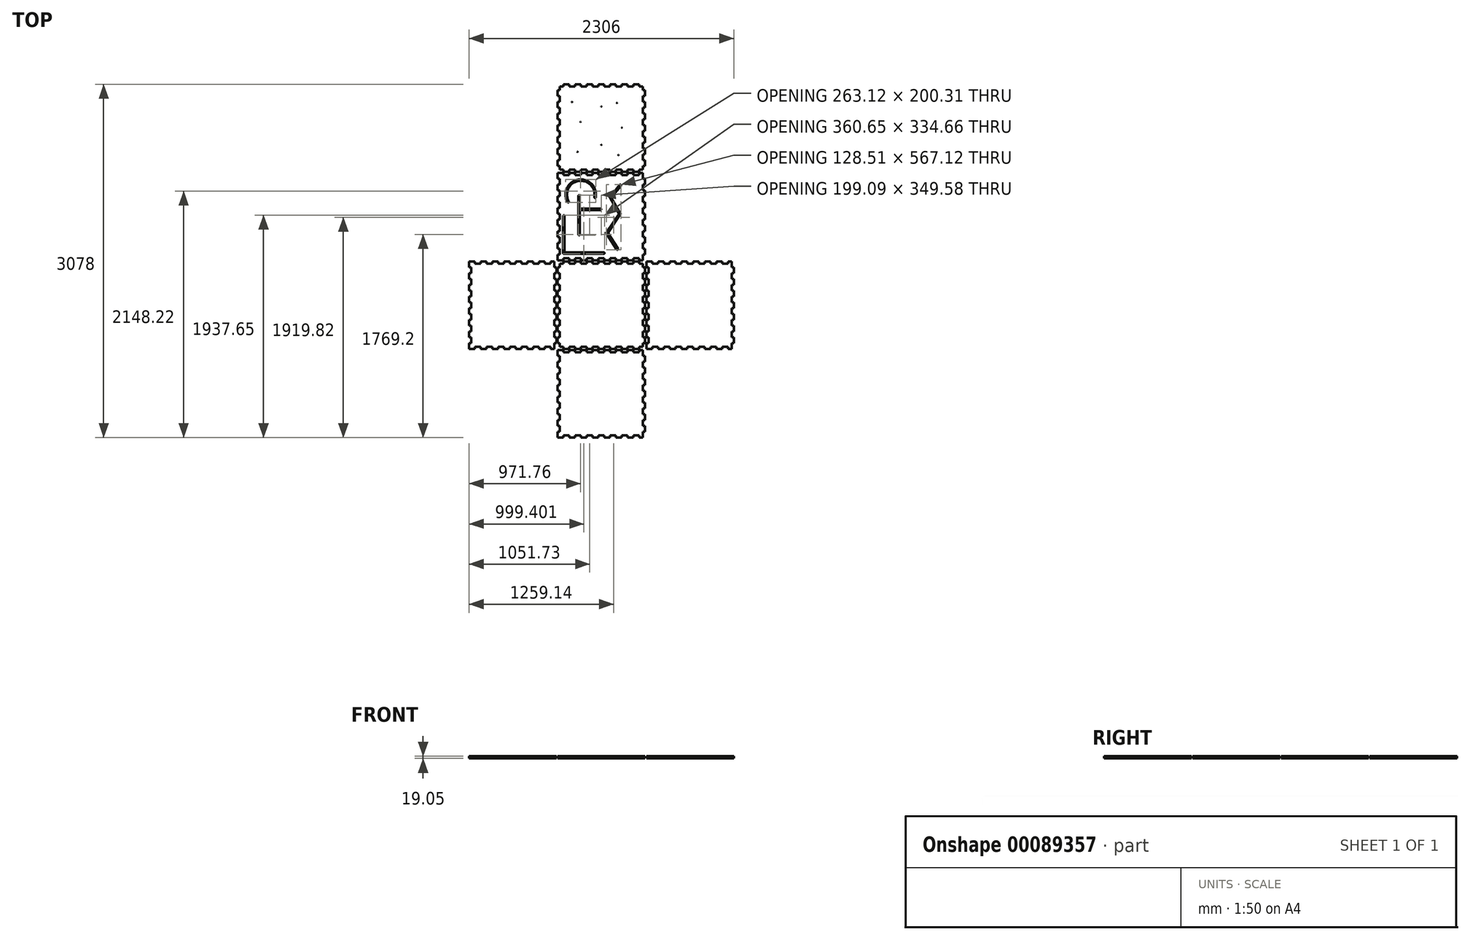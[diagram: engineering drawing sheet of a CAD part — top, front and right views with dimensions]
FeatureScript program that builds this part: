
annotation { "Feature Type Name" : "Feature", "Feature Type Description" : "" }
export const myFeature = defineFeature(function(context is Context, id is Id, definition is map)
    precondition{}
    {
        {
            var Q0;
            Q0=qCreatedBy(makeId("Top.planeOp"),FACE);
            var sketch = newSketch(context, id + "F0", { "sketchPlane" : qUnion([Q0])});
            skLineSegment(sketch, "E0", {"start": v(-381, -1539) * mm, "end": v(-330.2, -1539) * mm});
            skLineSegment(sketch, "E1", {"start": v(-330.2, -1519.95) * mm, "end": v(-330.2, -1539) * mm});
            skLineSegment(sketch, "E2", {"start": v(-330.2, -1519.95) * mm, "end": v(-279.4, -1519.95) * mm});
            skLineSegment(sketch, "E3", {"start": v(-279.4, -1519.95) * mm, "end": v(-279.4, -1539) * mm});
            skLineSegment(sketch, "E4", {"start": v(-279.4, -1539) * mm, "end": v(-228.6, -1539) * mm});
            skLineSegment(sketch, "E5", {"start": v(-228.6, -1519.95) * mm, "end": v(-228.6, -1539) * mm});
            skLineSegment(sketch, "E6", {"start": v(-228.6, -1519.95) * mm, "end": v(-177.8, -1519.95) * mm});
            skLineSegment(sketch, "E7", {"start": v(-177.8, -1519.95) * mm, "end": v(-177.8, -1539) * mm});
            skLineSegment(sketch, "E8", {"start": v(-177.8, -1539) * mm, "end": v(-127, -1539) * mm});
            skLineSegment(sketch, "E9", {"start": v(-127, -1519.95) * mm, "end": v(-127, -1539) * mm});
            skLineSegment(sketch, "E10", {"start": v(-127, -1519.95) * mm, "end": v(-76.2, -1519.95) * mm});
            skLineSegment(sketch, "E11", {"start": v(-76.2, -1519.95) * mm, "end": v(-76.2, -1539) * mm});
            skLineSegment(sketch, "E12", {"start": v(-76.2, -1539) * mm, "end": v(-25.4, -1539) * mm});
            skLineSegment(sketch, "E13", {"start": v(-25.4, -1519.95) * mm, "end": v(-25.4, -1539) * mm});
            skLineSegment(sketch, "E14", {"start": v(-25.4, -1519.95) * mm, "end": v(25.4, -1519.95) * mm});
            skLineSegment(sketch, "E15", {"start": v(25.4, -1519.95) * mm, "end": v(25.4, -1539) * mm});
            skLineSegment(sketch, "E16", {"start": v(25.4, -1539) * mm, "end": v(76.2, -1539) * mm});
            skLineSegment(sketch, "E17", {"start": v(76.2, -1519.95) * mm, "end": v(76.2, -1539) * mm});
            skLineSegment(sketch, "E18", {"start": v(76.2, -1519.95) * mm, "end": v(127, -1519.95) * mm});
            skLineSegment(sketch, "E19", {"start": v(127, -1519.95) * mm, "end": v(127, -1539) * mm});
            skLineSegment(sketch, "E20", {"start": v(127, -1539) * mm, "end": v(177.8, -1539) * mm});
            skLineSegment(sketch, "E21", {"start": v(177.8, -1519.95) * mm, "end": v(177.8, -1539) * mm});
            skLineSegment(sketch, "E22", {"start": v(177.8, -1519.95) * mm, "end": v(228.6, -1519.95) * mm});
            skLineSegment(sketch, "E23", {"start": v(228.6, -1519.95) * mm, "end": v(228.6, -1539) * mm});
            skLineSegment(sketch, "E24", {"start": v(228.6, -1539) * mm, "end": v(279.4, -1539) * mm});
            skLineSegment(sketch, "E25", {"start": v(279.4, -1519.95) * mm, "end": v(279.4, -1539) * mm});
            skLineSegment(sketch, "E26", {"start": v(279.4, -1519.95) * mm, "end": v(330.2, -1519.95) * mm});
            skLineSegment(sketch, "E27", {"start": v(330.2, -1519.95) * mm, "end": v(330.2, -1539) * mm});
            skLineSegment(sketch, "E28", {"start": v(330.2, -1539) * mm, "end": v(361.95, -1539) * mm});
            skLineSegment(sketch, "E29", {"start": v(-381, -777) * mm, "end": v(-330.2, -777) * mm});
            skLineSegment(sketch, "E30", {"start": v(-330.2, -777) * mm, "end": v(-330.2, -796.05) * mm});
            skLineSegment(sketch, "E31", {"start": v(-330.2, -796.05) * mm, "end": v(-279.4, -796.05) * mm});
            skLineSegment(sketch, "E32", {"start": v(-279.4, -777) * mm, "end": v(-279.4, -796.05) * mm});
            skLineSegment(sketch, "E33", {"start": v(-279.4, -777) * mm, "end": v(-228.6, -777) * mm});
            skLineSegment(sketch, "E34", {"start": v(-228.6, -777) * mm, "end": v(-228.6, -796.05) * mm});
            skLineSegment(sketch, "E35", {"start": v(-228.6, -796.05) * mm, "end": v(-177.8, -796.05) * mm});
            skLineSegment(sketch, "E36", {"start": v(-177.8, -777) * mm, "end": v(-177.8, -796.05) * mm});
            skLineSegment(sketch, "E37", {"start": v(-177.8, -777) * mm, "end": v(-127, -777) * mm});
            skLineSegment(sketch, "E38", {"start": v(-127, -777) * mm, "end": v(-127, -796.05) * mm});
            skLineSegment(sketch, "E39", {"start": v(-127, -796.05) * mm, "end": v(-76.2, -796.05) * mm});
            skLineSegment(sketch, "E40", {"start": v(-76.2, -777) * mm, "end": v(-76.2, -796.05) * mm});
            skLineSegment(sketch, "E41", {"start": v(-76.2, -777) * mm, "end": v(-25.4, -777) * mm});
            skLineSegment(sketch, "E42", {"start": v(-25.4, -777) * mm, "end": v(-25.4, -796.05) * mm});
            skLineSegment(sketch, "E43", {"start": v(-25.4, -796.05) * mm, "end": v(25.4, -796.05) * mm});
            skLineSegment(sketch, "E44", {"start": v(25.4, -777) * mm, "end": v(25.4, -796.05) * mm});
            skLineSegment(sketch, "E45", {"start": v(25.4, -777) * mm, "end": v(76.2, -777) * mm});
            skLineSegment(sketch, "E46", {"start": v(76.2, -777) * mm, "end": v(76.2, -796.05) * mm});
            skLineSegment(sketch, "E47", {"start": v(76.2, -796.05) * mm, "end": v(127, -796.05) * mm});
            skLineSegment(sketch, "E48", {"start": v(127, -777) * mm, "end": v(127, -796.05) * mm});
            skLineSegment(sketch, "E49", {"start": v(127, -777) * mm, "end": v(177.8, -777) * mm});
            skLineSegment(sketch, "E50", {"start": v(177.8, -777) * mm, "end": v(177.8, -796.05) * mm});
            skLineSegment(sketch, "E51", {"start": v(177.8, -796.05) * mm, "end": v(228.6, -796.05) * mm});
            skLineSegment(sketch, "E52", {"start": v(228.6, -777) * mm, "end": v(228.6, -796.05) * mm});
            skLineSegment(sketch, "E53", {"start": v(228.6, -777) * mm, "end": v(279.4, -777) * mm});
            skLineSegment(sketch, "E54", {"start": v(279.4, -777) * mm, "end": v(279.4, -796.05) * mm});
            skLineSegment(sketch, "E55", {"start": v(279.4, -796.05) * mm, "end": v(330.2, -796.05) * mm});
            skLineSegment(sketch, "E56", {"start": v(330.2, -777) * mm, "end": v(330.2, -796.05) * mm});
            skLineSegment(sketch, "E57", {"start": v(330.2, -777) * mm, "end": v(361.95, -777) * mm});
            skLineSegment(sketch, "E58", {"start": v(-381, -1539) * mm, "end": v(-381, -1488.2) * mm});
            skLineSegment(sketch, "E59", {"start": v(-361.95, -1488.2) * mm, "end": v(-381, -1488.2) * mm});
            skLineSegment(sketch, "E60", {"start": v(-361.95, -1488.2) * mm, "end": v(-361.95, -1437.4) * mm});
            skLineSegment(sketch, "E61", {"start": v(-361.95, -1437.4) * mm, "end": v(-381, -1437.4) * mm});
            skLineSegment(sketch, "E62", {"start": v(-381, -1437.4) * mm, "end": v(-381, -1386.6) * mm});
            skLineSegment(sketch, "E63", {"start": v(-361.95, -1386.6) * mm, "end": v(-381, -1386.6) * mm});
            skLineSegment(sketch, "E64", {"start": v(-361.95, -1386.6) * mm, "end": v(-361.95, -1335.8) * mm});
            skLineSegment(sketch, "E65", {"start": v(-361.95, -1335.8) * mm, "end": v(-381, -1335.8) * mm});
            skLineSegment(sketch, "E66", {"start": v(-381, -1335.8) * mm, "end": v(-381, -1285) * mm});
            skLineSegment(sketch, "E67", {"start": v(-361.95, -1285) * mm, "end": v(-381, -1285) * mm});
            skLineSegment(sketch, "E68", {"start": v(-361.95, -1285) * mm, "end": v(-361.95, -1234.2) * mm});
            skLineSegment(sketch, "E69", {"start": v(-361.95, -1234.2) * mm, "end": v(-381, -1234.2) * mm});
            skLineSegment(sketch, "E70", {"start": v(-381, -1234.2) * mm, "end": v(-381, -1183.4) * mm});
            skLineSegment(sketch, "E71", {"start": v(-361.95, -1183.4) * mm, "end": v(-381, -1183.4) * mm});
            skLineSegment(sketch, "E72", {"start": v(-361.95, -1183.4) * mm, "end": v(-361.95, -1132.6) * mm});
            skLineSegment(sketch, "E73", {"start": v(-361.95, -1132.6) * mm, "end": v(-381, -1132.6) * mm});
            skLineSegment(sketch, "E74", {"start": v(-381, -1132.6) * mm, "end": v(-381, -1081.8) * mm});
            skLineSegment(sketch, "E75", {"start": v(-361.95, -1081.8) * mm, "end": v(-381, -1081.8) * mm});
            skLineSegment(sketch, "E76", {"start": v(-361.95, -1081.8) * mm, "end": v(-361.95, -1031) * mm});
            skLineSegment(sketch, "E77", {"start": v(-361.95, -1031) * mm, "end": v(-381, -1031) * mm});
            skLineSegment(sketch, "E78", {"start": v(-381, -1031) * mm, "end": v(-381, -980.2) * mm});
            skLineSegment(sketch, "E79", {"start": v(-361.95, -980.2) * mm, "end": v(-381, -980.2) * mm});
            skLineSegment(sketch, "E80", {"start": v(-361.95, -980.2) * mm, "end": v(-361.95, -929.4) * mm});
            skLineSegment(sketch, "E81", {"start": v(-361.95, -929.4) * mm, "end": v(-381, -929.4) * mm});
            skLineSegment(sketch, "E82", {"start": v(-381, -929.4) * mm, "end": v(-381, -878.6) * mm});
            skLineSegment(sketch, "E83", {"start": v(-361.95, -878.6) * mm, "end": v(-381, -878.6) * mm});
            skLineSegment(sketch, "E84", {"start": v(-361.95, -878.6) * mm, "end": v(-361.95, -827.8) * mm});
            skLineSegment(sketch, "E85", {"start": v(-361.95, -827.8) * mm, "end": v(-381, -827.8) * mm});
            skLineSegment(sketch, "E86", {"start": v(-381, -827.8) * mm, "end": v(-381, -777) * mm});
            skLineSegment(sketch, "E87", {"start": v(361.95, -1539) * mm, "end": v(361.95, -1488.2) * mm});
            skLineSegment(sketch, "E88", {"start": v(381, -1488.2) * mm, "end": v(361.95, -1488.2) * mm});
            skLineSegment(sketch, "E89", {"start": v(381, -1488.2) * mm, "end": v(381, -1437.4) * mm});
            skLineSegment(sketch, "E90", {"start": v(381, -1437.4) * mm, "end": v(361.95, -1437.4) * mm});
            skLineSegment(sketch, "E91", {"start": v(361.95, -1437.4) * mm, "end": v(361.95, -1386.6) * mm});
            skLineSegment(sketch, "E92", {"start": v(381, -1386.6) * mm, "end": v(361.95, -1386.6) * mm});
            skLineSegment(sketch, "E93", {"start": v(381, -1386.6) * mm, "end": v(381, -1335.8) * mm});
            skLineSegment(sketch, "E94", {"start": v(381, -1335.8) * mm, "end": v(361.95, -1335.8) * mm});
            skLineSegment(sketch, "E95", {"start": v(361.95, -1335.8) * mm, "end": v(361.95, -1285) * mm});
            skLineSegment(sketch, "E96", {"start": v(381, -1285) * mm, "end": v(361.95, -1285) * mm});
            skLineSegment(sketch, "E97", {"start": v(381, -1285) * mm, "end": v(381, -1234.2) * mm});
            skLineSegment(sketch, "E98", {"start": v(381, -1234.2) * mm, "end": v(361.95, -1234.2) * mm});
            skLineSegment(sketch, "E99", {"start": v(361.95, -1234.2) * mm, "end": v(361.95, -1183.4) * mm});
            skLineSegment(sketch, "E100", {"start": v(381, -1183.4) * mm, "end": v(361.95, -1183.4) * mm});
            skLineSegment(sketch, "E101", {"start": v(381, -1183.4) * mm, "end": v(381, -1132.6) * mm});
            skLineSegment(sketch, "E102", {"start": v(381, -1132.6) * mm, "end": v(361.95, -1132.6) * mm});
            skLineSegment(sketch, "E103", {"start": v(361.95, -1132.6) * mm, "end": v(361.95, -1081.8) * mm});
            skLineSegment(sketch, "E104", {"start": v(381, -1081.8) * mm, "end": v(361.95, -1081.8) * mm});
            skLineSegment(sketch, "E105", {"start": v(381, -1081.8) * mm, "end": v(381, -1031) * mm});
            skLineSegment(sketch, "E106", {"start": v(381, -1031) * mm, "end": v(361.95, -1031) * mm});
            skLineSegment(sketch, "E107", {"start": v(361.95, -1031) * mm, "end": v(361.95, -980.2) * mm});
            skLineSegment(sketch, "E108", {"start": v(381, -980.2) * mm, "end": v(361.95, -980.2) * mm});
            skLineSegment(sketch, "E109", {"start": v(381, -980.2) * mm, "end": v(381, -929.4) * mm});
            skLineSegment(sketch, "E110", {"start": v(381, -929.4) * mm, "end": v(361.95, -929.4) * mm});
            skLineSegment(sketch, "E111", {"start": v(361.95, -929.4) * mm, "end": v(361.95, -878.6) * mm});
            skLineSegment(sketch, "E112", {"start": v(381, -878.6) * mm, "end": v(361.95, -878.6) * mm});
            skLineSegment(sketch, "E113", {"start": v(381, -878.6) * mm, "end": v(381, -827.8) * mm});
            skLineSegment(sketch, "E114", {"start": v(381, -827.8) * mm, "end": v(361.95, -827.8) * mm});
            skLineSegment(sketch, "E115", {"start": v(361.95, -827.8) * mm, "end": v(361.95, -777) * mm});
            skLineSegment(sketch, "E116", {"start": v(-1153, -767) * mm, "end": v(-1102.2, -767) * mm});
            skLineSegment(sketch, "E117", {"start": v(-1102.2, -747.95) * mm, "end": v(-1102.2, -767) * mm});
            skLineSegment(sketch, "E118", {"start": v(-1102.2, -747.95) * mm, "end": v(-1051.4, -747.95) * mm});
            skLineSegment(sketch, "E119", {"start": v(-1051.4, -747.95) * mm, "end": v(-1051.4, -767) * mm});
            skLineSegment(sketch, "E120", {"start": v(-1051.4, -767) * mm, "end": v(-1000.6, -767) * mm});
            skLineSegment(sketch, "E121", {"start": v(-1000.6, -747.95) * mm, "end": v(-1000.6, -767) * mm});
            skLineSegment(sketch, "E122", {"start": v(-1000.6, -747.95) * mm, "end": v(-949.8, -747.95) * mm});
            skLineSegment(sketch, "E123", {"start": v(-949.8, -747.95) * mm, "end": v(-949.8, -767) * mm});
            skLineSegment(sketch, "E124", {"start": v(-949.8, -767) * mm, "end": v(-899, -767) * mm});
            skLineSegment(sketch, "E125", {"start": v(-899, -747.95) * mm, "end": v(-899, -767) * mm});
            skLineSegment(sketch, "E126", {"start": v(-899, -747.95) * mm, "end": v(-848.2, -747.95) * mm});
            skLineSegment(sketch, "E127", {"start": v(-848.2, -747.95) * mm, "end": v(-848.2, -767) * mm});
            skLineSegment(sketch, "E128", {"start": v(-848.2, -767) * mm, "end": v(-797.4, -767) * mm});
            skLineSegment(sketch, "E129", {"start": v(-797.4, -747.95) * mm, "end": v(-797.4, -767) * mm});
            skLineSegment(sketch, "E130", {"start": v(-797.4, -747.95) * mm, "end": v(-746.6, -747.95) * mm});
            skLineSegment(sketch, "E131", {"start": v(-746.6, -747.95) * mm, "end": v(-746.6, -767) * mm});
            skLineSegment(sketch, "E132", {"start": v(-746.6, -767) * mm, "end": v(-695.8, -767) * mm});
            skLineSegment(sketch, "E133", {"start": v(-695.8, -747.95) * mm, "end": v(-695.8, -767) * mm});
            skLineSegment(sketch, "E134", {"start": v(-695.8, -747.95) * mm, "end": v(-645, -747.95) * mm});
            skLineSegment(sketch, "E135", {"start": v(-645, -747.95) * mm, "end": v(-645, -767) * mm});
            skLineSegment(sketch, "E136", {"start": v(-645, -767) * mm, "end": v(-594.2, -767) * mm});
            skLineSegment(sketch, "E137", {"start": v(-594.2, -747.95) * mm, "end": v(-594.2, -767) * mm});
            skLineSegment(sketch, "E138", {"start": v(-594.2, -747.95) * mm, "end": v(-543.4, -747.95) * mm});
            skLineSegment(sketch, "E139", {"start": v(-543.4, -747.95) * mm, "end": v(-543.4, -767) * mm});
            skLineSegment(sketch, "E140", {"start": v(-543.4, -767) * mm, "end": v(-492.6, -767) * mm});
            skLineSegment(sketch, "E141", {"start": v(-492.6, -747.95) * mm, "end": v(-492.6, -767) * mm});
            skLineSegment(sketch, "E142", {"start": v(-492.6, -747.95) * mm, "end": v(-441.8, -747.95) * mm});
            skLineSegment(sketch, "E143", {"start": v(-441.8, -747.95) * mm, "end": v(-441.8, -767) * mm});
            skLineSegment(sketch, "E144", {"start": v(-441.8, -767) * mm, "end": v(-410.05, -767) * mm});
            skLineSegment(sketch, "E145", {"start": v(-1153, -5) * mm, "end": v(-1102.2, -5) * mm});
            skLineSegment(sketch, "E146", {"start": v(-1102.2, -5) * mm, "end": v(-1102.2, -24.05) * mm});
            skLineSegment(sketch, "E147", {"start": v(-1102.2, -24.05) * mm, "end": v(-1051.4, -24.05) * mm});
            skLineSegment(sketch, "E148", {"start": v(-1051.4, -5) * mm, "end": v(-1051.4, -24.05) * mm});
            skLineSegment(sketch, "E149", {"start": v(-1051.4, -5) * mm, "end": v(-1000.6, -5) * mm});
            skLineSegment(sketch, "E150", {"start": v(-1000.6, -5) * mm, "end": v(-1000.6, -24.05) * mm});
            skLineSegment(sketch, "E151", {"start": v(-1000.6, -24.05) * mm, "end": v(-949.8, -24.05) * mm});
            skLineSegment(sketch, "E152", {"start": v(-949.8, -5) * mm, "end": v(-949.8, -24.05) * mm});
            skLineSegment(sketch, "E153", {"start": v(-949.8, -5) * mm, "end": v(-899, -5) * mm});
            skLineSegment(sketch, "E154", {"start": v(-899, -5) * mm, "end": v(-899, -24.05) * mm});
            skLineSegment(sketch, "E155", {"start": v(-899, -24.05) * mm, "end": v(-848.2, -24.05) * mm});
            skLineSegment(sketch, "E156", {"start": v(-848.2, -5) * mm, "end": v(-848.2, -24.05) * mm});
            skLineSegment(sketch, "E157", {"start": v(-848.2, -5) * mm, "end": v(-797.4, -5) * mm});
            skLineSegment(sketch, "E158", {"start": v(-797.4, -5) * mm, "end": v(-797.4, -24.05) * mm});
            skLineSegment(sketch, "E159", {"start": v(-797.4, -24.05) * mm, "end": v(-746.6, -24.05) * mm});
            skLineSegment(sketch, "E160", {"start": v(-746.6, -5) * mm, "end": v(-746.6, -24.05) * mm});
            skLineSegment(sketch, "E161", {"start": v(-746.6, -5) * mm, "end": v(-695.8, -5) * mm});
            skLineSegment(sketch, "E162", {"start": v(-695.8, -5) * mm, "end": v(-695.8, -24.05) * mm});
            skLineSegment(sketch, "E163", {"start": v(-695.8, -24.05) * mm, "end": v(-645, -24.05) * mm});
            skLineSegment(sketch, "E164", {"start": v(-645, -5) * mm, "end": v(-645, -24.05) * mm});
            skLineSegment(sketch, "E165", {"start": v(-645, -5) * mm, "end": v(-594.2, -5) * mm});
            skLineSegment(sketch, "E166", {"start": v(-594.2, -5) * mm, "end": v(-594.2, -24.05) * mm});
            skLineSegment(sketch, "E167", {"start": v(-594.2, -24.05) * mm, "end": v(-543.4, -24.05) * mm});
            skLineSegment(sketch, "E168", {"start": v(-543.4, -5) * mm, "end": v(-543.4, -24.05) * mm});
            skLineSegment(sketch, "E169", {"start": v(-543.4, -5) * mm, "end": v(-492.6, -5) * mm});
            skLineSegment(sketch, "E170", {"start": v(-492.6, -5) * mm, "end": v(-492.6, -24.05) * mm});
            skLineSegment(sketch, "E171", {"start": v(-492.6, -24.05) * mm, "end": v(-441.8, -24.05) * mm});
            skLineSegment(sketch, "E172", {"start": v(-441.8, -5) * mm, "end": v(-441.8, -24.05) * mm});
            skLineSegment(sketch, "E173", {"start": v(-441.8, -5) * mm, "end": v(-410.05, -5) * mm});
            skLineSegment(sketch, "E174", {"start": v(-1153, -767) * mm, "end": v(-1153, -716.2) * mm});
            skLineSegment(sketch, "E175", {"start": v(-1133.95, -716.2) * mm, "end": v(-1153, -716.2) * mm});
            skLineSegment(sketch, "E176", {"start": v(-1133.95, -716.2) * mm, "end": v(-1133.95, -665.4) * mm});
            skLineSegment(sketch, "E177", {"start": v(-1133.95, -665.4) * mm, "end": v(-1153, -665.4) * mm});
            skLineSegment(sketch, "E178", {"start": v(-1153, -665.4) * mm, "end": v(-1153, -614.6) * mm});
            skLineSegment(sketch, "E179", {"start": v(-1133.95, -614.6) * mm, "end": v(-1153, -614.6) * mm});
            skLineSegment(sketch, "E180", {"start": v(-1133.95, -614.6) * mm, "end": v(-1133.95, -563.8) * mm});
            skLineSegment(sketch, "E181", {"start": v(-1133.95, -563.8) * mm, "end": v(-1153, -563.8) * mm});
            skLineSegment(sketch, "E182", {"start": v(-1153, -563.8) * mm, "end": v(-1153, -513) * mm});
            skLineSegment(sketch, "E183", {"start": v(-1133.95, -513) * mm, "end": v(-1153, -513) * mm});
            skLineSegment(sketch, "E184", {"start": v(-1133.95, -513) * mm, "end": v(-1133.95, -462.2) * mm});
            skLineSegment(sketch, "E185", {"start": v(-1133.95, -462.2) * mm, "end": v(-1153, -462.2) * mm});
            skLineSegment(sketch, "E186", {"start": v(-1153, -462.2) * mm, "end": v(-1153, -411.4) * mm});
            skLineSegment(sketch, "E187", {"start": v(-1133.95, -411.4) * mm, "end": v(-1153, -411.4) * mm});
            skLineSegment(sketch, "E188", {"start": v(-1133.95, -411.4) * mm, "end": v(-1133.95, -360.6) * mm});
            skLineSegment(sketch, "E189", {"start": v(-1133.95, -360.6) * mm, "end": v(-1153, -360.6) * mm});
            skLineSegment(sketch, "E190", {"start": v(-1153, -360.6) * mm, "end": v(-1153, -309.8) * mm});
            skLineSegment(sketch, "E191", {"start": v(-1133.95, -309.8) * mm, "end": v(-1153, -309.8) * mm});
            skLineSegment(sketch, "E192", {"start": v(-1133.95, -309.8) * mm, "end": v(-1133.95, -259) * mm});
            skLineSegment(sketch, "E193", {"start": v(-1133.95, -259) * mm, "end": v(-1153, -259) * mm});
            skLineSegment(sketch, "E194", {"start": v(-1153, -259) * mm, "end": v(-1153, -208.2) * mm});
            skLineSegment(sketch, "E195", {"start": v(-1133.95, -208.2) * mm, "end": v(-1153, -208.2) * mm});
            skLineSegment(sketch, "E196", {"start": v(-1133.95, -208.2) * mm, "end": v(-1133.95, -157.4) * mm});
            skLineSegment(sketch, "E197", {"start": v(-1133.95, -157.4) * mm, "end": v(-1153, -157.4) * mm});
            skLineSegment(sketch, "E198", {"start": v(-1153, -157.4) * mm, "end": v(-1153, -106.6) * mm});
            skLineSegment(sketch, "E199", {"start": v(-1133.95, -106.6) * mm, "end": v(-1153, -106.6) * mm});
            skLineSegment(sketch, "E200", {"start": v(-1133.95, -106.6) * mm, "end": v(-1133.95, -55.8) * mm});
            skLineSegment(sketch, "E201", {"start": v(-1133.95, -55.8) * mm, "end": v(-1153, -55.8) * mm});
            skLineSegment(sketch, "E202", {"start": v(-1153, -55.8) * mm, "end": v(-1153, -5) * mm});
            skLineSegment(sketch, "E203", {"start": v(-410.05, -767) * mm, "end": v(-410.05, -716.2) * mm});
            skLineSegment(sketch, "E204", {"start": v(-391, -716.2) * mm, "end": v(-410.05, -716.2) * mm});
            skLineSegment(sketch, "E205", {"start": v(-391, -716.2) * mm, "end": v(-391, -665.4) * mm});
            skLineSegment(sketch, "E206", {"start": v(-391, -665.4) * mm, "end": v(-410.05, -665.4) * mm});
            skLineSegment(sketch, "E207", {"start": v(-410.05, -665.4) * mm, "end": v(-410.05, -614.6) * mm});
            skLineSegment(sketch, "E208", {"start": v(-391, -614.6) * mm, "end": v(-410.05, -614.6) * mm});
            skLineSegment(sketch, "E209", {"start": v(-391, -614.6) * mm, "end": v(-391, -563.8) * mm});
            skLineSegment(sketch, "E210", {"start": v(-391, -563.8) * mm, "end": v(-410.05, -563.8) * mm});
            skLineSegment(sketch, "E211", {"start": v(-410.05, -563.8) * mm, "end": v(-410.05, -513) * mm});
            skLineSegment(sketch, "E212", {"start": v(-391, -513) * mm, "end": v(-410.05, -513) * mm});
            skLineSegment(sketch, "E213", {"start": v(-391, -513) * mm, "end": v(-391, -462.2) * mm});
            skLineSegment(sketch, "E214", {"start": v(-391, -462.2) * mm, "end": v(-410.05, -462.2) * mm});
            skLineSegment(sketch, "E215", {"start": v(-410.05, -462.2) * mm, "end": v(-410.05, -411.4) * mm});
            skLineSegment(sketch, "E216", {"start": v(-391, -411.4) * mm, "end": v(-410.05, -411.4) * mm});
            skLineSegment(sketch, "E217", {"start": v(-391, -411.4) * mm, "end": v(-391, -360.6) * mm});
            skLineSegment(sketch, "E218", {"start": v(-391, -360.6) * mm, "end": v(-410.05, -360.6) * mm});
            skLineSegment(sketch, "E219", {"start": v(-410.05, -360.6) * mm, "end": v(-410.05, -309.8) * mm});
            skLineSegment(sketch, "E220", {"start": v(-391, -309.8) * mm, "end": v(-410.05, -309.8) * mm});
            skLineSegment(sketch, "E221", {"start": v(-391, -309.8) * mm, "end": v(-391, -259) * mm});
            skLineSegment(sketch, "E222", {"start": v(-391, -259) * mm, "end": v(-410.05, -259) * mm});
            skLineSegment(sketch, "E223", {"start": v(-410.05, -259) * mm, "end": v(-410.05, -208.2) * mm});
            skLineSegment(sketch, "E224", {"start": v(-391, -208.2) * mm, "end": v(-410.05, -208.2) * mm});
            skLineSegment(sketch, "E225", {"start": v(-391, -208.2) * mm, "end": v(-391, -157.4) * mm});
            skLineSegment(sketch, "E226", {"start": v(-391, -157.4) * mm, "end": v(-410.05, -157.4) * mm});
            skLineSegment(sketch, "E227", {"start": v(-410.05, -157.4) * mm, "end": v(-410.05, -106.6) * mm});
            skLineSegment(sketch, "E228", {"start": v(-391, -106.6) * mm, "end": v(-410.05, -106.6) * mm});
            skLineSegment(sketch, "E229", {"start": v(-391, -106.6) * mm, "end": v(-391, -55.8) * mm});
            skLineSegment(sketch, "E230", {"start": v(-391, -55.8) * mm, "end": v(-410.05, -55.8) * mm});
            skLineSegment(sketch, "E231", {"start": v(-410.05, -55.8) * mm, "end": v(-410.05, -5) * mm});
            skLineSegment(sketch, "E232", {"start": v(-361.95, -747.95) * mm, "end": v(-330.2, -747.95) * mm});
            skLineSegment(sketch, "E233", {"start": v(-330.2, -747.95) * mm, "end": v(-330.2, -767) * mm});
            skLineSegment(sketch, "E234", {"start": v(-330.2, -767) * mm, "end": v(-279.4, -767) * mm});
            skLineSegment(sketch, "E235", {"start": v(-279.4, -747.95) * mm, "end": v(-279.4, -767) * mm});
            skLineSegment(sketch, "E236", {"start": v(-279.4, -747.95) * mm, "end": v(-228.6, -747.95) * mm});
            skLineSegment(sketch, "E237", {"start": v(-228.6, -747.95) * mm, "end": v(-228.6, -767) * mm});
            skLineSegment(sketch, "E238", {"start": v(-228.6, -767) * mm, "end": v(-177.8, -767) * mm});
            skLineSegment(sketch, "E239", {"start": v(-177.8, -747.95) * mm, "end": v(-177.8, -767) * mm});
            skLineSegment(sketch, "E240", {"start": v(-177.8, -747.95) * mm, "end": v(-127, -747.95) * mm});
            skLineSegment(sketch, "E241", {"start": v(-127, -747.95) * mm, "end": v(-127, -767) * mm});
            skLineSegment(sketch, "E242", {"start": v(-127, -767) * mm, "end": v(-76.2, -767) * mm});
            skLineSegment(sketch, "E243", {"start": v(-76.2, -747.95) * mm, "end": v(-76.2, -767) * mm});
            skLineSegment(sketch, "E244", {"start": v(-76.2, -747.95) * mm, "end": v(-25.4, -747.95) * mm});
            skLineSegment(sketch, "E245", {"start": v(-25.4, -747.95) * mm, "end": v(-25.4, -767) * mm});
            skLineSegment(sketch, "E246", {"start": v(-25.4, -767) * mm, "end": v(25.4, -767) * mm});
            skLineSegment(sketch, "E247", {"start": v(25.4, -747.95) * mm, "end": v(25.4, -767) * mm});
            skLineSegment(sketch, "E248", {"start": v(25.4, -747.95) * mm, "end": v(76.2, -747.95) * mm});
            skLineSegment(sketch, "E249", {"start": v(76.2, -747.95) * mm, "end": v(76.2, -767) * mm});
            skLineSegment(sketch, "E250", {"start": v(76.2, -767) * mm, "end": v(127, -767) * mm});
            skLineSegment(sketch, "E251", {"start": v(127, -747.95) * mm, "end": v(127, -767) * mm});
            skLineSegment(sketch, "E252", {"start": v(127, -747.95) * mm, "end": v(177.8, -747.95) * mm});
            skLineSegment(sketch, "E253", {"start": v(177.8, -747.95) * mm, "end": v(177.8, -767) * mm});
            skLineSegment(sketch, "E254", {"start": v(177.8, -767) * mm, "end": v(228.6, -767) * mm});
            skLineSegment(sketch, "E255", {"start": v(228.6, -747.95) * mm, "end": v(228.6, -767) * mm});
            skLineSegment(sketch, "E256", {"start": v(228.6, -747.95) * mm, "end": v(279.4, -747.95) * mm});
            skLineSegment(sketch, "E257", {"start": v(279.4, -747.95) * mm, "end": v(279.4, -767) * mm});
            skLineSegment(sketch, "E258", {"start": v(279.4, -767) * mm, "end": v(330.2, -767) * mm});
            skLineSegment(sketch, "E259", {"start": v(330.2, -747.95) * mm, "end": v(330.2, -767) * mm});
            skLineSegment(sketch, "E260", {"start": v(330.2, -747.95) * mm, "end": v(361.95, -747.95) * mm});
            skLineSegment(sketch, "E261", {"start": v(-361.95, -24.05) * mm, "end": v(-330.2, -24.05) * mm});
            skLineSegment(sketch, "E262", {"start": v(-330.2, -5) * mm, "end": v(-330.2, -24.05) * mm});
            skLineSegment(sketch, "E263", {"start": v(-330.2, -5) * mm, "end": v(-279.4, -5) * mm});
            skLineSegment(sketch, "E264", {"start": v(-279.4, -5) * mm, "end": v(-279.4, -24.05) * mm});
            skLineSegment(sketch, "E265", {"start": v(-279.4, -24.05) * mm, "end": v(-228.6, -24.05) * mm});
            skLineSegment(sketch, "E266", {"start": v(-228.6, -5) * mm, "end": v(-228.6, -24.05) * mm});
            skLineSegment(sketch, "E267", {"start": v(-228.6, -5) * mm, "end": v(-177.8, -5) * mm});
            skLineSegment(sketch, "E268", {"start": v(-177.8, -5) * mm, "end": v(-177.8, -24.05) * mm});
            skLineSegment(sketch, "E269", {"start": v(-177.8, -24.05) * mm, "end": v(-127, -24.05) * mm});
            skLineSegment(sketch, "E270", {"start": v(-127, -5) * mm, "end": v(-127, -24.05) * mm});
            skLineSegment(sketch, "E271", {"start": v(-127, -5) * mm, "end": v(-76.2, -5) * mm});
            skLineSegment(sketch, "E272", {"start": v(-76.2, -5) * mm, "end": v(-76.2, -24.05) * mm});
            skLineSegment(sketch, "E273", {"start": v(-76.2, -24.05) * mm, "end": v(-25.4, -24.05) * mm});
            skLineSegment(sketch, "E274", {"start": v(-25.4, -5) * mm, "end": v(-25.4, -24.05) * mm});
            skLineSegment(sketch, "E275", {"start": v(-25.4, -5) * mm, "end": v(25.4, -5) * mm});
            skLineSegment(sketch, "E276", {"start": v(25.4, -5) * mm, "end": v(25.4, -24.05) * mm});
            skLineSegment(sketch, "E277", {"start": v(25.4, -24.05) * mm, "end": v(76.2, -24.05) * mm});
            skLineSegment(sketch, "E278", {"start": v(76.2, -5) * mm, "end": v(76.2, -24.05) * mm});
            skLineSegment(sketch, "E279", {"start": v(76.2, -5) * mm, "end": v(127, -5) * mm});
            skLineSegment(sketch, "E280", {"start": v(127, -5) * mm, "end": v(127, -24.05) * mm});
            skLineSegment(sketch, "E281", {"start": v(127, -24.05) * mm, "end": v(177.8, -24.05) * mm});
            skLineSegment(sketch, "E282", {"start": v(177.8, -5) * mm, "end": v(177.8, -24.05) * mm});
            skLineSegment(sketch, "E283", {"start": v(177.8, -5) * mm, "end": v(228.6, -5) * mm});
            skLineSegment(sketch, "E284", {"start": v(228.6, -5) * mm, "end": v(228.6, -24.05) * mm});
            skLineSegment(sketch, "E285", {"start": v(228.6, -24.05) * mm, "end": v(279.4, -24.05) * mm});
            skLineSegment(sketch, "E286", {"start": v(279.4, -5) * mm, "end": v(279.4, -24.05) * mm});
            skLineSegment(sketch, "E287", {"start": v(279.4, -5) * mm, "end": v(330.2, -5) * mm});
            skLineSegment(sketch, "E288", {"start": v(330.2, -5) * mm, "end": v(330.2, -24.05) * mm});
            skLineSegment(sketch, "E289", {"start": v(330.2, -24.05) * mm, "end": v(361.95, -24.05) * mm});
            skLineSegment(sketch, "E290", {"start": v(-361.95, -747.95) * mm, "end": v(-361.95, -716.2) * mm});
            skLineSegment(sketch, "E291", {"start": v(-361.95, -716.2) * mm, "end": v(-381, -716.2) * mm});
            skLineSegment(sketch, "E292", {"start": v(-381, -716.2) * mm, "end": v(-381, -665.4) * mm});
            skLineSegment(sketch, "E293", {"start": v(-361.95, -665.4) * mm, "end": v(-381, -665.4) * mm});
            skLineSegment(sketch, "E294", {"start": v(-361.95, -665.4) * mm, "end": v(-361.95, -614.6) * mm});
            skLineSegment(sketch, "E295", {"start": v(-361.95, -614.6) * mm, "end": v(-381, -614.6) * mm});
            skLineSegment(sketch, "E296", {"start": v(-381, -614.6) * mm, "end": v(-381, -563.8) * mm});
            skLineSegment(sketch, "E297", {"start": v(-361.95, -563.8) * mm, "end": v(-381, -563.8) * mm});
            skLineSegment(sketch, "E298", {"start": v(-361.95, -563.8) * mm, "end": v(-361.95, -513) * mm});
            skLineSegment(sketch, "E299", {"start": v(-361.95, -513) * mm, "end": v(-381, -513) * mm});
            skLineSegment(sketch, "E300", {"start": v(-381, -513) * mm, "end": v(-381, -462.2) * mm});
            skLineSegment(sketch, "E301", {"start": v(-361.95, -462.2) * mm, "end": v(-381, -462.2) * mm});
            skLineSegment(sketch, "E302", {"start": v(-361.95, -462.2) * mm, "end": v(-361.95, -411.4) * mm});
            skLineSegment(sketch, "E303", {"start": v(-361.95, -411.4) * mm, "end": v(-381, -411.4) * mm});
            skLineSegment(sketch, "E304", {"start": v(-381, -411.4) * mm, "end": v(-381, -360.6) * mm});
            skLineSegment(sketch, "E305", {"start": v(-361.95, -360.6) * mm, "end": v(-381, -360.6) * mm});
            skLineSegment(sketch, "E306", {"start": v(-361.95, -360.6) * mm, "end": v(-361.95, -309.8) * mm});
            skLineSegment(sketch, "E307", {"start": v(-361.95, -309.8) * mm, "end": v(-381, -309.8) * mm});
            skLineSegment(sketch, "E308", {"start": v(-381, -309.8) * mm, "end": v(-381, -259) * mm});
            skLineSegment(sketch, "E309", {"start": v(-361.95, -259) * mm, "end": v(-381, -259) * mm});
            skLineSegment(sketch, "E310", {"start": v(-361.95, -259) * mm, "end": v(-361.95, -208.2) * mm});
            skLineSegment(sketch, "E311", {"start": v(-361.95, -208.2) * mm, "end": v(-381, -208.2) * mm});
            skLineSegment(sketch, "E312", {"start": v(-381, -208.2) * mm, "end": v(-381, -157.4) * mm});
            skLineSegment(sketch, "E313", {"start": v(-361.95, -157.4) * mm, "end": v(-381, -157.4) * mm});
            skLineSegment(sketch, "E314", {"start": v(-361.95, -157.4) * mm, "end": v(-361.95, -106.6) * mm});
            skLineSegment(sketch, "E315", {"start": v(-361.95, -106.6) * mm, "end": v(-381, -106.6) * mm});
            skLineSegment(sketch, "E316", {"start": v(-381, -106.6) * mm, "end": v(-381, -55.8) * mm});
            skLineSegment(sketch, "E317", {"start": v(-361.95, -55.8) * mm, "end": v(-381, -55.8) * mm});
            skLineSegment(sketch, "E318", {"start": v(-361.95, -55.8) * mm, "end": v(-361.95, -24.05) * mm});
            skLineSegment(sketch, "E319", {"start": v(361.95, -747.95) * mm, "end": v(361.95, -716.2) * mm});
            skLineSegment(sketch, "E320", {"start": v(381, -716.2) * mm, "end": v(361.95, -716.2) * mm});
            skLineSegment(sketch, "E321", {"start": v(381, -716.2) * mm, "end": v(381, -665.4) * mm});
            skLineSegment(sketch, "E322", {"start": v(381, -665.4) * mm, "end": v(361.95, -665.4) * mm});
            skLineSegment(sketch, "E323", {"start": v(361.95, -665.4) * mm, "end": v(361.95, -614.6) * mm});
            skLineSegment(sketch, "E324", {"start": v(381, -614.6) * mm, "end": v(361.95, -614.6) * mm});
            skLineSegment(sketch, "E325", {"start": v(381, -614.6) * mm, "end": v(381, -563.8) * mm});
            skLineSegment(sketch, "E326", {"start": v(381, -563.8) * mm, "end": v(361.95, -563.8) * mm});
            skLineSegment(sketch, "E327", {"start": v(361.95, -563.8) * mm, "end": v(361.95, -513) * mm});
            skLineSegment(sketch, "E328", {"start": v(381, -513) * mm, "end": v(361.95, -513) * mm});
            skLineSegment(sketch, "E329", {"start": v(381, -513) * mm, "end": v(381, -462.2) * mm});
            skLineSegment(sketch, "E330", {"start": v(381, -462.2) * mm, "end": v(361.95, -462.2) * mm});
            skLineSegment(sketch, "E331", {"start": v(361.95, -462.2) * mm, "end": v(361.95, -411.4) * mm});
            skLineSegment(sketch, "E332", {"start": v(381, -411.4) * mm, "end": v(361.95, -411.4) * mm});
            skLineSegment(sketch, "E333", {"start": v(381, -411.4) * mm, "end": v(381, -360.6) * mm});
            skLineSegment(sketch, "E334", {"start": v(381, -360.6) * mm, "end": v(361.95, -360.6) * mm});
            skLineSegment(sketch, "E335", {"start": v(361.95, -360.6) * mm, "end": v(361.95, -309.8) * mm});
            skLineSegment(sketch, "E336", {"start": v(381, -309.8) * mm, "end": v(361.95, -309.8) * mm});
            skLineSegment(sketch, "E337", {"start": v(381, -309.8) * mm, "end": v(381, -259) * mm});
            skLineSegment(sketch, "E338", {"start": v(381, -259) * mm, "end": v(361.95, -259) * mm});
            skLineSegment(sketch, "E339", {"start": v(361.95, -259) * mm, "end": v(361.95, -208.2) * mm});
            skLineSegment(sketch, "E340", {"start": v(381, -208.2) * mm, "end": v(361.95, -208.2) * mm});
            skLineSegment(sketch, "E341", {"start": v(381, -208.2) * mm, "end": v(381, -157.4) * mm});
            skLineSegment(sketch, "E342", {"start": v(381, -157.4) * mm, "end": v(361.95, -157.4) * mm});
            skLineSegment(sketch, "E343", {"start": v(361.95, -157.4) * mm, "end": v(361.95, -106.6) * mm});
            skLineSegment(sketch, "E344", {"start": v(381, -106.6) * mm, "end": v(361.95, -106.6) * mm});
            skLineSegment(sketch, "E345", {"start": v(381, -106.6) * mm, "end": v(381, -55.8) * mm});
            skLineSegment(sketch, "E346", {"start": v(381, -55.8) * mm, "end": v(361.95, -55.8) * mm});
            skLineSegment(sketch, "E347", {"start": v(361.95, -55.8) * mm, "end": v(361.95, -24.05) * mm});
            skLineSegment(sketch, "E348", {"start": v(391, -767) * mm, "end": v(441.8, -767) * mm});
            skLineSegment(sketch, "E349", {"start": v(441.8, -747.95) * mm, "end": v(441.8, -767) * mm});
            skLineSegment(sketch, "E350", {"start": v(441.8, -747.95) * mm, "end": v(492.6, -747.95) * mm});
            skLineSegment(sketch, "E351", {"start": v(492.6, -747.95) * mm, "end": v(492.6, -767) * mm});
            skLineSegment(sketch, "E352", {"start": v(492.6, -767) * mm, "end": v(543.4, -767) * mm});
            skLineSegment(sketch, "E353", {"start": v(543.4, -747.95) * mm, "end": v(543.4, -767) * mm});
            skLineSegment(sketch, "E354", {"start": v(543.4, -747.95) * mm, "end": v(594.2, -747.95) * mm});
            skLineSegment(sketch, "E355", {"start": v(594.2, -747.95) * mm, "end": v(594.2, -767) * mm});
            skLineSegment(sketch, "E356", {"start": v(594.2, -767) * mm, "end": v(645, -767) * mm});
            skLineSegment(sketch, "E357", {"start": v(645, -747.95) * mm, "end": v(645, -767) * mm});
            skLineSegment(sketch, "E358", {"start": v(645, -747.95) * mm, "end": v(695.8, -747.95) * mm});
            skLineSegment(sketch, "E359", {"start": v(695.8, -747.95) * mm, "end": v(695.8, -767) * mm});
            skLineSegment(sketch, "E360", {"start": v(695.8, -767) * mm, "end": v(746.6, -767) * mm});
            skLineSegment(sketch, "E361", {"start": v(746.6, -747.95) * mm, "end": v(746.6, -767) * mm});
            skLineSegment(sketch, "E362", {"start": v(746.6, -747.95) * mm, "end": v(797.4, -747.95) * mm});
            skLineSegment(sketch, "E363", {"start": v(797.4, -747.95) * mm, "end": v(797.4, -767) * mm});
            skLineSegment(sketch, "E364", {"start": v(797.4, -767) * mm, "end": v(848.2, -767) * mm});
            skLineSegment(sketch, "E365", {"start": v(848.2, -747.95) * mm, "end": v(848.2, -767) * mm});
            skLineSegment(sketch, "E366", {"start": v(848.2, -747.95) * mm, "end": v(899, -747.95) * mm});
            skLineSegment(sketch, "E367", {"start": v(899, -747.95) * mm, "end": v(899, -767) * mm});
            skLineSegment(sketch, "E368", {"start": v(899, -767) * mm, "end": v(949.8, -767) * mm});
            skLineSegment(sketch, "E369", {"start": v(949.8, -747.95) * mm, "end": v(949.8, -767) * mm});
            skLineSegment(sketch, "E370", {"start": v(949.8, -747.95) * mm, "end": v(1000.6, -747.95) * mm});
            skLineSegment(sketch, "E371", {"start": v(1000.6, -747.95) * mm, "end": v(1000.6, -767) * mm});
            skLineSegment(sketch, "E372", {"start": v(1000.6, -767) * mm, "end": v(1051.4, -767) * mm});
            skLineSegment(sketch, "E373", {"start": v(1051.4, -747.95) * mm, "end": v(1051.4, -767) * mm});
            skLineSegment(sketch, "E374", {"start": v(1051.4, -747.95) * mm, "end": v(1102.2, -747.95) * mm});
            skLineSegment(sketch, "E375", {"start": v(1102.2, -747.95) * mm, "end": v(1102.2, -767) * mm});
            skLineSegment(sketch, "E376", {"start": v(1102.2, -767) * mm, "end": v(1133.95, -767) * mm});
            skLineSegment(sketch, "E377", {"start": v(391, -5) * mm, "end": v(441.8, -5) * mm});
            skLineSegment(sketch, "E378", {"start": v(441.8, -5) * mm, "end": v(441.8, -24.05) * mm});
            skLineSegment(sketch, "E379", {"start": v(441.8, -24.05) * mm, "end": v(492.6, -24.05) * mm});
            skLineSegment(sketch, "E380", {"start": v(492.6, -5) * mm, "end": v(492.6, -24.05) * mm});
            skLineSegment(sketch, "E381", {"start": v(492.6, -5) * mm, "end": v(543.4, -5) * mm});
            skLineSegment(sketch, "E382", {"start": v(543.4, -5) * mm, "end": v(543.4, -24.05) * mm});
            skLineSegment(sketch, "E383", {"start": v(543.4, -24.05) * mm, "end": v(594.2, -24.05) * mm});
            skLineSegment(sketch, "E384", {"start": v(594.2, -5) * mm, "end": v(594.2, -24.05) * mm});
            skLineSegment(sketch, "E385", {"start": v(594.2, -5) * mm, "end": v(645, -5) * mm});
            skLineSegment(sketch, "E386", {"start": v(645, -5) * mm, "end": v(645, -24.05) * mm});
            skLineSegment(sketch, "E387", {"start": v(645, -24.05) * mm, "end": v(695.8, -24.05) * mm});
            skLineSegment(sketch, "E388", {"start": v(695.8, -5) * mm, "end": v(695.8, -24.05) * mm});
            skLineSegment(sketch, "E389", {"start": v(695.8, -5) * mm, "end": v(746.6, -5) * mm});
            skLineSegment(sketch, "E390", {"start": v(746.6, -5) * mm, "end": v(746.6, -24.05) * mm});
            skLineSegment(sketch, "E391", {"start": v(746.6, -24.05) * mm, "end": v(797.4, -24.05) * mm});
            skLineSegment(sketch, "E392", {"start": v(797.4, -5) * mm, "end": v(797.4, -24.05) * mm});
            skLineSegment(sketch, "E393", {"start": v(797.4, -5) * mm, "end": v(848.2, -5) * mm});
            skLineSegment(sketch, "E394", {"start": v(848.2, -5) * mm, "end": v(848.2, -24.05) * mm});
            skLineSegment(sketch, "E395", {"start": v(848.2, -24.05) * mm, "end": v(899, -24.05) * mm});
            skLineSegment(sketch, "E396", {"start": v(899, -5) * mm, "end": v(899, -24.05) * mm});
            skLineSegment(sketch, "E397", {"start": v(899, -5) * mm, "end": v(949.8, -5) * mm});
            skLineSegment(sketch, "E398", {"start": v(949.8, -5) * mm, "end": v(949.8, -24.05) * mm});
            skLineSegment(sketch, "E399", {"start": v(949.8, -24.05) * mm, "end": v(1000.6, -24.05) * mm});
            skLineSegment(sketch, "E400", {"start": v(1000.6, -5) * mm, "end": v(1000.6, -24.05) * mm});
            skLineSegment(sketch, "E401", {"start": v(1000.6, -5) * mm, "end": v(1051.4, -5) * mm});
            skLineSegment(sketch, "E402", {"start": v(1051.4, -5) * mm, "end": v(1051.4, -24.05) * mm});
            skLineSegment(sketch, "E403", {"start": v(1051.4, -24.05) * mm, "end": v(1102.2, -24.05) * mm});
            skLineSegment(sketch, "E404", {"start": v(1102.2, -5) * mm, "end": v(1102.2, -24.05) * mm});
            skLineSegment(sketch, "E405", {"start": v(1102.2, -5) * mm, "end": v(1133.95, -5) * mm});
            skLineSegment(sketch, "E406", {"start": v(391, -767) * mm, "end": v(391, -716.2) * mm});
            skLineSegment(sketch, "E407", {"start": v(410.05, -716.2) * mm, "end": v(391, -716.2) * mm});
            skLineSegment(sketch, "E408", {"start": v(410.05, -716.2) * mm, "end": v(410.05, -665.4) * mm});
            skLineSegment(sketch, "E409", {"start": v(410.05, -665.4) * mm, "end": v(391, -665.4) * mm});
            skLineSegment(sketch, "E410", {"start": v(391, -665.4) * mm, "end": v(391, -614.6) * mm});
            skLineSegment(sketch, "E411", {"start": v(410.05, -614.6) * mm, "end": v(391, -614.6) * mm});
            skLineSegment(sketch, "E412", {"start": v(410.05, -614.6) * mm, "end": v(410.05, -563.8) * mm});
            skLineSegment(sketch, "E413", {"start": v(410.05, -563.8) * mm, "end": v(391, -563.8) * mm});
            skLineSegment(sketch, "E414", {"start": v(391, -563.8) * mm, "end": v(391, -513) * mm});
            skLineSegment(sketch, "E415", {"start": v(410.05, -513) * mm, "end": v(391, -513) * mm});
            skLineSegment(sketch, "E416", {"start": v(410.05, -513) * mm, "end": v(410.05, -462.2) * mm});
            skLineSegment(sketch, "E417", {"start": v(410.05, -462.2) * mm, "end": v(391, -462.2) * mm});
            skLineSegment(sketch, "E418", {"start": v(391, -462.2) * mm, "end": v(391, -411.4) * mm});
            skLineSegment(sketch, "E419", {"start": v(410.05, -411.4) * mm, "end": v(391, -411.4) * mm});
            skLineSegment(sketch, "E420", {"start": v(410.05, -411.4) * mm, "end": v(410.05, -360.6) * mm});
            skLineSegment(sketch, "E421", {"start": v(410.05, -360.6) * mm, "end": v(391, -360.6) * mm});
            skLineSegment(sketch, "E422", {"start": v(391, -360.6) * mm, "end": v(391, -309.8) * mm});
            skLineSegment(sketch, "E423", {"start": v(410.05, -309.8) * mm, "end": v(391, -309.8) * mm});
            skLineSegment(sketch, "E424", {"start": v(410.05, -309.8) * mm, "end": v(410.05, -259) * mm});
            skLineSegment(sketch, "E425", {"start": v(410.05, -259) * mm, "end": v(391, -259) * mm});
            skLineSegment(sketch, "E426", {"start": v(391, -259) * mm, "end": v(391, -208.2) * mm});
            skLineSegment(sketch, "E427", {"start": v(410.05, -208.2) * mm, "end": v(391, -208.2) * mm});
            skLineSegment(sketch, "E428", {"start": v(410.05, -208.2) * mm, "end": v(410.05, -157.4) * mm});
            skLineSegment(sketch, "E429", {"start": v(410.05, -157.4) * mm, "end": v(391, -157.4) * mm});
            skLineSegment(sketch, "E430", {"start": v(391, -157.4) * mm, "end": v(391, -106.6) * mm});
            skLineSegment(sketch, "E431", {"start": v(410.05, -106.6) * mm, "end": v(391, -106.6) * mm});
            skLineSegment(sketch, "E432", {"start": v(410.05, -106.6) * mm, "end": v(410.05, -55.8) * mm});
            skLineSegment(sketch, "E433", {"start": v(410.05, -55.8) * mm, "end": v(391, -55.8) * mm});
            skLineSegment(sketch, "E434", {"start": v(391, -55.8) * mm, "end": v(391, -5) * mm});
            skLineSegment(sketch, "E435", {"start": v(1133.95, -767) * mm, "end": v(1133.95, -716.2) * mm});
            skLineSegment(sketch, "E436", {"start": v(1153, -716.2) * mm, "end": v(1133.95, -716.2) * mm});
            skLineSegment(sketch, "E437", {"start": v(1153, -716.2) * mm, "end": v(1153, -665.4) * mm});
            skLineSegment(sketch, "E438", {"start": v(1153, -665.4) * mm, "end": v(1133.95, -665.4) * mm});
            skLineSegment(sketch, "E439", {"start": v(1133.95, -665.4) * mm, "end": v(1133.95, -614.6) * mm});
            skLineSegment(sketch, "E440", {"start": v(1153, -614.6) * mm, "end": v(1133.95, -614.6) * mm});
            skLineSegment(sketch, "E441", {"start": v(1153, -614.6) * mm, "end": v(1153, -563.8) * mm});
            skLineSegment(sketch, "E442", {"start": v(1153, -563.8) * mm, "end": v(1133.95, -563.8) * mm});
            skLineSegment(sketch, "E443", {"start": v(1133.95, -563.8) * mm, "end": v(1133.95, -513) * mm});
            skLineSegment(sketch, "E444", {"start": v(1153, -513) * mm, "end": v(1133.95, -513) * mm});
            skLineSegment(sketch, "E445", {"start": v(1153, -513) * mm, "end": v(1153, -462.2) * mm});
            skLineSegment(sketch, "E446", {"start": v(1153, -462.2) * mm, "end": v(1133.95, -462.2) * mm});
            skLineSegment(sketch, "E447", {"start": v(1133.95, -462.2) * mm, "end": v(1133.95, -411.4) * mm});
            skLineSegment(sketch, "E448", {"start": v(1153, -411.4) * mm, "end": v(1133.95, -411.4) * mm});
            skLineSegment(sketch, "E449", {"start": v(1153, -411.4) * mm, "end": v(1153, -360.6) * mm});
            skLineSegment(sketch, "E450", {"start": v(1153, -360.6) * mm, "end": v(1133.95, -360.6) * mm});
            skLineSegment(sketch, "E451", {"start": v(1133.95, -360.6) * mm, "end": v(1133.95, -309.8) * mm});
            skLineSegment(sketch, "E452", {"start": v(1153, -309.8) * mm, "end": v(1133.95, -309.8) * mm});
            skLineSegment(sketch, "E453", {"start": v(1153, -309.8) * mm, "end": v(1153, -259) * mm});
            skLineSegment(sketch, "E454", {"start": v(1153, -259) * mm, "end": v(1133.95, -259) * mm});
            skLineSegment(sketch, "E455", {"start": v(1133.95, -259) * mm, "end": v(1133.95, -208.2) * mm});
            skLineSegment(sketch, "E456", {"start": v(1153, -208.2) * mm, "end": v(1133.95, -208.2) * mm});
            skLineSegment(sketch, "E457", {"start": v(1153, -208.2) * mm, "end": v(1153, -157.4) * mm});
            skLineSegment(sketch, "E458", {"start": v(1153, -157.4) * mm, "end": v(1133.95, -157.4) * mm});
            skLineSegment(sketch, "E459", {"start": v(1133.95, -157.4) * mm, "end": v(1133.95, -106.6) * mm});
            skLineSegment(sketch, "E460", {"start": v(1153, -106.6) * mm, "end": v(1133.95, -106.6) * mm});
            skLineSegment(sketch, "E461", {"start": v(1153, -106.6) * mm, "end": v(1153, -55.8) * mm});
            skLineSegment(sketch, "E462", {"start": v(1153, -55.8) * mm, "end": v(1133.95, -55.8) * mm});
            skLineSegment(sketch, "E463", {"start": v(1133.95, -55.8) * mm, "end": v(1133.95, -5) * mm});
            skLineSegment(sketch, "E464", {"start": v(-381, 5) * mm, "end": v(-330.2, 5) * mm});
            skLineSegment(sketch, "E465", {"start": v(-330.2, 24.05) * mm, "end": v(-330.2, 5) * mm});
            skLineSegment(sketch, "E466", {"start": v(-330.2, 24.05) * mm, "end": v(-279.4, 24.05) * mm});
            skLineSegment(sketch, "E467", {"start": v(-279.4, 24.05) * mm, "end": v(-279.4, 5) * mm});
            skLineSegment(sketch, "E468", {"start": v(-279.4, 5) * mm, "end": v(-228.6, 5) * mm});
            skLineSegment(sketch, "E469", {"start": v(-228.6, 24.05) * mm, "end": v(-228.6, 5) * mm});
            skLineSegment(sketch, "E470", {"start": v(-228.6, 24.05) * mm, "end": v(-177.8, 24.05) * mm});
            skLineSegment(sketch, "E471", {"start": v(-177.8, 24.05) * mm, "end": v(-177.8, 5) * mm});
            skLineSegment(sketch, "E472", {"start": v(-177.8, 5) * mm, "end": v(-127, 5) * mm});
            skLineSegment(sketch, "E473", {"start": v(-127, 24.05) * mm, "end": v(-127, 5) * mm});
            skLineSegment(sketch, "E474", {"start": v(-127, 24.05) * mm, "end": v(-76.2, 24.05) * mm});
            skLineSegment(sketch, "E475", {"start": v(-76.2, 24.05) * mm, "end": v(-76.2, 5) * mm});
            skLineSegment(sketch, "E476", {"start": v(-76.2, 5) * mm, "end": v(-25.4, 5) * mm});
            skLineSegment(sketch, "E477", {"start": v(-25.4, 24.05) * mm, "end": v(-25.4, 5) * mm});
            skLineSegment(sketch, "E478", {"start": v(-25.4, 24.05) * mm, "end": v(25.4, 24.05) * mm});
            skLineSegment(sketch, "E479", {"start": v(25.4, 24.05) * mm, "end": v(25.4, 5) * mm});
            skLineSegment(sketch, "E480", {"start": v(25.4, 5) * mm, "end": v(76.2, 5) * mm});
            skLineSegment(sketch, "E481", {"start": v(76.2, 24.05) * mm, "end": v(76.2, 5) * mm});
            skLineSegment(sketch, "E482", {"start": v(76.2, 24.05) * mm, "end": v(127, 24.05) * mm});
            skLineSegment(sketch, "E483", {"start": v(127, 24.05) * mm, "end": v(127, 5) * mm});
            skLineSegment(sketch, "E484", {"start": v(127, 5) * mm, "end": v(177.8, 5) * mm});
            skLineSegment(sketch, "E485", {"start": v(177.8, 24.05) * mm, "end": v(177.8, 5) * mm});
            skLineSegment(sketch, "E486", {"start": v(177.8, 24.05) * mm, "end": v(228.6, 24.05) * mm});
            skLineSegment(sketch, "E487", {"start": v(228.6, 24.05) * mm, "end": v(228.6, 5) * mm});
            skLineSegment(sketch, "E488", {"start": v(228.6, 5) * mm, "end": v(279.4, 5) * mm});
            skLineSegment(sketch, "E489", {"start": v(279.4, 24.05) * mm, "end": v(279.4, 5) * mm});
            skLineSegment(sketch, "E490", {"start": v(279.4, 24.05) * mm, "end": v(330.2, 24.05) * mm});
            skLineSegment(sketch, "E491", {"start": v(330.2, 24.05) * mm, "end": v(330.2, 5) * mm});
            skLineSegment(sketch, "E492", {"start": v(330.2, 5) * mm, "end": v(361.95, 5) * mm});
            skLineSegment(sketch, "E493", {"start": v(-381, 767) * mm, "end": v(-330.2, 767) * mm});
            skLineSegment(sketch, "E494", {"start": v(-330.2, 767) * mm, "end": v(-330.2, 747.95) * mm});
            skLineSegment(sketch, "E495", {"start": v(-330.2, 747.95) * mm, "end": v(-279.4, 747.95) * mm});
            skLineSegment(sketch, "E496", {"start": v(-279.4, 767) * mm, "end": v(-279.4, 747.95) * mm});
            skLineSegment(sketch, "E497", {"start": v(-279.4, 767) * mm, "end": v(-228.6, 767) * mm});
            skLineSegment(sketch, "E498", {"start": v(-228.6, 767) * mm, "end": v(-228.6, 747.95) * mm});
            skLineSegment(sketch, "E499", {"start": v(-228.6, 747.95) * mm, "end": v(-177.8, 747.95) * mm});
            skLineSegment(sketch, "E500", {"start": v(-177.8, 767) * mm, "end": v(-177.8, 747.95) * mm});
            skLineSegment(sketch, "E501", {"start": v(-177.8, 767) * mm, "end": v(-127, 767) * mm});
            skLineSegment(sketch, "E502", {"start": v(-127, 767) * mm, "end": v(-127, 747.95) * mm});
            skLineSegment(sketch, "E503", {"start": v(-127, 747.95) * mm, "end": v(-76.2, 747.95) * mm});
            skLineSegment(sketch, "E504", {"start": v(-76.2, 767) * mm, "end": v(-76.2, 747.95) * mm});
            skLineSegment(sketch, "E505", {"start": v(-76.2, 767) * mm, "end": v(-25.4, 767) * mm});
            skLineSegment(sketch, "E506", {"start": v(-25.4, 767) * mm, "end": v(-25.4, 747.95) * mm});
            skLineSegment(sketch, "E507", {"start": v(-25.4, 747.95) * mm, "end": v(25.4, 747.95) * mm});
            skLineSegment(sketch, "E508", {"start": v(25.4, 767) * mm, "end": v(25.4, 747.95) * mm});
            skLineSegment(sketch, "E509", {"start": v(25.4, 767) * mm, "end": v(76.2, 767) * mm});
            skLineSegment(sketch, "E510", {"start": v(76.2, 767) * mm, "end": v(76.2, 747.95) * mm});
            skLineSegment(sketch, "E511", {"start": v(76.2, 747.95) * mm, "end": v(127, 747.95) * mm});
            skLineSegment(sketch, "E512", {"start": v(127, 767) * mm, "end": v(127, 747.95) * mm});
            skLineSegment(sketch, "E513", {"start": v(127, 767) * mm, "end": v(177.8, 767) * mm});
            skLineSegment(sketch, "E514", {"start": v(177.8, 767) * mm, "end": v(177.8, 747.95) * mm});
            skLineSegment(sketch, "E515", {"start": v(177.8, 747.95) * mm, "end": v(228.6, 747.95) * mm});
            skLineSegment(sketch, "E516", {"start": v(228.6, 767) * mm, "end": v(228.6, 747.95) * mm});
            skLineSegment(sketch, "E517", {"start": v(228.6, 767) * mm, "end": v(279.4, 767) * mm});
            skLineSegment(sketch, "E518", {"start": v(279.4, 767) * mm, "end": v(279.4, 747.95) * mm});
            skLineSegment(sketch, "E519", {"start": v(279.4, 747.95) * mm, "end": v(330.2, 747.95) * mm});
            skLineSegment(sketch, "E520", {"start": v(330.2, 767) * mm, "end": v(330.2, 747.95) * mm});
            skLineSegment(sketch, "E521", {"start": v(330.2, 767) * mm, "end": v(361.95, 767) * mm});
            skLineSegment(sketch, "E522", {"start": v(-381, 5) * mm, "end": v(-381, 55.8) * mm});
            skLineSegment(sketch, "E523", {"start": v(-361.95, 55.8) * mm, "end": v(-381, 55.8) * mm});
            skLineSegment(sketch, "E524", {"start": v(-361.95, 55.8) * mm, "end": v(-361.95, 106.6) * mm});
            skLineSegment(sketch, "E525", {"start": v(-361.95, 106.6) * mm, "end": v(-381, 106.6) * mm});
            skLineSegment(sketch, "E526", {"start": v(-381, 106.6) * mm, "end": v(-381, 157.4) * mm});
            skLineSegment(sketch, "E527", {"start": v(-361.95, 157.4) * mm, "end": v(-381, 157.4) * mm});
            skLineSegment(sketch, "E528", {"start": v(-361.95, 157.4) * mm, "end": v(-361.95, 208.2) * mm});
            skLineSegment(sketch, "E529", {"start": v(-361.95, 208.2) * mm, "end": v(-381, 208.2) * mm});
            skLineSegment(sketch, "E530", {"start": v(-381, 208.2) * mm, "end": v(-381, 259) * mm});
            skLineSegment(sketch, "E531", {"start": v(-361.95, 259) * mm, "end": v(-381, 259) * mm});
            skLineSegment(sketch, "E532", {"start": v(-361.95, 259) * mm, "end": v(-361.95, 309.8) * mm});
            skLineSegment(sketch, "E533", {"start": v(-361.95, 309.8) * mm, "end": v(-381, 309.8) * mm});
            skLineSegment(sketch, "E534", {"start": v(-381, 309.8) * mm, "end": v(-381, 360.6) * mm});
            skLineSegment(sketch, "E535", {"start": v(-361.95, 360.6) * mm, "end": v(-381, 360.6) * mm});
            skLineSegment(sketch, "E536", {"start": v(-361.95, 360.6) * mm, "end": v(-361.95, 411.4) * mm});
            skLineSegment(sketch, "E537", {"start": v(-361.95, 411.4) * mm, "end": v(-381, 411.4) * mm});
            skLineSegment(sketch, "E538", {"start": v(-381, 411.4) * mm, "end": v(-381, 462.2) * mm});
            skLineSegment(sketch, "E539", {"start": v(-361.95, 462.2) * mm, "end": v(-381, 462.2) * mm});
            skLineSegment(sketch, "E540", {"start": v(-361.95, 462.2) * mm, "end": v(-361.95, 513) * mm});
            skLineSegment(sketch, "E541", {"start": v(-361.95, 513) * mm, "end": v(-381, 513) * mm});
            skLineSegment(sketch, "E542", {"start": v(-381, 513) * mm, "end": v(-381, 563.8) * mm});
            skLineSegment(sketch, "E543", {"start": v(-361.95, 563.8) * mm, "end": v(-381, 563.8) * mm});
            skLineSegment(sketch, "E544", {"start": v(-361.95, 563.8) * mm, "end": v(-361.95, 614.6) * mm});
            skLineSegment(sketch, "E545", {"start": v(-361.95, 614.6) * mm, "end": v(-381, 614.6) * mm});
            skLineSegment(sketch, "E546", {"start": v(-381, 614.6) * mm, "end": v(-381, 665.4) * mm});
            skLineSegment(sketch, "E547", {"start": v(-361.95, 665.4) * mm, "end": v(-381, 665.4) * mm});
            skLineSegment(sketch, "E548", {"start": v(-361.95, 665.4) * mm, "end": v(-361.95, 716.2) * mm});
            skLineSegment(sketch, "E549", {"start": v(-361.95, 716.2) * mm, "end": v(-381, 716.2) * mm});
            skLineSegment(sketch, "E550", {"start": v(-381, 716.2) * mm, "end": v(-381, 767) * mm});
            skLineSegment(sketch, "E551", {"start": v(361.95, 5) * mm, "end": v(361.95, 55.8) * mm});
            skLineSegment(sketch, "E552", {"start": v(381, 55.8) * mm, "end": v(361.95, 55.8) * mm});
            skLineSegment(sketch, "E553", {"start": v(381, 55.8) * mm, "end": v(381, 106.6) * mm});
            skLineSegment(sketch, "E554", {"start": v(381, 106.6) * mm, "end": v(361.95, 106.6) * mm});
            skLineSegment(sketch, "E555", {"start": v(361.95, 106.6) * mm, "end": v(361.95, 157.4) * mm});
            skLineSegment(sketch, "E556", {"start": v(381, 157.4) * mm, "end": v(361.95, 157.4) * mm});
            skLineSegment(sketch, "E557", {"start": v(381, 157.4) * mm, "end": v(381, 208.2) * mm});
            skLineSegment(sketch, "E558", {"start": v(381, 208.2) * mm, "end": v(361.95, 208.2) * mm});
            skLineSegment(sketch, "E559", {"start": v(361.95, 208.2) * mm, "end": v(361.95, 259) * mm});
            skLineSegment(sketch, "E560", {"start": v(381, 259) * mm, "end": v(361.95, 259) * mm});
            skLineSegment(sketch, "E561", {"start": v(381, 259) * mm, "end": v(381, 309.8) * mm});
            skLineSegment(sketch, "E562", {"start": v(381, 309.8) * mm, "end": v(361.95, 309.8) * mm});
            skLineSegment(sketch, "E563", {"start": v(361.95, 309.8) * mm, "end": v(361.95, 360.6) * mm});
            skLineSegment(sketch, "E564", {"start": v(381, 360.6) * mm, "end": v(361.95, 360.6) * mm});
            skLineSegment(sketch, "E565", {"start": v(381, 360.6) * mm, "end": v(381, 411.4) * mm});
            skLineSegment(sketch, "E566", {"start": v(381, 411.4) * mm, "end": v(361.95, 411.4) * mm});
            skLineSegment(sketch, "E567", {"start": v(361.95, 411.4) * mm, "end": v(361.95, 462.2) * mm});
            skLineSegment(sketch, "E568", {"start": v(381, 462.2) * mm, "end": v(361.95, 462.2) * mm});
            skLineSegment(sketch, "E569", {"start": v(381, 462.2) * mm, "end": v(381, 513) * mm});
            skLineSegment(sketch, "E570", {"start": v(381, 513) * mm, "end": v(361.95, 513) * mm});
            skLineSegment(sketch, "E571", {"start": v(361.95, 513) * mm, "end": v(361.95, 563.8) * mm});
            skLineSegment(sketch, "E572", {"start": v(381, 563.8) * mm, "end": v(361.95, 563.8) * mm});
            skLineSegment(sketch, "E573", {"start": v(381, 563.8) * mm, "end": v(381, 614.6) * mm});
            skLineSegment(sketch, "E574", {"start": v(381, 614.6) * mm, "end": v(361.95, 614.6) * mm});
            skLineSegment(sketch, "E575", {"start": v(361.95, 614.6) * mm, "end": v(361.95, 665.4) * mm});
            skLineSegment(sketch, "E576", {"start": v(381, 665.4) * mm, "end": v(361.95, 665.4) * mm});
            skLineSegment(sketch, "E577", {"start": v(381, 665.4) * mm, "end": v(381, 716.2) * mm});
            skLineSegment(sketch, "E578", {"start": v(381, 716.2) * mm, "end": v(361.95, 716.2) * mm});
            skLineSegment(sketch, "E579", {"start": v(361.95, 716.2) * mm, "end": v(361.95, 767) * mm});
            skLineSegment(sketch, "E580", {"start": v(-361.95, 796.05) * mm, "end": v(-330.2, 796.05) * mm});
            skLineSegment(sketch, "E581", {"start": v(-330.2, 796.05) * mm, "end": v(-330.2, 777) * mm});
            skLineSegment(sketch, "E582", {"start": v(-330.2, 777) * mm, "end": v(-279.4, 777) * mm});
            skLineSegment(sketch, "E583", {"start": v(-279.4, 796.05) * mm, "end": v(-279.4, 777) * mm});
            skLineSegment(sketch, "E584", {"start": v(-279.4, 796.05) * mm, "end": v(-228.6, 796.05) * mm});
            skLineSegment(sketch, "E585", {"start": v(-228.6, 796.05) * mm, "end": v(-228.6, 777) * mm});
            skLineSegment(sketch, "E586", {"start": v(-228.6, 777) * mm, "end": v(-177.8, 777) * mm});
            skLineSegment(sketch, "E587", {"start": v(-177.8, 796.05) * mm, "end": v(-177.8, 777) * mm});
            skLineSegment(sketch, "E588", {"start": v(-177.8, 796.05) * mm, "end": v(-127, 796.05) * mm});
            skLineSegment(sketch, "E589", {"start": v(-127, 796.05) * mm, "end": v(-127, 777) * mm});
            skLineSegment(sketch, "E590", {"start": v(-127, 777) * mm, "end": v(-76.2, 777) * mm});
            skLineSegment(sketch, "E591", {"start": v(-76.2, 796.05) * mm, "end": v(-76.2, 777) * mm});
            skLineSegment(sketch, "E592", {"start": v(-76.2, 796.05) * mm, "end": v(-25.4, 796.05) * mm});
            skLineSegment(sketch, "E593", {"start": v(-25.4, 796.05) * mm, "end": v(-25.4, 777) * mm});
            skLineSegment(sketch, "E594", {"start": v(-25.4, 777) * mm, "end": v(25.4, 777) * mm});
            skLineSegment(sketch, "E595", {"start": v(25.4, 796.05) * mm, "end": v(25.4, 777) * mm});
            skLineSegment(sketch, "E596", {"start": v(25.4, 796.05) * mm, "end": v(76.2, 796.05) * mm});
            skLineSegment(sketch, "E597", {"start": v(76.2, 796.05) * mm, "end": v(76.2, 777) * mm});
            skLineSegment(sketch, "E598", {"start": v(76.2, 777) * mm, "end": v(127, 777) * mm});
            skLineSegment(sketch, "E599", {"start": v(127, 796.05) * mm, "end": v(127, 777) * mm});
            skLineSegment(sketch, "E600", {"start": v(127, 796.05) * mm, "end": v(177.8, 796.05) * mm});
            skLineSegment(sketch, "E601", {"start": v(177.8, 796.05) * mm, "end": v(177.8, 777) * mm});
            skLineSegment(sketch, "E602", {"start": v(177.8, 777) * mm, "end": v(228.6, 777) * mm});
            skLineSegment(sketch, "E603", {"start": v(228.6, 796.05) * mm, "end": v(228.6, 777) * mm});
            skLineSegment(sketch, "E604", {"start": v(228.6, 796.05) * mm, "end": v(279.4, 796.05) * mm});
            skLineSegment(sketch, "E605", {"start": v(279.4, 796.05) * mm, "end": v(279.4, 777) * mm});
            skLineSegment(sketch, "E606", {"start": v(279.4, 777) * mm, "end": v(330.2, 777) * mm});
            skLineSegment(sketch, "E607", {"start": v(330.2, 796.05) * mm, "end": v(330.2, 777) * mm});
            skLineSegment(sketch, "E608", {"start": v(330.2, 796.05) * mm, "end": v(361.95, 796.05) * mm});
            skLineSegment(sketch, "E609", {"start": v(-361.95, 1519.95) * mm, "end": v(-330.2, 1519.95) * mm});
            skLineSegment(sketch, "E610", {"start": v(-330.2, 1539) * mm, "end": v(-330.2, 1519.95) * mm});
            skLineSegment(sketch, "E611", {"start": v(-330.2, 1539) * mm, "end": v(-279.4, 1539) * mm});
            skLineSegment(sketch, "E612", {"start": v(-279.4, 1539) * mm, "end": v(-279.4, 1519.95) * mm});
            skLineSegment(sketch, "E613", {"start": v(-279.4, 1519.95) * mm, "end": v(-228.6, 1519.95) * mm});
            skLineSegment(sketch, "E614", {"start": v(-228.6, 1539) * mm, "end": v(-228.6, 1519.95) * mm});
            skLineSegment(sketch, "E615", {"start": v(-228.6, 1539) * mm, "end": v(-177.8, 1539) * mm});
            skLineSegment(sketch, "E616", {"start": v(-177.8, 1539) * mm, "end": v(-177.8, 1519.95) * mm});
            skLineSegment(sketch, "E617", {"start": v(-177.8, 1519.95) * mm, "end": v(-127, 1519.95) * mm});
            skLineSegment(sketch, "E618", {"start": v(-127, 1539) * mm, "end": v(-127, 1519.95) * mm});
            skLineSegment(sketch, "E619", {"start": v(-127, 1539) * mm, "end": v(-76.2, 1539) * mm});
            skLineSegment(sketch, "E620", {"start": v(-76.2, 1539) * mm, "end": v(-76.2, 1519.95) * mm});
            skLineSegment(sketch, "E621", {"start": v(-76.2, 1519.95) * mm, "end": v(-25.4, 1519.95) * mm});
            skLineSegment(sketch, "E622", {"start": v(-25.4, 1539) * mm, "end": v(-25.4, 1519.95) * mm});
            skLineSegment(sketch, "E623", {"start": v(-25.4, 1539) * mm, "end": v(25.4, 1539) * mm});
            skLineSegment(sketch, "E624", {"start": v(25.4, 1539) * mm, "end": v(25.4, 1519.95) * mm});
            skLineSegment(sketch, "E625", {"start": v(25.4, 1519.95) * mm, "end": v(76.2, 1519.95) * mm});
            skLineSegment(sketch, "E626", {"start": v(76.2, 1539) * mm, "end": v(76.2, 1519.95) * mm});
            skLineSegment(sketch, "E627", {"start": v(76.2, 1539) * mm, "end": v(127, 1539) * mm});
            skLineSegment(sketch, "E628", {"start": v(127, 1539) * mm, "end": v(127, 1519.95) * mm});
            skLineSegment(sketch, "E629", {"start": v(127, 1519.95) * mm, "end": v(177.8, 1519.95) * mm});
            skLineSegment(sketch, "E630", {"start": v(177.8, 1539) * mm, "end": v(177.8, 1519.95) * mm});
            skLineSegment(sketch, "E631", {"start": v(177.8, 1539) * mm, "end": v(228.6, 1539) * mm});
            skLineSegment(sketch, "E632", {"start": v(228.6, 1539) * mm, "end": v(228.6, 1519.95) * mm});
            skLineSegment(sketch, "E633", {"start": v(228.6, 1519.95) * mm, "end": v(279.4, 1519.95) * mm});
            skLineSegment(sketch, "E634", {"start": v(279.4, 1539) * mm, "end": v(279.4, 1519.95) * mm});
            skLineSegment(sketch, "E635", {"start": v(279.4, 1539) * mm, "end": v(330.2, 1539) * mm});
            skLineSegment(sketch, "E636", {"start": v(330.2, 1539) * mm, "end": v(330.2, 1519.95) * mm});
            skLineSegment(sketch, "E637", {"start": v(330.2, 1519.95) * mm, "end": v(361.95, 1519.95) * mm});
            skLineSegment(sketch, "E638", {"start": v(-361.95, 796.05) * mm, "end": v(-361.95, 827.8) * mm});
            skLineSegment(sketch, "E639", {"start": v(-361.95, 827.8) * mm, "end": v(-381, 827.8) * mm});
            skLineSegment(sketch, "E640", {"start": v(-381, 827.8) * mm, "end": v(-381, 878.6) * mm});
            skLineSegment(sketch, "E641", {"start": v(-361.95, 878.6) * mm, "end": v(-381, 878.6) * mm});
            skLineSegment(sketch, "E642", {"start": v(-361.95, 878.6) * mm, "end": v(-361.95, 929.4) * mm});
            skLineSegment(sketch, "E643", {"start": v(-361.95, 929.4) * mm, "end": v(-381, 929.4) * mm});
            skLineSegment(sketch, "E644", {"start": v(-381, 929.4) * mm, "end": v(-381, 980.2) * mm});
            skLineSegment(sketch, "E645", {"start": v(-361.95, 980.2) * mm, "end": v(-381, 980.2) * mm});
            skLineSegment(sketch, "E646", {"start": v(-361.95, 980.2) * mm, "end": v(-361.95, 1031) * mm});
            skLineSegment(sketch, "E647", {"start": v(-361.95, 1031) * mm, "end": v(-381, 1031) * mm});
            skLineSegment(sketch, "E648", {"start": v(-381, 1031) * mm, "end": v(-381, 1081.8) * mm});
            skLineSegment(sketch, "E649", {"start": v(-361.95, 1081.8) * mm, "end": v(-381, 1081.8) * mm});
            skLineSegment(sketch, "E650", {"start": v(-361.95, 1081.8) * mm, "end": v(-361.95, 1132.6) * mm});
            skLineSegment(sketch, "E651", {"start": v(-361.95, 1132.6) * mm, "end": v(-381, 1132.6) * mm});
            skLineSegment(sketch, "E652", {"start": v(-381, 1132.6) * mm, "end": v(-381, 1183.4) * mm});
            skLineSegment(sketch, "E653", {"start": v(-361.95, 1183.4) * mm, "end": v(-381, 1183.4) * mm});
            skLineSegment(sketch, "E654", {"start": v(-361.95, 1183.4) * mm, "end": v(-361.95, 1234.2) * mm});
            skLineSegment(sketch, "E655", {"start": v(-361.95, 1234.2) * mm, "end": v(-381, 1234.2) * mm});
            skLineSegment(sketch, "E656", {"start": v(-381, 1234.2) * mm, "end": v(-381, 1285) * mm});
            skLineSegment(sketch, "E657", {"start": v(-361.95, 1285) * mm, "end": v(-381, 1285) * mm});
            skLineSegment(sketch, "E658", {"start": v(-361.95, 1285) * mm, "end": v(-361.95, 1335.8) * mm});
            skLineSegment(sketch, "E659", {"start": v(-361.95, 1335.8) * mm, "end": v(-381, 1335.8) * mm});
            skLineSegment(sketch, "E660", {"start": v(-381, 1335.8) * mm, "end": v(-381, 1386.6) * mm});
            skLineSegment(sketch, "E661", {"start": v(-361.95, 1386.6) * mm, "end": v(-381, 1386.6) * mm});
            skLineSegment(sketch, "E662", {"start": v(-361.95, 1386.6) * mm, "end": v(-361.95, 1437.4) * mm});
            skLineSegment(sketch, "E663", {"start": v(-361.95, 1437.4) * mm, "end": v(-381, 1437.4) * mm});
            skLineSegment(sketch, "E664", {"start": v(-381, 1437.4) * mm, "end": v(-381, 1488.2) * mm});
            skLineSegment(sketch, "E665", {"start": v(-361.95, 1488.2) * mm, "end": v(-381, 1488.2) * mm});
            skLineSegment(sketch, "E666", {"start": v(-361.95, 1488.2) * mm, "end": v(-361.95, 1519.95) * mm});
            skLineSegment(sketch, "E667", {"start": v(361.95, 796.05) * mm, "end": v(361.95, 827.8) * mm});
            skLineSegment(sketch, "E668", {"start": v(381, 827.8) * mm, "end": v(361.95, 827.8) * mm});
            skLineSegment(sketch, "E669", {"start": v(381, 827.8) * mm, "end": v(381, 878.6) * mm});
            skLineSegment(sketch, "E670", {"start": v(381, 878.6) * mm, "end": v(361.95, 878.6) * mm});
            skLineSegment(sketch, "E671", {"start": v(361.95, 878.6) * mm, "end": v(361.95, 929.4) * mm});
            skLineSegment(sketch, "E672", {"start": v(381, 929.4) * mm, "end": v(361.95, 929.4) * mm});
            skLineSegment(sketch, "E673", {"start": v(381, 929.4) * mm, "end": v(381, 980.2) * mm});
            skLineSegment(sketch, "E674", {"start": v(381, 980.2) * mm, "end": v(361.95, 980.2) * mm});
            skLineSegment(sketch, "E675", {"start": v(361.95, 980.2) * mm, "end": v(361.95, 1031) * mm});
            skLineSegment(sketch, "E676", {"start": v(381, 1031) * mm, "end": v(361.95, 1031) * mm});
            skLineSegment(sketch, "E677", {"start": v(381, 1031) * mm, "end": v(381, 1081.8) * mm});
            skLineSegment(sketch, "E678", {"start": v(381, 1081.8) * mm, "end": v(361.95, 1081.8) * mm});
            skLineSegment(sketch, "E679", {"start": v(361.95, 1081.8) * mm, "end": v(361.95, 1132.6) * mm});
            skLineSegment(sketch, "E680", {"start": v(381, 1132.6) * mm, "end": v(361.95, 1132.6) * mm});
            skLineSegment(sketch, "E681", {"start": v(381, 1132.6) * mm, "end": v(381, 1183.4) * mm});
            skLineSegment(sketch, "E682", {"start": v(381, 1183.4) * mm, "end": v(361.95, 1183.4) * mm});
            skLineSegment(sketch, "E683", {"start": v(361.95, 1183.4) * mm, "end": v(361.95, 1234.2) * mm});
            skLineSegment(sketch, "E684", {"start": v(381, 1234.2) * mm, "end": v(361.95, 1234.2) * mm});
            skLineSegment(sketch, "E685", {"start": v(381, 1234.2) * mm, "end": v(381, 1285) * mm});
            skLineSegment(sketch, "E686", {"start": v(381, 1285) * mm, "end": v(361.95, 1285) * mm});
            skLineSegment(sketch, "E687", {"start": v(361.95, 1285) * mm, "end": v(361.95, 1335.8) * mm});
            skLineSegment(sketch, "E688", {"start": v(381, 1335.8) * mm, "end": v(361.95, 1335.8) * mm});
            skLineSegment(sketch, "E689", {"start": v(381, 1335.8) * mm, "end": v(381, 1386.6) * mm});
            skLineSegment(sketch, "E690", {"start": v(381, 1386.6) * mm, "end": v(361.95, 1386.6) * mm});
            skLineSegment(sketch, "E691", {"start": v(361.95, 1386.6) * mm, "end": v(361.95, 1437.4) * mm});
            skLineSegment(sketch, "E692", {"start": v(381, 1437.4) * mm, "end": v(361.95, 1437.4) * mm});
            skLineSegment(sketch, "E693", {"start": v(381, 1437.4) * mm, "end": v(381, 1488.2) * mm});
            skLineSegment(sketch, "E694", {"start": v(381, 1488.2) * mm, "end": v(361.95, 1488.2) * mm});
            skLineSegment(sketch, "E695", {"start": v(361.95, 1488.2) * mm, "end": v(361.95, 1519.95) * mm});
            skSolve(sketch);
        }
        {
            var Q0;
            Q0=makeQuery(id+"F0.imprint","IMPRINT",FACE,{"disambiguationData":[TD([[makeQuery(id+"F0.imprint","IMPRINT",EDGE,{"derivedFrom":sQuery(id+"F0.wireOp",EDGE,"E580")}),1.0]])]});
            var Q1;
            Q1=makeQuery(id+"F0.imprint","IMPRINT",FACE,{"disambiguationData":[TD([[makeQuery(id+"F0.imprint","IMPRINT",EDGE,{"derivedFrom":sQuery(id+"F0.wireOp",EDGE,"E464")}),1.0]])]});
            var Q2;
            Q2=makeQuery(id+"F0.imprint","IMPRINT",FACE,{"disambiguationData":[TD([[makeQuery(id+"F0.imprint","IMPRINT",EDGE,{"derivedFrom":sQuery(id+"F0.wireOp",EDGE,"E232")}),1.0]])]});
            var Q3;
            Q3=makeQuery(id+"F0.imprint","IMPRINT",FACE,{"disambiguationData":[TD([[makeQuery(id+"F0.imprint","IMPRINT",EDGE,{"derivedFrom":sQuery(id+"F0.wireOp",EDGE,"E348")}),1.0]])]});
            var Q4;
            Q4=makeQuery(id+"F0.imprint","IMPRINT",FACE,{"disambiguationData":[TD([[makeQuery(id+"F0.imprint","IMPRINT",EDGE,{"derivedFrom":sQuery(id+"F0.wireOp",EDGE,"E116")}),1.0]])]});
            var Q5;
            Q5=makeQuery(id+"F0.imprint","IMPRINT",FACE,{"disambiguationData":[TD([[makeQuery(id+"F0.imprint","IMPRINT",EDGE,{"derivedFrom":sQuery(id+"F0.wireOp",EDGE,"E0")}),1.0]])]});
            extrude(context, id + "F1", {"entities" : qUnion([Q0, Q1, Q2, Q3, Q4, Q5]), "depth" : 19.05 * mm});
        }
        {
            var Q0;
            Q0=makeQuery(id+"F1.opExtrude","CAP_FACE",FACE,{"disambiguationData":[OSD([sQuery(id+"F0.wireOp",EDGE,"E464"),sQuery(id+"F0.wireOp",EDGE,"E465"),sQuery(id+"F0.wireOp",EDGE,"E466"),sQuery(id+"F0.wireOp",EDGE,"E467"),sQuery(id+"F0.wireOp",EDGE,"E468"),sQuery(id+"F0.wireOp",EDGE,"E469"),sQuery(id+"F0.wireOp",EDGE,"E470"),sQuery(id+"F0.wireOp",EDGE,"E471"),sQuery(id+"F0.wireOp",EDGE,"E472"),sQuery(id+"F0.wireOp",EDGE,"E473"),sQuery(id+"F0.wireOp",EDGE,"E474"),sQuery(id+"F0.wireOp",EDGE,"E475"),sQuery(id+"F0.wireOp",EDGE,"E476"),sQuery(id+"F0.wireOp",EDGE,"E477"),sQuery(id+"F0.wireOp",EDGE,"E478"),sQuery(id+"F0.wireOp",EDGE,"E479"),sQuery(id+"F0.wireOp",EDGE,"E480"),sQuery(id+"F0.wireOp",EDGE,"E481"),sQuery(id+"F0.wireOp",EDGE,"E482"),sQuery(id+"F0.wireOp",EDGE,"E483"),sQuery(id+"F0.wireOp",EDGE,"E484"),sQuery(id+"F0.wireOp",EDGE,"E485"),sQuery(id+"F0.wireOp",EDGE,"E486"),sQuery(id+"F0.wireOp",EDGE,"E487"),sQuery(id+"F0.wireOp",EDGE,"E488"),sQuery(id+"F0.wireOp",EDGE,"E489"),sQuery(id+"F0.wireOp",EDGE,"E490"),sQuery(id+"F0.wireOp",EDGE,"E491"),sQuery(id+"F0.wireOp",EDGE,"E492"),sQuery(id+"F0.wireOp",EDGE,"E493"),sQuery(id+"F0.wireOp",EDGE,"E494"),sQuery(id+"F0.wireOp",EDGE,"E495"),sQuery(id+"F0.wireOp",EDGE,"E496"),sQuery(id+"F0.wireOp",EDGE,"E497"),sQuery(id+"F0.wireOp",EDGE,"E498"),sQuery(id+"F0.wireOp",EDGE,"E499"),sQuery(id+"F0.wireOp",EDGE,"E500"),sQuery(id+"F0.wireOp",EDGE,"E501"),sQuery(id+"F0.wireOp",EDGE,"E502"),sQuery(id+"F0.wireOp",EDGE,"E503"),sQuery(id+"F0.wireOp",EDGE,"E504"),sQuery(id+"F0.wireOp",EDGE,"E505"),sQuery(id+"F0.wireOp",EDGE,"E506"),sQuery(id+"F0.wireOp",EDGE,"E507"),sQuery(id+"F0.wireOp",EDGE,"E508"),sQuery(id+"F0.wireOp",EDGE,"E509"),sQuery(id+"F0.wireOp",EDGE,"E510"),sQuery(id+"F0.wireOp",EDGE,"E511"),sQuery(id+"F0.wireOp",EDGE,"E512"),sQuery(id+"F0.wireOp",EDGE,"E513"),sQuery(id+"F0.wireOp",EDGE,"E514"),sQuery(id+"F0.wireOp",EDGE,"E515"),sQuery(id+"F0.wireOp",EDGE,"E516"),sQuery(id+"F0.wireOp",EDGE,"E517"),sQuery(id+"F0.wireOp",EDGE,"E518"),sQuery(id+"F0.wireOp",EDGE,"E519"),sQuery(id+"F0.wireOp",EDGE,"E520"),sQuery(id+"F0.wireOp",EDGE,"E521"),sQuery(id+"F0.wireOp",EDGE,"E522"),sQuery(id+"F0.wireOp",EDGE,"E523"),sQuery(id+"F0.wireOp",EDGE,"E524"),sQuery(id+"F0.wireOp",EDGE,"E525"),sQuery(id+"F0.wireOp",EDGE,"E526"),sQuery(id+"F0.wireOp",EDGE,"E527"),sQuery(id+"F0.wireOp",EDGE,"E528"),sQuery(id+"F0.wireOp",EDGE,"E529"),sQuery(id+"F0.wireOp",EDGE,"E530"),sQuery(id+"F0.wireOp",EDGE,"E531"),sQuery(id+"F0.wireOp",EDGE,"E532"),sQuery(id+"F0.wireOp",EDGE,"E533"),sQuery(id+"F0.wireOp",EDGE,"E534"),sQuery(id+"F0.wireOp",EDGE,"E535"),sQuery(id+"F0.wireOp",EDGE,"E536"),sQuery(id+"F0.wireOp",EDGE,"E537"),sQuery(id+"F0.wireOp",EDGE,"E538"),sQuery(id+"F0.wireOp",EDGE,"E539"),sQuery(id+"F0.wireOp",EDGE,"E540"),sQuery(id+"F0.wireOp",EDGE,"E541"),sQuery(id+"F0.wireOp",EDGE,"E542"),sQuery(id+"F0.wireOp",EDGE,"E543"),sQuery(id+"F0.wireOp",EDGE,"E544"),sQuery(id+"F0.wireOp",EDGE,"E545"),sQuery(id+"F0.wireOp",EDGE,"E546"),sQuery(id+"F0.wireOp",EDGE,"E547"),sQuery(id+"F0.wireOp",EDGE,"E548"),sQuery(id+"F0.wireOp",EDGE,"E549"),sQuery(id+"F0.wireOp",EDGE,"E550"),sQuery(id+"F0.wireOp",EDGE,"E551"),sQuery(id+"F0.wireOp",EDGE,"E552"),sQuery(id+"F0.wireOp",EDGE,"E553"),sQuery(id+"F0.wireOp",EDGE,"E554"),sQuery(id+"F0.wireOp",EDGE,"E555"),sQuery(id+"F0.wireOp",EDGE,"E556"),sQuery(id+"F0.wireOp",EDGE,"E557"),sQuery(id+"F0.wireOp",EDGE,"E558"),sQuery(id+"F0.wireOp",EDGE,"E559"),sQuery(id+"F0.wireOp",EDGE,"E560"),sQuery(id+"F0.wireOp",EDGE,"E561"),sQuery(id+"F0.wireOp",EDGE,"E562"),sQuery(id+"F0.wireOp",EDGE,"E563"),sQuery(id+"F0.wireOp",EDGE,"E564"),sQuery(id+"F0.wireOp",EDGE,"E565"),sQuery(id+"F0.wireOp",EDGE,"E566"),sQuery(id+"F0.wireOp",EDGE,"E567"),sQuery(id+"F0.wireOp",EDGE,"E568"),sQuery(id+"F0.wireOp",EDGE,"E569"),sQuery(id+"F0.wireOp",EDGE,"E570"),sQuery(id+"F0.wireOp",EDGE,"E571"),sQuery(id+"F0.wireOp",EDGE,"E572"),sQuery(id+"F0.wireOp",EDGE,"E573"),sQuery(id+"F0.wireOp",EDGE,"E574"),sQuery(id+"F0.wireOp",EDGE,"E575"),sQuery(id+"F0.wireOp",EDGE,"E576"),sQuery(id+"F0.wireOp",EDGE,"E577"),sQuery(id+"F0.wireOp",EDGE,"E578"),sQuery(id+"F0.wireOp",EDGE,"E579")])],"isStart":false});
            var sketch = newSketch(context, id + "F2", { "sketchPlane" : qUnion([Q0])});
            skPoint(sketch, "E696", {"position": v(-142.68, 651.63) * mm});
            skArc(sketch, "E697", {"start": v(-49.68, 554.24) * mm, "mid": v(-202.6, 709.38) * mm, "end": v(-295.15, 512.2) * mm});
            skArc(sketch, "E698.0", {"start": v(-62.17, 556.57) * mm, "mid": v(-200.45, 696.86) * mm, "end": v(-284.15, 518.54) * mm});
            skPoint(sketch, "E699", {"position": v(-279.13, 510.58) * mm});
            skPoint(sketch, "E700", {"position": v(-289.61, 503.42) * mm});
            skPoint(sketch, "E701", {"position": v(-295.15, 512.2) * mm});
            skPoint(sketch, "E702", {"position": v(-284.15, 518.54) * mm});
            skPoint(sketch, "E703", {"position": v(-49.68, 554.24) * mm});
            skPoint(sketch, "E704", {"position": v(-62.17, 556.57) * mm});
            skArc(sketch, "E705", {"start": v(-295.15, 512.2) * mm, "mid": v(-286.47, 509.87) * mm, "end": v(-284.15, 518.54) * mm});
            skArc(sketch, "E706", {"start": v(-62.17, 556.57) * mm, "mid": v(-57.09, 549.16) * mm, "end": v(-49.68, 554.24) * mm});
            skPoint(sketch, "E707", {"position": v(-189.93, 576.44) * mm});
            skPoint(sketch, "E708", {"position": v(-200.81, 583.02) * mm});
            skPoint(sketch, "E709", {"position": v(-275.57, 90.15) * mm});
            skPoint(sketch, "E710.4.internal.orphan", {"position": v(-180.18, 246.44) * mm});
            skLineSegment(sketch, "E711.left", {"start": v(-200.81, 567.1) * mm, "end": v(-200.81, 230.2) * mm});
            skLineSegment(sketch, "E711.right", {"start": v(-188.11, 567.1) * mm, "end": v(-188.11, 463.76) * mm});
            skLineSegment(sketch, "E712.bottom", {"start": v(-181.76, 457.41) * mm, "end": v(-8.07, 457.41) * mm});
            skLineSegment(sketch, "E712.top", {"start": v(-181.76, 444.71) * mm, "end": v(-8.07, 444.71) * mm});
            skLineSegment(sketch, "E713.trimOffspring", {"start": v(-188.11, 438.36) * mm, "end": v(-188.11, 230.2) * mm});
            skArc(sketch, "E714", {"start": v(-200.81, 230.2) * mm, "mid": v(-194.46, 223.86) * mm, "end": v(-188.11, 230.2) * mm});
            skArc(sketch, "E715", {"start": v(-8.07, 444.71) * mm, "mid": v(-1.72, 451.06) * mm, "end": v(-8.07, 457.41) * mm});
            skArc(sketch, "E716", {"start": v(-188.11, 567.1) * mm, "mid": v(-194.46, 573.44) * mm, "end": v(-200.81, 567.1) * mm});
            skPoint(sketch, "E717.15.internal.snap0", {"position": v(-361.95, 386) * mm});
            skPoint(sketch, "E718.8.internal.snap0", {"position": v(-98.1, 457.41) * mm});
            skPoint(sketch, "E718.20.internal.snap0", {"position": v(-361.95, 182.8) * mm});
            skPoint(sketch, "E717.0.internal.orphan", {"position": v(-310.1, 687.94) * mm});
            skPoint(sketch, "E717.18.internal.orphan", {"position": v(158.77, 716.2) * mm});
            skPoint(sketch, "E717.20.internal.orphan", {"position": v(-80.55, 716.2) * mm});
            skPoint(sketch, "E718.0.internal.orphan", {"position": v(-289.65, 165.35) * mm});
            skPoint(sketch, "E718.10.internal.orphan", {"position": v(64.34, 665.4) * mm});
            skPoint(sketch, "E718.12.internal.orphan", {"position": v(152.26, 411.4) * mm});
            skPoint(sketch, "E718.2.internal.orphan", {"position": v(-289.65, 329.78) * mm});
            skPoint(sketch, "E718.20.internal.orphan", {"position": v(-127, 182.8) * mm});
            skPoint(sketch, "E718.6.internal.orphan", {"position": v(-310.1, 457.41) * mm});
            skPoint(sketch, "E718.7.internal.orphan", {"position": v(-289.65, 665.4) * mm});
            skPoint(sketch, "E718.8.internal.orphan", {"position": v(-98.1, 704.22) * mm});
            skLineSegment(sketch, "E719", {"start": v(73.78, 550.48) * mm, "end": v(150.34, 414.8) * mm});
            skLineSegment(sketch, "E720", {"start": v(150.08, 408.15) * mm, "end": v(42.96, 248.31) * mm});
            skLineSegment(sketch, "E721", {"start": v(42.89, 241.35) * mm, "end": v(133.7, 100.08) * mm});
            skLineSegment(sketch, "E722", {"start": v(-333.93, 391.19) * mm, "end": v(-333.93, 69.22) * mm});
            skLineSegment(sketch, "E723", {"start": v(-327.58, 62.87) * mm, "end": v(20.38, 62.87) * mm});
            skLineSegment(sketch, "E724.0", {"start": v(-321.23, 391.19) * mm, "end": v(-321.23, 75.57) * mm});
            skLineSegment(sketch, "E725.0", {"start": v(-355.6, 49.45) * mm, "end": v(-374.65, 49.45) * mm});
            skLineSegment(sketch, "E725.1", {"start": v(-355.6, 112.95) * mm, "end": v(-355.6, 49.45) * mm});
            skLineSegment(sketch, "E725.2", {"start": v(-374.65, 112.95) * mm, "end": v(-355.6, 112.95) * mm});
            skLineSegment(sketch, "E725.3", {"start": v(-374.65, 151.05) * mm, "end": v(-374.65, 112.95) * mm});
            skLineSegment(sketch, "E725.4", {"start": v(-355.6, 151.05) * mm, "end": v(-374.65, 151.05) * mm});
            skLineSegment(sketch, "E725.5", {"start": v(-355.6, 214.55) * mm, "end": v(-355.6, 151.05) * mm});
            skLineSegment(sketch, "E725.6", {"start": v(-374.65, 214.55) * mm, "end": v(-355.6, 214.55) * mm});
            skLineSegment(sketch, "E725.7", {"start": v(-374.65, 252.65) * mm, "end": v(-374.65, 214.55) * mm});
            skLineSegment(sketch, "E725.8", {"start": v(-355.6, 252.65) * mm, "end": v(-374.65, 252.65) * mm});
            skLineSegment(sketch, "E725.9", {"start": v(-355.6, 316.15) * mm, "end": v(-355.6, 252.65) * mm});
            skLineSegment(sketch, "E725.10", {"start": v(-374.65, 316.15) * mm, "end": v(-355.6, 316.15) * mm});
            skLineSegment(sketch, "E725.11", {"start": v(-374.65, 354.25) * mm, "end": v(-374.65, 316.15) * mm});
            skLineSegment(sketch, "E725.12", {"start": v(-355.6, 354.25) * mm, "end": v(-374.65, 354.25) * mm});
            skLineSegment(sketch, "E725.13", {"start": v(-355.6, 417.75) * mm, "end": v(-355.6, 354.25) * mm});
            skLineSegment(sketch, "E725.14", {"start": v(-374.65, 417.75) * mm, "end": v(-355.6, 417.75) * mm});
            skLineSegment(sketch, "E725.15", {"start": v(-374.65, 455.85) * mm, "end": v(-374.65, 417.75) * mm});
            skLineSegment(sketch, "E725.16", {"start": v(-355.6, 455.85) * mm, "end": v(-374.65, 455.85) * mm});
            skLineSegment(sketch, "E725.17", {"start": v(-355.6, 519.35) * mm, "end": v(-355.6, 455.85) * mm});
            skLineSegment(sketch, "E725.18", {"start": v(-374.65, 519.35) * mm, "end": v(-355.6, 519.35) * mm});
            skLineSegment(sketch, "E725.19", {"start": v(355.6, 405.05) * mm, "end": v(355.6, 468.55) * mm});
            skLineSegment(sketch, "E725.20", {"start": v(374.65, 405.05) * mm, "end": v(355.6, 405.05) * mm});
            skLineSegment(sketch, "E725.21", {"start": v(374.65, 366.95) * mm, "end": v(374.65, 405.05) * mm});
            skLineSegment(sketch, "E725.22", {"start": v(355.6, 366.95) * mm, "end": v(374.65, 366.95) * mm});
            skLineSegment(sketch, "E725.23", {"start": v(355.6, 303.45) * mm, "end": v(355.6, 366.95) * mm});
            skLineSegment(sketch, "E725.24", {"start": v(374.65, 303.45) * mm, "end": v(355.6, 303.45) * mm});
            skLineSegment(sketch, "E725.25", {"start": v(374.65, 265.35) * mm, "end": v(374.65, 303.45) * mm});
            skLineSegment(sketch, "E725.26", {"start": v(355.6, 265.35) * mm, "end": v(374.65, 265.35) * mm});
            skLineSegment(sketch, "E725.27", {"start": v(355.6, 201.85) * mm, "end": v(355.6, 265.35) * mm});
            skLineSegment(sketch, "E725.28", {"start": v(374.65, 201.85) * mm, "end": v(355.6, 201.85) * mm});
            skLineSegment(sketch, "E725.29", {"start": v(374.65, 163.75) * mm, "end": v(374.65, 201.85) * mm});
            skLineSegment(sketch, "E725.30", {"start": v(355.6, 163.75) * mm, "end": v(374.65, 163.75) * mm});
            skLineSegment(sketch, "E725.31", {"start": v(355.6, 100.25) * mm, "end": v(355.6, 163.75) * mm});
            skLineSegment(sketch, "E725.32", {"start": v(374.65, 100.25) * mm, "end": v(355.6, 100.25) * mm});
            skLineSegment(sketch, "E725.33", {"start": v(374.65, 62.15) * mm, "end": v(374.65, 100.25) * mm});
            skLineSegment(sketch, "E725.34", {"start": v(355.6, 62.15) * mm, "end": v(374.65, 62.15) * mm});
            skLineSegment(sketch, "E725.35", {"start": v(355.6, 11.35) * mm, "end": v(355.6, 62.15) * mm});
            skLineSegment(sketch, "E725.36", {"start": v(336.55, 11.35) * mm, "end": v(355.6, 11.35) * mm});
            skLineSegment(sketch, "E725.37", {"start": v(336.55, 30.4) * mm, "end": v(336.55, 11.35) * mm});
            skLineSegment(sketch, "E725.38", {"start": v(273.05, 30.4) * mm, "end": v(336.55, 30.4) * mm});
            skLineSegment(sketch, "E725.39", {"start": v(273.05, 11.35) * mm, "end": v(273.05, 30.4) * mm});
            skLineSegment(sketch, "E725.40", {"start": v(234.95, 11.35) * mm, "end": v(273.05, 11.35) * mm});
            skLineSegment(sketch, "E725.41", {"start": v(234.95, 30.4) * mm, "end": v(234.95, 11.35) * mm});
            skLineSegment(sketch, "E725.42", {"start": v(171.45, 30.4) * mm, "end": v(234.95, 30.4) * mm});
            skLineSegment(sketch, "E725.43", {"start": v(-133.35, 11.35) * mm, "end": v(-133.35, 30.4) * mm});
            skLineSegment(sketch, "E725.44", {"start": v(-171.45, 11.35) * mm, "end": v(-133.35, 11.35) * mm});
            skLineSegment(sketch, "E725.45", {"start": v(-171.45, 30.4) * mm, "end": v(-171.45, 11.35) * mm});
            skLineSegment(sketch, "E725.46", {"start": v(-234.95, 30.4) * mm, "end": v(-171.45, 30.4) * mm});
            skLineSegment(sketch, "E725.47", {"start": v(-234.95, 11.35) * mm, "end": v(-234.95, 30.4) * mm});
            skLineSegment(sketch, "E725.48", {"start": v(-273.05, 11.35) * mm, "end": v(-234.95, 11.35) * mm});
            skLineSegment(sketch, "E725.49", {"start": v(-374.65, 11.35) * mm, "end": v(-336.55, 11.35) * mm});
            skLineSegment(sketch, "E725.50", {"start": v(-336.55, 11.35) * mm, "end": v(-336.55, 30.4) * mm});
            skLineSegment(sketch, "E725.51", {"start": v(-336.55, 30.4) * mm, "end": v(-273.05, 30.4) * mm});
            skLineSegment(sketch, "E725.52", {"start": v(-273.05, 30.4) * mm, "end": v(-273.05, 11.35) * mm});
            skLineSegment(sketch, "E725.53", {"start": v(-133.35, 30.4) * mm, "end": v(-69.85, 30.4) * mm});
            skLineSegment(sketch, "E725.54", {"start": v(-69.85, 30.4) * mm, "end": v(-69.85, 11.35) * mm});
            skLineSegment(sketch, "E725.55", {"start": v(-69.85, 11.35) * mm, "end": v(-31.75, 11.35) * mm});
            skLineSegment(sketch, "E725.56", {"start": v(-31.75, 11.35) * mm, "end": v(-31.75, 30.4) * mm});
            skLineSegment(sketch, "E725.57", {"start": v(-31.75, 30.4) * mm, "end": v(31.75, 30.4) * mm});
            skLineSegment(sketch, "E725.58", {"start": v(31.75, 30.4) * mm, "end": v(31.75, 11.35) * mm});
            skLineSegment(sketch, "E725.59", {"start": v(31.75, 11.35) * mm, "end": v(69.85, 11.35) * mm});
            skLineSegment(sketch, "E725.60", {"start": v(69.85, 11.35) * mm, "end": v(69.85, 30.4) * mm});
            skLineSegment(sketch, "E725.61", {"start": v(69.85, 30.4) * mm, "end": v(133.35, 30.4) * mm});
            skLineSegment(sketch, "E725.62", {"start": v(133.35, 30.4) * mm, "end": v(133.35, 11.35) * mm});
            skLineSegment(sketch, "E725.63", {"start": v(133.35, 11.35) * mm, "end": v(171.45, 11.35) * mm});
            skLineSegment(sketch, "E725.64", {"start": v(171.45, 11.35) * mm, "end": v(171.45, 30.4) * mm});
            skLineSegment(sketch, "E725.65", {"start": v(355.6, 468.55) * mm, "end": v(374.65, 468.55) * mm});
            skLineSegment(sketch, "E725.66", {"start": v(374.65, 468.55) * mm, "end": v(374.65, 506.65) * mm});
            skLineSegment(sketch, "E725.67", {"start": v(374.65, 506.65) * mm, "end": v(355.6, 506.65) * mm});
            skLineSegment(sketch, "E725.68", {"start": v(355.6, 506.65) * mm, "end": v(355.6, 570.15) * mm});
            skLineSegment(sketch, "E725.69", {"start": v(355.6, 570.15) * mm, "end": v(374.65, 570.15) * mm});
            skLineSegment(sketch, "E725.70", {"start": v(374.65, 570.15) * mm, "end": v(374.65, 608.25) * mm});
            skLineSegment(sketch, "E725.71", {"start": v(374.65, 608.25) * mm, "end": v(355.6, 608.25) * mm});
            skLineSegment(sketch, "E725.72", {"start": v(355.6, 608.25) * mm, "end": v(355.6, 671.75) * mm});
            skLineSegment(sketch, "E725.73", {"start": v(355.6, 671.75) * mm, "end": v(374.65, 671.75) * mm});
            skLineSegment(sketch, "E725.74", {"start": v(374.65, 671.75) * mm, "end": v(374.65, 709.85) * mm});
            skLineSegment(sketch, "E725.75", {"start": v(374.65, 709.85) * mm, "end": v(355.6, 709.85) * mm});
            skLineSegment(sketch, "E725.76", {"start": v(355.6, 709.85) * mm, "end": v(355.6, 760.65) * mm});
            skLineSegment(sketch, "E725.77", {"start": v(355.6, 760.65) * mm, "end": v(336.55, 760.65) * mm});
            skLineSegment(sketch, "E725.78", {"start": v(336.55, 760.65) * mm, "end": v(336.55, 741.6) * mm});
            skLineSegment(sketch, "E725.79", {"start": v(336.55, 741.6) * mm, "end": v(273.05, 741.6) * mm});
            skLineSegment(sketch, "E725.80", {"start": v(273.05, 741.6) * mm, "end": v(273.05, 760.65) * mm});
            skLineSegment(sketch, "E725.81", {"start": v(273.05, 760.65) * mm, "end": v(234.95, 760.65) * mm});
            skLineSegment(sketch, "E725.82", {"start": v(234.95, 760.65) * mm, "end": v(234.95, 741.6) * mm});
            skLineSegment(sketch, "E725.83", {"start": v(234.95, 741.6) * mm, "end": v(171.45, 741.6) * mm});
            skLineSegment(sketch, "E725.84", {"start": v(-374.65, 49.45) * mm, "end": v(-374.65, 11.35) * mm});
            skLineSegment(sketch, "E725.85", {"start": v(171.45, 741.6) * mm, "end": v(171.45, 760.65) * mm});
            skLineSegment(sketch, "E725.86", {"start": v(171.45, 760.65) * mm, "end": v(133.35, 760.65) * mm});
            skLineSegment(sketch, "E725.87", {"start": v(133.35, 760.65) * mm, "end": v(133.35, 741.6) * mm});
            skLineSegment(sketch, "E725.88", {"start": v(133.35, 741.6) * mm, "end": v(69.85, 741.6) * mm});
            skLineSegment(sketch, "E725.89", {"start": v(69.85, 741.6) * mm, "end": v(69.85, 760.65) * mm});
            skLineSegment(sketch, "E725.90", {"start": v(69.85, 760.65) * mm, "end": v(31.75, 760.65) * mm});
            skLineSegment(sketch, "E725.91", {"start": v(31.75, 760.65) * mm, "end": v(31.75, 741.6) * mm});
            skLineSegment(sketch, "E725.92", {"start": v(31.75, 741.6) * mm, "end": v(-31.75, 741.6) * mm});
            skLineSegment(sketch, "E725.93", {"start": v(-31.75, 741.6) * mm, "end": v(-31.75, 760.65) * mm});
            skLineSegment(sketch, "E725.94", {"start": v(-31.75, 760.65) * mm, "end": v(-69.85, 760.65) * mm});
            skLineSegment(sketch, "E725.95", {"start": v(-69.85, 760.65) * mm, "end": v(-69.85, 741.6) * mm});
            skLineSegment(sketch, "E725.96", {"start": v(-69.85, 741.6) * mm, "end": v(-133.35, 741.6) * mm});
            skLineSegment(sketch, "E725.97", {"start": v(-133.35, 741.6) * mm, "end": v(-133.35, 760.65) * mm});
            skLineSegment(sketch, "E725.98", {"start": v(-133.35, 760.65) * mm, "end": v(-171.45, 760.65) * mm});
            skLineSegment(sketch, "E725.99", {"start": v(-171.45, 760.65) * mm, "end": v(-171.45, 741.6) * mm});
            skLineSegment(sketch, "E725.100", {"start": v(-171.45, 741.6) * mm, "end": v(-234.95, 741.6) * mm});
            skLineSegment(sketch, "E725.101", {"start": v(-234.95, 741.6) * mm, "end": v(-234.95, 760.65) * mm});
            skLineSegment(sketch, "E725.102", {"start": v(-234.95, 760.65) * mm, "end": v(-273.05, 760.65) * mm});
            skLineSegment(sketch, "E725.103", {"start": v(-273.05, 760.65) * mm, "end": v(-273.05, 741.6) * mm});
            skLineSegment(sketch, "E725.104", {"start": v(-273.05, 741.6) * mm, "end": v(-336.55, 741.6) * mm});
            skLineSegment(sketch, "E725.105", {"start": v(-336.55, 741.6) * mm, "end": v(-336.55, 760.65) * mm});
            skLineSegment(sketch, "E725.106", {"start": v(-336.55, 760.65) * mm, "end": v(-374.65, 760.65) * mm});
            skLineSegment(sketch, "E725.107", {"start": v(-374.65, 760.65) * mm, "end": v(-374.65, 722.55) * mm});
            skLineSegment(sketch, "E725.108", {"start": v(-374.65, 722.55) * mm, "end": v(-355.6, 722.55) * mm});
            skLineSegment(sketch, "E725.109", {"start": v(-355.6, 722.55) * mm, "end": v(-355.6, 659.05) * mm});
            skLineSegment(sketch, "E725.110", {"start": v(-355.6, 659.05) * mm, "end": v(-374.65, 659.05) * mm});
            skLineSegment(sketch, "E725.111", {"start": v(-374.65, 659.05) * mm, "end": v(-374.65, 620.95) * mm});
            skLineSegment(sketch, "E725.112", {"start": v(-374.65, 620.95) * mm, "end": v(-355.6, 620.95) * mm});
            skLineSegment(sketch, "E725.113", {"start": v(-355.6, 620.95) * mm, "end": v(-355.6, 557.45) * mm});
            skLineSegment(sketch, "E725.114", {"start": v(-355.6, 557.45) * mm, "end": v(-374.65, 557.45) * mm});
            skLineSegment(sketch, "E725.115", {"start": v(-374.65, 557.45) * mm, "end": v(-374.65, 519.35) * mm});
            skLineSegment(sketch, "E726", {"start": v(20.38, 75.57) * mm, "end": v(-321.23, 75.57) * mm});
            skLineSegment(sketch, "E727", {"start": v(-321.23, 75.57) * mm, "end": v(-321.23, 391.19) * mm});
            skPoint(sketch, "E728.startSnap0", {"position": v(-98.1, 444.71) * mm});
            skLineSegment(sketch, "E729", {"start": v(-204.1, 116.27) * mm, "end": v(60.34, 435.04) * mm});
            skPoint(sketch, "E730.endSnap0", {"position": v(355.6, 436.8) * mm});
            skPoint(sketch, "E731.end.orphan", {"position": v(266.93, 651.63) * mm});
            skPoint(sketch, "E731.start.orphan", {"position": v(266.93, 638.93) * mm});
            skLineSegment(sketch, "E732", {"start": v(74.38, 557.6) * mm, "end": v(159.15, 662.06) * mm});
            skLineSegment(sketch, "E733.0", {"start": v(89.7, 556.31) * mm, "end": v(169.01, 654.06) * mm});
            skLineSegment(sketch, "E733.1", {"start": v(89.1, 549.19) * mm, "end": v(165.24, 414.23) * mm});
            skLineSegment(sketch, "E733.2", {"start": v(164.99, 407.58) * mm, "end": v(58.15, 248.17) * mm});
            skLineSegment(sketch, "E733.3", {"start": v(58.08, 241.2) * mm, "end": v(144.39, 106.94) * mm});
            skArc(sketch, "E734", {"start": v(-321.23, 391.19) * mm, "mid": v(-327.58, 397.54) * mm, "end": v(-333.93, 391.19) * mm});
            skArc(sketch, "E735", {"start": v(20.38, 62.87) * mm, "mid": v(26.73, 69.22) * mm, "end": v(20.38, 75.57) * mm});
            skPoint(sketch, "E736.visualSharp", {"position": v(-333.93, 62.87) * mm});
            skArc(sketch, "E736.filletArc", {"start": v(-333.93, 69.22) * mm, "mid": v(-332.07, 64.73) * mm, "end": v(-327.58, 62.87) * mm});
            skArc(sketch, "E737", {"start": v(133.7, 100.08) * mm, "mid": v(142.48, 98.17) * mm, "end": v(144.39, 106.94) * mm});
            skArc(sketch, "E738", {"start": v(169.01, 654.06) * mm, "mid": v(168.08, 663) * mm, "end": v(159.15, 662.06) * mm});
            skPoint(sketch, "E739.visualSharp", {"position": v(71.66, 554.24) * mm});
            skArc(sketch, "E739.filletArc", {"start": v(74.38, 557.6) * mm, "mid": v(72.99, 554.13) * mm, "end": v(73.78, 550.48) * mm});
            skPoint(sketch, "E740.visualSharp", {"position": v(86.97, 552.95) * mm});
            skArc(sketch, "E740.filletArc", {"start": v(89.7, 556.31) * mm, "mid": v(88.3, 552.84) * mm, "end": v(89.1, 549.19) * mm});
            skArc(sketch, "E741.filletArc", {"start": v(150.08, 408.15) * mm, "mid": v(151.15, 411.44) * mm, "end": v(150.34, 414.8) * mm});
            skPoint(sketch, "E742.visualSharp", {"position": v(167.16, 410.83) * mm});
            skArc(sketch, "E742.filletArc", {"start": v(164.99, 407.58) * mm, "mid": v(166.06, 410.87) * mm, "end": v(165.24, 414.23) * mm});
            skPoint(sketch, "E743.visualSharp", {"position": v(40.64, 244.85) * mm});
            skArc(sketch, "E743.filletArc", {"start": v(42.96, 248.31) * mm, "mid": v(41.88, 244.84) * mm, "end": v(42.89, 241.35) * mm});
            skPoint(sketch, "E744.visualSharp", {"position": v(55.83, 244.7) * mm});
            skArc(sketch, "E744.filletArc", {"start": v(58.15, 248.17) * mm, "mid": v(57.07, 244.7) * mm, "end": v(58.08, 241.2) * mm});
            skPoint(sketch, "E745.visualSharp", {"position": v(-188.11, 457.41) * mm});
            skArc(sketch, "E745.filletArc", {"start": v(-188.11, 463.76) * mm, "mid": v(-186.25, 459.27) * mm, "end": v(-181.76, 457.41) * mm});
            skPoint(sketch, "E746.visualSharp", {"position": v(-188.11, 444.71) * mm});
            skArc(sketch, "E746.filletArc", {"start": v(-181.76, 444.71) * mm, "mid": v(-186.25, 442.85) * mm, "end": v(-188.11, 438.36) * mm});
            skPoint(sketch, "E728.start.orphan", {"position": v(52.1, 444.71) * mm});
            skLineSegment(sketch, "E747.0", {"start": v(-194.32, 108.16) * mm, "end": v(70.1, 426.93) * mm});
            skArc(sketch, "E748", {"start": v(-204.1, 116.27) * mm, "mid": v(-203.26, 107.33) * mm, "end": v(-194.32, 108.16) * mm});
            skArc(sketch, "E749", {"start": v(70.1, 426.93) * mm, "mid": v(69.28, 435.87) * mm, "end": v(60.34, 435.04) * mm});
            skSolve(sketch);
        }
        {
            var Q0;
            Q0=makeQuery(id+"F2.imprint","IMPRINT",FACE,{"disambiguationData":[TD([[makeQuery(id+"F2.imprint","IMPRINT",EDGE,{"derivedFrom":sQuery(id+"F2.wireOp",EDGE,"E697")}),1.0]])]});
            var Q1;
            Q1=makeQuery(id+"F2.imprint","IMPRINT",FACE,{"disambiguationData":[TD([[makeQuery(id+"F2.imprint","IMPRINT",EDGE,{"derivedFrom":sQuery(id+"F2.wireOp",EDGE,"E711.left")}),1.0]])]});
            var Q2;
            Q2=makeQuery(id+"F2.imprint","IMPRINT",FACE,{"disambiguationData":[TD([[makeQuery(id+"F2.imprint","IMPRINT",EDGE,{"derivedFrom":sQuery(id+"F2.wireOp",EDGE,"E717")}),1.0]])]});
            var Q3;
            Q3=makeQuery(id+"F2.imprint","IMPRINT",FACE,{"disambiguationData":[TD([[makeQuery(id+"F2.imprint","IMPRINT",EDGE,{"derivedFrom":sQuery(id+"F2.wireOp",EDGE,"vTTiJHrq-l3M7-g1bd-ojdK-S6GDLuhRd5LN")}),1.0]])]});
            var Q4;
            Q4=makeQuery(id+"F2.imprint","IMPRINT",FACE,{"disambiguationData":[TD([[makeQuery(id+"F2.imprint","IMPRINT",EDGE,{"derivedFrom":sQuery(id+"F2.wireOp",EDGE,"E728")}),1.0]])]});
            var Q5;
            Q5=makeQuery(id+"F2.imprint","IMPRINT",FACE,{"disambiguationData":[TD([[makeQuery(id+"F2.imprint","IMPRINT",EDGE,{"derivedFrom":sQuery(id+"F2.wireOp",EDGE,"E719")}),1.0]])]});
            var Q6;
            Q6=makeQuery(id+"F2.imprint","IMPRINT",FACE,{"disambiguationData":[TD([[makeQuery(id+"F2.imprint","IMPRINT",EDGE,{"derivedFrom":sQuery(id+"F2.wireOp",EDGE,"E722")}),1.0]])]});
            extrude(context, id + "F3", {"entities" : qUnion([Q0, Q1, Q2, Q3, Q4, Q5, Q6]), "operationType" : NewBodyOperationType.REMOVE, "endBound" : BoundingType.THROUGH_ALL, "oppositeDirection" : true, "depth" : 25.4 * mm});
        }
        {
            var Q0;
            Q0=makeQuery(id+"F1.opExtrude","CAP_FACE",FACE,{"disambiguationData":[OSD([sQuery(id+"F0.wireOp",EDGE,"E0"),sQuery(id+"F0.wireOp",EDGE,"E1"),sQuery(id+"F0.wireOp",EDGE,"E2"),sQuery(id+"F0.wireOp",EDGE,"E3"),sQuery(id+"F0.wireOp",EDGE,"E4"),sQuery(id+"F0.wireOp",EDGE,"E5"),sQuery(id+"F0.wireOp",EDGE,"E6"),sQuery(id+"F0.wireOp",EDGE,"E7"),sQuery(id+"F0.wireOp",EDGE,"E8"),sQuery(id+"F0.wireOp",EDGE,"E9"),sQuery(id+"F0.wireOp",EDGE,"E10"),sQuery(id+"F0.wireOp",EDGE,"E11"),sQuery(id+"F0.wireOp",EDGE,"E12"),sQuery(id+"F0.wireOp",EDGE,"E13"),sQuery(id+"F0.wireOp",EDGE,"E14"),sQuery(id+"F0.wireOp",EDGE,"E15"),sQuery(id+"F0.wireOp",EDGE,"E16"),sQuery(id+"F0.wireOp",EDGE,"E17"),sQuery(id+"F0.wireOp",EDGE,"E18"),sQuery(id+"F0.wireOp",EDGE,"E19"),sQuery(id+"F0.wireOp",EDGE,"E20"),sQuery(id+"F0.wireOp",EDGE,"E21"),sQuery(id+"F0.wireOp",EDGE,"E22"),sQuery(id+"F0.wireOp",EDGE,"E23"),sQuery(id+"F0.wireOp",EDGE,"E24"),sQuery(id+"F0.wireOp",EDGE,"E25"),sQuery(id+"F0.wireOp",EDGE,"E26"),sQuery(id+"F0.wireOp",EDGE,"E27"),sQuery(id+"F0.wireOp",EDGE,"E28"),sQuery(id+"F0.wireOp",EDGE,"E29"),sQuery(id+"F0.wireOp",EDGE,"E30"),sQuery(id+"F0.wireOp",EDGE,"E31"),sQuery(id+"F0.wireOp",EDGE,"E32"),sQuery(id+"F0.wireOp",EDGE,"E33"),sQuery(id+"F0.wireOp",EDGE,"E34"),sQuery(id+"F0.wireOp",EDGE,"E35"),sQuery(id+"F0.wireOp",EDGE,"E36"),sQuery(id+"F0.wireOp",EDGE,"E37"),sQuery(id+"F0.wireOp",EDGE,"E38"),sQuery(id+"F0.wireOp",EDGE,"E39"),sQuery(id+"F0.wireOp",EDGE,"E40"),sQuery(id+"F0.wireOp",EDGE,"E41"),sQuery(id+"F0.wireOp",EDGE,"E42"),sQuery(id+"F0.wireOp",EDGE,"E43"),sQuery(id+"F0.wireOp",EDGE,"E44"),sQuery(id+"F0.wireOp",EDGE,"E45"),sQuery(id+"F0.wireOp",EDGE,"E46"),sQuery(id+"F0.wireOp",EDGE,"E47"),sQuery(id+"F0.wireOp",EDGE,"E48"),sQuery(id+"F0.wireOp",EDGE,"E49"),sQuery(id+"F0.wireOp",EDGE,"E50"),sQuery(id+"F0.wireOp",EDGE,"E51"),sQuery(id+"F0.wireOp",EDGE,"E52"),sQuery(id+"F0.wireOp",EDGE,"E53"),sQuery(id+"F0.wireOp",EDGE,"E54"),sQuery(id+"F0.wireOp",EDGE,"E55"),sQuery(id+"F0.wireOp",EDGE,"E56"),sQuery(id+"F0.wireOp",EDGE,"E57"),sQuery(id+"F0.wireOp",EDGE,"E58"),sQuery(id+"F0.wireOp",EDGE,"E59"),sQuery(id+"F0.wireOp",EDGE,"E60"),sQuery(id+"F0.wireOp",EDGE,"E61"),sQuery(id+"F0.wireOp",EDGE,"E62"),sQuery(id+"F0.wireOp",EDGE,"E63"),sQuery(id+"F0.wireOp",EDGE,"E64"),sQuery(id+"F0.wireOp",EDGE,"E65"),sQuery(id+"F0.wireOp",EDGE,"E66"),sQuery(id+"F0.wireOp",EDGE,"E67"),sQuery(id+"F0.wireOp",EDGE,"E68"),sQuery(id+"F0.wireOp",EDGE,"E69"),sQuery(id+"F0.wireOp",EDGE,"E70"),sQuery(id+"F0.wireOp",EDGE,"E71"),sQuery(id+"F0.wireOp",EDGE,"E72"),sQuery(id+"F0.wireOp",EDGE,"E73"),sQuery(id+"F0.wireOp",EDGE,"E74"),sQuery(id+"F0.wireOp",EDGE,"E75"),sQuery(id+"F0.wireOp",EDGE,"E76"),sQuery(id+"F0.wireOp",EDGE,"E77"),sQuery(id+"F0.wireOp",EDGE,"E78"),sQuery(id+"F0.wireOp",EDGE,"E79"),sQuery(id+"F0.wireOp",EDGE,"E80"),sQuery(id+"F0.wireOp",EDGE,"E81"),sQuery(id+"F0.wireOp",EDGE,"E82"),sQuery(id+"F0.wireOp",EDGE,"E83"),sQuery(id+"F0.wireOp",EDGE,"E84"),sQuery(id+"F0.wireOp",EDGE,"E85"),sQuery(id+"F0.wireOp",EDGE,"E86"),sQuery(id+"F0.wireOp",EDGE,"E87"),sQuery(id+"F0.wireOp",EDGE,"E88"),sQuery(id+"F0.wireOp",EDGE,"E89"),sQuery(id+"F0.wireOp",EDGE,"E90"),sQuery(id+"F0.wireOp",EDGE,"E91"),sQuery(id+"F0.wireOp",EDGE,"E92"),sQuery(id+"F0.wireOp",EDGE,"E93"),sQuery(id+"F0.wireOp",EDGE,"E94"),sQuery(id+"F0.wireOp",EDGE,"E95"),sQuery(id+"F0.wireOp",EDGE,"E96"),sQuery(id+"F0.wireOp",EDGE,"E97"),sQuery(id+"F0.wireOp",EDGE,"E98"),sQuery(id+"F0.wireOp",EDGE,"E99"),sQuery(id+"F0.wireOp",EDGE,"E100"),sQuery(id+"F0.wireOp",EDGE,"E101"),sQuery(id+"F0.wireOp",EDGE,"E102"),sQuery(id+"F0.wireOp",EDGE,"E103"),sQuery(id+"F0.wireOp",EDGE,"E104"),sQuery(id+"F0.wireOp",EDGE,"E105"),sQuery(id+"F0.wireOp",EDGE,"E106"),sQuery(id+"F0.wireOp",EDGE,"E107"),sQuery(id+"F0.wireOp",EDGE,"E108"),sQuery(id+"F0.wireOp",EDGE,"E109"),sQuery(id+"F0.wireOp",EDGE,"E110"),sQuery(id+"F0.wireOp",EDGE,"E111"),sQuery(id+"F0.wireOp",EDGE,"E112"),sQuery(id+"F0.wireOp",EDGE,"E113"),sQuery(id+"F0.wireOp",EDGE,"E114"),sQuery(id+"F0.wireOp",EDGE,"E115")])],"isStart":false});
            var sketch = newSketch(context, id + "F4", { "sketchPlane" : qUnion([Q0])});
            skPoint(sketch, "E750.center.orphan", {"position": v(-145.79, -1033.13) * mm});
            skPoint(sketch, "E751.center.orphan", {"position": v(-71.5, -1033.13) * mm});
            skPoint(sketch, "E752.center.orphan", {"position": v(0, -1088.98) * mm});
            skPoint(sketch, "E753.center.orphan", {"position": v(0, -1295.23) * mm});
            skPoint(sketch, "E754.center.orphan", {"position": v(110.8, -1312.2) * mm});
            skPoint(sketch, "E755.center.orphan", {"position": v(110.8, -1376.62) * mm});
            skCircle(sketch, "E756", {"center": v(-263.93, -887.76) * mm, "radius": 44.17 * mm});
            skPoint(sketch, "E756.first.point", {"position": v(-299.33, -861.34) * mm});
            skPoint(sketch, "E756.second.point", {"position": v(-249.31, -929.45) * mm});
            skPoint(sketch, "E756.third.point", {"position": v(-248.1, -846.53) * mm});
            skCircle(sketch, "E757.0.1.0", {"center": v(-261.05, -989.32) * mm, "radius": 44.17 * mm});
            skCircle(sketch, "E757.0.2.0", {"center": v(-258.17, -1090.88) * mm, "radius": 44.17 * mm});
            skCircle(sketch, "E757.0.3.0", {"center": v(-255.29, -1192.44) * mm, "radius": 44.17 * mm});
            skCircle(sketch, "E757.1.0.0", {"center": v(-162.33, -888.64) * mm, "radius": 44.17 * mm});
            skCircle(sketch, "E757.1.1.0", {"center": v(-159.45, -990.2) * mm, "radius": 44.17 * mm});
            skCircle(sketch, "E757.1.2.0", {"center": v(-156.57, -1091.76) * mm, "radius": 44.17 * mm});
            skCircle(sketch, "E757.1.3.0", {"center": v(-153.7, -1193.32) * mm, "radius": 44.17 * mm});
            skCircle(sketch, "E757.2.0.0", {"center": v(-60.74, -889.52) * mm, "radius": 44.17 * mm});
            skCircle(sketch, "E757.2.1.0", {"center": v(-57.86, -991.08) * mm, "radius": 44.17 * mm});
            skCircle(sketch, "E757.2.2.0", {"center": v(-54.98, -1092.64) * mm, "radius": 44.17 * mm});
            skCircle(sketch, "E757.2.3.0", {"center": v(-52.1, -1194.2) * mm, "radius": 44.17 * mm});
            skCircle(sketch, "E757.3.0.0", {"center": v(40.86, -890.4) * mm, "radius": 44.17 * mm});
            skCircle(sketch, "E757.3.1.0", {"center": v(43.74, -991.96) * mm, "radius": 44.17 * mm});
            skCircle(sketch, "E757.3.2.0", {"center": v(46.62, -1093.52) * mm, "radius": 44.17 * mm});
            skCircle(sketch, "E757.3.3.0", {"center": v(49.5, -1195.08) * mm, "radius": 44.17 * mm});
            skLineSegment(sketch, "E757.direction1", {"start": v(-263.93, -887.76) * mm, "end": v(-162.33, -888.64) * mm, "construction": true});
            skLineSegment(sketch, "E757.direction2", {"start": v(-263.93, -887.76) * mm, "end": v(-261.05, -989.32) * mm, "construction": true});
            skCircle(sketch, "E758.0.4.0", {"center": v(142.46, -891.28) * mm, "radius": 44.17 * mm});
            skCircle(sketch, "E758.0.4.1", {"center": v(145.34, -992.84) * mm, "radius": 44.17 * mm});
            skCircle(sketch, "E758.0.4.2", {"center": v(148.22, -1094.4) * mm, "radius": 44.17 * mm});
            skCircle(sketch, "E758.0.4.3", {"center": v(151.1, -1195.96) * mm, "radius": 44.17 * mm});
            skCircle(sketch, "E758.0.5.0", {"center": v(244.05, -892.16) * mm, "radius": 44.17 * mm});
            skCircle(sketch, "E758.0.5.1", {"center": v(246.93, -993.72) * mm, "radius": 44.17 * mm});
            skCircle(sketch, "E758.0.5.2", {"center": v(249.81, -1095.28) * mm, "radius": 44.17 * mm});
            skCircle(sketch, "E758.0.5.3", {"center": v(252.7, -1196.84) * mm, "radius": 44.17 * mm});
            skCircle(sketch, "E759.0.0.4", {"center": v(-252.4, -1294) * mm, "radius": 44.17 * mm});
            skCircle(sketch, "E759.0.0.5", {"center": v(-249.53, -1395.56) * mm, "radius": 44.17 * mm});
            skCircle(sketch, "E759.0.1.4", {"center": v(-150.81, -1294.88) * mm, "radius": 44.17 * mm});
            skCircle(sketch, "E759.0.1.5", {"center": v(-147.93, -1396.44) * mm, "radius": 44.17 * mm});
            skCircle(sketch, "E759.0.2.4", {"center": v(-49.22, -1295.76) * mm, "radius": 44.17 * mm});
            skCircle(sketch, "E759.0.2.5", {"center": v(-46.34, -1397.32) * mm, "radius": 44.17 * mm});
            skCircle(sketch, "E759.0.3.4", {"center": v(52.38, -1296.64) * mm, "radius": 44.17 * mm});
            skCircle(sketch, "E759.0.3.5", {"center": v(55.26, -1398.2) * mm, "radius": 44.17 * mm});
            skCircle(sketch, "E759.0.4.4", {"center": v(153.98, -1297.52) * mm, "radius": 44.17 * mm});
            skCircle(sketch, "E759.0.4.5", {"center": v(156.86, -1399.08) * mm, "radius": 44.17 * mm});
            skCircle(sketch, "E759.0.5.4", {"center": v(255.57, -1298.4) * mm, "radius": 44.17 * mm});
            skCircle(sketch, "E759.0.5.5", {"center": v(258.45, -1399.96) * mm, "radius": 44.17 * mm});
            skSolve(sketch);
        }
        {
            var Q0;
            Q0=makeQuery(id+"F4.imprint","IMPRINT",FACE,{"disambiguationData":[TD([[makeQuery(id+"F4.imprint","IMPRINT",EDGE,{"derivedFrom":sQuery(id+"F4.wireOp",EDGE,"E757.2.2.0")}),1.0]])]});
            var Q1;
            Q1=makeQuery(id+"F4.imprint","IMPRINT",FACE,{"disambiguationData":[TD([[makeQuery(id+"F4.imprint","IMPRINT",EDGE,{"derivedFrom":sQuery(id+"F4.wireOp",EDGE,"E757.1.2.0")}),1.0]])]});
            var Q2;
            Q2=makeQuery(id+"F4.imprint","IMPRINT",FACE,{"disambiguationData":[TD([[makeQuery(id+"F4.imprint","IMPRINT",EDGE,{"derivedFrom":sQuery(id+"F4.wireOp",EDGE,"E757.0.2.0")}),1.0]])]});
            var Q3;
            Q3=makeQuery(id+"F4.imprint","IMPRINT",FACE,{"disambiguationData":[TD([[makeQuery(id+"F4.imprint","IMPRINT",EDGE,{"derivedFrom":sQuery(id+"F4.wireOp",EDGE,"E757.0.1.0")}),1.0]])]});
            var Q4;
            Q4=makeQuery(id+"F4.imprint","IMPRINT",FACE,{"disambiguationData":[TD([[makeQuery(id+"F4.imprint","IMPRINT",EDGE,{"derivedFrom":sQuery(id+"F4.wireOp",EDGE,"E757.1.1.0")}),1.0]])]});
            var Q5;
            Q5=makeQuery(id+"F4.imprint","IMPRINT",FACE,{"disambiguationData":[TD([[makeQuery(id+"F4.imprint","IMPRINT",EDGE,{"derivedFrom":sQuery(id+"F4.wireOp",EDGE,"E757.2.1.0")}),1.0]])]});
            var Q6;
            Q6=makeQuery(id+"F4.imprint","IMPRINT",FACE,{"disambiguationData":[TD([[makeQuery(id+"F4.imprint","IMPRINT",EDGE,{"derivedFrom":sQuery(id+"F4.wireOp",EDGE,"E756")}),1.0]])]});
            var Q7;
            Q7=makeQuery(id+"F4.imprint","IMPRINT",FACE,{"disambiguationData":[TD([[makeQuery(id+"F4.imprint","IMPRINT",EDGE,{"derivedFrom":sQuery(id+"F4.wireOp",EDGE,"E757.1.0.0")}),1.0]])]});
            var Q8;
            Q8=makeQuery(id+"F4.imprint","IMPRINT",FACE,{"disambiguationData":[TD([[makeQuery(id+"F4.imprint","IMPRINT",EDGE,{"derivedFrom":sQuery(id+"F4.wireOp",EDGE,"E757.2.0.0")}),1.0]])]});
            var Q9;
            Q9=makeQuery(id+"F4.imprint","IMPRINT",FACE,{"disambiguationData":[TD([[makeQuery(id+"F4.imprint","IMPRINT",EDGE,{"derivedFrom":sQuery(id+"F4.wireOp",EDGE,"E757.3.0.0")}),1.0]])]});
            var Q10;
            Q10=makeQuery(id+"F4.imprint","IMPRINT",FACE,{"disambiguationData":[TD([[makeQuery(id+"F4.imprint","IMPRINT",EDGE,{"derivedFrom":sQuery(id+"F4.wireOp",EDGE,"E757.3.1.0")}),1.0]])]});
            var Q11;
            Q11=makeQuery(id+"F4.imprint","IMPRINT",FACE,{"disambiguationData":[TD([[makeQuery(id+"F4.imprint","IMPRINT",EDGE,{"derivedFrom":sQuery(id+"F4.wireOp",EDGE,"E757.3.2.0")}),1.0]])]});
            var Q12;
            Q12=makeQuery(id+"F4.imprint","IMPRINT",FACE,{"disambiguationData":[TD([[makeQuery(id+"F4.imprint","IMPRINT",EDGE,{"derivedFrom":sQuery(id+"F4.wireOp",EDGE,"E758.0.4.2")}),1.0]])]});
            var Q13;
            Q13=makeQuery(id+"F4.imprint","IMPRINT",FACE,{"disambiguationData":[TD([[makeQuery(id+"F4.imprint","IMPRINT",EDGE,{"derivedFrom":sQuery(id+"F4.wireOp",EDGE,"E758.0.4.1")}),1.0]])]});
            var Q14;
            Q14=makeQuery(id+"F4.imprint","IMPRINT",FACE,{"disambiguationData":[TD([[makeQuery(id+"F4.imprint","IMPRINT",EDGE,{"derivedFrom":sQuery(id+"F4.wireOp",EDGE,"E758.0.4.0")}),1.0]])]});
            var Q15;
            Q15=makeQuery(id+"F4.imprint","IMPRINT",FACE,{"disambiguationData":[TD([[makeQuery(id+"F4.imprint","IMPRINT",EDGE,{"derivedFrom":sQuery(id+"F4.wireOp",EDGE,"E758.0.5.0")}),1.0]])]});
            var Q16;
            Q16=makeQuery(id+"F4.imprint","IMPRINT",FACE,{"disambiguationData":[TD([[makeQuery(id+"F4.imprint","IMPRINT",EDGE,{"derivedFrom":sQuery(id+"F4.wireOp",EDGE,"E758.0.5.1")}),1.0]])]});
            var Q17;
            Q17=makeQuery(id+"F4.imprint","IMPRINT",FACE,{"disambiguationData":[TD([[makeQuery(id+"F4.imprint","IMPRINT",EDGE,{"derivedFrom":sQuery(id+"F4.wireOp",EDGE,"E758.0.5.2")}),1.0]])]});
            var Q18;
            Q18=makeQuery(id+"F4.imprint","IMPRINT",FACE,{"disambiguationData":[TD([[makeQuery(id+"F4.imprint","IMPRINT",EDGE,{"derivedFrom":sQuery(id+"F4.wireOp",EDGE,"E757.2.3.0")}),1.0]])]});
            var Q19;
            Q19=makeQuery(id+"F4.imprint","IMPRINT",FACE,{"disambiguationData":[TD([[makeQuery(id+"F4.imprint","IMPRINT",EDGE,{"derivedFrom":sQuery(id+"F4.wireOp",EDGE,"E757.1.3.0")}),1.0]])]});
            var Q20;
            Q20=makeQuery(id+"F4.imprint","IMPRINT",FACE,{"disambiguationData":[TD([[makeQuery(id+"F4.imprint","IMPRINT",EDGE,{"derivedFrom":sQuery(id+"F4.wireOp",EDGE,"E757.0.3.0")}),1.0]])]});
            var Q21;
            Q21=makeQuery(id+"F4.imprint","IMPRINT",FACE,{"disambiguationData":[TD([[makeQuery(id+"F4.imprint","IMPRINT",EDGE,{"derivedFrom":sQuery(id+"F4.wireOp",EDGE,"E759.0.0.4")}),1.0]])]});
            var Q22;
            Q22=makeQuery(id+"F4.imprint","IMPRINT",FACE,{"disambiguationData":[TD([[makeQuery(id+"F4.imprint","IMPRINT",EDGE,{"derivedFrom":sQuery(id+"F4.wireOp",EDGE,"E759.0.1.4")}),1.0]])]});
            var Q23;
            Q23=makeQuery(id+"F4.imprint","IMPRINT",FACE,{"disambiguationData":[TD([[makeQuery(id+"F4.imprint","IMPRINT",EDGE,{"derivedFrom":sQuery(id+"F4.wireOp",EDGE,"E759.0.2.4")}),1.0]])]});
            var Q24;
            Q24=makeQuery(id+"F4.imprint","IMPRINT",FACE,{"disambiguationData":[TD([[makeQuery(id+"F4.imprint","IMPRINT",EDGE,{"derivedFrom":sQuery(id+"F4.wireOp",EDGE,"E757.3.3.0")}),1.0]])]});
            var Q25;
            Q25=makeQuery(id+"F4.imprint","IMPRINT",FACE,{"disambiguationData":[TD([[makeQuery(id+"F4.imprint","IMPRINT",EDGE,{"derivedFrom":sQuery(id+"F4.wireOp",EDGE,"E758.0.4.3")}),1.0]])]});
            var Q26;
            Q26=makeQuery(id+"F4.imprint","IMPRINT",FACE,{"disambiguationData":[TD([[makeQuery(id+"F4.imprint","IMPRINT",EDGE,{"derivedFrom":sQuery(id+"F4.wireOp",EDGE,"E758.0.5.3")}),1.0]])]});
            var Q27;
            Q27=makeQuery(id+"F4.imprint","IMPRINT",FACE,{"disambiguationData":[TD([[makeQuery(id+"F4.imprint","IMPRINT",EDGE,{"derivedFrom":sQuery(id+"F4.wireOp",EDGE,"E759.0.5.4")}),1.0]])]});
            var Q28;
            Q28=makeQuery(id+"F4.imprint","IMPRINT",FACE,{"disambiguationData":[TD([[makeQuery(id+"F4.imprint","IMPRINT",EDGE,{"derivedFrom":sQuery(id+"F4.wireOp",EDGE,"E759.0.4.4")}),1.0]])]});
            var Q29;
            Q29=makeQuery(id+"F4.imprint","IMPRINT",FACE,{"disambiguationData":[TD([[makeQuery(id+"F4.imprint","IMPRINT",EDGE,{"derivedFrom":sQuery(id+"F4.wireOp",EDGE,"E759.0.3.4")}),1.0]])]});
            var Q30;
            Q30=makeQuery(id+"F4.imprint","IMPRINT",FACE,{"disambiguationData":[TD([[makeQuery(id+"F4.imprint","IMPRINT",EDGE,{"derivedFrom":sQuery(id+"F4.wireOp",EDGE,"E759.0.3.5")}),1.0]])]});
            var Q31;
            Q31=makeQuery(id+"F4.imprint","IMPRINT",FACE,{"disambiguationData":[TD([[makeQuery(id+"F4.imprint","IMPRINT",EDGE,{"derivedFrom":sQuery(id+"F4.wireOp",EDGE,"E759.0.4.5")}),1.0]])]});
            var Q32;
            Q32=makeQuery(id+"F4.imprint","IMPRINT",FACE,{"disambiguationData":[TD([[makeQuery(id+"F4.imprint","IMPRINT",EDGE,{"derivedFrom":sQuery(id+"F4.wireOp",EDGE,"E759.0.5.5")}),1.0]])]});
            var Q33;
            Q33=makeQuery(id+"F4.imprint","IMPRINT",FACE,{"disambiguationData":[TD([[makeQuery(id+"F4.imprint","IMPRINT",EDGE,{"derivedFrom":sQuery(id+"F4.wireOp",EDGE,"E759.0.2.5")}),1.0]])]});
            var Q34;
            Q34=makeQuery(id+"F4.imprint","IMPRINT",FACE,{"disambiguationData":[TD([[makeQuery(id+"F4.imprint","IMPRINT",EDGE,{"derivedFrom":sQuery(id+"F4.wireOp",EDGE,"E759.0.1.5")}),1.0]])]});
            var Q35;
            Q35=makeQuery(id+"F4.imprint","IMPRINT",FACE,{"disambiguationData":[TD([[makeQuery(id+"F4.imprint","IMPRINT",EDGE,{"derivedFrom":sQuery(id+"F4.wireOp",EDGE,"E759.0.0.5")}),1.0]])]});
            extrude(context, id + "F5", {"entities" : qUnion([Q0, Q1, Q2, Q3, Q4, Q5, Q6, Q7, Q8, Q9, Q10, Q11, Q12, Q13, Q14, Q15, Q16, Q17, Q18, Q19, Q20, Q21, Q22, Q23, Q24, Q25, Q26, Q27, Q28, Q29, Q30, Q31, Q32, Q33, Q34, Q35]), "operationType" : NewBodyOperationType.REMOVE, "oppositeDirection" : true, "depth" : 6.35 * mm});
        }
        {
            var Q0;
            Q0=makeQuery(id+"F5.boolean.opBoolean","COPY",EDGE,{"derivedFrom":makeQuery(id+"F5.opExtrude","CAP_EDGE",EDGE,{"disambiguationData":[OSD([sQuery(id+"F4.wireOp",EDGE,"E756")])],"isStart":false})});
            var Q1;
            Q1=makeQuery(id+"F5.boolean.opBoolean","COPY",EDGE,{"derivedFrom":makeQuery(id+"F5.opExtrude","CAP_EDGE",EDGE,{"disambiguationData":[OSD([sQuery(id+"F4.wireOp",EDGE,"E757.0.1.0")])],"isStart":false})});
            var Q2;
            Q2=makeQuery(id+"F5.boolean.opBoolean","COPY",FACE,{"derivedFrom":makeQuery(id+"F5.opExtrude","CAP_FACE",FACE,{"disambiguationData":[OSD([sQuery(id+"F4.wireOp",EDGE,"E757.1.0.0")])],"isStart":false})});
            var Q3;
            Q3=makeQuery(id+"F5.boolean.opBoolean","COPY",EDGE,{"derivedFrom":makeQuery(id+"F5.opExtrude","CAP_EDGE",EDGE,{"disambiguationData":[OSD([sQuery(id+"F4.wireOp",EDGE,"E757.1.1.0")])],"isStart":false})});
            var Q4;
            Q4=makeQuery(id+"F5.boolean.opBoolean","COPY",EDGE,{"derivedFrom":makeQuery(id+"F5.opExtrude","CAP_EDGE",EDGE,{"disambiguationData":[OSD([sQuery(id+"F4.wireOp",EDGE,"E757.2.1.0")])],"isStart":false})});
            var Q5;
            Q5=makeQuery(id+"F5.boolean.opBoolean","COPY",EDGE,{"derivedFrom":makeQuery(id+"F5.opExtrude","CAP_EDGE",EDGE,{"disambiguationData":[OSD([sQuery(id+"F4.wireOp",EDGE,"E757.2.0.0")])],"isStart":false})});
            var Q6;
            Q6=makeQuery(id+"F5.boolean.opBoolean","COPY",FACE,{"derivedFrom":makeQuery(id+"F5.opExtrude","CAP_FACE",FACE,{"disambiguationData":[OSD([sQuery(id+"F4.wireOp",EDGE,"E757.3.0.0")])],"isStart":false})});
            var Q7;
            Q7=makeQuery(id+"F5.boolean.opBoolean","COPY",EDGE,{"derivedFrom":makeQuery(id+"F5.opExtrude","CAP_EDGE",EDGE,{"disambiguationData":[OSD([sQuery(id+"F4.wireOp",EDGE,"E757.3.1.0")])],"isStart":false})});
            var Q8;
            Q8=makeQuery(id+"F5.boolean.opBoolean","COPY",FACE,{"derivedFrom":makeQuery(id+"F5.opExtrude","CAP_FACE",FACE,{"disambiguationData":[OSD([sQuery(id+"F4.wireOp",EDGE,"E758.0.4.0")])],"isStart":false})});
            var Q9;
            Q9=makeQuery(id+"F5.boolean.opBoolean","COPY",EDGE,{"derivedFrom":makeQuery(id+"F5.opExtrude","CAP_EDGE",EDGE,{"disambiguationData":[OSD([sQuery(id+"F4.wireOp",EDGE,"E758.0.4.1")])],"isStart":false})});
            var Q10;
            Q10=makeQuery(id+"F5.boolean.opBoolean","COPY",EDGE,{"derivedFrom":makeQuery(id+"F5.opExtrude","CAP_EDGE",EDGE,{"disambiguationData":[OSD([sQuery(id+"F4.wireOp",EDGE,"E758.0.4.2")])],"isStart":false})});
            var Q11;
            Q11=makeQuery(id+"F5.boolean.opBoolean","COPY",FACE,{"derivedFrom":makeQuery(id+"F5.opExtrude","CAP_FACE",FACE,{"disambiguationData":[OSD([sQuery(id+"F4.wireOp",EDGE,"E757.3.2.0")])],"isStart":false})});
            var Q12;
            Q12=makeQuery(id+"F5.boolean.opBoolean","COPY",FACE,{"derivedFrom":makeQuery(id+"F5.opExtrude","CAP_FACE",FACE,{"disambiguationData":[OSD([sQuery(id+"F4.wireOp",EDGE,"E757.2.2.0")])],"isStart":false})});
            var Q13;
            Q13=makeQuery(id+"F5.boolean.opBoolean","COPY",FACE,{"derivedFrom":makeQuery(id+"F5.opExtrude","CAP_FACE",FACE,{"disambiguationData":[OSD([sQuery(id+"F4.wireOp",EDGE,"E757.1.2.0")])],"isStart":false})});
            var Q14;
            Q14=makeQuery(id+"F5.boolean.opBoolean","COPY",FACE,{"derivedFrom":makeQuery(id+"F5.opExtrude","CAP_FACE",FACE,{"disambiguationData":[OSD([sQuery(id+"F4.wireOp",EDGE,"E757.0.2.0")])],"isStart":false})});
            var Q15;
            Q15=makeQuery(id+"F5.boolean.opBoolean","COPY",FACE,{"derivedFrom":makeQuery(id+"F5.opExtrude","CAP_FACE",FACE,{"disambiguationData":[OSD([sQuery(id+"F4.wireOp",EDGE,"E757.0.3.0")])],"isStart":false})});
            var Q16;
            Q16=makeQuery(id+"F5.boolean.opBoolean","COPY",FACE,{"derivedFrom":makeQuery(id+"F5.opExtrude","CAP_FACE",FACE,{"disambiguationData":[OSD([sQuery(id+"F4.wireOp",EDGE,"E757.1.3.0")])],"isStart":false})});
            var Q17;
            Q17=makeQuery(id+"F5.boolean.opBoolean","COPY",FACE,{"derivedFrom":makeQuery(id+"F5.opExtrude","CAP_FACE",FACE,{"disambiguationData":[OSD([sQuery(id+"F4.wireOp",EDGE,"E757.2.3.0")])],"isStart":false})});
            var Q18;
            Q18=makeQuery(id+"F5.boolean.opBoolean","COPY",FACE,{"derivedFrom":makeQuery(id+"F5.opExtrude","CAP_FACE",FACE,{"disambiguationData":[OSD([sQuery(id+"F4.wireOp",EDGE,"E757.3.3.0")])],"isStart":false})});
            var Q19;
            Q19=makeQuery(id+"F5.boolean.opBoolean","COPY",FACE,{"derivedFrom":makeQuery(id+"F5.opExtrude","CAP_FACE",FACE,{"disambiguationData":[OSD([sQuery(id+"F4.wireOp",EDGE,"E758.0.4.3")])],"isStart":false})});
            var Q20;
            Q20=makeQuery(id+"F5.boolean.opBoolean","COPY",FACE,{"derivedFrom":makeQuery(id+"F5.opExtrude","CAP_FACE",FACE,{"disambiguationData":[OSD([sQuery(id+"F4.wireOp",EDGE,"E759.0.3.4")])],"isStart":false})});
            var Q21;
            Q21=makeQuery(id+"F5.boolean.opBoolean","COPY",FACE,{"derivedFrom":makeQuery(id+"F5.opExtrude","CAP_FACE",FACE,{"disambiguationData":[OSD([sQuery(id+"F4.wireOp",EDGE,"E759.0.2.4")])],"isStart":false})});
            var Q22;
            Q22=makeQuery(id+"F5.boolean.opBoolean","COPY",FACE,{"derivedFrom":makeQuery(id+"F5.opExtrude","CAP_FACE",FACE,{"disambiguationData":[OSD([sQuery(id+"F4.wireOp",EDGE,"E759.0.1.4")])],"isStart":false})});
            var Q23;
            Q23=makeQuery(id+"F5.boolean.opBoolean","COPY",FACE,{"derivedFrom":makeQuery(id+"F5.opExtrude","CAP_FACE",FACE,{"disambiguationData":[OSD([sQuery(id+"F4.wireOp",EDGE,"E759.0.0.4")])],"isStart":false})});
            var Q24;
            Q24=makeQuery(id+"F5.boolean.opBoolean","COPY",FACE,{"derivedFrom":makeQuery(id+"F5.opExtrude","CAP_FACE",FACE,{"disambiguationData":[OSD([sQuery(id+"F4.wireOp",EDGE,"E759.0.0.5")])],"isStart":false})});
            var Q25;
            Q25=makeQuery(id+"F5.boolean.opBoolean","COPY",FACE,{"derivedFrom":makeQuery(id+"F5.opExtrude","CAP_FACE",FACE,{"disambiguationData":[OSD([sQuery(id+"F4.wireOp",EDGE,"E759.0.1.5")])],"isStart":false})});
            var Q26;
            Q26=makeQuery(id+"F5.boolean.opBoolean","COPY",FACE,{"derivedFrom":makeQuery(id+"F5.opExtrude","CAP_FACE",FACE,{"disambiguationData":[OSD([sQuery(id+"F4.wireOp",EDGE,"E759.0.2.5")])],"isStart":false})});
            var Q27;
            Q27=makeQuery(id+"F5.boolean.opBoolean","COPY",FACE,{"derivedFrom":makeQuery(id+"F5.opExtrude","CAP_FACE",FACE,{"disambiguationData":[OSD([sQuery(id+"F4.wireOp",EDGE,"E759.0.3.5")])],"isStart":false})});
            var Q28;
            Q28=makeQuery(id+"F5.boolean.opBoolean","COPY",FACE,{"derivedFrom":makeQuery(id+"F5.opExtrude","CAP_FACE",FACE,{"disambiguationData":[OSD([sQuery(id+"F4.wireOp",EDGE,"E759.0.4.5")])],"isStart":false})});
            var Q29;
            Q29=makeQuery(id+"F5.boolean.opBoolean","COPY",FACE,{"derivedFrom":makeQuery(id+"F5.opExtrude","CAP_FACE",FACE,{"disambiguationData":[OSD([sQuery(id+"F4.wireOp",EDGE,"E759.0.4.4")])],"isStart":false})});
            var Q30;
            Q30=makeQuery(id+"F5.boolean.opBoolean","COPY",FACE,{"derivedFrom":makeQuery(id+"F5.opExtrude","CAP_FACE",FACE,{"disambiguationData":[OSD([sQuery(id+"F4.wireOp",EDGE,"E758.0.5.0")])],"isStart":false})});
            var Q31;
            Q31=makeQuery(id+"F5.boolean.opBoolean","COPY",FACE,{"derivedFrom":makeQuery(id+"F5.opExtrude","CAP_FACE",FACE,{"disambiguationData":[OSD([sQuery(id+"F4.wireOp",EDGE,"E758.0.5.1")])],"isStart":false})});
            var Q32;
            Q32=makeQuery(id+"F5.boolean.opBoolean","COPY",EDGE,{"derivedFrom":makeQuery(id+"F5.opExtrude","CAP_EDGE",EDGE,{"disambiguationData":[OSD([sQuery(id+"F4.wireOp",EDGE,"E758.0.5.2")])],"isStart":false})});
            var Q33;
            Q33=makeQuery(id+"F5.boolean.opBoolean","COPY",FACE,{"derivedFrom":makeQuery(id+"F5.opExtrude","CAP_FACE",FACE,{"disambiguationData":[OSD([sQuery(id+"F4.wireOp",EDGE,"E758.0.5.3")])],"isStart":false})});
            var Q34;
            Q34=makeQuery(id+"F5.boolean.opBoolean","COPY",FACE,{"derivedFrom":makeQuery(id+"F5.opExtrude","CAP_FACE",FACE,{"disambiguationData":[OSD([sQuery(id+"F4.wireOp",EDGE,"E759.0.5.4")])],"isStart":false})});
            var Q35;
            Q35=makeQuery(id+"F5.boolean.opBoolean","COPY",FACE,{"derivedFrom":makeQuery(id+"F5.opExtrude","CAP_FACE",FACE,{"disambiguationData":[OSD([sQuery(id+"F4.wireOp",EDGE,"E759.0.5.5")])],"isStart":false})});
            fillet(context, id + "F6", {"entities" : qUnion([Q0, Q1, Q2, Q3, Q4, Q5, Q6, Q7, Q8, Q9, Q10, Q11, Q12, Q13, Q14, Q15, Q16, Q17, Q18, Q19, Q20, Q21, Q22, Q23, Q24, Q25, Q26, Q27, Q28, Q29, Q30, Q31, Q32, Q33, Q34, Q35]), "radius" : 154.94 * mm, "tangentPropagation" : true, "allowEdgeOverflow" : false});
        }
        {
            var Q0;
            Q0=makeQuery(id+"F6.opFillet","BLEND_EDGE",EDGE,{"blendedFrom":[makeQuery(id+"F5.boolean.opBoolean","COPY",EDGE,{"derivedFrom":makeQuery(id+"F5.opExtrude","CAP_EDGE",EDGE,{"disambiguationData":[OSD([sQuery(id+"F4.wireOp",EDGE,"E757.3.3.0")])],"isStart":false})}),makeQuery(id+"F1.opExtrude","CAP_FACE",FACE,{"disambiguationData":[OSD([sQuery(id+"F0.wireOp",EDGE,"E0"),sQuery(id+"F0.wireOp",EDGE,"E1"),sQuery(id+"F0.wireOp",EDGE,"E2"),sQuery(id+"F0.wireOp",EDGE,"E3"),sQuery(id+"F0.wireOp",EDGE,"E4"),sQuery(id+"F0.wireOp",EDGE,"E5"),sQuery(id+"F0.wireOp",EDGE,"E6"),sQuery(id+"F0.wireOp",EDGE,"E7"),sQuery(id+"F0.wireOp",EDGE,"E8"),sQuery(id+"F0.wireOp",EDGE,"E9"),sQuery(id+"F0.wireOp",EDGE,"E10"),sQuery(id+"F0.wireOp",EDGE,"E11"),sQuery(id+"F0.wireOp",EDGE,"E12"),sQuery(id+"F0.wireOp",EDGE,"E13"),sQuery(id+"F0.wireOp",EDGE,"E14"),sQuery(id+"F0.wireOp",EDGE,"E15"),sQuery(id+"F0.wireOp",EDGE,"E16"),sQuery(id+"F0.wireOp",EDGE,"E17"),sQuery(id+"F0.wireOp",EDGE,"E18"),sQuery(id+"F0.wireOp",EDGE,"E19"),sQuery(id+"F0.wireOp",EDGE,"E20"),sQuery(id+"F0.wireOp",EDGE,"E21"),sQuery(id+"F0.wireOp",EDGE,"E22"),sQuery(id+"F0.wireOp",EDGE,"E23"),sQuery(id+"F0.wireOp",EDGE,"E24"),sQuery(id+"F0.wireOp",EDGE,"E25"),sQuery(id+"F0.wireOp",EDGE,"E26"),sQuery(id+"F0.wireOp",EDGE,"E27"),sQuery(id+"F0.wireOp",EDGE,"E28"),sQuery(id+"F0.wireOp",EDGE,"E29"),sQuery(id+"F0.wireOp",EDGE,"E30"),sQuery(id+"F0.wireOp",EDGE,"E31"),sQuery(id+"F0.wireOp",EDGE,"E32"),sQuery(id+"F0.wireOp",EDGE,"E33"),sQuery(id+"F0.wireOp",EDGE,"E34"),sQuery(id+"F0.wireOp",EDGE,"E35"),sQuery(id+"F0.wireOp",EDGE,"E36"),sQuery(id+"F0.wireOp",EDGE,"E37"),sQuery(id+"F0.wireOp",EDGE,"E38"),sQuery(id+"F0.wireOp",EDGE,"E39"),sQuery(id+"F0.wireOp",EDGE,"E40"),sQuery(id+"F0.wireOp",EDGE,"E41"),sQuery(id+"F0.wireOp",EDGE,"E42"),sQuery(id+"F0.wireOp",EDGE,"E43"),sQuery(id+"F0.wireOp",EDGE,"E44"),sQuery(id+"F0.wireOp",EDGE,"E45"),sQuery(id+"F0.wireOp",EDGE,"E46"),sQuery(id+"F0.wireOp",EDGE,"E47"),sQuery(id+"F0.wireOp",EDGE,"E48"),sQuery(id+"F0.wireOp",EDGE,"E49"),sQuery(id+"F0.wireOp",EDGE,"E50"),sQuery(id+"F0.wireOp",EDGE,"E51"),sQuery(id+"F0.wireOp",EDGE,"E52"),sQuery(id+"F0.wireOp",EDGE,"E53"),sQuery(id+"F0.wireOp",EDGE,"E54"),sQuery(id+"F0.wireOp",EDGE,"E55"),sQuery(id+"F0.wireOp",EDGE,"E56"),sQuery(id+"F0.wireOp",EDGE,"E57"),sQuery(id+"F0.wireOp",EDGE,"E58"),sQuery(id+"F0.wireOp",EDGE,"E59"),sQuery(id+"F0.wireOp",EDGE,"E60"),sQuery(id+"F0.wireOp",EDGE,"E61"),sQuery(id+"F0.wireOp",EDGE,"E62"),sQuery(id+"F0.wireOp",EDGE,"E63"),sQuery(id+"F0.wireOp",EDGE,"E64"),sQuery(id+"F0.wireOp",EDGE,"E65"),sQuery(id+"F0.wireOp",EDGE,"E66"),sQuery(id+"F0.wireOp",EDGE,"E67"),sQuery(id+"F0.wireOp",EDGE,"E68"),sQuery(id+"F0.wireOp",EDGE,"E69"),sQuery(id+"F0.wireOp",EDGE,"E70"),sQuery(id+"F0.wireOp",EDGE,"E71"),sQuery(id+"F0.wireOp",EDGE,"E72"),sQuery(id+"F0.wireOp",EDGE,"E73"),sQuery(id+"F0.wireOp",EDGE,"E74"),sQuery(id+"F0.wireOp",EDGE,"E75"),sQuery(id+"F0.wireOp",EDGE,"E76"),sQuery(id+"F0.wireOp",EDGE,"E77"),sQuery(id+"F0.wireOp",EDGE,"E78"),sQuery(id+"F0.wireOp",EDGE,"E79"),sQuery(id+"F0.wireOp",EDGE,"E80"),sQuery(id+"F0.wireOp",EDGE,"E81"),sQuery(id+"F0.wireOp",EDGE,"E82"),sQuery(id+"F0.wireOp",EDGE,"E83"),sQuery(id+"F0.wireOp",EDGE,"E84"),sQuery(id+"F0.wireOp",EDGE,"E85"),sQuery(id+"F0.wireOp",EDGE,"E86"),sQuery(id+"F0.wireOp",EDGE,"E87"),sQuery(id+"F0.wireOp",EDGE,"E88"),sQuery(id+"F0.wireOp",EDGE,"E89"),sQuery(id+"F0.wireOp",EDGE,"E90"),sQuery(id+"F0.wireOp",EDGE,"E91"),sQuery(id+"F0.wireOp",EDGE,"E92"),sQuery(id+"F0.wireOp",EDGE,"E93"),sQuery(id+"F0.wireOp",EDGE,"E94"),sQuery(id+"F0.wireOp",EDGE,"E95"),sQuery(id+"F0.wireOp",EDGE,"E96"),sQuery(id+"F0.wireOp",EDGE,"E97"),sQuery(id+"F0.wireOp",EDGE,"E98"),sQuery(id+"F0.wireOp",EDGE,"E99"),sQuery(id+"F0.wireOp",EDGE,"E100"),sQuery(id+"F0.wireOp",EDGE,"E101"),sQuery(id+"F0.wireOp",EDGE,"E102"),sQuery(id+"F0.wireOp",EDGE,"E103"),sQuery(id+"F0.wireOp",EDGE,"E104"),sQuery(id+"F0.wireOp",EDGE,"E105"),sQuery(id+"F0.wireOp",EDGE,"E106"),sQuery(id+"F0.wireOp",EDGE,"E107"),sQuery(id+"F0.wireOp",EDGE,"E108"),sQuery(id+"F0.wireOp",EDGE,"E109"),sQuery(id+"F0.wireOp",EDGE,"E110"),sQuery(id+"F0.wireOp",EDGE,"E111"),sQuery(id+"F0.wireOp",EDGE,"E112"),sQuery(id+"F0.wireOp",EDGE,"E113"),sQuery(id+"F0.wireOp",EDGE,"E114"),sQuery(id+"F0.wireOp",EDGE,"E115")])],"isStart":false})],"blendedInto":[makeQuery(id+"F1.opExtrude","CAP_FACE",FACE,{"disambiguationData":[OSD([sQuery(id+"F0.wireOp",EDGE,"E0"),sQuery(id+"F0.wireOp",EDGE,"E1"),sQuery(id+"F0.wireOp",EDGE,"E2"),sQuery(id+"F0.wireOp",EDGE,"E3"),sQuery(id+"F0.wireOp",EDGE,"E4"),sQuery(id+"F0.wireOp",EDGE,"E5"),sQuery(id+"F0.wireOp",EDGE,"E6"),sQuery(id+"F0.wireOp",EDGE,"E7"),sQuery(id+"F0.wireOp",EDGE,"E8"),sQuery(id+"F0.wireOp",EDGE,"E9"),sQuery(id+"F0.wireOp",EDGE,"E10"),sQuery(id+"F0.wireOp",EDGE,"E11"),sQuery(id+"F0.wireOp",EDGE,"E12"),sQuery(id+"F0.wireOp",EDGE,"E13"),sQuery(id+"F0.wireOp",EDGE,"E14"),sQuery(id+"F0.wireOp",EDGE,"E15"),sQuery(id+"F0.wireOp",EDGE,"E16"),sQuery(id+"F0.wireOp",EDGE,"E17"),sQuery(id+"F0.wireOp",EDGE,"E18"),sQuery(id+"F0.wireOp",EDGE,"E19"),sQuery(id+"F0.wireOp",EDGE,"E20"),sQuery(id+"F0.wireOp",EDGE,"E21"),sQuery(id+"F0.wireOp",EDGE,"E22"),sQuery(id+"F0.wireOp",EDGE,"E23"),sQuery(id+"F0.wireOp",EDGE,"E24"),sQuery(id+"F0.wireOp",EDGE,"E25"),sQuery(id+"F0.wireOp",EDGE,"E26"),sQuery(id+"F0.wireOp",EDGE,"E27"),sQuery(id+"F0.wireOp",EDGE,"E28"),sQuery(id+"F0.wireOp",EDGE,"E29"),sQuery(id+"F0.wireOp",EDGE,"E30"),sQuery(id+"F0.wireOp",EDGE,"E31"),sQuery(id+"F0.wireOp",EDGE,"E32"),sQuery(id+"F0.wireOp",EDGE,"E33"),sQuery(id+"F0.wireOp",EDGE,"E34"),sQuery(id+"F0.wireOp",EDGE,"E35"),sQuery(id+"F0.wireOp",EDGE,"E36"),sQuery(id+"F0.wireOp",EDGE,"E37"),sQuery(id+"F0.wireOp",EDGE,"E38"),sQuery(id+"F0.wireOp",EDGE,"E39"),sQuery(id+"F0.wireOp",EDGE,"E40"),sQuery(id+"F0.wireOp",EDGE,"E41"),sQuery(id+"F0.wireOp",EDGE,"E42"),sQuery(id+"F0.wireOp",EDGE,"E43"),sQuery(id+"F0.wireOp",EDGE,"E44"),sQuery(id+"F0.wireOp",EDGE,"E45"),sQuery(id+"F0.wireOp",EDGE,"E46"),sQuery(id+"F0.wireOp",EDGE,"E47"),sQuery(id+"F0.wireOp",EDGE,"E48"),sQuery(id+"F0.wireOp",EDGE,"E49"),sQuery(id+"F0.wireOp",EDGE,"E50"),sQuery(id+"F0.wireOp",EDGE,"E51"),sQuery(id+"F0.wireOp",EDGE,"E52"),sQuery(id+"F0.wireOp",EDGE,"E53"),sQuery(id+"F0.wireOp",EDGE,"E54"),sQuery(id+"F0.wireOp",EDGE,"E55"),sQuery(id+"F0.wireOp",EDGE,"E56"),sQuery(id+"F0.wireOp",EDGE,"E57"),sQuery(id+"F0.wireOp",EDGE,"E58"),sQuery(id+"F0.wireOp",EDGE,"E59"),sQuery(id+"F0.wireOp",EDGE,"E60"),sQuery(id+"F0.wireOp",EDGE,"E61"),sQuery(id+"F0.wireOp",EDGE,"E62"),sQuery(id+"F0.wireOp",EDGE,"E63"),sQuery(id+"F0.wireOp",EDGE,"E64"),sQuery(id+"F0.wireOp",EDGE,"E65"),sQuery(id+"F0.wireOp",EDGE,"E66"),sQuery(id+"F0.wireOp",EDGE,"E67"),sQuery(id+"F0.wireOp",EDGE,"E68"),sQuery(id+"F0.wireOp",EDGE,"E69"),sQuery(id+"F0.wireOp",EDGE,"E70"),sQuery(id+"F0.wireOp",EDGE,"E71"),sQuery(id+"F0.wireOp",EDGE,"E72"),sQuery(id+"F0.wireOp",EDGE,"E73"),sQuery(id+"F0.wireOp",EDGE,"E74"),sQuery(id+"F0.wireOp",EDGE,"E75"),sQuery(id+"F0.wireOp",EDGE,"E76"),sQuery(id+"F0.wireOp",EDGE,"E77"),sQuery(id+"F0.wireOp",EDGE,"E78"),sQuery(id+"F0.wireOp",EDGE,"E79"),sQuery(id+"F0.wireOp",EDGE,"E80"),sQuery(id+"F0.wireOp",EDGE,"E81"),sQuery(id+"F0.wireOp",EDGE,"E82"),sQuery(id+"F0.wireOp",EDGE,"E83"),sQuery(id+"F0.wireOp",EDGE,"E84"),sQuery(id+"F0.wireOp",EDGE,"E85"),sQuery(id+"F0.wireOp",EDGE,"E86"),sQuery(id+"F0.wireOp",EDGE,"E87"),sQuery(id+"F0.wireOp",EDGE,"E88"),sQuery(id+"F0.wireOp",EDGE,"E89"),sQuery(id+"F0.wireOp",EDGE,"E90"),sQuery(id+"F0.wireOp",EDGE,"E91"),sQuery(id+"F0.wireOp",EDGE,"E92"),sQuery(id+"F0.wireOp",EDGE,"E93"),sQuery(id+"F0.wireOp",EDGE,"E94"),sQuery(id+"F0.wireOp",EDGE,"E95"),sQuery(id+"F0.wireOp",EDGE,"E96"),sQuery(id+"F0.wireOp",EDGE,"E97"),sQuery(id+"F0.wireOp",EDGE,"E98"),sQuery(id+"F0.wireOp",EDGE,"E99"),sQuery(id+"F0.wireOp",EDGE,"E100"),sQuery(id+"F0.wireOp",EDGE,"E101"),sQuery(id+"F0.wireOp",EDGE,"E102"),sQuery(id+"F0.wireOp",EDGE,"E103"),sQuery(id+"F0.wireOp",EDGE,"E104"),sQuery(id+"F0.wireOp",EDGE,"E105"),sQuery(id+"F0.wireOp",EDGE,"E106"),sQuery(id+"F0.wireOp",EDGE,"E107"),sQuery(id+"F0.wireOp",EDGE,"E108"),sQuery(id+"F0.wireOp",EDGE,"E109"),sQuery(id+"F0.wireOp",EDGE,"E110"),sQuery(id+"F0.wireOp",EDGE,"E111"),sQuery(id+"F0.wireOp",EDGE,"E112"),sQuery(id+"F0.wireOp",EDGE,"E113"),sQuery(id+"F0.wireOp",EDGE,"E114"),sQuery(id+"F0.wireOp",EDGE,"E115")])],"isStart":false})]});
            var Q1;
            Q1=makeQuery(id+"F6.opFillet","BLEND_EDGE",EDGE,{"blendedFrom":[makeQuery(id+"F5.boolean.opBoolean","COPY",EDGE,{"derivedFrom":makeQuery(id+"F5.opExtrude","CAP_EDGE",EDGE,{"disambiguationData":[OSD([sQuery(id+"F4.wireOp",EDGE,"E758.0.4.3")])],"isStart":false})}),makeQuery(id+"F1.opExtrude","CAP_FACE",FACE,{"disambiguationData":[OSD([sQuery(id+"F0.wireOp",EDGE,"E0"),sQuery(id+"F0.wireOp",EDGE,"E1"),sQuery(id+"F0.wireOp",EDGE,"E2"),sQuery(id+"F0.wireOp",EDGE,"E3"),sQuery(id+"F0.wireOp",EDGE,"E4"),sQuery(id+"F0.wireOp",EDGE,"E5"),sQuery(id+"F0.wireOp",EDGE,"E6"),sQuery(id+"F0.wireOp",EDGE,"E7"),sQuery(id+"F0.wireOp",EDGE,"E8"),sQuery(id+"F0.wireOp",EDGE,"E9"),sQuery(id+"F0.wireOp",EDGE,"E10"),sQuery(id+"F0.wireOp",EDGE,"E11"),sQuery(id+"F0.wireOp",EDGE,"E12"),sQuery(id+"F0.wireOp",EDGE,"E13"),sQuery(id+"F0.wireOp",EDGE,"E14"),sQuery(id+"F0.wireOp",EDGE,"E15"),sQuery(id+"F0.wireOp",EDGE,"E16"),sQuery(id+"F0.wireOp",EDGE,"E17"),sQuery(id+"F0.wireOp",EDGE,"E18"),sQuery(id+"F0.wireOp",EDGE,"E19"),sQuery(id+"F0.wireOp",EDGE,"E20"),sQuery(id+"F0.wireOp",EDGE,"E21"),sQuery(id+"F0.wireOp",EDGE,"E22"),sQuery(id+"F0.wireOp",EDGE,"E23"),sQuery(id+"F0.wireOp",EDGE,"E24"),sQuery(id+"F0.wireOp",EDGE,"E25"),sQuery(id+"F0.wireOp",EDGE,"E26"),sQuery(id+"F0.wireOp",EDGE,"E27"),sQuery(id+"F0.wireOp",EDGE,"E28"),sQuery(id+"F0.wireOp",EDGE,"E29"),sQuery(id+"F0.wireOp",EDGE,"E30"),sQuery(id+"F0.wireOp",EDGE,"E31"),sQuery(id+"F0.wireOp",EDGE,"E32"),sQuery(id+"F0.wireOp",EDGE,"E33"),sQuery(id+"F0.wireOp",EDGE,"E34"),sQuery(id+"F0.wireOp",EDGE,"E35"),sQuery(id+"F0.wireOp",EDGE,"E36"),sQuery(id+"F0.wireOp",EDGE,"E37"),sQuery(id+"F0.wireOp",EDGE,"E38"),sQuery(id+"F0.wireOp",EDGE,"E39"),sQuery(id+"F0.wireOp",EDGE,"E40"),sQuery(id+"F0.wireOp",EDGE,"E41"),sQuery(id+"F0.wireOp",EDGE,"E42"),sQuery(id+"F0.wireOp",EDGE,"E43"),sQuery(id+"F0.wireOp",EDGE,"E44"),sQuery(id+"F0.wireOp",EDGE,"E45"),sQuery(id+"F0.wireOp",EDGE,"E46"),sQuery(id+"F0.wireOp",EDGE,"E47"),sQuery(id+"F0.wireOp",EDGE,"E48"),sQuery(id+"F0.wireOp",EDGE,"E49"),sQuery(id+"F0.wireOp",EDGE,"E50"),sQuery(id+"F0.wireOp",EDGE,"E51"),sQuery(id+"F0.wireOp",EDGE,"E52"),sQuery(id+"F0.wireOp",EDGE,"E53"),sQuery(id+"F0.wireOp",EDGE,"E54"),sQuery(id+"F0.wireOp",EDGE,"E55"),sQuery(id+"F0.wireOp",EDGE,"E56"),sQuery(id+"F0.wireOp",EDGE,"E57"),sQuery(id+"F0.wireOp",EDGE,"E58"),sQuery(id+"F0.wireOp",EDGE,"E59"),sQuery(id+"F0.wireOp",EDGE,"E60"),sQuery(id+"F0.wireOp",EDGE,"E61"),sQuery(id+"F0.wireOp",EDGE,"E62"),sQuery(id+"F0.wireOp",EDGE,"E63"),sQuery(id+"F0.wireOp",EDGE,"E64"),sQuery(id+"F0.wireOp",EDGE,"E65"),sQuery(id+"F0.wireOp",EDGE,"E66"),sQuery(id+"F0.wireOp",EDGE,"E67"),sQuery(id+"F0.wireOp",EDGE,"E68"),sQuery(id+"F0.wireOp",EDGE,"E69"),sQuery(id+"F0.wireOp",EDGE,"E70"),sQuery(id+"F0.wireOp",EDGE,"E71"),sQuery(id+"F0.wireOp",EDGE,"E72"),sQuery(id+"F0.wireOp",EDGE,"E73"),sQuery(id+"F0.wireOp",EDGE,"E74"),sQuery(id+"F0.wireOp",EDGE,"E75"),sQuery(id+"F0.wireOp",EDGE,"E76"),sQuery(id+"F0.wireOp",EDGE,"E77"),sQuery(id+"F0.wireOp",EDGE,"E78"),sQuery(id+"F0.wireOp",EDGE,"E79"),sQuery(id+"F0.wireOp",EDGE,"E80"),sQuery(id+"F0.wireOp",EDGE,"E81"),sQuery(id+"F0.wireOp",EDGE,"E82"),sQuery(id+"F0.wireOp",EDGE,"E83"),sQuery(id+"F0.wireOp",EDGE,"E84"),sQuery(id+"F0.wireOp",EDGE,"E85"),sQuery(id+"F0.wireOp",EDGE,"E86"),sQuery(id+"F0.wireOp",EDGE,"E87"),sQuery(id+"F0.wireOp",EDGE,"E88"),sQuery(id+"F0.wireOp",EDGE,"E89"),sQuery(id+"F0.wireOp",EDGE,"E90"),sQuery(id+"F0.wireOp",EDGE,"E91"),sQuery(id+"F0.wireOp",EDGE,"E92"),sQuery(id+"F0.wireOp",EDGE,"E93"),sQuery(id+"F0.wireOp",EDGE,"E94"),sQuery(id+"F0.wireOp",EDGE,"E95"),sQuery(id+"F0.wireOp",EDGE,"E96"),sQuery(id+"F0.wireOp",EDGE,"E97"),sQuery(id+"F0.wireOp",EDGE,"E98"),sQuery(id+"F0.wireOp",EDGE,"E99"),sQuery(id+"F0.wireOp",EDGE,"E100"),sQuery(id+"F0.wireOp",EDGE,"E101"),sQuery(id+"F0.wireOp",EDGE,"E102"),sQuery(id+"F0.wireOp",EDGE,"E103"),sQuery(id+"F0.wireOp",EDGE,"E104"),sQuery(id+"F0.wireOp",EDGE,"E105"),sQuery(id+"F0.wireOp",EDGE,"E106"),sQuery(id+"F0.wireOp",EDGE,"E107"),sQuery(id+"F0.wireOp",EDGE,"E108"),sQuery(id+"F0.wireOp",EDGE,"E109"),sQuery(id+"F0.wireOp",EDGE,"E110"),sQuery(id+"F0.wireOp",EDGE,"E111"),sQuery(id+"F0.wireOp",EDGE,"E112"),sQuery(id+"F0.wireOp",EDGE,"E113"),sQuery(id+"F0.wireOp",EDGE,"E114"),sQuery(id+"F0.wireOp",EDGE,"E115")])],"isStart":false})],"blendedInto":[makeQuery(id+"F1.opExtrude","CAP_FACE",FACE,{"disambiguationData":[OSD([sQuery(id+"F0.wireOp",EDGE,"E0"),sQuery(id+"F0.wireOp",EDGE,"E1"),sQuery(id+"F0.wireOp",EDGE,"E2"),sQuery(id+"F0.wireOp",EDGE,"E3"),sQuery(id+"F0.wireOp",EDGE,"E4"),sQuery(id+"F0.wireOp",EDGE,"E5"),sQuery(id+"F0.wireOp",EDGE,"E6"),sQuery(id+"F0.wireOp",EDGE,"E7"),sQuery(id+"F0.wireOp",EDGE,"E8"),sQuery(id+"F0.wireOp",EDGE,"E9"),sQuery(id+"F0.wireOp",EDGE,"E10"),sQuery(id+"F0.wireOp",EDGE,"E11"),sQuery(id+"F0.wireOp",EDGE,"E12"),sQuery(id+"F0.wireOp",EDGE,"E13"),sQuery(id+"F0.wireOp",EDGE,"E14"),sQuery(id+"F0.wireOp",EDGE,"E15"),sQuery(id+"F0.wireOp",EDGE,"E16"),sQuery(id+"F0.wireOp",EDGE,"E17"),sQuery(id+"F0.wireOp",EDGE,"E18"),sQuery(id+"F0.wireOp",EDGE,"E19"),sQuery(id+"F0.wireOp",EDGE,"E20"),sQuery(id+"F0.wireOp",EDGE,"E21"),sQuery(id+"F0.wireOp",EDGE,"E22"),sQuery(id+"F0.wireOp",EDGE,"E23"),sQuery(id+"F0.wireOp",EDGE,"E24"),sQuery(id+"F0.wireOp",EDGE,"E25"),sQuery(id+"F0.wireOp",EDGE,"E26"),sQuery(id+"F0.wireOp",EDGE,"E27"),sQuery(id+"F0.wireOp",EDGE,"E28"),sQuery(id+"F0.wireOp",EDGE,"E29"),sQuery(id+"F0.wireOp",EDGE,"E30"),sQuery(id+"F0.wireOp",EDGE,"E31"),sQuery(id+"F0.wireOp",EDGE,"E32"),sQuery(id+"F0.wireOp",EDGE,"E33"),sQuery(id+"F0.wireOp",EDGE,"E34"),sQuery(id+"F0.wireOp",EDGE,"E35"),sQuery(id+"F0.wireOp",EDGE,"E36"),sQuery(id+"F0.wireOp",EDGE,"E37"),sQuery(id+"F0.wireOp",EDGE,"E38"),sQuery(id+"F0.wireOp",EDGE,"E39"),sQuery(id+"F0.wireOp",EDGE,"E40"),sQuery(id+"F0.wireOp",EDGE,"E41"),sQuery(id+"F0.wireOp",EDGE,"E42"),sQuery(id+"F0.wireOp",EDGE,"E43"),sQuery(id+"F0.wireOp",EDGE,"E44"),sQuery(id+"F0.wireOp",EDGE,"E45"),sQuery(id+"F0.wireOp",EDGE,"E46"),sQuery(id+"F0.wireOp",EDGE,"E47"),sQuery(id+"F0.wireOp",EDGE,"E48"),sQuery(id+"F0.wireOp",EDGE,"E49"),sQuery(id+"F0.wireOp",EDGE,"E50"),sQuery(id+"F0.wireOp",EDGE,"E51"),sQuery(id+"F0.wireOp",EDGE,"E52"),sQuery(id+"F0.wireOp",EDGE,"E53"),sQuery(id+"F0.wireOp",EDGE,"E54"),sQuery(id+"F0.wireOp",EDGE,"E55"),sQuery(id+"F0.wireOp",EDGE,"E56"),sQuery(id+"F0.wireOp",EDGE,"E57"),sQuery(id+"F0.wireOp",EDGE,"E58"),sQuery(id+"F0.wireOp",EDGE,"E59"),sQuery(id+"F0.wireOp",EDGE,"E60"),sQuery(id+"F0.wireOp",EDGE,"E61"),sQuery(id+"F0.wireOp",EDGE,"E62"),sQuery(id+"F0.wireOp",EDGE,"E63"),sQuery(id+"F0.wireOp",EDGE,"E64"),sQuery(id+"F0.wireOp",EDGE,"E65"),sQuery(id+"F0.wireOp",EDGE,"E66"),sQuery(id+"F0.wireOp",EDGE,"E67"),sQuery(id+"F0.wireOp",EDGE,"E68"),sQuery(id+"F0.wireOp",EDGE,"E69"),sQuery(id+"F0.wireOp",EDGE,"E70"),sQuery(id+"F0.wireOp",EDGE,"E71"),sQuery(id+"F0.wireOp",EDGE,"E72"),sQuery(id+"F0.wireOp",EDGE,"E73"),sQuery(id+"F0.wireOp",EDGE,"E74"),sQuery(id+"F0.wireOp",EDGE,"E75"),sQuery(id+"F0.wireOp",EDGE,"E76"),sQuery(id+"F0.wireOp",EDGE,"E77"),sQuery(id+"F0.wireOp",EDGE,"E78"),sQuery(id+"F0.wireOp",EDGE,"E79"),sQuery(id+"F0.wireOp",EDGE,"E80"),sQuery(id+"F0.wireOp",EDGE,"E81"),sQuery(id+"F0.wireOp",EDGE,"E82"),sQuery(id+"F0.wireOp",EDGE,"E83"),sQuery(id+"F0.wireOp",EDGE,"E84"),sQuery(id+"F0.wireOp",EDGE,"E85"),sQuery(id+"F0.wireOp",EDGE,"E86"),sQuery(id+"F0.wireOp",EDGE,"E87"),sQuery(id+"F0.wireOp",EDGE,"E88"),sQuery(id+"F0.wireOp",EDGE,"E89"),sQuery(id+"F0.wireOp",EDGE,"E90"),sQuery(id+"F0.wireOp",EDGE,"E91"),sQuery(id+"F0.wireOp",EDGE,"E92"),sQuery(id+"F0.wireOp",EDGE,"E93"),sQuery(id+"F0.wireOp",EDGE,"E94"),sQuery(id+"F0.wireOp",EDGE,"E95"),sQuery(id+"F0.wireOp",EDGE,"E96"),sQuery(id+"F0.wireOp",EDGE,"E97"),sQuery(id+"F0.wireOp",EDGE,"E98"),sQuery(id+"F0.wireOp",EDGE,"E99"),sQuery(id+"F0.wireOp",EDGE,"E100"),sQuery(id+"F0.wireOp",EDGE,"E101"),sQuery(id+"F0.wireOp",EDGE,"E102"),sQuery(id+"F0.wireOp",EDGE,"E103"),sQuery(id+"F0.wireOp",EDGE,"E104"),sQuery(id+"F0.wireOp",EDGE,"E105"),sQuery(id+"F0.wireOp",EDGE,"E106"),sQuery(id+"F0.wireOp",EDGE,"E107"),sQuery(id+"F0.wireOp",EDGE,"E108"),sQuery(id+"F0.wireOp",EDGE,"E109"),sQuery(id+"F0.wireOp",EDGE,"E110"),sQuery(id+"F0.wireOp",EDGE,"E111"),sQuery(id+"F0.wireOp",EDGE,"E112"),sQuery(id+"F0.wireOp",EDGE,"E113"),sQuery(id+"F0.wireOp",EDGE,"E114"),sQuery(id+"F0.wireOp",EDGE,"E115")])],"isStart":false})]});
            var Q2;
            Q2=makeQuery(id+"F6.opFillet","BLEND_FACE",FACE,{"disambiguationData":[OSD([sQuery(id+"F4.wireOp",EDGE,"E758.0.4.2")])]});
            var Q3;
            Q3=makeQuery(id+"F6.opFillet","BLEND_EDGE",EDGE,{"blendedFrom":[makeQuery(id+"F5.boolean.opBoolean","COPY",EDGE,{"derivedFrom":makeQuery(id+"F5.opExtrude","CAP_EDGE",EDGE,{"disambiguationData":[OSD([sQuery(id+"F4.wireOp",EDGE,"E758.0.4.2")])],"isStart":false})}),makeQuery(id+"F1.opExtrude","CAP_FACE",FACE,{"disambiguationData":[OSD([sQuery(id+"F0.wireOp",EDGE,"E0"),sQuery(id+"F0.wireOp",EDGE,"E1"),sQuery(id+"F0.wireOp",EDGE,"E2"),sQuery(id+"F0.wireOp",EDGE,"E3"),sQuery(id+"F0.wireOp",EDGE,"E4"),sQuery(id+"F0.wireOp",EDGE,"E5"),sQuery(id+"F0.wireOp",EDGE,"E6"),sQuery(id+"F0.wireOp",EDGE,"E7"),sQuery(id+"F0.wireOp",EDGE,"E8"),sQuery(id+"F0.wireOp",EDGE,"E9"),sQuery(id+"F0.wireOp",EDGE,"E10"),sQuery(id+"F0.wireOp",EDGE,"E11"),sQuery(id+"F0.wireOp",EDGE,"E12"),sQuery(id+"F0.wireOp",EDGE,"E13"),sQuery(id+"F0.wireOp",EDGE,"E14"),sQuery(id+"F0.wireOp",EDGE,"E15"),sQuery(id+"F0.wireOp",EDGE,"E16"),sQuery(id+"F0.wireOp",EDGE,"E17"),sQuery(id+"F0.wireOp",EDGE,"E18"),sQuery(id+"F0.wireOp",EDGE,"E19"),sQuery(id+"F0.wireOp",EDGE,"E20"),sQuery(id+"F0.wireOp",EDGE,"E21"),sQuery(id+"F0.wireOp",EDGE,"E22"),sQuery(id+"F0.wireOp",EDGE,"E23"),sQuery(id+"F0.wireOp",EDGE,"E24"),sQuery(id+"F0.wireOp",EDGE,"E25"),sQuery(id+"F0.wireOp",EDGE,"E26"),sQuery(id+"F0.wireOp",EDGE,"E27"),sQuery(id+"F0.wireOp",EDGE,"E28"),sQuery(id+"F0.wireOp",EDGE,"E29"),sQuery(id+"F0.wireOp",EDGE,"E30"),sQuery(id+"F0.wireOp",EDGE,"E31"),sQuery(id+"F0.wireOp",EDGE,"E32"),sQuery(id+"F0.wireOp",EDGE,"E33"),sQuery(id+"F0.wireOp",EDGE,"E34"),sQuery(id+"F0.wireOp",EDGE,"E35"),sQuery(id+"F0.wireOp",EDGE,"E36"),sQuery(id+"F0.wireOp",EDGE,"E37"),sQuery(id+"F0.wireOp",EDGE,"E38"),sQuery(id+"F0.wireOp",EDGE,"E39"),sQuery(id+"F0.wireOp",EDGE,"E40"),sQuery(id+"F0.wireOp",EDGE,"E41"),sQuery(id+"F0.wireOp",EDGE,"E42"),sQuery(id+"F0.wireOp",EDGE,"E43"),sQuery(id+"F0.wireOp",EDGE,"E44"),sQuery(id+"F0.wireOp",EDGE,"E45"),sQuery(id+"F0.wireOp",EDGE,"E46"),sQuery(id+"F0.wireOp",EDGE,"E47"),sQuery(id+"F0.wireOp",EDGE,"E48"),sQuery(id+"F0.wireOp",EDGE,"E49"),sQuery(id+"F0.wireOp",EDGE,"E50"),sQuery(id+"F0.wireOp",EDGE,"E51"),sQuery(id+"F0.wireOp",EDGE,"E52"),sQuery(id+"F0.wireOp",EDGE,"E53"),sQuery(id+"F0.wireOp",EDGE,"E54"),sQuery(id+"F0.wireOp",EDGE,"E55"),sQuery(id+"F0.wireOp",EDGE,"E56"),sQuery(id+"F0.wireOp",EDGE,"E57"),sQuery(id+"F0.wireOp",EDGE,"E58"),sQuery(id+"F0.wireOp",EDGE,"E59"),sQuery(id+"F0.wireOp",EDGE,"E60"),sQuery(id+"F0.wireOp",EDGE,"E61"),sQuery(id+"F0.wireOp",EDGE,"E62"),sQuery(id+"F0.wireOp",EDGE,"E63"),sQuery(id+"F0.wireOp",EDGE,"E64"),sQuery(id+"F0.wireOp",EDGE,"E65"),sQuery(id+"F0.wireOp",EDGE,"E66"),sQuery(id+"F0.wireOp",EDGE,"E67"),sQuery(id+"F0.wireOp",EDGE,"E68"),sQuery(id+"F0.wireOp",EDGE,"E69"),sQuery(id+"F0.wireOp",EDGE,"E70"),sQuery(id+"F0.wireOp",EDGE,"E71"),sQuery(id+"F0.wireOp",EDGE,"E72"),sQuery(id+"F0.wireOp",EDGE,"E73"),sQuery(id+"F0.wireOp",EDGE,"E74"),sQuery(id+"F0.wireOp",EDGE,"E75"),sQuery(id+"F0.wireOp",EDGE,"E76"),sQuery(id+"F0.wireOp",EDGE,"E77"),sQuery(id+"F0.wireOp",EDGE,"E78"),sQuery(id+"F0.wireOp",EDGE,"E79"),sQuery(id+"F0.wireOp",EDGE,"E80"),sQuery(id+"F0.wireOp",EDGE,"E81"),sQuery(id+"F0.wireOp",EDGE,"E82"),sQuery(id+"F0.wireOp",EDGE,"E83"),sQuery(id+"F0.wireOp",EDGE,"E84"),sQuery(id+"F0.wireOp",EDGE,"E85"),sQuery(id+"F0.wireOp",EDGE,"E86"),sQuery(id+"F0.wireOp",EDGE,"E87"),sQuery(id+"F0.wireOp",EDGE,"E88"),sQuery(id+"F0.wireOp",EDGE,"E89"),sQuery(id+"F0.wireOp",EDGE,"E90"),sQuery(id+"F0.wireOp",EDGE,"E91"),sQuery(id+"F0.wireOp",EDGE,"E92"),sQuery(id+"F0.wireOp",EDGE,"E93"),sQuery(id+"F0.wireOp",EDGE,"E94"),sQuery(id+"F0.wireOp",EDGE,"E95"),sQuery(id+"F0.wireOp",EDGE,"E96"),sQuery(id+"F0.wireOp",EDGE,"E97"),sQuery(id+"F0.wireOp",EDGE,"E98"),sQuery(id+"F0.wireOp",EDGE,"E99"),sQuery(id+"F0.wireOp",EDGE,"E100"),sQuery(id+"F0.wireOp",EDGE,"E101"),sQuery(id+"F0.wireOp",EDGE,"E102"),sQuery(id+"F0.wireOp",EDGE,"E103"),sQuery(id+"F0.wireOp",EDGE,"E104"),sQuery(id+"F0.wireOp",EDGE,"E105"),sQuery(id+"F0.wireOp",EDGE,"E106"),sQuery(id+"F0.wireOp",EDGE,"E107"),sQuery(id+"F0.wireOp",EDGE,"E108"),sQuery(id+"F0.wireOp",EDGE,"E109"),sQuery(id+"F0.wireOp",EDGE,"E110"),sQuery(id+"F0.wireOp",EDGE,"E111"),sQuery(id+"F0.wireOp",EDGE,"E112"),sQuery(id+"F0.wireOp",EDGE,"E113"),sQuery(id+"F0.wireOp",EDGE,"E114"),sQuery(id+"F0.wireOp",EDGE,"E115")])],"isStart":false})],"blendedInto":[makeQuery(id+"F1.opExtrude","CAP_FACE",FACE,{"disambiguationData":[OSD([sQuery(id+"F0.wireOp",EDGE,"E0"),sQuery(id+"F0.wireOp",EDGE,"E1"),sQuery(id+"F0.wireOp",EDGE,"E2"),sQuery(id+"F0.wireOp",EDGE,"E3"),sQuery(id+"F0.wireOp",EDGE,"E4"),sQuery(id+"F0.wireOp",EDGE,"E5"),sQuery(id+"F0.wireOp",EDGE,"E6"),sQuery(id+"F0.wireOp",EDGE,"E7"),sQuery(id+"F0.wireOp",EDGE,"E8"),sQuery(id+"F0.wireOp",EDGE,"E9"),sQuery(id+"F0.wireOp",EDGE,"E10"),sQuery(id+"F0.wireOp",EDGE,"E11"),sQuery(id+"F0.wireOp",EDGE,"E12"),sQuery(id+"F0.wireOp",EDGE,"E13"),sQuery(id+"F0.wireOp",EDGE,"E14"),sQuery(id+"F0.wireOp",EDGE,"E15"),sQuery(id+"F0.wireOp",EDGE,"E16"),sQuery(id+"F0.wireOp",EDGE,"E17"),sQuery(id+"F0.wireOp",EDGE,"E18"),sQuery(id+"F0.wireOp",EDGE,"E19"),sQuery(id+"F0.wireOp",EDGE,"E20"),sQuery(id+"F0.wireOp",EDGE,"E21"),sQuery(id+"F0.wireOp",EDGE,"E22"),sQuery(id+"F0.wireOp",EDGE,"E23"),sQuery(id+"F0.wireOp",EDGE,"E24"),sQuery(id+"F0.wireOp",EDGE,"E25"),sQuery(id+"F0.wireOp",EDGE,"E26"),sQuery(id+"F0.wireOp",EDGE,"E27"),sQuery(id+"F0.wireOp",EDGE,"E28"),sQuery(id+"F0.wireOp",EDGE,"E29"),sQuery(id+"F0.wireOp",EDGE,"E30"),sQuery(id+"F0.wireOp",EDGE,"E31"),sQuery(id+"F0.wireOp",EDGE,"E32"),sQuery(id+"F0.wireOp",EDGE,"E33"),sQuery(id+"F0.wireOp",EDGE,"E34"),sQuery(id+"F0.wireOp",EDGE,"E35"),sQuery(id+"F0.wireOp",EDGE,"E36"),sQuery(id+"F0.wireOp",EDGE,"E37"),sQuery(id+"F0.wireOp",EDGE,"E38"),sQuery(id+"F0.wireOp",EDGE,"E39"),sQuery(id+"F0.wireOp",EDGE,"E40"),sQuery(id+"F0.wireOp",EDGE,"E41"),sQuery(id+"F0.wireOp",EDGE,"E42"),sQuery(id+"F0.wireOp",EDGE,"E43"),sQuery(id+"F0.wireOp",EDGE,"E44"),sQuery(id+"F0.wireOp",EDGE,"E45"),sQuery(id+"F0.wireOp",EDGE,"E46"),sQuery(id+"F0.wireOp",EDGE,"E47"),sQuery(id+"F0.wireOp",EDGE,"E48"),sQuery(id+"F0.wireOp",EDGE,"E49"),sQuery(id+"F0.wireOp",EDGE,"E50"),sQuery(id+"F0.wireOp",EDGE,"E51"),sQuery(id+"F0.wireOp",EDGE,"E52"),sQuery(id+"F0.wireOp",EDGE,"E53"),sQuery(id+"F0.wireOp",EDGE,"E54"),sQuery(id+"F0.wireOp",EDGE,"E55"),sQuery(id+"F0.wireOp",EDGE,"E56"),sQuery(id+"F0.wireOp",EDGE,"E57"),sQuery(id+"F0.wireOp",EDGE,"E58"),sQuery(id+"F0.wireOp",EDGE,"E59"),sQuery(id+"F0.wireOp",EDGE,"E60"),sQuery(id+"F0.wireOp",EDGE,"E61"),sQuery(id+"F0.wireOp",EDGE,"E62"),sQuery(id+"F0.wireOp",EDGE,"E63"),sQuery(id+"F0.wireOp",EDGE,"E64"),sQuery(id+"F0.wireOp",EDGE,"E65"),sQuery(id+"F0.wireOp",EDGE,"E66"),sQuery(id+"F0.wireOp",EDGE,"E67"),sQuery(id+"F0.wireOp",EDGE,"E68"),sQuery(id+"F0.wireOp",EDGE,"E69"),sQuery(id+"F0.wireOp",EDGE,"E70"),sQuery(id+"F0.wireOp",EDGE,"E71"),sQuery(id+"F0.wireOp",EDGE,"E72"),sQuery(id+"F0.wireOp",EDGE,"E73"),sQuery(id+"F0.wireOp",EDGE,"E74"),sQuery(id+"F0.wireOp",EDGE,"E75"),sQuery(id+"F0.wireOp",EDGE,"E76"),sQuery(id+"F0.wireOp",EDGE,"E77"),sQuery(id+"F0.wireOp",EDGE,"E78"),sQuery(id+"F0.wireOp",EDGE,"E79"),sQuery(id+"F0.wireOp",EDGE,"E80"),sQuery(id+"F0.wireOp",EDGE,"E81"),sQuery(id+"F0.wireOp",EDGE,"E82"),sQuery(id+"F0.wireOp",EDGE,"E83"),sQuery(id+"F0.wireOp",EDGE,"E84"),sQuery(id+"F0.wireOp",EDGE,"E85"),sQuery(id+"F0.wireOp",EDGE,"E86"),sQuery(id+"F0.wireOp",EDGE,"E87"),sQuery(id+"F0.wireOp",EDGE,"E88"),sQuery(id+"F0.wireOp",EDGE,"E89"),sQuery(id+"F0.wireOp",EDGE,"E90"),sQuery(id+"F0.wireOp",EDGE,"E91"),sQuery(id+"F0.wireOp",EDGE,"E92"),sQuery(id+"F0.wireOp",EDGE,"E93"),sQuery(id+"F0.wireOp",EDGE,"E94"),sQuery(id+"F0.wireOp",EDGE,"E95"),sQuery(id+"F0.wireOp",EDGE,"E96"),sQuery(id+"F0.wireOp",EDGE,"E97"),sQuery(id+"F0.wireOp",EDGE,"E98"),sQuery(id+"F0.wireOp",EDGE,"E99"),sQuery(id+"F0.wireOp",EDGE,"E100"),sQuery(id+"F0.wireOp",EDGE,"E101"),sQuery(id+"F0.wireOp",EDGE,"E102"),sQuery(id+"F0.wireOp",EDGE,"E103"),sQuery(id+"F0.wireOp",EDGE,"E104"),sQuery(id+"F0.wireOp",EDGE,"E105"),sQuery(id+"F0.wireOp",EDGE,"E106"),sQuery(id+"F0.wireOp",EDGE,"E107"),sQuery(id+"F0.wireOp",EDGE,"E108"),sQuery(id+"F0.wireOp",EDGE,"E109"),sQuery(id+"F0.wireOp",EDGE,"E110"),sQuery(id+"F0.wireOp",EDGE,"E111"),sQuery(id+"F0.wireOp",EDGE,"E112"),sQuery(id+"F0.wireOp",EDGE,"E113"),sQuery(id+"F0.wireOp",EDGE,"E114"),sQuery(id+"F0.wireOp",EDGE,"E115")])],"isStart":false})]});
            var Q4;
            Q4=makeQuery(id+"F6.opFillet","BLEND_FACE",FACE,{"disambiguationData":[OSD([sQuery(id+"F4.wireOp",EDGE,"E757.3.2.0")])]});
            var Q5;
            Q5=makeQuery(id+"F6.opFillet","BLEND_EDGE",EDGE,{"blendedFrom":[makeQuery(id+"F5.boolean.opBoolean","COPY",EDGE,{"derivedFrom":makeQuery(id+"F5.opExtrude","CAP_EDGE",EDGE,{"disambiguationData":[OSD([sQuery(id+"F4.wireOp",EDGE,"E757.2.2.0")])],"isStart":false})}),makeQuery(id+"F1.opExtrude","CAP_FACE",FACE,{"disambiguationData":[OSD([sQuery(id+"F0.wireOp",EDGE,"E0"),sQuery(id+"F0.wireOp",EDGE,"E1"),sQuery(id+"F0.wireOp",EDGE,"E2"),sQuery(id+"F0.wireOp",EDGE,"E3"),sQuery(id+"F0.wireOp",EDGE,"E4"),sQuery(id+"F0.wireOp",EDGE,"E5"),sQuery(id+"F0.wireOp",EDGE,"E6"),sQuery(id+"F0.wireOp",EDGE,"E7"),sQuery(id+"F0.wireOp",EDGE,"E8"),sQuery(id+"F0.wireOp",EDGE,"E9"),sQuery(id+"F0.wireOp",EDGE,"E10"),sQuery(id+"F0.wireOp",EDGE,"E11"),sQuery(id+"F0.wireOp",EDGE,"E12"),sQuery(id+"F0.wireOp",EDGE,"E13"),sQuery(id+"F0.wireOp",EDGE,"E14"),sQuery(id+"F0.wireOp",EDGE,"E15"),sQuery(id+"F0.wireOp",EDGE,"E16"),sQuery(id+"F0.wireOp",EDGE,"E17"),sQuery(id+"F0.wireOp",EDGE,"E18"),sQuery(id+"F0.wireOp",EDGE,"E19"),sQuery(id+"F0.wireOp",EDGE,"E20"),sQuery(id+"F0.wireOp",EDGE,"E21"),sQuery(id+"F0.wireOp",EDGE,"E22"),sQuery(id+"F0.wireOp",EDGE,"E23"),sQuery(id+"F0.wireOp",EDGE,"E24"),sQuery(id+"F0.wireOp",EDGE,"E25"),sQuery(id+"F0.wireOp",EDGE,"E26"),sQuery(id+"F0.wireOp",EDGE,"E27"),sQuery(id+"F0.wireOp",EDGE,"E28"),sQuery(id+"F0.wireOp",EDGE,"E29"),sQuery(id+"F0.wireOp",EDGE,"E30"),sQuery(id+"F0.wireOp",EDGE,"E31"),sQuery(id+"F0.wireOp",EDGE,"E32"),sQuery(id+"F0.wireOp",EDGE,"E33"),sQuery(id+"F0.wireOp",EDGE,"E34"),sQuery(id+"F0.wireOp",EDGE,"E35"),sQuery(id+"F0.wireOp",EDGE,"E36"),sQuery(id+"F0.wireOp",EDGE,"E37"),sQuery(id+"F0.wireOp",EDGE,"E38"),sQuery(id+"F0.wireOp",EDGE,"E39"),sQuery(id+"F0.wireOp",EDGE,"E40"),sQuery(id+"F0.wireOp",EDGE,"E41"),sQuery(id+"F0.wireOp",EDGE,"E42"),sQuery(id+"F0.wireOp",EDGE,"E43"),sQuery(id+"F0.wireOp",EDGE,"E44"),sQuery(id+"F0.wireOp",EDGE,"E45"),sQuery(id+"F0.wireOp",EDGE,"E46"),sQuery(id+"F0.wireOp",EDGE,"E47"),sQuery(id+"F0.wireOp",EDGE,"E48"),sQuery(id+"F0.wireOp",EDGE,"E49"),sQuery(id+"F0.wireOp",EDGE,"E50"),sQuery(id+"F0.wireOp",EDGE,"E51"),sQuery(id+"F0.wireOp",EDGE,"E52"),sQuery(id+"F0.wireOp",EDGE,"E53"),sQuery(id+"F0.wireOp",EDGE,"E54"),sQuery(id+"F0.wireOp",EDGE,"E55"),sQuery(id+"F0.wireOp",EDGE,"E56"),sQuery(id+"F0.wireOp",EDGE,"E57"),sQuery(id+"F0.wireOp",EDGE,"E58"),sQuery(id+"F0.wireOp",EDGE,"E59"),sQuery(id+"F0.wireOp",EDGE,"E60"),sQuery(id+"F0.wireOp",EDGE,"E61"),sQuery(id+"F0.wireOp",EDGE,"E62"),sQuery(id+"F0.wireOp",EDGE,"E63"),sQuery(id+"F0.wireOp",EDGE,"E64"),sQuery(id+"F0.wireOp",EDGE,"E65"),sQuery(id+"F0.wireOp",EDGE,"E66"),sQuery(id+"F0.wireOp",EDGE,"E67"),sQuery(id+"F0.wireOp",EDGE,"E68"),sQuery(id+"F0.wireOp",EDGE,"E69"),sQuery(id+"F0.wireOp",EDGE,"E70"),sQuery(id+"F0.wireOp",EDGE,"E71"),sQuery(id+"F0.wireOp",EDGE,"E72"),sQuery(id+"F0.wireOp",EDGE,"E73"),sQuery(id+"F0.wireOp",EDGE,"E74"),sQuery(id+"F0.wireOp",EDGE,"E75"),sQuery(id+"F0.wireOp",EDGE,"E76"),sQuery(id+"F0.wireOp",EDGE,"E77"),sQuery(id+"F0.wireOp",EDGE,"E78"),sQuery(id+"F0.wireOp",EDGE,"E79"),sQuery(id+"F0.wireOp",EDGE,"E80"),sQuery(id+"F0.wireOp",EDGE,"E81"),sQuery(id+"F0.wireOp",EDGE,"E82"),sQuery(id+"F0.wireOp",EDGE,"E83"),sQuery(id+"F0.wireOp",EDGE,"E84"),sQuery(id+"F0.wireOp",EDGE,"E85"),sQuery(id+"F0.wireOp",EDGE,"E86"),sQuery(id+"F0.wireOp",EDGE,"E87"),sQuery(id+"F0.wireOp",EDGE,"E88"),sQuery(id+"F0.wireOp",EDGE,"E89"),sQuery(id+"F0.wireOp",EDGE,"E90"),sQuery(id+"F0.wireOp",EDGE,"E91"),sQuery(id+"F0.wireOp",EDGE,"E92"),sQuery(id+"F0.wireOp",EDGE,"E93"),sQuery(id+"F0.wireOp",EDGE,"E94"),sQuery(id+"F0.wireOp",EDGE,"E95"),sQuery(id+"F0.wireOp",EDGE,"E96"),sQuery(id+"F0.wireOp",EDGE,"E97"),sQuery(id+"F0.wireOp",EDGE,"E98"),sQuery(id+"F0.wireOp",EDGE,"E99"),sQuery(id+"F0.wireOp",EDGE,"E100"),sQuery(id+"F0.wireOp",EDGE,"E101"),sQuery(id+"F0.wireOp",EDGE,"E102"),sQuery(id+"F0.wireOp",EDGE,"E103"),sQuery(id+"F0.wireOp",EDGE,"E104"),sQuery(id+"F0.wireOp",EDGE,"E105"),sQuery(id+"F0.wireOp",EDGE,"E106"),sQuery(id+"F0.wireOp",EDGE,"E107"),sQuery(id+"F0.wireOp",EDGE,"E108"),sQuery(id+"F0.wireOp",EDGE,"E109"),sQuery(id+"F0.wireOp",EDGE,"E110"),sQuery(id+"F0.wireOp",EDGE,"E111"),sQuery(id+"F0.wireOp",EDGE,"E112"),sQuery(id+"F0.wireOp",EDGE,"E113"),sQuery(id+"F0.wireOp",EDGE,"E114"),sQuery(id+"F0.wireOp",EDGE,"E115")])],"isStart":false})],"blendedInto":[makeQuery(id+"F1.opExtrude","CAP_FACE",FACE,{"disambiguationData":[OSD([sQuery(id+"F0.wireOp",EDGE,"E0"),sQuery(id+"F0.wireOp",EDGE,"E1"),sQuery(id+"F0.wireOp",EDGE,"E2"),sQuery(id+"F0.wireOp",EDGE,"E3"),sQuery(id+"F0.wireOp",EDGE,"E4"),sQuery(id+"F0.wireOp",EDGE,"E5"),sQuery(id+"F0.wireOp",EDGE,"E6"),sQuery(id+"F0.wireOp",EDGE,"E7"),sQuery(id+"F0.wireOp",EDGE,"E8"),sQuery(id+"F0.wireOp",EDGE,"E9"),sQuery(id+"F0.wireOp",EDGE,"E10"),sQuery(id+"F0.wireOp",EDGE,"E11"),sQuery(id+"F0.wireOp",EDGE,"E12"),sQuery(id+"F0.wireOp",EDGE,"E13"),sQuery(id+"F0.wireOp",EDGE,"E14"),sQuery(id+"F0.wireOp",EDGE,"E15"),sQuery(id+"F0.wireOp",EDGE,"E16"),sQuery(id+"F0.wireOp",EDGE,"E17"),sQuery(id+"F0.wireOp",EDGE,"E18"),sQuery(id+"F0.wireOp",EDGE,"E19"),sQuery(id+"F0.wireOp",EDGE,"E20"),sQuery(id+"F0.wireOp",EDGE,"E21"),sQuery(id+"F0.wireOp",EDGE,"E22"),sQuery(id+"F0.wireOp",EDGE,"E23"),sQuery(id+"F0.wireOp",EDGE,"E24"),sQuery(id+"F0.wireOp",EDGE,"E25"),sQuery(id+"F0.wireOp",EDGE,"E26"),sQuery(id+"F0.wireOp",EDGE,"E27"),sQuery(id+"F0.wireOp",EDGE,"E28"),sQuery(id+"F0.wireOp",EDGE,"E29"),sQuery(id+"F0.wireOp",EDGE,"E30"),sQuery(id+"F0.wireOp",EDGE,"E31"),sQuery(id+"F0.wireOp",EDGE,"E32"),sQuery(id+"F0.wireOp",EDGE,"E33"),sQuery(id+"F0.wireOp",EDGE,"E34"),sQuery(id+"F0.wireOp",EDGE,"E35"),sQuery(id+"F0.wireOp",EDGE,"E36"),sQuery(id+"F0.wireOp",EDGE,"E37"),sQuery(id+"F0.wireOp",EDGE,"E38"),sQuery(id+"F0.wireOp",EDGE,"E39"),sQuery(id+"F0.wireOp",EDGE,"E40"),sQuery(id+"F0.wireOp",EDGE,"E41"),sQuery(id+"F0.wireOp",EDGE,"E42"),sQuery(id+"F0.wireOp",EDGE,"E43"),sQuery(id+"F0.wireOp",EDGE,"E44"),sQuery(id+"F0.wireOp",EDGE,"E45"),sQuery(id+"F0.wireOp",EDGE,"E46"),sQuery(id+"F0.wireOp",EDGE,"E47"),sQuery(id+"F0.wireOp",EDGE,"E48"),sQuery(id+"F0.wireOp",EDGE,"E49"),sQuery(id+"F0.wireOp",EDGE,"E50"),sQuery(id+"F0.wireOp",EDGE,"E51"),sQuery(id+"F0.wireOp",EDGE,"E52"),sQuery(id+"F0.wireOp",EDGE,"E53"),sQuery(id+"F0.wireOp",EDGE,"E54"),sQuery(id+"F0.wireOp",EDGE,"E55"),sQuery(id+"F0.wireOp",EDGE,"E56"),sQuery(id+"F0.wireOp",EDGE,"E57"),sQuery(id+"F0.wireOp",EDGE,"E58"),sQuery(id+"F0.wireOp",EDGE,"E59"),sQuery(id+"F0.wireOp",EDGE,"E60"),sQuery(id+"F0.wireOp",EDGE,"E61"),sQuery(id+"F0.wireOp",EDGE,"E62"),sQuery(id+"F0.wireOp",EDGE,"E63"),sQuery(id+"F0.wireOp",EDGE,"E64"),sQuery(id+"F0.wireOp",EDGE,"E65"),sQuery(id+"F0.wireOp",EDGE,"E66"),sQuery(id+"F0.wireOp",EDGE,"E67"),sQuery(id+"F0.wireOp",EDGE,"E68"),sQuery(id+"F0.wireOp",EDGE,"E69"),sQuery(id+"F0.wireOp",EDGE,"E70"),sQuery(id+"F0.wireOp",EDGE,"E71"),sQuery(id+"F0.wireOp",EDGE,"E72"),sQuery(id+"F0.wireOp",EDGE,"E73"),sQuery(id+"F0.wireOp",EDGE,"E74"),sQuery(id+"F0.wireOp",EDGE,"E75"),sQuery(id+"F0.wireOp",EDGE,"E76"),sQuery(id+"F0.wireOp",EDGE,"E77"),sQuery(id+"F0.wireOp",EDGE,"E78"),sQuery(id+"F0.wireOp",EDGE,"E79"),sQuery(id+"F0.wireOp",EDGE,"E80"),sQuery(id+"F0.wireOp",EDGE,"E81"),sQuery(id+"F0.wireOp",EDGE,"E82"),sQuery(id+"F0.wireOp",EDGE,"E83"),sQuery(id+"F0.wireOp",EDGE,"E84"),sQuery(id+"F0.wireOp",EDGE,"E85"),sQuery(id+"F0.wireOp",EDGE,"E86"),sQuery(id+"F0.wireOp",EDGE,"E87"),sQuery(id+"F0.wireOp",EDGE,"E88"),sQuery(id+"F0.wireOp",EDGE,"E89"),sQuery(id+"F0.wireOp",EDGE,"E90"),sQuery(id+"F0.wireOp",EDGE,"E91"),sQuery(id+"F0.wireOp",EDGE,"E92"),sQuery(id+"F0.wireOp",EDGE,"E93"),sQuery(id+"F0.wireOp",EDGE,"E94"),sQuery(id+"F0.wireOp",EDGE,"E95"),sQuery(id+"F0.wireOp",EDGE,"E96"),sQuery(id+"F0.wireOp",EDGE,"E97"),sQuery(id+"F0.wireOp",EDGE,"E98"),sQuery(id+"F0.wireOp",EDGE,"E99"),sQuery(id+"F0.wireOp",EDGE,"E100"),sQuery(id+"F0.wireOp",EDGE,"E101"),sQuery(id+"F0.wireOp",EDGE,"E102"),sQuery(id+"F0.wireOp",EDGE,"E103"),sQuery(id+"F0.wireOp",EDGE,"E104"),sQuery(id+"F0.wireOp",EDGE,"E105"),sQuery(id+"F0.wireOp",EDGE,"E106"),sQuery(id+"F0.wireOp",EDGE,"E107"),sQuery(id+"F0.wireOp",EDGE,"E108"),sQuery(id+"F0.wireOp",EDGE,"E109"),sQuery(id+"F0.wireOp",EDGE,"E110"),sQuery(id+"F0.wireOp",EDGE,"E111"),sQuery(id+"F0.wireOp",EDGE,"E112"),sQuery(id+"F0.wireOp",EDGE,"E113"),sQuery(id+"F0.wireOp",EDGE,"E114"),sQuery(id+"F0.wireOp",EDGE,"E115")])],"isStart":false})]});
            var Q6;
            Q6=makeQuery(id+"F6.opFillet","BLEND_FACE",FACE,{"disambiguationData":[OSD([sQuery(id+"F4.wireOp",EDGE,"E757.1.2.0")])]});
            var Q7;
            Q7=makeQuery(id+"F6.opFillet","BLEND_EDGE",EDGE,{"blendedFrom":[makeQuery(id+"F5.boolean.opBoolean","COPY",EDGE,{"derivedFrom":makeQuery(id+"F5.opExtrude","CAP_EDGE",EDGE,{"disambiguationData":[OSD([sQuery(id+"F4.wireOp",EDGE,"E757.0.2.0")])],"isStart":false})}),makeQuery(id+"F1.opExtrude","CAP_FACE",FACE,{"disambiguationData":[OSD([sQuery(id+"F0.wireOp",EDGE,"E0"),sQuery(id+"F0.wireOp",EDGE,"E1"),sQuery(id+"F0.wireOp",EDGE,"E2"),sQuery(id+"F0.wireOp",EDGE,"E3"),sQuery(id+"F0.wireOp",EDGE,"E4"),sQuery(id+"F0.wireOp",EDGE,"E5"),sQuery(id+"F0.wireOp",EDGE,"E6"),sQuery(id+"F0.wireOp",EDGE,"E7"),sQuery(id+"F0.wireOp",EDGE,"E8"),sQuery(id+"F0.wireOp",EDGE,"E9"),sQuery(id+"F0.wireOp",EDGE,"E10"),sQuery(id+"F0.wireOp",EDGE,"E11"),sQuery(id+"F0.wireOp",EDGE,"E12"),sQuery(id+"F0.wireOp",EDGE,"E13"),sQuery(id+"F0.wireOp",EDGE,"E14"),sQuery(id+"F0.wireOp",EDGE,"E15"),sQuery(id+"F0.wireOp",EDGE,"E16"),sQuery(id+"F0.wireOp",EDGE,"E17"),sQuery(id+"F0.wireOp",EDGE,"E18"),sQuery(id+"F0.wireOp",EDGE,"E19"),sQuery(id+"F0.wireOp",EDGE,"E20"),sQuery(id+"F0.wireOp",EDGE,"E21"),sQuery(id+"F0.wireOp",EDGE,"E22"),sQuery(id+"F0.wireOp",EDGE,"E23"),sQuery(id+"F0.wireOp",EDGE,"E24"),sQuery(id+"F0.wireOp",EDGE,"E25"),sQuery(id+"F0.wireOp",EDGE,"E26"),sQuery(id+"F0.wireOp",EDGE,"E27"),sQuery(id+"F0.wireOp",EDGE,"E28"),sQuery(id+"F0.wireOp",EDGE,"E29"),sQuery(id+"F0.wireOp",EDGE,"E30"),sQuery(id+"F0.wireOp",EDGE,"E31"),sQuery(id+"F0.wireOp",EDGE,"E32"),sQuery(id+"F0.wireOp",EDGE,"E33"),sQuery(id+"F0.wireOp",EDGE,"E34"),sQuery(id+"F0.wireOp",EDGE,"E35"),sQuery(id+"F0.wireOp",EDGE,"E36"),sQuery(id+"F0.wireOp",EDGE,"E37"),sQuery(id+"F0.wireOp",EDGE,"E38"),sQuery(id+"F0.wireOp",EDGE,"E39"),sQuery(id+"F0.wireOp",EDGE,"E40"),sQuery(id+"F0.wireOp",EDGE,"E41"),sQuery(id+"F0.wireOp",EDGE,"E42"),sQuery(id+"F0.wireOp",EDGE,"E43"),sQuery(id+"F0.wireOp",EDGE,"E44"),sQuery(id+"F0.wireOp",EDGE,"E45"),sQuery(id+"F0.wireOp",EDGE,"E46"),sQuery(id+"F0.wireOp",EDGE,"E47"),sQuery(id+"F0.wireOp",EDGE,"E48"),sQuery(id+"F0.wireOp",EDGE,"E49"),sQuery(id+"F0.wireOp",EDGE,"E50"),sQuery(id+"F0.wireOp",EDGE,"E51"),sQuery(id+"F0.wireOp",EDGE,"E52"),sQuery(id+"F0.wireOp",EDGE,"E53"),sQuery(id+"F0.wireOp",EDGE,"E54"),sQuery(id+"F0.wireOp",EDGE,"E55"),sQuery(id+"F0.wireOp",EDGE,"E56"),sQuery(id+"F0.wireOp",EDGE,"E57"),sQuery(id+"F0.wireOp",EDGE,"E58"),sQuery(id+"F0.wireOp",EDGE,"E59"),sQuery(id+"F0.wireOp",EDGE,"E60"),sQuery(id+"F0.wireOp",EDGE,"E61"),sQuery(id+"F0.wireOp",EDGE,"E62"),sQuery(id+"F0.wireOp",EDGE,"E63"),sQuery(id+"F0.wireOp",EDGE,"E64"),sQuery(id+"F0.wireOp",EDGE,"E65"),sQuery(id+"F0.wireOp",EDGE,"E66"),sQuery(id+"F0.wireOp",EDGE,"E67"),sQuery(id+"F0.wireOp",EDGE,"E68"),sQuery(id+"F0.wireOp",EDGE,"E69"),sQuery(id+"F0.wireOp",EDGE,"E70"),sQuery(id+"F0.wireOp",EDGE,"E71"),sQuery(id+"F0.wireOp",EDGE,"E72"),sQuery(id+"F0.wireOp",EDGE,"E73"),sQuery(id+"F0.wireOp",EDGE,"E74"),sQuery(id+"F0.wireOp",EDGE,"E75"),sQuery(id+"F0.wireOp",EDGE,"E76"),sQuery(id+"F0.wireOp",EDGE,"E77"),sQuery(id+"F0.wireOp",EDGE,"E78"),sQuery(id+"F0.wireOp",EDGE,"E79"),sQuery(id+"F0.wireOp",EDGE,"E80"),sQuery(id+"F0.wireOp",EDGE,"E81"),sQuery(id+"F0.wireOp",EDGE,"E82"),sQuery(id+"F0.wireOp",EDGE,"E83"),sQuery(id+"F0.wireOp",EDGE,"E84"),sQuery(id+"F0.wireOp",EDGE,"E85"),sQuery(id+"F0.wireOp",EDGE,"E86"),sQuery(id+"F0.wireOp",EDGE,"E87"),sQuery(id+"F0.wireOp",EDGE,"E88"),sQuery(id+"F0.wireOp",EDGE,"E89"),sQuery(id+"F0.wireOp",EDGE,"E90"),sQuery(id+"F0.wireOp",EDGE,"E91"),sQuery(id+"F0.wireOp",EDGE,"E92"),sQuery(id+"F0.wireOp",EDGE,"E93"),sQuery(id+"F0.wireOp",EDGE,"E94"),sQuery(id+"F0.wireOp",EDGE,"E95"),sQuery(id+"F0.wireOp",EDGE,"E96"),sQuery(id+"F0.wireOp",EDGE,"E97"),sQuery(id+"F0.wireOp",EDGE,"E98"),sQuery(id+"F0.wireOp",EDGE,"E99"),sQuery(id+"F0.wireOp",EDGE,"E100"),sQuery(id+"F0.wireOp",EDGE,"E101"),sQuery(id+"F0.wireOp",EDGE,"E102"),sQuery(id+"F0.wireOp",EDGE,"E103"),sQuery(id+"F0.wireOp",EDGE,"E104"),sQuery(id+"F0.wireOp",EDGE,"E105"),sQuery(id+"F0.wireOp",EDGE,"E106"),sQuery(id+"F0.wireOp",EDGE,"E107"),sQuery(id+"F0.wireOp",EDGE,"E108"),sQuery(id+"F0.wireOp",EDGE,"E109"),sQuery(id+"F0.wireOp",EDGE,"E110"),sQuery(id+"F0.wireOp",EDGE,"E111"),sQuery(id+"F0.wireOp",EDGE,"E112"),sQuery(id+"F0.wireOp",EDGE,"E113"),sQuery(id+"F0.wireOp",EDGE,"E114"),sQuery(id+"F0.wireOp",EDGE,"E115")])],"isStart":false})],"blendedInto":[makeQuery(id+"F1.opExtrude","CAP_FACE",FACE,{"disambiguationData":[OSD([sQuery(id+"F0.wireOp",EDGE,"E0"),sQuery(id+"F0.wireOp",EDGE,"E1"),sQuery(id+"F0.wireOp",EDGE,"E2"),sQuery(id+"F0.wireOp",EDGE,"E3"),sQuery(id+"F0.wireOp",EDGE,"E4"),sQuery(id+"F0.wireOp",EDGE,"E5"),sQuery(id+"F0.wireOp",EDGE,"E6"),sQuery(id+"F0.wireOp",EDGE,"E7"),sQuery(id+"F0.wireOp",EDGE,"E8"),sQuery(id+"F0.wireOp",EDGE,"E9"),sQuery(id+"F0.wireOp",EDGE,"E10"),sQuery(id+"F0.wireOp",EDGE,"E11"),sQuery(id+"F0.wireOp",EDGE,"E12"),sQuery(id+"F0.wireOp",EDGE,"E13"),sQuery(id+"F0.wireOp",EDGE,"E14"),sQuery(id+"F0.wireOp",EDGE,"E15"),sQuery(id+"F0.wireOp",EDGE,"E16"),sQuery(id+"F0.wireOp",EDGE,"E17"),sQuery(id+"F0.wireOp",EDGE,"E18"),sQuery(id+"F0.wireOp",EDGE,"E19"),sQuery(id+"F0.wireOp",EDGE,"E20"),sQuery(id+"F0.wireOp",EDGE,"E21"),sQuery(id+"F0.wireOp",EDGE,"E22"),sQuery(id+"F0.wireOp",EDGE,"E23"),sQuery(id+"F0.wireOp",EDGE,"E24"),sQuery(id+"F0.wireOp",EDGE,"E25"),sQuery(id+"F0.wireOp",EDGE,"E26"),sQuery(id+"F0.wireOp",EDGE,"E27"),sQuery(id+"F0.wireOp",EDGE,"E28"),sQuery(id+"F0.wireOp",EDGE,"E29"),sQuery(id+"F0.wireOp",EDGE,"E30"),sQuery(id+"F0.wireOp",EDGE,"E31"),sQuery(id+"F0.wireOp",EDGE,"E32"),sQuery(id+"F0.wireOp",EDGE,"E33"),sQuery(id+"F0.wireOp",EDGE,"E34"),sQuery(id+"F0.wireOp",EDGE,"E35"),sQuery(id+"F0.wireOp",EDGE,"E36"),sQuery(id+"F0.wireOp",EDGE,"E37"),sQuery(id+"F0.wireOp",EDGE,"E38"),sQuery(id+"F0.wireOp",EDGE,"E39"),sQuery(id+"F0.wireOp",EDGE,"E40"),sQuery(id+"F0.wireOp",EDGE,"E41"),sQuery(id+"F0.wireOp",EDGE,"E42"),sQuery(id+"F0.wireOp",EDGE,"E43"),sQuery(id+"F0.wireOp",EDGE,"E44"),sQuery(id+"F0.wireOp",EDGE,"E45"),sQuery(id+"F0.wireOp",EDGE,"E46"),sQuery(id+"F0.wireOp",EDGE,"E47"),sQuery(id+"F0.wireOp",EDGE,"E48"),sQuery(id+"F0.wireOp",EDGE,"E49"),sQuery(id+"F0.wireOp",EDGE,"E50"),sQuery(id+"F0.wireOp",EDGE,"E51"),sQuery(id+"F0.wireOp",EDGE,"E52"),sQuery(id+"F0.wireOp",EDGE,"E53"),sQuery(id+"F0.wireOp",EDGE,"E54"),sQuery(id+"F0.wireOp",EDGE,"E55"),sQuery(id+"F0.wireOp",EDGE,"E56"),sQuery(id+"F0.wireOp",EDGE,"E57"),sQuery(id+"F0.wireOp",EDGE,"E58"),sQuery(id+"F0.wireOp",EDGE,"E59"),sQuery(id+"F0.wireOp",EDGE,"E60"),sQuery(id+"F0.wireOp",EDGE,"E61"),sQuery(id+"F0.wireOp",EDGE,"E62"),sQuery(id+"F0.wireOp",EDGE,"E63"),sQuery(id+"F0.wireOp",EDGE,"E64"),sQuery(id+"F0.wireOp",EDGE,"E65"),sQuery(id+"F0.wireOp",EDGE,"E66"),sQuery(id+"F0.wireOp",EDGE,"E67"),sQuery(id+"F0.wireOp",EDGE,"E68"),sQuery(id+"F0.wireOp",EDGE,"E69"),sQuery(id+"F0.wireOp",EDGE,"E70"),sQuery(id+"F0.wireOp",EDGE,"E71"),sQuery(id+"F0.wireOp",EDGE,"E72"),sQuery(id+"F0.wireOp",EDGE,"E73"),sQuery(id+"F0.wireOp",EDGE,"E74"),sQuery(id+"F0.wireOp",EDGE,"E75"),sQuery(id+"F0.wireOp",EDGE,"E76"),sQuery(id+"F0.wireOp",EDGE,"E77"),sQuery(id+"F0.wireOp",EDGE,"E78"),sQuery(id+"F0.wireOp",EDGE,"E79"),sQuery(id+"F0.wireOp",EDGE,"E80"),sQuery(id+"F0.wireOp",EDGE,"E81"),sQuery(id+"F0.wireOp",EDGE,"E82"),sQuery(id+"F0.wireOp",EDGE,"E83"),sQuery(id+"F0.wireOp",EDGE,"E84"),sQuery(id+"F0.wireOp",EDGE,"E85"),sQuery(id+"F0.wireOp",EDGE,"E86"),sQuery(id+"F0.wireOp",EDGE,"E87"),sQuery(id+"F0.wireOp",EDGE,"E88"),sQuery(id+"F0.wireOp",EDGE,"E89"),sQuery(id+"F0.wireOp",EDGE,"E90"),sQuery(id+"F0.wireOp",EDGE,"E91"),sQuery(id+"F0.wireOp",EDGE,"E92"),sQuery(id+"F0.wireOp",EDGE,"E93"),sQuery(id+"F0.wireOp",EDGE,"E94"),sQuery(id+"F0.wireOp",EDGE,"E95"),sQuery(id+"F0.wireOp",EDGE,"E96"),sQuery(id+"F0.wireOp",EDGE,"E97"),sQuery(id+"F0.wireOp",EDGE,"E98"),sQuery(id+"F0.wireOp",EDGE,"E99"),sQuery(id+"F0.wireOp",EDGE,"E100"),sQuery(id+"F0.wireOp",EDGE,"E101"),sQuery(id+"F0.wireOp",EDGE,"E102"),sQuery(id+"F0.wireOp",EDGE,"E103"),sQuery(id+"F0.wireOp",EDGE,"E104"),sQuery(id+"F0.wireOp",EDGE,"E105"),sQuery(id+"F0.wireOp",EDGE,"E106"),sQuery(id+"F0.wireOp",EDGE,"E107"),sQuery(id+"F0.wireOp",EDGE,"E108"),sQuery(id+"F0.wireOp",EDGE,"E109"),sQuery(id+"F0.wireOp",EDGE,"E110"),sQuery(id+"F0.wireOp",EDGE,"E111"),sQuery(id+"F0.wireOp",EDGE,"E112"),sQuery(id+"F0.wireOp",EDGE,"E113"),sQuery(id+"F0.wireOp",EDGE,"E114"),sQuery(id+"F0.wireOp",EDGE,"E115")])],"isStart":false})]});
            var Q8;
            Q8=makeQuery(id+"F6.opFillet","BLEND_EDGE",EDGE,{"blendedFrom":[makeQuery(id+"F5.boolean.opBoolean","COPY",EDGE,{"derivedFrom":makeQuery(id+"F5.opExtrude","CAP_EDGE",EDGE,{"disambiguationData":[OSD([sQuery(id+"F4.wireOp",EDGE,"E757.0.1.0")])],"isStart":false})}),makeQuery(id+"F1.opExtrude","CAP_FACE",FACE,{"disambiguationData":[OSD([sQuery(id+"F0.wireOp",EDGE,"E0"),sQuery(id+"F0.wireOp",EDGE,"E1"),sQuery(id+"F0.wireOp",EDGE,"E2"),sQuery(id+"F0.wireOp",EDGE,"E3"),sQuery(id+"F0.wireOp",EDGE,"E4"),sQuery(id+"F0.wireOp",EDGE,"E5"),sQuery(id+"F0.wireOp",EDGE,"E6"),sQuery(id+"F0.wireOp",EDGE,"E7"),sQuery(id+"F0.wireOp",EDGE,"E8"),sQuery(id+"F0.wireOp",EDGE,"E9"),sQuery(id+"F0.wireOp",EDGE,"E10"),sQuery(id+"F0.wireOp",EDGE,"E11"),sQuery(id+"F0.wireOp",EDGE,"E12"),sQuery(id+"F0.wireOp",EDGE,"E13"),sQuery(id+"F0.wireOp",EDGE,"E14"),sQuery(id+"F0.wireOp",EDGE,"E15"),sQuery(id+"F0.wireOp",EDGE,"E16"),sQuery(id+"F0.wireOp",EDGE,"E17"),sQuery(id+"F0.wireOp",EDGE,"E18"),sQuery(id+"F0.wireOp",EDGE,"E19"),sQuery(id+"F0.wireOp",EDGE,"E20"),sQuery(id+"F0.wireOp",EDGE,"E21"),sQuery(id+"F0.wireOp",EDGE,"E22"),sQuery(id+"F0.wireOp",EDGE,"E23"),sQuery(id+"F0.wireOp",EDGE,"E24"),sQuery(id+"F0.wireOp",EDGE,"E25"),sQuery(id+"F0.wireOp",EDGE,"E26"),sQuery(id+"F0.wireOp",EDGE,"E27"),sQuery(id+"F0.wireOp",EDGE,"E28"),sQuery(id+"F0.wireOp",EDGE,"E29"),sQuery(id+"F0.wireOp",EDGE,"E30"),sQuery(id+"F0.wireOp",EDGE,"E31"),sQuery(id+"F0.wireOp",EDGE,"E32"),sQuery(id+"F0.wireOp",EDGE,"E33"),sQuery(id+"F0.wireOp",EDGE,"E34"),sQuery(id+"F0.wireOp",EDGE,"E35"),sQuery(id+"F0.wireOp",EDGE,"E36"),sQuery(id+"F0.wireOp",EDGE,"E37"),sQuery(id+"F0.wireOp",EDGE,"E38"),sQuery(id+"F0.wireOp",EDGE,"E39"),sQuery(id+"F0.wireOp",EDGE,"E40"),sQuery(id+"F0.wireOp",EDGE,"E41"),sQuery(id+"F0.wireOp",EDGE,"E42"),sQuery(id+"F0.wireOp",EDGE,"E43"),sQuery(id+"F0.wireOp",EDGE,"E44"),sQuery(id+"F0.wireOp",EDGE,"E45"),sQuery(id+"F0.wireOp",EDGE,"E46"),sQuery(id+"F0.wireOp",EDGE,"E47"),sQuery(id+"F0.wireOp",EDGE,"E48"),sQuery(id+"F0.wireOp",EDGE,"E49"),sQuery(id+"F0.wireOp",EDGE,"E50"),sQuery(id+"F0.wireOp",EDGE,"E51"),sQuery(id+"F0.wireOp",EDGE,"E52"),sQuery(id+"F0.wireOp",EDGE,"E53"),sQuery(id+"F0.wireOp",EDGE,"E54"),sQuery(id+"F0.wireOp",EDGE,"E55"),sQuery(id+"F0.wireOp",EDGE,"E56"),sQuery(id+"F0.wireOp",EDGE,"E57"),sQuery(id+"F0.wireOp",EDGE,"E58"),sQuery(id+"F0.wireOp",EDGE,"E59"),sQuery(id+"F0.wireOp",EDGE,"E60"),sQuery(id+"F0.wireOp",EDGE,"E61"),sQuery(id+"F0.wireOp",EDGE,"E62"),sQuery(id+"F0.wireOp",EDGE,"E63"),sQuery(id+"F0.wireOp",EDGE,"E64"),sQuery(id+"F0.wireOp",EDGE,"E65"),sQuery(id+"F0.wireOp",EDGE,"E66"),sQuery(id+"F0.wireOp",EDGE,"E67"),sQuery(id+"F0.wireOp",EDGE,"E68"),sQuery(id+"F0.wireOp",EDGE,"E69"),sQuery(id+"F0.wireOp",EDGE,"E70"),sQuery(id+"F0.wireOp",EDGE,"E71"),sQuery(id+"F0.wireOp",EDGE,"E72"),sQuery(id+"F0.wireOp",EDGE,"E73"),sQuery(id+"F0.wireOp",EDGE,"E74"),sQuery(id+"F0.wireOp",EDGE,"E75"),sQuery(id+"F0.wireOp",EDGE,"E76"),sQuery(id+"F0.wireOp",EDGE,"E77"),sQuery(id+"F0.wireOp",EDGE,"E78"),sQuery(id+"F0.wireOp",EDGE,"E79"),sQuery(id+"F0.wireOp",EDGE,"E80"),sQuery(id+"F0.wireOp",EDGE,"E81"),sQuery(id+"F0.wireOp",EDGE,"E82"),sQuery(id+"F0.wireOp",EDGE,"E83"),sQuery(id+"F0.wireOp",EDGE,"E84"),sQuery(id+"F0.wireOp",EDGE,"E85"),sQuery(id+"F0.wireOp",EDGE,"E86"),sQuery(id+"F0.wireOp",EDGE,"E87"),sQuery(id+"F0.wireOp",EDGE,"E88"),sQuery(id+"F0.wireOp",EDGE,"E89"),sQuery(id+"F0.wireOp",EDGE,"E90"),sQuery(id+"F0.wireOp",EDGE,"E91"),sQuery(id+"F0.wireOp",EDGE,"E92"),sQuery(id+"F0.wireOp",EDGE,"E93"),sQuery(id+"F0.wireOp",EDGE,"E94"),sQuery(id+"F0.wireOp",EDGE,"E95"),sQuery(id+"F0.wireOp",EDGE,"E96"),sQuery(id+"F0.wireOp",EDGE,"E97"),sQuery(id+"F0.wireOp",EDGE,"E98"),sQuery(id+"F0.wireOp",EDGE,"E99"),sQuery(id+"F0.wireOp",EDGE,"E100"),sQuery(id+"F0.wireOp",EDGE,"E101"),sQuery(id+"F0.wireOp",EDGE,"E102"),sQuery(id+"F0.wireOp",EDGE,"E103"),sQuery(id+"F0.wireOp",EDGE,"E104"),sQuery(id+"F0.wireOp",EDGE,"E105"),sQuery(id+"F0.wireOp",EDGE,"E106"),sQuery(id+"F0.wireOp",EDGE,"E107"),sQuery(id+"F0.wireOp",EDGE,"E108"),sQuery(id+"F0.wireOp",EDGE,"E109"),sQuery(id+"F0.wireOp",EDGE,"E110"),sQuery(id+"F0.wireOp",EDGE,"E111"),sQuery(id+"F0.wireOp",EDGE,"E112"),sQuery(id+"F0.wireOp",EDGE,"E113"),sQuery(id+"F0.wireOp",EDGE,"E114"),sQuery(id+"F0.wireOp",EDGE,"E115")])],"isStart":false})],"blendedInto":[makeQuery(id+"F1.opExtrude","CAP_FACE",FACE,{"disambiguationData":[OSD([sQuery(id+"F0.wireOp",EDGE,"E0"),sQuery(id+"F0.wireOp",EDGE,"E1"),sQuery(id+"F0.wireOp",EDGE,"E2"),sQuery(id+"F0.wireOp",EDGE,"E3"),sQuery(id+"F0.wireOp",EDGE,"E4"),sQuery(id+"F0.wireOp",EDGE,"E5"),sQuery(id+"F0.wireOp",EDGE,"E6"),sQuery(id+"F0.wireOp",EDGE,"E7"),sQuery(id+"F0.wireOp",EDGE,"E8"),sQuery(id+"F0.wireOp",EDGE,"E9"),sQuery(id+"F0.wireOp",EDGE,"E10"),sQuery(id+"F0.wireOp",EDGE,"E11"),sQuery(id+"F0.wireOp",EDGE,"E12"),sQuery(id+"F0.wireOp",EDGE,"E13"),sQuery(id+"F0.wireOp",EDGE,"E14"),sQuery(id+"F0.wireOp",EDGE,"E15"),sQuery(id+"F0.wireOp",EDGE,"E16"),sQuery(id+"F0.wireOp",EDGE,"E17"),sQuery(id+"F0.wireOp",EDGE,"E18"),sQuery(id+"F0.wireOp",EDGE,"E19"),sQuery(id+"F0.wireOp",EDGE,"E20"),sQuery(id+"F0.wireOp",EDGE,"E21"),sQuery(id+"F0.wireOp",EDGE,"E22"),sQuery(id+"F0.wireOp",EDGE,"E23"),sQuery(id+"F0.wireOp",EDGE,"E24"),sQuery(id+"F0.wireOp",EDGE,"E25"),sQuery(id+"F0.wireOp",EDGE,"E26"),sQuery(id+"F0.wireOp",EDGE,"E27"),sQuery(id+"F0.wireOp",EDGE,"E28"),sQuery(id+"F0.wireOp",EDGE,"E29"),sQuery(id+"F0.wireOp",EDGE,"E30"),sQuery(id+"F0.wireOp",EDGE,"E31"),sQuery(id+"F0.wireOp",EDGE,"E32"),sQuery(id+"F0.wireOp",EDGE,"E33"),sQuery(id+"F0.wireOp",EDGE,"E34"),sQuery(id+"F0.wireOp",EDGE,"E35"),sQuery(id+"F0.wireOp",EDGE,"E36"),sQuery(id+"F0.wireOp",EDGE,"E37"),sQuery(id+"F0.wireOp",EDGE,"E38"),sQuery(id+"F0.wireOp",EDGE,"E39"),sQuery(id+"F0.wireOp",EDGE,"E40"),sQuery(id+"F0.wireOp",EDGE,"E41"),sQuery(id+"F0.wireOp",EDGE,"E42"),sQuery(id+"F0.wireOp",EDGE,"E43"),sQuery(id+"F0.wireOp",EDGE,"E44"),sQuery(id+"F0.wireOp",EDGE,"E45"),sQuery(id+"F0.wireOp",EDGE,"E46"),sQuery(id+"F0.wireOp",EDGE,"E47"),sQuery(id+"F0.wireOp",EDGE,"E48"),sQuery(id+"F0.wireOp",EDGE,"E49"),sQuery(id+"F0.wireOp",EDGE,"E50"),sQuery(id+"F0.wireOp",EDGE,"E51"),sQuery(id+"F0.wireOp",EDGE,"E52"),sQuery(id+"F0.wireOp",EDGE,"E53"),sQuery(id+"F0.wireOp",EDGE,"E54"),sQuery(id+"F0.wireOp",EDGE,"E55"),sQuery(id+"F0.wireOp",EDGE,"E56"),sQuery(id+"F0.wireOp",EDGE,"E57"),sQuery(id+"F0.wireOp",EDGE,"E58"),sQuery(id+"F0.wireOp",EDGE,"E59"),sQuery(id+"F0.wireOp",EDGE,"E60"),sQuery(id+"F0.wireOp",EDGE,"E61"),sQuery(id+"F0.wireOp",EDGE,"E62"),sQuery(id+"F0.wireOp",EDGE,"E63"),sQuery(id+"F0.wireOp",EDGE,"E64"),sQuery(id+"F0.wireOp",EDGE,"E65"),sQuery(id+"F0.wireOp",EDGE,"E66"),sQuery(id+"F0.wireOp",EDGE,"E67"),sQuery(id+"F0.wireOp",EDGE,"E68"),sQuery(id+"F0.wireOp",EDGE,"E69"),sQuery(id+"F0.wireOp",EDGE,"E70"),sQuery(id+"F0.wireOp",EDGE,"E71"),sQuery(id+"F0.wireOp",EDGE,"E72"),sQuery(id+"F0.wireOp",EDGE,"E73"),sQuery(id+"F0.wireOp",EDGE,"E74"),sQuery(id+"F0.wireOp",EDGE,"E75"),sQuery(id+"F0.wireOp",EDGE,"E76"),sQuery(id+"F0.wireOp",EDGE,"E77"),sQuery(id+"F0.wireOp",EDGE,"E78"),sQuery(id+"F0.wireOp",EDGE,"E79"),sQuery(id+"F0.wireOp",EDGE,"E80"),sQuery(id+"F0.wireOp",EDGE,"E81"),sQuery(id+"F0.wireOp",EDGE,"E82"),sQuery(id+"F0.wireOp",EDGE,"E83"),sQuery(id+"F0.wireOp",EDGE,"E84"),sQuery(id+"F0.wireOp",EDGE,"E85"),sQuery(id+"F0.wireOp",EDGE,"E86"),sQuery(id+"F0.wireOp",EDGE,"E87"),sQuery(id+"F0.wireOp",EDGE,"E88"),sQuery(id+"F0.wireOp",EDGE,"E89"),sQuery(id+"F0.wireOp",EDGE,"E90"),sQuery(id+"F0.wireOp",EDGE,"E91"),sQuery(id+"F0.wireOp",EDGE,"E92"),sQuery(id+"F0.wireOp",EDGE,"E93"),sQuery(id+"F0.wireOp",EDGE,"E94"),sQuery(id+"F0.wireOp",EDGE,"E95"),sQuery(id+"F0.wireOp",EDGE,"E96"),sQuery(id+"F0.wireOp",EDGE,"E97"),sQuery(id+"F0.wireOp",EDGE,"E98"),sQuery(id+"F0.wireOp",EDGE,"E99"),sQuery(id+"F0.wireOp",EDGE,"E100"),sQuery(id+"F0.wireOp",EDGE,"E101"),sQuery(id+"F0.wireOp",EDGE,"E102"),sQuery(id+"F0.wireOp",EDGE,"E103"),sQuery(id+"F0.wireOp",EDGE,"E104"),sQuery(id+"F0.wireOp",EDGE,"E105"),sQuery(id+"F0.wireOp",EDGE,"E106"),sQuery(id+"F0.wireOp",EDGE,"E107"),sQuery(id+"F0.wireOp",EDGE,"E108"),sQuery(id+"F0.wireOp",EDGE,"E109"),sQuery(id+"F0.wireOp",EDGE,"E110"),sQuery(id+"F0.wireOp",EDGE,"E111"),sQuery(id+"F0.wireOp",EDGE,"E112"),sQuery(id+"F0.wireOp",EDGE,"E113"),sQuery(id+"F0.wireOp",EDGE,"E114"),sQuery(id+"F0.wireOp",EDGE,"E115")])],"isStart":false})]});
            var Q9;
            Q9=makeQuery(id+"F6.opFillet","BLEND_EDGE",EDGE,{"blendedFrom":[makeQuery(id+"F5.boolean.opBoolean","COPY",EDGE,{"derivedFrom":makeQuery(id+"F5.opExtrude","CAP_EDGE",EDGE,{"disambiguationData":[OSD([sQuery(id+"F4.wireOp",EDGE,"E756")])],"isStart":false})}),makeQuery(id+"F1.opExtrude","CAP_FACE",FACE,{"disambiguationData":[OSD([sQuery(id+"F0.wireOp",EDGE,"E0"),sQuery(id+"F0.wireOp",EDGE,"E1"),sQuery(id+"F0.wireOp",EDGE,"E2"),sQuery(id+"F0.wireOp",EDGE,"E3"),sQuery(id+"F0.wireOp",EDGE,"E4"),sQuery(id+"F0.wireOp",EDGE,"E5"),sQuery(id+"F0.wireOp",EDGE,"E6"),sQuery(id+"F0.wireOp",EDGE,"E7"),sQuery(id+"F0.wireOp",EDGE,"E8"),sQuery(id+"F0.wireOp",EDGE,"E9"),sQuery(id+"F0.wireOp",EDGE,"E10"),sQuery(id+"F0.wireOp",EDGE,"E11"),sQuery(id+"F0.wireOp",EDGE,"E12"),sQuery(id+"F0.wireOp",EDGE,"E13"),sQuery(id+"F0.wireOp",EDGE,"E14"),sQuery(id+"F0.wireOp",EDGE,"E15"),sQuery(id+"F0.wireOp",EDGE,"E16"),sQuery(id+"F0.wireOp",EDGE,"E17"),sQuery(id+"F0.wireOp",EDGE,"E18"),sQuery(id+"F0.wireOp",EDGE,"E19"),sQuery(id+"F0.wireOp",EDGE,"E20"),sQuery(id+"F0.wireOp",EDGE,"E21"),sQuery(id+"F0.wireOp",EDGE,"E22"),sQuery(id+"F0.wireOp",EDGE,"E23"),sQuery(id+"F0.wireOp",EDGE,"E24"),sQuery(id+"F0.wireOp",EDGE,"E25"),sQuery(id+"F0.wireOp",EDGE,"E26"),sQuery(id+"F0.wireOp",EDGE,"E27"),sQuery(id+"F0.wireOp",EDGE,"E28"),sQuery(id+"F0.wireOp",EDGE,"E29"),sQuery(id+"F0.wireOp",EDGE,"E30"),sQuery(id+"F0.wireOp",EDGE,"E31"),sQuery(id+"F0.wireOp",EDGE,"E32"),sQuery(id+"F0.wireOp",EDGE,"E33"),sQuery(id+"F0.wireOp",EDGE,"E34"),sQuery(id+"F0.wireOp",EDGE,"E35"),sQuery(id+"F0.wireOp",EDGE,"E36"),sQuery(id+"F0.wireOp",EDGE,"E37"),sQuery(id+"F0.wireOp",EDGE,"E38"),sQuery(id+"F0.wireOp",EDGE,"E39"),sQuery(id+"F0.wireOp",EDGE,"E40"),sQuery(id+"F0.wireOp",EDGE,"E41"),sQuery(id+"F0.wireOp",EDGE,"E42"),sQuery(id+"F0.wireOp",EDGE,"E43"),sQuery(id+"F0.wireOp",EDGE,"E44"),sQuery(id+"F0.wireOp",EDGE,"E45"),sQuery(id+"F0.wireOp",EDGE,"E46"),sQuery(id+"F0.wireOp",EDGE,"E47"),sQuery(id+"F0.wireOp",EDGE,"E48"),sQuery(id+"F0.wireOp",EDGE,"E49"),sQuery(id+"F0.wireOp",EDGE,"E50"),sQuery(id+"F0.wireOp",EDGE,"E51"),sQuery(id+"F0.wireOp",EDGE,"E52"),sQuery(id+"F0.wireOp",EDGE,"E53"),sQuery(id+"F0.wireOp",EDGE,"E54"),sQuery(id+"F0.wireOp",EDGE,"E55"),sQuery(id+"F0.wireOp",EDGE,"E56"),sQuery(id+"F0.wireOp",EDGE,"E57"),sQuery(id+"F0.wireOp",EDGE,"E58"),sQuery(id+"F0.wireOp",EDGE,"E59"),sQuery(id+"F0.wireOp",EDGE,"E60"),sQuery(id+"F0.wireOp",EDGE,"E61"),sQuery(id+"F0.wireOp",EDGE,"E62"),sQuery(id+"F0.wireOp",EDGE,"E63"),sQuery(id+"F0.wireOp",EDGE,"E64"),sQuery(id+"F0.wireOp",EDGE,"E65"),sQuery(id+"F0.wireOp",EDGE,"E66"),sQuery(id+"F0.wireOp",EDGE,"E67"),sQuery(id+"F0.wireOp",EDGE,"E68"),sQuery(id+"F0.wireOp",EDGE,"E69"),sQuery(id+"F0.wireOp",EDGE,"E70"),sQuery(id+"F0.wireOp",EDGE,"E71"),sQuery(id+"F0.wireOp",EDGE,"E72"),sQuery(id+"F0.wireOp",EDGE,"E73"),sQuery(id+"F0.wireOp",EDGE,"E74"),sQuery(id+"F0.wireOp",EDGE,"E75"),sQuery(id+"F0.wireOp",EDGE,"E76"),sQuery(id+"F0.wireOp",EDGE,"E77"),sQuery(id+"F0.wireOp",EDGE,"E78"),sQuery(id+"F0.wireOp",EDGE,"E79"),sQuery(id+"F0.wireOp",EDGE,"E80"),sQuery(id+"F0.wireOp",EDGE,"E81"),sQuery(id+"F0.wireOp",EDGE,"E82"),sQuery(id+"F0.wireOp",EDGE,"E83"),sQuery(id+"F0.wireOp",EDGE,"E84"),sQuery(id+"F0.wireOp",EDGE,"E85"),sQuery(id+"F0.wireOp",EDGE,"E86"),sQuery(id+"F0.wireOp",EDGE,"E87"),sQuery(id+"F0.wireOp",EDGE,"E88"),sQuery(id+"F0.wireOp",EDGE,"E89"),sQuery(id+"F0.wireOp",EDGE,"E90"),sQuery(id+"F0.wireOp",EDGE,"E91"),sQuery(id+"F0.wireOp",EDGE,"E92"),sQuery(id+"F0.wireOp",EDGE,"E93"),sQuery(id+"F0.wireOp",EDGE,"E94"),sQuery(id+"F0.wireOp",EDGE,"E95"),sQuery(id+"F0.wireOp",EDGE,"E96"),sQuery(id+"F0.wireOp",EDGE,"E97"),sQuery(id+"F0.wireOp",EDGE,"E98"),sQuery(id+"F0.wireOp",EDGE,"E99"),sQuery(id+"F0.wireOp",EDGE,"E100"),sQuery(id+"F0.wireOp",EDGE,"E101"),sQuery(id+"F0.wireOp",EDGE,"E102"),sQuery(id+"F0.wireOp",EDGE,"E103"),sQuery(id+"F0.wireOp",EDGE,"E104"),sQuery(id+"F0.wireOp",EDGE,"E105"),sQuery(id+"F0.wireOp",EDGE,"E106"),sQuery(id+"F0.wireOp",EDGE,"E107"),sQuery(id+"F0.wireOp",EDGE,"E108"),sQuery(id+"F0.wireOp",EDGE,"E109"),sQuery(id+"F0.wireOp",EDGE,"E110"),sQuery(id+"F0.wireOp",EDGE,"E111"),sQuery(id+"F0.wireOp",EDGE,"E112"),sQuery(id+"F0.wireOp",EDGE,"E113"),sQuery(id+"F0.wireOp",EDGE,"E114"),sQuery(id+"F0.wireOp",EDGE,"E115")])],"isStart":false})],"blendedInto":[makeQuery(id+"F1.opExtrude","CAP_FACE",FACE,{"disambiguationData":[OSD([sQuery(id+"F0.wireOp",EDGE,"E0"),sQuery(id+"F0.wireOp",EDGE,"E1"),sQuery(id+"F0.wireOp",EDGE,"E2"),sQuery(id+"F0.wireOp",EDGE,"E3"),sQuery(id+"F0.wireOp",EDGE,"E4"),sQuery(id+"F0.wireOp",EDGE,"E5"),sQuery(id+"F0.wireOp",EDGE,"E6"),sQuery(id+"F0.wireOp",EDGE,"E7"),sQuery(id+"F0.wireOp",EDGE,"E8"),sQuery(id+"F0.wireOp",EDGE,"E9"),sQuery(id+"F0.wireOp",EDGE,"E10"),sQuery(id+"F0.wireOp",EDGE,"E11"),sQuery(id+"F0.wireOp",EDGE,"E12"),sQuery(id+"F0.wireOp",EDGE,"E13"),sQuery(id+"F0.wireOp",EDGE,"E14"),sQuery(id+"F0.wireOp",EDGE,"E15"),sQuery(id+"F0.wireOp",EDGE,"E16"),sQuery(id+"F0.wireOp",EDGE,"E17"),sQuery(id+"F0.wireOp",EDGE,"E18"),sQuery(id+"F0.wireOp",EDGE,"E19"),sQuery(id+"F0.wireOp",EDGE,"E20"),sQuery(id+"F0.wireOp",EDGE,"E21"),sQuery(id+"F0.wireOp",EDGE,"E22"),sQuery(id+"F0.wireOp",EDGE,"E23"),sQuery(id+"F0.wireOp",EDGE,"E24"),sQuery(id+"F0.wireOp",EDGE,"E25"),sQuery(id+"F0.wireOp",EDGE,"E26"),sQuery(id+"F0.wireOp",EDGE,"E27"),sQuery(id+"F0.wireOp",EDGE,"E28"),sQuery(id+"F0.wireOp",EDGE,"E29"),sQuery(id+"F0.wireOp",EDGE,"E30"),sQuery(id+"F0.wireOp",EDGE,"E31"),sQuery(id+"F0.wireOp",EDGE,"E32"),sQuery(id+"F0.wireOp",EDGE,"E33"),sQuery(id+"F0.wireOp",EDGE,"E34"),sQuery(id+"F0.wireOp",EDGE,"E35"),sQuery(id+"F0.wireOp",EDGE,"E36"),sQuery(id+"F0.wireOp",EDGE,"E37"),sQuery(id+"F0.wireOp",EDGE,"E38"),sQuery(id+"F0.wireOp",EDGE,"E39"),sQuery(id+"F0.wireOp",EDGE,"E40"),sQuery(id+"F0.wireOp",EDGE,"E41"),sQuery(id+"F0.wireOp",EDGE,"E42"),sQuery(id+"F0.wireOp",EDGE,"E43"),sQuery(id+"F0.wireOp",EDGE,"E44"),sQuery(id+"F0.wireOp",EDGE,"E45"),sQuery(id+"F0.wireOp",EDGE,"E46"),sQuery(id+"F0.wireOp",EDGE,"E47"),sQuery(id+"F0.wireOp",EDGE,"E48"),sQuery(id+"F0.wireOp",EDGE,"E49"),sQuery(id+"F0.wireOp",EDGE,"E50"),sQuery(id+"F0.wireOp",EDGE,"E51"),sQuery(id+"F0.wireOp",EDGE,"E52"),sQuery(id+"F0.wireOp",EDGE,"E53"),sQuery(id+"F0.wireOp",EDGE,"E54"),sQuery(id+"F0.wireOp",EDGE,"E55"),sQuery(id+"F0.wireOp",EDGE,"E56"),sQuery(id+"F0.wireOp",EDGE,"E57"),sQuery(id+"F0.wireOp",EDGE,"E58"),sQuery(id+"F0.wireOp",EDGE,"E59"),sQuery(id+"F0.wireOp",EDGE,"E60"),sQuery(id+"F0.wireOp",EDGE,"E61"),sQuery(id+"F0.wireOp",EDGE,"E62"),sQuery(id+"F0.wireOp",EDGE,"E63"),sQuery(id+"F0.wireOp",EDGE,"E64"),sQuery(id+"F0.wireOp",EDGE,"E65"),sQuery(id+"F0.wireOp",EDGE,"E66"),sQuery(id+"F0.wireOp",EDGE,"E67"),sQuery(id+"F0.wireOp",EDGE,"E68"),sQuery(id+"F0.wireOp",EDGE,"E69"),sQuery(id+"F0.wireOp",EDGE,"E70"),sQuery(id+"F0.wireOp",EDGE,"E71"),sQuery(id+"F0.wireOp",EDGE,"E72"),sQuery(id+"F0.wireOp",EDGE,"E73"),sQuery(id+"F0.wireOp",EDGE,"E74"),sQuery(id+"F0.wireOp",EDGE,"E75"),sQuery(id+"F0.wireOp",EDGE,"E76"),sQuery(id+"F0.wireOp",EDGE,"E77"),sQuery(id+"F0.wireOp",EDGE,"E78"),sQuery(id+"F0.wireOp",EDGE,"E79"),sQuery(id+"F0.wireOp",EDGE,"E80"),sQuery(id+"F0.wireOp",EDGE,"E81"),sQuery(id+"F0.wireOp",EDGE,"E82"),sQuery(id+"F0.wireOp",EDGE,"E83"),sQuery(id+"F0.wireOp",EDGE,"E84"),sQuery(id+"F0.wireOp",EDGE,"E85"),sQuery(id+"F0.wireOp",EDGE,"E86"),sQuery(id+"F0.wireOp",EDGE,"E87"),sQuery(id+"F0.wireOp",EDGE,"E88"),sQuery(id+"F0.wireOp",EDGE,"E89"),sQuery(id+"F0.wireOp",EDGE,"E90"),sQuery(id+"F0.wireOp",EDGE,"E91"),sQuery(id+"F0.wireOp",EDGE,"E92"),sQuery(id+"F0.wireOp",EDGE,"E93"),sQuery(id+"F0.wireOp",EDGE,"E94"),sQuery(id+"F0.wireOp",EDGE,"E95"),sQuery(id+"F0.wireOp",EDGE,"E96"),sQuery(id+"F0.wireOp",EDGE,"E97"),sQuery(id+"F0.wireOp",EDGE,"E98"),sQuery(id+"F0.wireOp",EDGE,"E99"),sQuery(id+"F0.wireOp",EDGE,"E100"),sQuery(id+"F0.wireOp",EDGE,"E101"),sQuery(id+"F0.wireOp",EDGE,"E102"),sQuery(id+"F0.wireOp",EDGE,"E103"),sQuery(id+"F0.wireOp",EDGE,"E104"),sQuery(id+"F0.wireOp",EDGE,"E105"),sQuery(id+"F0.wireOp",EDGE,"E106"),sQuery(id+"F0.wireOp",EDGE,"E107"),sQuery(id+"F0.wireOp",EDGE,"E108"),sQuery(id+"F0.wireOp",EDGE,"E109"),sQuery(id+"F0.wireOp",EDGE,"E110"),sQuery(id+"F0.wireOp",EDGE,"E111"),sQuery(id+"F0.wireOp",EDGE,"E112"),sQuery(id+"F0.wireOp",EDGE,"E113"),sQuery(id+"F0.wireOp",EDGE,"E114"),sQuery(id+"F0.wireOp",EDGE,"E115")])],"isStart":false})]});
            var Q10;
            Q10=makeQuery(id+"F6.opFillet","BLEND_EDGE",EDGE,{"blendedFrom":[makeQuery(id+"F5.boolean.opBoolean","COPY",EDGE,{"derivedFrom":makeQuery(id+"F5.opExtrude","CAP_EDGE",EDGE,{"disambiguationData":[OSD([sQuery(id+"F4.wireOp",EDGE,"E757.1.0.0")])],"isStart":false})}),makeQuery(id+"F1.opExtrude","CAP_FACE",FACE,{"disambiguationData":[OSD([sQuery(id+"F0.wireOp",EDGE,"E0"),sQuery(id+"F0.wireOp",EDGE,"E1"),sQuery(id+"F0.wireOp",EDGE,"E2"),sQuery(id+"F0.wireOp",EDGE,"E3"),sQuery(id+"F0.wireOp",EDGE,"E4"),sQuery(id+"F0.wireOp",EDGE,"E5"),sQuery(id+"F0.wireOp",EDGE,"E6"),sQuery(id+"F0.wireOp",EDGE,"E7"),sQuery(id+"F0.wireOp",EDGE,"E8"),sQuery(id+"F0.wireOp",EDGE,"E9"),sQuery(id+"F0.wireOp",EDGE,"E10"),sQuery(id+"F0.wireOp",EDGE,"E11"),sQuery(id+"F0.wireOp",EDGE,"E12"),sQuery(id+"F0.wireOp",EDGE,"E13"),sQuery(id+"F0.wireOp",EDGE,"E14"),sQuery(id+"F0.wireOp",EDGE,"E15"),sQuery(id+"F0.wireOp",EDGE,"E16"),sQuery(id+"F0.wireOp",EDGE,"E17"),sQuery(id+"F0.wireOp",EDGE,"E18"),sQuery(id+"F0.wireOp",EDGE,"E19"),sQuery(id+"F0.wireOp",EDGE,"E20"),sQuery(id+"F0.wireOp",EDGE,"E21"),sQuery(id+"F0.wireOp",EDGE,"E22"),sQuery(id+"F0.wireOp",EDGE,"E23"),sQuery(id+"F0.wireOp",EDGE,"E24"),sQuery(id+"F0.wireOp",EDGE,"E25"),sQuery(id+"F0.wireOp",EDGE,"E26"),sQuery(id+"F0.wireOp",EDGE,"E27"),sQuery(id+"F0.wireOp",EDGE,"E28"),sQuery(id+"F0.wireOp",EDGE,"E29"),sQuery(id+"F0.wireOp",EDGE,"E30"),sQuery(id+"F0.wireOp",EDGE,"E31"),sQuery(id+"F0.wireOp",EDGE,"E32"),sQuery(id+"F0.wireOp",EDGE,"E33"),sQuery(id+"F0.wireOp",EDGE,"E34"),sQuery(id+"F0.wireOp",EDGE,"E35"),sQuery(id+"F0.wireOp",EDGE,"E36"),sQuery(id+"F0.wireOp",EDGE,"E37"),sQuery(id+"F0.wireOp",EDGE,"E38"),sQuery(id+"F0.wireOp",EDGE,"E39"),sQuery(id+"F0.wireOp",EDGE,"E40"),sQuery(id+"F0.wireOp",EDGE,"E41"),sQuery(id+"F0.wireOp",EDGE,"E42"),sQuery(id+"F0.wireOp",EDGE,"E43"),sQuery(id+"F0.wireOp",EDGE,"E44"),sQuery(id+"F0.wireOp",EDGE,"E45"),sQuery(id+"F0.wireOp",EDGE,"E46"),sQuery(id+"F0.wireOp",EDGE,"E47"),sQuery(id+"F0.wireOp",EDGE,"E48"),sQuery(id+"F0.wireOp",EDGE,"E49"),sQuery(id+"F0.wireOp",EDGE,"E50"),sQuery(id+"F0.wireOp",EDGE,"E51"),sQuery(id+"F0.wireOp",EDGE,"E52"),sQuery(id+"F0.wireOp",EDGE,"E53"),sQuery(id+"F0.wireOp",EDGE,"E54"),sQuery(id+"F0.wireOp",EDGE,"E55"),sQuery(id+"F0.wireOp",EDGE,"E56"),sQuery(id+"F0.wireOp",EDGE,"E57"),sQuery(id+"F0.wireOp",EDGE,"E58"),sQuery(id+"F0.wireOp",EDGE,"E59"),sQuery(id+"F0.wireOp",EDGE,"E60"),sQuery(id+"F0.wireOp",EDGE,"E61"),sQuery(id+"F0.wireOp",EDGE,"E62"),sQuery(id+"F0.wireOp",EDGE,"E63"),sQuery(id+"F0.wireOp",EDGE,"E64"),sQuery(id+"F0.wireOp",EDGE,"E65"),sQuery(id+"F0.wireOp",EDGE,"E66"),sQuery(id+"F0.wireOp",EDGE,"E67"),sQuery(id+"F0.wireOp",EDGE,"E68"),sQuery(id+"F0.wireOp",EDGE,"E69"),sQuery(id+"F0.wireOp",EDGE,"E70"),sQuery(id+"F0.wireOp",EDGE,"E71"),sQuery(id+"F0.wireOp",EDGE,"E72"),sQuery(id+"F0.wireOp",EDGE,"E73"),sQuery(id+"F0.wireOp",EDGE,"E74"),sQuery(id+"F0.wireOp",EDGE,"E75"),sQuery(id+"F0.wireOp",EDGE,"E76"),sQuery(id+"F0.wireOp",EDGE,"E77"),sQuery(id+"F0.wireOp",EDGE,"E78"),sQuery(id+"F0.wireOp",EDGE,"E79"),sQuery(id+"F0.wireOp",EDGE,"E80"),sQuery(id+"F0.wireOp",EDGE,"E81"),sQuery(id+"F0.wireOp",EDGE,"E82"),sQuery(id+"F0.wireOp",EDGE,"E83"),sQuery(id+"F0.wireOp",EDGE,"E84"),sQuery(id+"F0.wireOp",EDGE,"E85"),sQuery(id+"F0.wireOp",EDGE,"E86"),sQuery(id+"F0.wireOp",EDGE,"E87"),sQuery(id+"F0.wireOp",EDGE,"E88"),sQuery(id+"F0.wireOp",EDGE,"E89"),sQuery(id+"F0.wireOp",EDGE,"E90"),sQuery(id+"F0.wireOp",EDGE,"E91"),sQuery(id+"F0.wireOp",EDGE,"E92"),sQuery(id+"F0.wireOp",EDGE,"E93"),sQuery(id+"F0.wireOp",EDGE,"E94"),sQuery(id+"F0.wireOp",EDGE,"E95"),sQuery(id+"F0.wireOp",EDGE,"E96"),sQuery(id+"F0.wireOp",EDGE,"E97"),sQuery(id+"F0.wireOp",EDGE,"E98"),sQuery(id+"F0.wireOp",EDGE,"E99"),sQuery(id+"F0.wireOp",EDGE,"E100"),sQuery(id+"F0.wireOp",EDGE,"E101"),sQuery(id+"F0.wireOp",EDGE,"E102"),sQuery(id+"F0.wireOp",EDGE,"E103"),sQuery(id+"F0.wireOp",EDGE,"E104"),sQuery(id+"F0.wireOp",EDGE,"E105"),sQuery(id+"F0.wireOp",EDGE,"E106"),sQuery(id+"F0.wireOp",EDGE,"E107"),sQuery(id+"F0.wireOp",EDGE,"E108"),sQuery(id+"F0.wireOp",EDGE,"E109"),sQuery(id+"F0.wireOp",EDGE,"E110"),sQuery(id+"F0.wireOp",EDGE,"E111"),sQuery(id+"F0.wireOp",EDGE,"E112"),sQuery(id+"F0.wireOp",EDGE,"E113"),sQuery(id+"F0.wireOp",EDGE,"E114"),sQuery(id+"F0.wireOp",EDGE,"E115")])],"isStart":false})],"blendedInto":[makeQuery(id+"F1.opExtrude","CAP_FACE",FACE,{"disambiguationData":[OSD([sQuery(id+"F0.wireOp",EDGE,"E0"),sQuery(id+"F0.wireOp",EDGE,"E1"),sQuery(id+"F0.wireOp",EDGE,"E2"),sQuery(id+"F0.wireOp",EDGE,"E3"),sQuery(id+"F0.wireOp",EDGE,"E4"),sQuery(id+"F0.wireOp",EDGE,"E5"),sQuery(id+"F0.wireOp",EDGE,"E6"),sQuery(id+"F0.wireOp",EDGE,"E7"),sQuery(id+"F0.wireOp",EDGE,"E8"),sQuery(id+"F0.wireOp",EDGE,"E9"),sQuery(id+"F0.wireOp",EDGE,"E10"),sQuery(id+"F0.wireOp",EDGE,"E11"),sQuery(id+"F0.wireOp",EDGE,"E12"),sQuery(id+"F0.wireOp",EDGE,"E13"),sQuery(id+"F0.wireOp",EDGE,"E14"),sQuery(id+"F0.wireOp",EDGE,"E15"),sQuery(id+"F0.wireOp",EDGE,"E16"),sQuery(id+"F0.wireOp",EDGE,"E17"),sQuery(id+"F0.wireOp",EDGE,"E18"),sQuery(id+"F0.wireOp",EDGE,"E19"),sQuery(id+"F0.wireOp",EDGE,"E20"),sQuery(id+"F0.wireOp",EDGE,"E21"),sQuery(id+"F0.wireOp",EDGE,"E22"),sQuery(id+"F0.wireOp",EDGE,"E23"),sQuery(id+"F0.wireOp",EDGE,"E24"),sQuery(id+"F0.wireOp",EDGE,"E25"),sQuery(id+"F0.wireOp",EDGE,"E26"),sQuery(id+"F0.wireOp",EDGE,"E27"),sQuery(id+"F0.wireOp",EDGE,"E28"),sQuery(id+"F0.wireOp",EDGE,"E29"),sQuery(id+"F0.wireOp",EDGE,"E30"),sQuery(id+"F0.wireOp",EDGE,"E31"),sQuery(id+"F0.wireOp",EDGE,"E32"),sQuery(id+"F0.wireOp",EDGE,"E33"),sQuery(id+"F0.wireOp",EDGE,"E34"),sQuery(id+"F0.wireOp",EDGE,"E35"),sQuery(id+"F0.wireOp",EDGE,"E36"),sQuery(id+"F0.wireOp",EDGE,"E37"),sQuery(id+"F0.wireOp",EDGE,"E38"),sQuery(id+"F0.wireOp",EDGE,"E39"),sQuery(id+"F0.wireOp",EDGE,"E40"),sQuery(id+"F0.wireOp",EDGE,"E41"),sQuery(id+"F0.wireOp",EDGE,"E42"),sQuery(id+"F0.wireOp",EDGE,"E43"),sQuery(id+"F0.wireOp",EDGE,"E44"),sQuery(id+"F0.wireOp",EDGE,"E45"),sQuery(id+"F0.wireOp",EDGE,"E46"),sQuery(id+"F0.wireOp",EDGE,"E47"),sQuery(id+"F0.wireOp",EDGE,"E48"),sQuery(id+"F0.wireOp",EDGE,"E49"),sQuery(id+"F0.wireOp",EDGE,"E50"),sQuery(id+"F0.wireOp",EDGE,"E51"),sQuery(id+"F0.wireOp",EDGE,"E52"),sQuery(id+"F0.wireOp",EDGE,"E53"),sQuery(id+"F0.wireOp",EDGE,"E54"),sQuery(id+"F0.wireOp",EDGE,"E55"),sQuery(id+"F0.wireOp",EDGE,"E56"),sQuery(id+"F0.wireOp",EDGE,"E57"),sQuery(id+"F0.wireOp",EDGE,"E58"),sQuery(id+"F0.wireOp",EDGE,"E59"),sQuery(id+"F0.wireOp",EDGE,"E60"),sQuery(id+"F0.wireOp",EDGE,"E61"),sQuery(id+"F0.wireOp",EDGE,"E62"),sQuery(id+"F0.wireOp",EDGE,"E63"),sQuery(id+"F0.wireOp",EDGE,"E64"),sQuery(id+"F0.wireOp",EDGE,"E65"),sQuery(id+"F0.wireOp",EDGE,"E66"),sQuery(id+"F0.wireOp",EDGE,"E67"),sQuery(id+"F0.wireOp",EDGE,"E68"),sQuery(id+"F0.wireOp",EDGE,"E69"),sQuery(id+"F0.wireOp",EDGE,"E70"),sQuery(id+"F0.wireOp",EDGE,"E71"),sQuery(id+"F0.wireOp",EDGE,"E72"),sQuery(id+"F0.wireOp",EDGE,"E73"),sQuery(id+"F0.wireOp",EDGE,"E74"),sQuery(id+"F0.wireOp",EDGE,"E75"),sQuery(id+"F0.wireOp",EDGE,"E76"),sQuery(id+"F0.wireOp",EDGE,"E77"),sQuery(id+"F0.wireOp",EDGE,"E78"),sQuery(id+"F0.wireOp",EDGE,"E79"),sQuery(id+"F0.wireOp",EDGE,"E80"),sQuery(id+"F0.wireOp",EDGE,"E81"),sQuery(id+"F0.wireOp",EDGE,"E82"),sQuery(id+"F0.wireOp",EDGE,"E83"),sQuery(id+"F0.wireOp",EDGE,"E84"),sQuery(id+"F0.wireOp",EDGE,"E85"),sQuery(id+"F0.wireOp",EDGE,"E86"),sQuery(id+"F0.wireOp",EDGE,"E87"),sQuery(id+"F0.wireOp",EDGE,"E88"),sQuery(id+"F0.wireOp",EDGE,"E89"),sQuery(id+"F0.wireOp",EDGE,"E90"),sQuery(id+"F0.wireOp",EDGE,"E91"),sQuery(id+"F0.wireOp",EDGE,"E92"),sQuery(id+"F0.wireOp",EDGE,"E93"),sQuery(id+"F0.wireOp",EDGE,"E94"),sQuery(id+"F0.wireOp",EDGE,"E95"),sQuery(id+"F0.wireOp",EDGE,"E96"),sQuery(id+"F0.wireOp",EDGE,"E97"),sQuery(id+"F0.wireOp",EDGE,"E98"),sQuery(id+"F0.wireOp",EDGE,"E99"),sQuery(id+"F0.wireOp",EDGE,"E100"),sQuery(id+"F0.wireOp",EDGE,"E101"),sQuery(id+"F0.wireOp",EDGE,"E102"),sQuery(id+"F0.wireOp",EDGE,"E103"),sQuery(id+"F0.wireOp",EDGE,"E104"),sQuery(id+"F0.wireOp",EDGE,"E105"),sQuery(id+"F0.wireOp",EDGE,"E106"),sQuery(id+"F0.wireOp",EDGE,"E107"),sQuery(id+"F0.wireOp",EDGE,"E108"),sQuery(id+"F0.wireOp",EDGE,"E109"),sQuery(id+"F0.wireOp",EDGE,"E110"),sQuery(id+"F0.wireOp",EDGE,"E111"),sQuery(id+"F0.wireOp",EDGE,"E112"),sQuery(id+"F0.wireOp",EDGE,"E113"),sQuery(id+"F0.wireOp",EDGE,"E114"),sQuery(id+"F0.wireOp",EDGE,"E115")])],"isStart":false})]});
            var Q11;
            Q11=makeQuery(id+"F6.opFillet","BLEND_EDGE",EDGE,{"blendedFrom":[makeQuery(id+"F5.boolean.opBoolean","COPY",EDGE,{"derivedFrom":makeQuery(id+"F5.opExtrude","CAP_EDGE",EDGE,{"disambiguationData":[OSD([sQuery(id+"F4.wireOp",EDGE,"E757.1.1.0")])],"isStart":false})}),makeQuery(id+"F1.opExtrude","CAP_FACE",FACE,{"disambiguationData":[OSD([sQuery(id+"F0.wireOp",EDGE,"E0"),sQuery(id+"F0.wireOp",EDGE,"E1"),sQuery(id+"F0.wireOp",EDGE,"E2"),sQuery(id+"F0.wireOp",EDGE,"E3"),sQuery(id+"F0.wireOp",EDGE,"E4"),sQuery(id+"F0.wireOp",EDGE,"E5"),sQuery(id+"F0.wireOp",EDGE,"E6"),sQuery(id+"F0.wireOp",EDGE,"E7"),sQuery(id+"F0.wireOp",EDGE,"E8"),sQuery(id+"F0.wireOp",EDGE,"E9"),sQuery(id+"F0.wireOp",EDGE,"E10"),sQuery(id+"F0.wireOp",EDGE,"E11"),sQuery(id+"F0.wireOp",EDGE,"E12"),sQuery(id+"F0.wireOp",EDGE,"E13"),sQuery(id+"F0.wireOp",EDGE,"E14"),sQuery(id+"F0.wireOp",EDGE,"E15"),sQuery(id+"F0.wireOp",EDGE,"E16"),sQuery(id+"F0.wireOp",EDGE,"E17"),sQuery(id+"F0.wireOp",EDGE,"E18"),sQuery(id+"F0.wireOp",EDGE,"E19"),sQuery(id+"F0.wireOp",EDGE,"E20"),sQuery(id+"F0.wireOp",EDGE,"E21"),sQuery(id+"F0.wireOp",EDGE,"E22"),sQuery(id+"F0.wireOp",EDGE,"E23"),sQuery(id+"F0.wireOp",EDGE,"E24"),sQuery(id+"F0.wireOp",EDGE,"E25"),sQuery(id+"F0.wireOp",EDGE,"E26"),sQuery(id+"F0.wireOp",EDGE,"E27"),sQuery(id+"F0.wireOp",EDGE,"E28"),sQuery(id+"F0.wireOp",EDGE,"E29"),sQuery(id+"F0.wireOp",EDGE,"E30"),sQuery(id+"F0.wireOp",EDGE,"E31"),sQuery(id+"F0.wireOp",EDGE,"E32"),sQuery(id+"F0.wireOp",EDGE,"E33"),sQuery(id+"F0.wireOp",EDGE,"E34"),sQuery(id+"F0.wireOp",EDGE,"E35"),sQuery(id+"F0.wireOp",EDGE,"E36"),sQuery(id+"F0.wireOp",EDGE,"E37"),sQuery(id+"F0.wireOp",EDGE,"E38"),sQuery(id+"F0.wireOp",EDGE,"E39"),sQuery(id+"F0.wireOp",EDGE,"E40"),sQuery(id+"F0.wireOp",EDGE,"E41"),sQuery(id+"F0.wireOp",EDGE,"E42"),sQuery(id+"F0.wireOp",EDGE,"E43"),sQuery(id+"F0.wireOp",EDGE,"E44"),sQuery(id+"F0.wireOp",EDGE,"E45"),sQuery(id+"F0.wireOp",EDGE,"E46"),sQuery(id+"F0.wireOp",EDGE,"E47"),sQuery(id+"F0.wireOp",EDGE,"E48"),sQuery(id+"F0.wireOp",EDGE,"E49"),sQuery(id+"F0.wireOp",EDGE,"E50"),sQuery(id+"F0.wireOp",EDGE,"E51"),sQuery(id+"F0.wireOp",EDGE,"E52"),sQuery(id+"F0.wireOp",EDGE,"E53"),sQuery(id+"F0.wireOp",EDGE,"E54"),sQuery(id+"F0.wireOp",EDGE,"E55"),sQuery(id+"F0.wireOp",EDGE,"E56"),sQuery(id+"F0.wireOp",EDGE,"E57"),sQuery(id+"F0.wireOp",EDGE,"E58"),sQuery(id+"F0.wireOp",EDGE,"E59"),sQuery(id+"F0.wireOp",EDGE,"E60"),sQuery(id+"F0.wireOp",EDGE,"E61"),sQuery(id+"F0.wireOp",EDGE,"E62"),sQuery(id+"F0.wireOp",EDGE,"E63"),sQuery(id+"F0.wireOp",EDGE,"E64"),sQuery(id+"F0.wireOp",EDGE,"E65"),sQuery(id+"F0.wireOp",EDGE,"E66"),sQuery(id+"F0.wireOp",EDGE,"E67"),sQuery(id+"F0.wireOp",EDGE,"E68"),sQuery(id+"F0.wireOp",EDGE,"E69"),sQuery(id+"F0.wireOp",EDGE,"E70"),sQuery(id+"F0.wireOp",EDGE,"E71"),sQuery(id+"F0.wireOp",EDGE,"E72"),sQuery(id+"F0.wireOp",EDGE,"E73"),sQuery(id+"F0.wireOp",EDGE,"E74"),sQuery(id+"F0.wireOp",EDGE,"E75"),sQuery(id+"F0.wireOp",EDGE,"E76"),sQuery(id+"F0.wireOp",EDGE,"E77"),sQuery(id+"F0.wireOp",EDGE,"E78"),sQuery(id+"F0.wireOp",EDGE,"E79"),sQuery(id+"F0.wireOp",EDGE,"E80"),sQuery(id+"F0.wireOp",EDGE,"E81"),sQuery(id+"F0.wireOp",EDGE,"E82"),sQuery(id+"F0.wireOp",EDGE,"E83"),sQuery(id+"F0.wireOp",EDGE,"E84"),sQuery(id+"F0.wireOp",EDGE,"E85"),sQuery(id+"F0.wireOp",EDGE,"E86"),sQuery(id+"F0.wireOp",EDGE,"E87"),sQuery(id+"F0.wireOp",EDGE,"E88"),sQuery(id+"F0.wireOp",EDGE,"E89"),sQuery(id+"F0.wireOp",EDGE,"E90"),sQuery(id+"F0.wireOp",EDGE,"E91"),sQuery(id+"F0.wireOp",EDGE,"E92"),sQuery(id+"F0.wireOp",EDGE,"E93"),sQuery(id+"F0.wireOp",EDGE,"E94"),sQuery(id+"F0.wireOp",EDGE,"E95"),sQuery(id+"F0.wireOp",EDGE,"E96"),sQuery(id+"F0.wireOp",EDGE,"E97"),sQuery(id+"F0.wireOp",EDGE,"E98"),sQuery(id+"F0.wireOp",EDGE,"E99"),sQuery(id+"F0.wireOp",EDGE,"E100"),sQuery(id+"F0.wireOp",EDGE,"E101"),sQuery(id+"F0.wireOp",EDGE,"E102"),sQuery(id+"F0.wireOp",EDGE,"E103"),sQuery(id+"F0.wireOp",EDGE,"E104"),sQuery(id+"F0.wireOp",EDGE,"E105"),sQuery(id+"F0.wireOp",EDGE,"E106"),sQuery(id+"F0.wireOp",EDGE,"E107"),sQuery(id+"F0.wireOp",EDGE,"E108"),sQuery(id+"F0.wireOp",EDGE,"E109"),sQuery(id+"F0.wireOp",EDGE,"E110"),sQuery(id+"F0.wireOp",EDGE,"E111"),sQuery(id+"F0.wireOp",EDGE,"E112"),sQuery(id+"F0.wireOp",EDGE,"E113"),sQuery(id+"F0.wireOp",EDGE,"E114"),sQuery(id+"F0.wireOp",EDGE,"E115")])],"isStart":false})],"blendedInto":[makeQuery(id+"F1.opExtrude","CAP_FACE",FACE,{"disambiguationData":[OSD([sQuery(id+"F0.wireOp",EDGE,"E0"),sQuery(id+"F0.wireOp",EDGE,"E1"),sQuery(id+"F0.wireOp",EDGE,"E2"),sQuery(id+"F0.wireOp",EDGE,"E3"),sQuery(id+"F0.wireOp",EDGE,"E4"),sQuery(id+"F0.wireOp",EDGE,"E5"),sQuery(id+"F0.wireOp",EDGE,"E6"),sQuery(id+"F0.wireOp",EDGE,"E7"),sQuery(id+"F0.wireOp",EDGE,"E8"),sQuery(id+"F0.wireOp",EDGE,"E9"),sQuery(id+"F0.wireOp",EDGE,"E10"),sQuery(id+"F0.wireOp",EDGE,"E11"),sQuery(id+"F0.wireOp",EDGE,"E12"),sQuery(id+"F0.wireOp",EDGE,"E13"),sQuery(id+"F0.wireOp",EDGE,"E14"),sQuery(id+"F0.wireOp",EDGE,"E15"),sQuery(id+"F0.wireOp",EDGE,"E16"),sQuery(id+"F0.wireOp",EDGE,"E17"),sQuery(id+"F0.wireOp",EDGE,"E18"),sQuery(id+"F0.wireOp",EDGE,"E19"),sQuery(id+"F0.wireOp",EDGE,"E20"),sQuery(id+"F0.wireOp",EDGE,"E21"),sQuery(id+"F0.wireOp",EDGE,"E22"),sQuery(id+"F0.wireOp",EDGE,"E23"),sQuery(id+"F0.wireOp",EDGE,"E24"),sQuery(id+"F0.wireOp",EDGE,"E25"),sQuery(id+"F0.wireOp",EDGE,"E26"),sQuery(id+"F0.wireOp",EDGE,"E27"),sQuery(id+"F0.wireOp",EDGE,"E28"),sQuery(id+"F0.wireOp",EDGE,"E29"),sQuery(id+"F0.wireOp",EDGE,"E30"),sQuery(id+"F0.wireOp",EDGE,"E31"),sQuery(id+"F0.wireOp",EDGE,"E32"),sQuery(id+"F0.wireOp",EDGE,"E33"),sQuery(id+"F0.wireOp",EDGE,"E34"),sQuery(id+"F0.wireOp",EDGE,"E35"),sQuery(id+"F0.wireOp",EDGE,"E36"),sQuery(id+"F0.wireOp",EDGE,"E37"),sQuery(id+"F0.wireOp",EDGE,"E38"),sQuery(id+"F0.wireOp",EDGE,"E39"),sQuery(id+"F0.wireOp",EDGE,"E40"),sQuery(id+"F0.wireOp",EDGE,"E41"),sQuery(id+"F0.wireOp",EDGE,"E42"),sQuery(id+"F0.wireOp",EDGE,"E43"),sQuery(id+"F0.wireOp",EDGE,"E44"),sQuery(id+"F0.wireOp",EDGE,"E45"),sQuery(id+"F0.wireOp",EDGE,"E46"),sQuery(id+"F0.wireOp",EDGE,"E47"),sQuery(id+"F0.wireOp",EDGE,"E48"),sQuery(id+"F0.wireOp",EDGE,"E49"),sQuery(id+"F0.wireOp",EDGE,"E50"),sQuery(id+"F0.wireOp",EDGE,"E51"),sQuery(id+"F0.wireOp",EDGE,"E52"),sQuery(id+"F0.wireOp",EDGE,"E53"),sQuery(id+"F0.wireOp",EDGE,"E54"),sQuery(id+"F0.wireOp",EDGE,"E55"),sQuery(id+"F0.wireOp",EDGE,"E56"),sQuery(id+"F0.wireOp",EDGE,"E57"),sQuery(id+"F0.wireOp",EDGE,"E58"),sQuery(id+"F0.wireOp",EDGE,"E59"),sQuery(id+"F0.wireOp",EDGE,"E60"),sQuery(id+"F0.wireOp",EDGE,"E61"),sQuery(id+"F0.wireOp",EDGE,"E62"),sQuery(id+"F0.wireOp",EDGE,"E63"),sQuery(id+"F0.wireOp",EDGE,"E64"),sQuery(id+"F0.wireOp",EDGE,"E65"),sQuery(id+"F0.wireOp",EDGE,"E66"),sQuery(id+"F0.wireOp",EDGE,"E67"),sQuery(id+"F0.wireOp",EDGE,"E68"),sQuery(id+"F0.wireOp",EDGE,"E69"),sQuery(id+"F0.wireOp",EDGE,"E70"),sQuery(id+"F0.wireOp",EDGE,"E71"),sQuery(id+"F0.wireOp",EDGE,"E72"),sQuery(id+"F0.wireOp",EDGE,"E73"),sQuery(id+"F0.wireOp",EDGE,"E74"),sQuery(id+"F0.wireOp",EDGE,"E75"),sQuery(id+"F0.wireOp",EDGE,"E76"),sQuery(id+"F0.wireOp",EDGE,"E77"),sQuery(id+"F0.wireOp",EDGE,"E78"),sQuery(id+"F0.wireOp",EDGE,"E79"),sQuery(id+"F0.wireOp",EDGE,"E80"),sQuery(id+"F0.wireOp",EDGE,"E81"),sQuery(id+"F0.wireOp",EDGE,"E82"),sQuery(id+"F0.wireOp",EDGE,"E83"),sQuery(id+"F0.wireOp",EDGE,"E84"),sQuery(id+"F0.wireOp",EDGE,"E85"),sQuery(id+"F0.wireOp",EDGE,"E86"),sQuery(id+"F0.wireOp",EDGE,"E87"),sQuery(id+"F0.wireOp",EDGE,"E88"),sQuery(id+"F0.wireOp",EDGE,"E89"),sQuery(id+"F0.wireOp",EDGE,"E90"),sQuery(id+"F0.wireOp",EDGE,"E91"),sQuery(id+"F0.wireOp",EDGE,"E92"),sQuery(id+"F0.wireOp",EDGE,"E93"),sQuery(id+"F0.wireOp",EDGE,"E94"),sQuery(id+"F0.wireOp",EDGE,"E95"),sQuery(id+"F0.wireOp",EDGE,"E96"),sQuery(id+"F0.wireOp",EDGE,"E97"),sQuery(id+"F0.wireOp",EDGE,"E98"),sQuery(id+"F0.wireOp",EDGE,"E99"),sQuery(id+"F0.wireOp",EDGE,"E100"),sQuery(id+"F0.wireOp",EDGE,"E101"),sQuery(id+"F0.wireOp",EDGE,"E102"),sQuery(id+"F0.wireOp",EDGE,"E103"),sQuery(id+"F0.wireOp",EDGE,"E104"),sQuery(id+"F0.wireOp",EDGE,"E105"),sQuery(id+"F0.wireOp",EDGE,"E106"),sQuery(id+"F0.wireOp",EDGE,"E107"),sQuery(id+"F0.wireOp",EDGE,"E108"),sQuery(id+"F0.wireOp",EDGE,"E109"),sQuery(id+"F0.wireOp",EDGE,"E110"),sQuery(id+"F0.wireOp",EDGE,"E111"),sQuery(id+"F0.wireOp",EDGE,"E112"),sQuery(id+"F0.wireOp",EDGE,"E113"),sQuery(id+"F0.wireOp",EDGE,"E114"),sQuery(id+"F0.wireOp",EDGE,"E115")])],"isStart":false})]});
            var Q12;
            Q12=makeQuery(id+"F6.opFillet","BLEND_EDGE",EDGE,{"blendedFrom":[makeQuery(id+"F5.boolean.opBoolean","COPY",EDGE,{"derivedFrom":makeQuery(id+"F5.opExtrude","CAP_EDGE",EDGE,{"disambiguationData":[OSD([sQuery(id+"F4.wireOp",EDGE,"E757.2.0.0")])],"isStart":false})}),makeQuery(id+"F1.opExtrude","CAP_FACE",FACE,{"disambiguationData":[OSD([sQuery(id+"F0.wireOp",EDGE,"E0"),sQuery(id+"F0.wireOp",EDGE,"E1"),sQuery(id+"F0.wireOp",EDGE,"E2"),sQuery(id+"F0.wireOp",EDGE,"E3"),sQuery(id+"F0.wireOp",EDGE,"E4"),sQuery(id+"F0.wireOp",EDGE,"E5"),sQuery(id+"F0.wireOp",EDGE,"E6"),sQuery(id+"F0.wireOp",EDGE,"E7"),sQuery(id+"F0.wireOp",EDGE,"E8"),sQuery(id+"F0.wireOp",EDGE,"E9"),sQuery(id+"F0.wireOp",EDGE,"E10"),sQuery(id+"F0.wireOp",EDGE,"E11"),sQuery(id+"F0.wireOp",EDGE,"E12"),sQuery(id+"F0.wireOp",EDGE,"E13"),sQuery(id+"F0.wireOp",EDGE,"E14"),sQuery(id+"F0.wireOp",EDGE,"E15"),sQuery(id+"F0.wireOp",EDGE,"E16"),sQuery(id+"F0.wireOp",EDGE,"E17"),sQuery(id+"F0.wireOp",EDGE,"E18"),sQuery(id+"F0.wireOp",EDGE,"E19"),sQuery(id+"F0.wireOp",EDGE,"E20"),sQuery(id+"F0.wireOp",EDGE,"E21"),sQuery(id+"F0.wireOp",EDGE,"E22"),sQuery(id+"F0.wireOp",EDGE,"E23"),sQuery(id+"F0.wireOp",EDGE,"E24"),sQuery(id+"F0.wireOp",EDGE,"E25"),sQuery(id+"F0.wireOp",EDGE,"E26"),sQuery(id+"F0.wireOp",EDGE,"E27"),sQuery(id+"F0.wireOp",EDGE,"E28"),sQuery(id+"F0.wireOp",EDGE,"E29"),sQuery(id+"F0.wireOp",EDGE,"E30"),sQuery(id+"F0.wireOp",EDGE,"E31"),sQuery(id+"F0.wireOp",EDGE,"E32"),sQuery(id+"F0.wireOp",EDGE,"E33"),sQuery(id+"F0.wireOp",EDGE,"E34"),sQuery(id+"F0.wireOp",EDGE,"E35"),sQuery(id+"F0.wireOp",EDGE,"E36"),sQuery(id+"F0.wireOp",EDGE,"E37"),sQuery(id+"F0.wireOp",EDGE,"E38"),sQuery(id+"F0.wireOp",EDGE,"E39"),sQuery(id+"F0.wireOp",EDGE,"E40"),sQuery(id+"F0.wireOp",EDGE,"E41"),sQuery(id+"F0.wireOp",EDGE,"E42"),sQuery(id+"F0.wireOp",EDGE,"E43"),sQuery(id+"F0.wireOp",EDGE,"E44"),sQuery(id+"F0.wireOp",EDGE,"E45"),sQuery(id+"F0.wireOp",EDGE,"E46"),sQuery(id+"F0.wireOp",EDGE,"E47"),sQuery(id+"F0.wireOp",EDGE,"E48"),sQuery(id+"F0.wireOp",EDGE,"E49"),sQuery(id+"F0.wireOp",EDGE,"E50"),sQuery(id+"F0.wireOp",EDGE,"E51"),sQuery(id+"F0.wireOp",EDGE,"E52"),sQuery(id+"F0.wireOp",EDGE,"E53"),sQuery(id+"F0.wireOp",EDGE,"E54"),sQuery(id+"F0.wireOp",EDGE,"E55"),sQuery(id+"F0.wireOp",EDGE,"E56"),sQuery(id+"F0.wireOp",EDGE,"E57"),sQuery(id+"F0.wireOp",EDGE,"E58"),sQuery(id+"F0.wireOp",EDGE,"E59"),sQuery(id+"F0.wireOp",EDGE,"E60"),sQuery(id+"F0.wireOp",EDGE,"E61"),sQuery(id+"F0.wireOp",EDGE,"E62"),sQuery(id+"F0.wireOp",EDGE,"E63"),sQuery(id+"F0.wireOp",EDGE,"E64"),sQuery(id+"F0.wireOp",EDGE,"E65"),sQuery(id+"F0.wireOp",EDGE,"E66"),sQuery(id+"F0.wireOp",EDGE,"E67"),sQuery(id+"F0.wireOp",EDGE,"E68"),sQuery(id+"F0.wireOp",EDGE,"E69"),sQuery(id+"F0.wireOp",EDGE,"E70"),sQuery(id+"F0.wireOp",EDGE,"E71"),sQuery(id+"F0.wireOp",EDGE,"E72"),sQuery(id+"F0.wireOp",EDGE,"E73"),sQuery(id+"F0.wireOp",EDGE,"E74"),sQuery(id+"F0.wireOp",EDGE,"E75"),sQuery(id+"F0.wireOp",EDGE,"E76"),sQuery(id+"F0.wireOp",EDGE,"E77"),sQuery(id+"F0.wireOp",EDGE,"E78"),sQuery(id+"F0.wireOp",EDGE,"E79"),sQuery(id+"F0.wireOp",EDGE,"E80"),sQuery(id+"F0.wireOp",EDGE,"E81"),sQuery(id+"F0.wireOp",EDGE,"E82"),sQuery(id+"F0.wireOp",EDGE,"E83"),sQuery(id+"F0.wireOp",EDGE,"E84"),sQuery(id+"F0.wireOp",EDGE,"E85"),sQuery(id+"F0.wireOp",EDGE,"E86"),sQuery(id+"F0.wireOp",EDGE,"E87"),sQuery(id+"F0.wireOp",EDGE,"E88"),sQuery(id+"F0.wireOp",EDGE,"E89"),sQuery(id+"F0.wireOp",EDGE,"E90"),sQuery(id+"F0.wireOp",EDGE,"E91"),sQuery(id+"F0.wireOp",EDGE,"E92"),sQuery(id+"F0.wireOp",EDGE,"E93"),sQuery(id+"F0.wireOp",EDGE,"E94"),sQuery(id+"F0.wireOp",EDGE,"E95"),sQuery(id+"F0.wireOp",EDGE,"E96"),sQuery(id+"F0.wireOp",EDGE,"E97"),sQuery(id+"F0.wireOp",EDGE,"E98"),sQuery(id+"F0.wireOp",EDGE,"E99"),sQuery(id+"F0.wireOp",EDGE,"E100"),sQuery(id+"F0.wireOp",EDGE,"E101"),sQuery(id+"F0.wireOp",EDGE,"E102"),sQuery(id+"F0.wireOp",EDGE,"E103"),sQuery(id+"F0.wireOp",EDGE,"E104"),sQuery(id+"F0.wireOp",EDGE,"E105"),sQuery(id+"F0.wireOp",EDGE,"E106"),sQuery(id+"F0.wireOp",EDGE,"E107"),sQuery(id+"F0.wireOp",EDGE,"E108"),sQuery(id+"F0.wireOp",EDGE,"E109"),sQuery(id+"F0.wireOp",EDGE,"E110"),sQuery(id+"F0.wireOp",EDGE,"E111"),sQuery(id+"F0.wireOp",EDGE,"E112"),sQuery(id+"F0.wireOp",EDGE,"E113"),sQuery(id+"F0.wireOp",EDGE,"E114"),sQuery(id+"F0.wireOp",EDGE,"E115")])],"isStart":false})],"blendedInto":[makeQuery(id+"F1.opExtrude","CAP_FACE",FACE,{"disambiguationData":[OSD([sQuery(id+"F0.wireOp",EDGE,"E0"),sQuery(id+"F0.wireOp",EDGE,"E1"),sQuery(id+"F0.wireOp",EDGE,"E2"),sQuery(id+"F0.wireOp",EDGE,"E3"),sQuery(id+"F0.wireOp",EDGE,"E4"),sQuery(id+"F0.wireOp",EDGE,"E5"),sQuery(id+"F0.wireOp",EDGE,"E6"),sQuery(id+"F0.wireOp",EDGE,"E7"),sQuery(id+"F0.wireOp",EDGE,"E8"),sQuery(id+"F0.wireOp",EDGE,"E9"),sQuery(id+"F0.wireOp",EDGE,"E10"),sQuery(id+"F0.wireOp",EDGE,"E11"),sQuery(id+"F0.wireOp",EDGE,"E12"),sQuery(id+"F0.wireOp",EDGE,"E13"),sQuery(id+"F0.wireOp",EDGE,"E14"),sQuery(id+"F0.wireOp",EDGE,"E15"),sQuery(id+"F0.wireOp",EDGE,"E16"),sQuery(id+"F0.wireOp",EDGE,"E17"),sQuery(id+"F0.wireOp",EDGE,"E18"),sQuery(id+"F0.wireOp",EDGE,"E19"),sQuery(id+"F0.wireOp",EDGE,"E20"),sQuery(id+"F0.wireOp",EDGE,"E21"),sQuery(id+"F0.wireOp",EDGE,"E22"),sQuery(id+"F0.wireOp",EDGE,"E23"),sQuery(id+"F0.wireOp",EDGE,"E24"),sQuery(id+"F0.wireOp",EDGE,"E25"),sQuery(id+"F0.wireOp",EDGE,"E26"),sQuery(id+"F0.wireOp",EDGE,"E27"),sQuery(id+"F0.wireOp",EDGE,"E28"),sQuery(id+"F0.wireOp",EDGE,"E29"),sQuery(id+"F0.wireOp",EDGE,"E30"),sQuery(id+"F0.wireOp",EDGE,"E31"),sQuery(id+"F0.wireOp",EDGE,"E32"),sQuery(id+"F0.wireOp",EDGE,"E33"),sQuery(id+"F0.wireOp",EDGE,"E34"),sQuery(id+"F0.wireOp",EDGE,"E35"),sQuery(id+"F0.wireOp",EDGE,"E36"),sQuery(id+"F0.wireOp",EDGE,"E37"),sQuery(id+"F0.wireOp",EDGE,"E38"),sQuery(id+"F0.wireOp",EDGE,"E39"),sQuery(id+"F0.wireOp",EDGE,"E40"),sQuery(id+"F0.wireOp",EDGE,"E41"),sQuery(id+"F0.wireOp",EDGE,"E42"),sQuery(id+"F0.wireOp",EDGE,"E43"),sQuery(id+"F0.wireOp",EDGE,"E44"),sQuery(id+"F0.wireOp",EDGE,"E45"),sQuery(id+"F0.wireOp",EDGE,"E46"),sQuery(id+"F0.wireOp",EDGE,"E47"),sQuery(id+"F0.wireOp",EDGE,"E48"),sQuery(id+"F0.wireOp",EDGE,"E49"),sQuery(id+"F0.wireOp",EDGE,"E50"),sQuery(id+"F0.wireOp",EDGE,"E51"),sQuery(id+"F0.wireOp",EDGE,"E52"),sQuery(id+"F0.wireOp",EDGE,"E53"),sQuery(id+"F0.wireOp",EDGE,"E54"),sQuery(id+"F0.wireOp",EDGE,"E55"),sQuery(id+"F0.wireOp",EDGE,"E56"),sQuery(id+"F0.wireOp",EDGE,"E57"),sQuery(id+"F0.wireOp",EDGE,"E58"),sQuery(id+"F0.wireOp",EDGE,"E59"),sQuery(id+"F0.wireOp",EDGE,"E60"),sQuery(id+"F0.wireOp",EDGE,"E61"),sQuery(id+"F0.wireOp",EDGE,"E62"),sQuery(id+"F0.wireOp",EDGE,"E63"),sQuery(id+"F0.wireOp",EDGE,"E64"),sQuery(id+"F0.wireOp",EDGE,"E65"),sQuery(id+"F0.wireOp",EDGE,"E66"),sQuery(id+"F0.wireOp",EDGE,"E67"),sQuery(id+"F0.wireOp",EDGE,"E68"),sQuery(id+"F0.wireOp",EDGE,"E69"),sQuery(id+"F0.wireOp",EDGE,"E70"),sQuery(id+"F0.wireOp",EDGE,"E71"),sQuery(id+"F0.wireOp",EDGE,"E72"),sQuery(id+"F0.wireOp",EDGE,"E73"),sQuery(id+"F0.wireOp",EDGE,"E74"),sQuery(id+"F0.wireOp",EDGE,"E75"),sQuery(id+"F0.wireOp",EDGE,"E76"),sQuery(id+"F0.wireOp",EDGE,"E77"),sQuery(id+"F0.wireOp",EDGE,"E78"),sQuery(id+"F0.wireOp",EDGE,"E79"),sQuery(id+"F0.wireOp",EDGE,"E80"),sQuery(id+"F0.wireOp",EDGE,"E81"),sQuery(id+"F0.wireOp",EDGE,"E82"),sQuery(id+"F0.wireOp",EDGE,"E83"),sQuery(id+"F0.wireOp",EDGE,"E84"),sQuery(id+"F0.wireOp",EDGE,"E85"),sQuery(id+"F0.wireOp",EDGE,"E86"),sQuery(id+"F0.wireOp",EDGE,"E87"),sQuery(id+"F0.wireOp",EDGE,"E88"),sQuery(id+"F0.wireOp",EDGE,"E89"),sQuery(id+"F0.wireOp",EDGE,"E90"),sQuery(id+"F0.wireOp",EDGE,"E91"),sQuery(id+"F0.wireOp",EDGE,"E92"),sQuery(id+"F0.wireOp",EDGE,"E93"),sQuery(id+"F0.wireOp",EDGE,"E94"),sQuery(id+"F0.wireOp",EDGE,"E95"),sQuery(id+"F0.wireOp",EDGE,"E96"),sQuery(id+"F0.wireOp",EDGE,"E97"),sQuery(id+"F0.wireOp",EDGE,"E98"),sQuery(id+"F0.wireOp",EDGE,"E99"),sQuery(id+"F0.wireOp",EDGE,"E100"),sQuery(id+"F0.wireOp",EDGE,"E101"),sQuery(id+"F0.wireOp",EDGE,"E102"),sQuery(id+"F0.wireOp",EDGE,"E103"),sQuery(id+"F0.wireOp",EDGE,"E104"),sQuery(id+"F0.wireOp",EDGE,"E105"),sQuery(id+"F0.wireOp",EDGE,"E106"),sQuery(id+"F0.wireOp",EDGE,"E107"),sQuery(id+"F0.wireOp",EDGE,"E108"),sQuery(id+"F0.wireOp",EDGE,"E109"),sQuery(id+"F0.wireOp",EDGE,"E110"),sQuery(id+"F0.wireOp",EDGE,"E111"),sQuery(id+"F0.wireOp",EDGE,"E112"),sQuery(id+"F0.wireOp",EDGE,"E113"),sQuery(id+"F0.wireOp",EDGE,"E114"),sQuery(id+"F0.wireOp",EDGE,"E115")])],"isStart":false})]});
            var Q13;
            Q13=makeQuery(id+"F6.opFillet","BLEND_EDGE",EDGE,{"blendedFrom":[makeQuery(id+"F5.boolean.opBoolean","COPY",EDGE,{"derivedFrom":makeQuery(id+"F5.opExtrude","CAP_EDGE",EDGE,{"disambiguationData":[OSD([sQuery(id+"F4.wireOp",EDGE,"E757.3.1.0")])],"isStart":false})}),makeQuery(id+"F1.opExtrude","CAP_FACE",FACE,{"disambiguationData":[OSD([sQuery(id+"F0.wireOp",EDGE,"E0"),sQuery(id+"F0.wireOp",EDGE,"E1"),sQuery(id+"F0.wireOp",EDGE,"E2"),sQuery(id+"F0.wireOp",EDGE,"E3"),sQuery(id+"F0.wireOp",EDGE,"E4"),sQuery(id+"F0.wireOp",EDGE,"E5"),sQuery(id+"F0.wireOp",EDGE,"E6"),sQuery(id+"F0.wireOp",EDGE,"E7"),sQuery(id+"F0.wireOp",EDGE,"E8"),sQuery(id+"F0.wireOp",EDGE,"E9"),sQuery(id+"F0.wireOp",EDGE,"E10"),sQuery(id+"F0.wireOp",EDGE,"E11"),sQuery(id+"F0.wireOp",EDGE,"E12"),sQuery(id+"F0.wireOp",EDGE,"E13"),sQuery(id+"F0.wireOp",EDGE,"E14"),sQuery(id+"F0.wireOp",EDGE,"E15"),sQuery(id+"F0.wireOp",EDGE,"E16"),sQuery(id+"F0.wireOp",EDGE,"E17"),sQuery(id+"F0.wireOp",EDGE,"E18"),sQuery(id+"F0.wireOp",EDGE,"E19"),sQuery(id+"F0.wireOp",EDGE,"E20"),sQuery(id+"F0.wireOp",EDGE,"E21"),sQuery(id+"F0.wireOp",EDGE,"E22"),sQuery(id+"F0.wireOp",EDGE,"E23"),sQuery(id+"F0.wireOp",EDGE,"E24"),sQuery(id+"F0.wireOp",EDGE,"E25"),sQuery(id+"F0.wireOp",EDGE,"E26"),sQuery(id+"F0.wireOp",EDGE,"E27"),sQuery(id+"F0.wireOp",EDGE,"E28"),sQuery(id+"F0.wireOp",EDGE,"E29"),sQuery(id+"F0.wireOp",EDGE,"E30"),sQuery(id+"F0.wireOp",EDGE,"E31"),sQuery(id+"F0.wireOp",EDGE,"E32"),sQuery(id+"F0.wireOp",EDGE,"E33"),sQuery(id+"F0.wireOp",EDGE,"E34"),sQuery(id+"F0.wireOp",EDGE,"E35"),sQuery(id+"F0.wireOp",EDGE,"E36"),sQuery(id+"F0.wireOp",EDGE,"E37"),sQuery(id+"F0.wireOp",EDGE,"E38"),sQuery(id+"F0.wireOp",EDGE,"E39"),sQuery(id+"F0.wireOp",EDGE,"E40"),sQuery(id+"F0.wireOp",EDGE,"E41"),sQuery(id+"F0.wireOp",EDGE,"E42"),sQuery(id+"F0.wireOp",EDGE,"E43"),sQuery(id+"F0.wireOp",EDGE,"E44"),sQuery(id+"F0.wireOp",EDGE,"E45"),sQuery(id+"F0.wireOp",EDGE,"E46"),sQuery(id+"F0.wireOp",EDGE,"E47"),sQuery(id+"F0.wireOp",EDGE,"E48"),sQuery(id+"F0.wireOp",EDGE,"E49"),sQuery(id+"F0.wireOp",EDGE,"E50"),sQuery(id+"F0.wireOp",EDGE,"E51"),sQuery(id+"F0.wireOp",EDGE,"E52"),sQuery(id+"F0.wireOp",EDGE,"E53"),sQuery(id+"F0.wireOp",EDGE,"E54"),sQuery(id+"F0.wireOp",EDGE,"E55"),sQuery(id+"F0.wireOp",EDGE,"E56"),sQuery(id+"F0.wireOp",EDGE,"E57"),sQuery(id+"F0.wireOp",EDGE,"E58"),sQuery(id+"F0.wireOp",EDGE,"E59"),sQuery(id+"F0.wireOp",EDGE,"E60"),sQuery(id+"F0.wireOp",EDGE,"E61"),sQuery(id+"F0.wireOp",EDGE,"E62"),sQuery(id+"F0.wireOp",EDGE,"E63"),sQuery(id+"F0.wireOp",EDGE,"E64"),sQuery(id+"F0.wireOp",EDGE,"E65"),sQuery(id+"F0.wireOp",EDGE,"E66"),sQuery(id+"F0.wireOp",EDGE,"E67"),sQuery(id+"F0.wireOp",EDGE,"E68"),sQuery(id+"F0.wireOp",EDGE,"E69"),sQuery(id+"F0.wireOp",EDGE,"E70"),sQuery(id+"F0.wireOp",EDGE,"E71"),sQuery(id+"F0.wireOp",EDGE,"E72"),sQuery(id+"F0.wireOp",EDGE,"E73"),sQuery(id+"F0.wireOp",EDGE,"E74"),sQuery(id+"F0.wireOp",EDGE,"E75"),sQuery(id+"F0.wireOp",EDGE,"E76"),sQuery(id+"F0.wireOp",EDGE,"E77"),sQuery(id+"F0.wireOp",EDGE,"E78"),sQuery(id+"F0.wireOp",EDGE,"E79"),sQuery(id+"F0.wireOp",EDGE,"E80"),sQuery(id+"F0.wireOp",EDGE,"E81"),sQuery(id+"F0.wireOp",EDGE,"E82"),sQuery(id+"F0.wireOp",EDGE,"E83"),sQuery(id+"F0.wireOp",EDGE,"E84"),sQuery(id+"F0.wireOp",EDGE,"E85"),sQuery(id+"F0.wireOp",EDGE,"E86"),sQuery(id+"F0.wireOp",EDGE,"E87"),sQuery(id+"F0.wireOp",EDGE,"E88"),sQuery(id+"F0.wireOp",EDGE,"E89"),sQuery(id+"F0.wireOp",EDGE,"E90"),sQuery(id+"F0.wireOp",EDGE,"E91"),sQuery(id+"F0.wireOp",EDGE,"E92"),sQuery(id+"F0.wireOp",EDGE,"E93"),sQuery(id+"F0.wireOp",EDGE,"E94"),sQuery(id+"F0.wireOp",EDGE,"E95"),sQuery(id+"F0.wireOp",EDGE,"E96"),sQuery(id+"F0.wireOp",EDGE,"E97"),sQuery(id+"F0.wireOp",EDGE,"E98"),sQuery(id+"F0.wireOp",EDGE,"E99"),sQuery(id+"F0.wireOp",EDGE,"E100"),sQuery(id+"F0.wireOp",EDGE,"E101"),sQuery(id+"F0.wireOp",EDGE,"E102"),sQuery(id+"F0.wireOp",EDGE,"E103"),sQuery(id+"F0.wireOp",EDGE,"E104"),sQuery(id+"F0.wireOp",EDGE,"E105"),sQuery(id+"F0.wireOp",EDGE,"E106"),sQuery(id+"F0.wireOp",EDGE,"E107"),sQuery(id+"F0.wireOp",EDGE,"E108"),sQuery(id+"F0.wireOp",EDGE,"E109"),sQuery(id+"F0.wireOp",EDGE,"E110"),sQuery(id+"F0.wireOp",EDGE,"E111"),sQuery(id+"F0.wireOp",EDGE,"E112"),sQuery(id+"F0.wireOp",EDGE,"E113"),sQuery(id+"F0.wireOp",EDGE,"E114"),sQuery(id+"F0.wireOp",EDGE,"E115")])],"isStart":false})],"blendedInto":[makeQuery(id+"F1.opExtrude","CAP_FACE",FACE,{"disambiguationData":[OSD([sQuery(id+"F0.wireOp",EDGE,"E0"),sQuery(id+"F0.wireOp",EDGE,"E1"),sQuery(id+"F0.wireOp",EDGE,"E2"),sQuery(id+"F0.wireOp",EDGE,"E3"),sQuery(id+"F0.wireOp",EDGE,"E4"),sQuery(id+"F0.wireOp",EDGE,"E5"),sQuery(id+"F0.wireOp",EDGE,"E6"),sQuery(id+"F0.wireOp",EDGE,"E7"),sQuery(id+"F0.wireOp",EDGE,"E8"),sQuery(id+"F0.wireOp",EDGE,"E9"),sQuery(id+"F0.wireOp",EDGE,"E10"),sQuery(id+"F0.wireOp",EDGE,"E11"),sQuery(id+"F0.wireOp",EDGE,"E12"),sQuery(id+"F0.wireOp",EDGE,"E13"),sQuery(id+"F0.wireOp",EDGE,"E14"),sQuery(id+"F0.wireOp",EDGE,"E15"),sQuery(id+"F0.wireOp",EDGE,"E16"),sQuery(id+"F0.wireOp",EDGE,"E17"),sQuery(id+"F0.wireOp",EDGE,"E18"),sQuery(id+"F0.wireOp",EDGE,"E19"),sQuery(id+"F0.wireOp",EDGE,"E20"),sQuery(id+"F0.wireOp",EDGE,"E21"),sQuery(id+"F0.wireOp",EDGE,"E22"),sQuery(id+"F0.wireOp",EDGE,"E23"),sQuery(id+"F0.wireOp",EDGE,"E24"),sQuery(id+"F0.wireOp",EDGE,"E25"),sQuery(id+"F0.wireOp",EDGE,"E26"),sQuery(id+"F0.wireOp",EDGE,"E27"),sQuery(id+"F0.wireOp",EDGE,"E28"),sQuery(id+"F0.wireOp",EDGE,"E29"),sQuery(id+"F0.wireOp",EDGE,"E30"),sQuery(id+"F0.wireOp",EDGE,"E31"),sQuery(id+"F0.wireOp",EDGE,"E32"),sQuery(id+"F0.wireOp",EDGE,"E33"),sQuery(id+"F0.wireOp",EDGE,"E34"),sQuery(id+"F0.wireOp",EDGE,"E35"),sQuery(id+"F0.wireOp",EDGE,"E36"),sQuery(id+"F0.wireOp",EDGE,"E37"),sQuery(id+"F0.wireOp",EDGE,"E38"),sQuery(id+"F0.wireOp",EDGE,"E39"),sQuery(id+"F0.wireOp",EDGE,"E40"),sQuery(id+"F0.wireOp",EDGE,"E41"),sQuery(id+"F0.wireOp",EDGE,"E42"),sQuery(id+"F0.wireOp",EDGE,"E43"),sQuery(id+"F0.wireOp",EDGE,"E44"),sQuery(id+"F0.wireOp",EDGE,"E45"),sQuery(id+"F0.wireOp",EDGE,"E46"),sQuery(id+"F0.wireOp",EDGE,"E47"),sQuery(id+"F0.wireOp",EDGE,"E48"),sQuery(id+"F0.wireOp",EDGE,"E49"),sQuery(id+"F0.wireOp",EDGE,"E50"),sQuery(id+"F0.wireOp",EDGE,"E51"),sQuery(id+"F0.wireOp",EDGE,"E52"),sQuery(id+"F0.wireOp",EDGE,"E53"),sQuery(id+"F0.wireOp",EDGE,"E54"),sQuery(id+"F0.wireOp",EDGE,"E55"),sQuery(id+"F0.wireOp",EDGE,"E56"),sQuery(id+"F0.wireOp",EDGE,"E57"),sQuery(id+"F0.wireOp",EDGE,"E58"),sQuery(id+"F0.wireOp",EDGE,"E59"),sQuery(id+"F0.wireOp",EDGE,"E60"),sQuery(id+"F0.wireOp",EDGE,"E61"),sQuery(id+"F0.wireOp",EDGE,"E62"),sQuery(id+"F0.wireOp",EDGE,"E63"),sQuery(id+"F0.wireOp",EDGE,"E64"),sQuery(id+"F0.wireOp",EDGE,"E65"),sQuery(id+"F0.wireOp",EDGE,"E66"),sQuery(id+"F0.wireOp",EDGE,"E67"),sQuery(id+"F0.wireOp",EDGE,"E68"),sQuery(id+"F0.wireOp",EDGE,"E69"),sQuery(id+"F0.wireOp",EDGE,"E70"),sQuery(id+"F0.wireOp",EDGE,"E71"),sQuery(id+"F0.wireOp",EDGE,"E72"),sQuery(id+"F0.wireOp",EDGE,"E73"),sQuery(id+"F0.wireOp",EDGE,"E74"),sQuery(id+"F0.wireOp",EDGE,"E75"),sQuery(id+"F0.wireOp",EDGE,"E76"),sQuery(id+"F0.wireOp",EDGE,"E77"),sQuery(id+"F0.wireOp",EDGE,"E78"),sQuery(id+"F0.wireOp",EDGE,"E79"),sQuery(id+"F0.wireOp",EDGE,"E80"),sQuery(id+"F0.wireOp",EDGE,"E81"),sQuery(id+"F0.wireOp",EDGE,"E82"),sQuery(id+"F0.wireOp",EDGE,"E83"),sQuery(id+"F0.wireOp",EDGE,"E84"),sQuery(id+"F0.wireOp",EDGE,"E85"),sQuery(id+"F0.wireOp",EDGE,"E86"),sQuery(id+"F0.wireOp",EDGE,"E87"),sQuery(id+"F0.wireOp",EDGE,"E88"),sQuery(id+"F0.wireOp",EDGE,"E89"),sQuery(id+"F0.wireOp",EDGE,"E90"),sQuery(id+"F0.wireOp",EDGE,"E91"),sQuery(id+"F0.wireOp",EDGE,"E92"),sQuery(id+"F0.wireOp",EDGE,"E93"),sQuery(id+"F0.wireOp",EDGE,"E94"),sQuery(id+"F0.wireOp",EDGE,"E95"),sQuery(id+"F0.wireOp",EDGE,"E96"),sQuery(id+"F0.wireOp",EDGE,"E97"),sQuery(id+"F0.wireOp",EDGE,"E98"),sQuery(id+"F0.wireOp",EDGE,"E99"),sQuery(id+"F0.wireOp",EDGE,"E100"),sQuery(id+"F0.wireOp",EDGE,"E101"),sQuery(id+"F0.wireOp",EDGE,"E102"),sQuery(id+"F0.wireOp",EDGE,"E103"),sQuery(id+"F0.wireOp",EDGE,"E104"),sQuery(id+"F0.wireOp",EDGE,"E105"),sQuery(id+"F0.wireOp",EDGE,"E106"),sQuery(id+"F0.wireOp",EDGE,"E107"),sQuery(id+"F0.wireOp",EDGE,"E108"),sQuery(id+"F0.wireOp",EDGE,"E109"),sQuery(id+"F0.wireOp",EDGE,"E110"),sQuery(id+"F0.wireOp",EDGE,"E111"),sQuery(id+"F0.wireOp",EDGE,"E112"),sQuery(id+"F0.wireOp",EDGE,"E113"),sQuery(id+"F0.wireOp",EDGE,"E114"),sQuery(id+"F0.wireOp",EDGE,"E115")])],"isStart":false})]});
            var Q14;
            Q14=makeQuery(id+"F6.opFillet","BLEND_EDGE",EDGE,{"blendedFrom":[makeQuery(id+"F5.boolean.opBoolean","COPY",EDGE,{"derivedFrom":makeQuery(id+"F5.opExtrude","CAP_EDGE",EDGE,{"disambiguationData":[OSD([sQuery(id+"F4.wireOp",EDGE,"E757.3.0.0")])],"isStart":false})}),makeQuery(id+"F1.opExtrude","CAP_FACE",FACE,{"disambiguationData":[OSD([sQuery(id+"F0.wireOp",EDGE,"E0"),sQuery(id+"F0.wireOp",EDGE,"E1"),sQuery(id+"F0.wireOp",EDGE,"E2"),sQuery(id+"F0.wireOp",EDGE,"E3"),sQuery(id+"F0.wireOp",EDGE,"E4"),sQuery(id+"F0.wireOp",EDGE,"E5"),sQuery(id+"F0.wireOp",EDGE,"E6"),sQuery(id+"F0.wireOp",EDGE,"E7"),sQuery(id+"F0.wireOp",EDGE,"E8"),sQuery(id+"F0.wireOp",EDGE,"E9"),sQuery(id+"F0.wireOp",EDGE,"E10"),sQuery(id+"F0.wireOp",EDGE,"E11"),sQuery(id+"F0.wireOp",EDGE,"E12"),sQuery(id+"F0.wireOp",EDGE,"E13"),sQuery(id+"F0.wireOp",EDGE,"E14"),sQuery(id+"F0.wireOp",EDGE,"E15"),sQuery(id+"F0.wireOp",EDGE,"E16"),sQuery(id+"F0.wireOp",EDGE,"E17"),sQuery(id+"F0.wireOp",EDGE,"E18"),sQuery(id+"F0.wireOp",EDGE,"E19"),sQuery(id+"F0.wireOp",EDGE,"E20"),sQuery(id+"F0.wireOp",EDGE,"E21"),sQuery(id+"F0.wireOp",EDGE,"E22"),sQuery(id+"F0.wireOp",EDGE,"E23"),sQuery(id+"F0.wireOp",EDGE,"E24"),sQuery(id+"F0.wireOp",EDGE,"E25"),sQuery(id+"F0.wireOp",EDGE,"E26"),sQuery(id+"F0.wireOp",EDGE,"E27"),sQuery(id+"F0.wireOp",EDGE,"E28"),sQuery(id+"F0.wireOp",EDGE,"E29"),sQuery(id+"F0.wireOp",EDGE,"E30"),sQuery(id+"F0.wireOp",EDGE,"E31"),sQuery(id+"F0.wireOp",EDGE,"E32"),sQuery(id+"F0.wireOp",EDGE,"E33"),sQuery(id+"F0.wireOp",EDGE,"E34"),sQuery(id+"F0.wireOp",EDGE,"E35"),sQuery(id+"F0.wireOp",EDGE,"E36"),sQuery(id+"F0.wireOp",EDGE,"E37"),sQuery(id+"F0.wireOp",EDGE,"E38"),sQuery(id+"F0.wireOp",EDGE,"E39"),sQuery(id+"F0.wireOp",EDGE,"E40"),sQuery(id+"F0.wireOp",EDGE,"E41"),sQuery(id+"F0.wireOp",EDGE,"E42"),sQuery(id+"F0.wireOp",EDGE,"E43"),sQuery(id+"F0.wireOp",EDGE,"E44"),sQuery(id+"F0.wireOp",EDGE,"E45"),sQuery(id+"F0.wireOp",EDGE,"E46"),sQuery(id+"F0.wireOp",EDGE,"E47"),sQuery(id+"F0.wireOp",EDGE,"E48"),sQuery(id+"F0.wireOp",EDGE,"E49"),sQuery(id+"F0.wireOp",EDGE,"E50"),sQuery(id+"F0.wireOp",EDGE,"E51"),sQuery(id+"F0.wireOp",EDGE,"E52"),sQuery(id+"F0.wireOp",EDGE,"E53"),sQuery(id+"F0.wireOp",EDGE,"E54"),sQuery(id+"F0.wireOp",EDGE,"E55"),sQuery(id+"F0.wireOp",EDGE,"E56"),sQuery(id+"F0.wireOp",EDGE,"E57"),sQuery(id+"F0.wireOp",EDGE,"E58"),sQuery(id+"F0.wireOp",EDGE,"E59"),sQuery(id+"F0.wireOp",EDGE,"E60"),sQuery(id+"F0.wireOp",EDGE,"E61"),sQuery(id+"F0.wireOp",EDGE,"E62"),sQuery(id+"F0.wireOp",EDGE,"E63"),sQuery(id+"F0.wireOp",EDGE,"E64"),sQuery(id+"F0.wireOp",EDGE,"E65"),sQuery(id+"F0.wireOp",EDGE,"E66"),sQuery(id+"F0.wireOp",EDGE,"E67"),sQuery(id+"F0.wireOp",EDGE,"E68"),sQuery(id+"F0.wireOp",EDGE,"E69"),sQuery(id+"F0.wireOp",EDGE,"E70"),sQuery(id+"F0.wireOp",EDGE,"E71"),sQuery(id+"F0.wireOp",EDGE,"E72"),sQuery(id+"F0.wireOp",EDGE,"E73"),sQuery(id+"F0.wireOp",EDGE,"E74"),sQuery(id+"F0.wireOp",EDGE,"E75"),sQuery(id+"F0.wireOp",EDGE,"E76"),sQuery(id+"F0.wireOp",EDGE,"E77"),sQuery(id+"F0.wireOp",EDGE,"E78"),sQuery(id+"F0.wireOp",EDGE,"E79"),sQuery(id+"F0.wireOp",EDGE,"E80"),sQuery(id+"F0.wireOp",EDGE,"E81"),sQuery(id+"F0.wireOp",EDGE,"E82"),sQuery(id+"F0.wireOp",EDGE,"E83"),sQuery(id+"F0.wireOp",EDGE,"E84"),sQuery(id+"F0.wireOp",EDGE,"E85"),sQuery(id+"F0.wireOp",EDGE,"E86"),sQuery(id+"F0.wireOp",EDGE,"E87"),sQuery(id+"F0.wireOp",EDGE,"E88"),sQuery(id+"F0.wireOp",EDGE,"E89"),sQuery(id+"F0.wireOp",EDGE,"E90"),sQuery(id+"F0.wireOp",EDGE,"E91"),sQuery(id+"F0.wireOp",EDGE,"E92"),sQuery(id+"F0.wireOp",EDGE,"E93"),sQuery(id+"F0.wireOp",EDGE,"E94"),sQuery(id+"F0.wireOp",EDGE,"E95"),sQuery(id+"F0.wireOp",EDGE,"E96"),sQuery(id+"F0.wireOp",EDGE,"E97"),sQuery(id+"F0.wireOp",EDGE,"E98"),sQuery(id+"F0.wireOp",EDGE,"E99"),sQuery(id+"F0.wireOp",EDGE,"E100"),sQuery(id+"F0.wireOp",EDGE,"E101"),sQuery(id+"F0.wireOp",EDGE,"E102"),sQuery(id+"F0.wireOp",EDGE,"E103"),sQuery(id+"F0.wireOp",EDGE,"E104"),sQuery(id+"F0.wireOp",EDGE,"E105"),sQuery(id+"F0.wireOp",EDGE,"E106"),sQuery(id+"F0.wireOp",EDGE,"E107"),sQuery(id+"F0.wireOp",EDGE,"E108"),sQuery(id+"F0.wireOp",EDGE,"E109"),sQuery(id+"F0.wireOp",EDGE,"E110"),sQuery(id+"F0.wireOp",EDGE,"E111"),sQuery(id+"F0.wireOp",EDGE,"E112"),sQuery(id+"F0.wireOp",EDGE,"E113"),sQuery(id+"F0.wireOp",EDGE,"E114"),sQuery(id+"F0.wireOp",EDGE,"E115")])],"isStart":false})],"blendedInto":[makeQuery(id+"F1.opExtrude","CAP_FACE",FACE,{"disambiguationData":[OSD([sQuery(id+"F0.wireOp",EDGE,"E0"),sQuery(id+"F0.wireOp",EDGE,"E1"),sQuery(id+"F0.wireOp",EDGE,"E2"),sQuery(id+"F0.wireOp",EDGE,"E3"),sQuery(id+"F0.wireOp",EDGE,"E4"),sQuery(id+"F0.wireOp",EDGE,"E5"),sQuery(id+"F0.wireOp",EDGE,"E6"),sQuery(id+"F0.wireOp",EDGE,"E7"),sQuery(id+"F0.wireOp",EDGE,"E8"),sQuery(id+"F0.wireOp",EDGE,"E9"),sQuery(id+"F0.wireOp",EDGE,"E10"),sQuery(id+"F0.wireOp",EDGE,"E11"),sQuery(id+"F0.wireOp",EDGE,"E12"),sQuery(id+"F0.wireOp",EDGE,"E13"),sQuery(id+"F0.wireOp",EDGE,"E14"),sQuery(id+"F0.wireOp",EDGE,"E15"),sQuery(id+"F0.wireOp",EDGE,"E16"),sQuery(id+"F0.wireOp",EDGE,"E17"),sQuery(id+"F0.wireOp",EDGE,"E18"),sQuery(id+"F0.wireOp",EDGE,"E19"),sQuery(id+"F0.wireOp",EDGE,"E20"),sQuery(id+"F0.wireOp",EDGE,"E21"),sQuery(id+"F0.wireOp",EDGE,"E22"),sQuery(id+"F0.wireOp",EDGE,"E23"),sQuery(id+"F0.wireOp",EDGE,"E24"),sQuery(id+"F0.wireOp",EDGE,"E25"),sQuery(id+"F0.wireOp",EDGE,"E26"),sQuery(id+"F0.wireOp",EDGE,"E27"),sQuery(id+"F0.wireOp",EDGE,"E28"),sQuery(id+"F0.wireOp",EDGE,"E29"),sQuery(id+"F0.wireOp",EDGE,"E30"),sQuery(id+"F0.wireOp",EDGE,"E31"),sQuery(id+"F0.wireOp",EDGE,"E32"),sQuery(id+"F0.wireOp",EDGE,"E33"),sQuery(id+"F0.wireOp",EDGE,"E34"),sQuery(id+"F0.wireOp",EDGE,"E35"),sQuery(id+"F0.wireOp",EDGE,"E36"),sQuery(id+"F0.wireOp",EDGE,"E37"),sQuery(id+"F0.wireOp",EDGE,"E38"),sQuery(id+"F0.wireOp",EDGE,"E39"),sQuery(id+"F0.wireOp",EDGE,"E40"),sQuery(id+"F0.wireOp",EDGE,"E41"),sQuery(id+"F0.wireOp",EDGE,"E42"),sQuery(id+"F0.wireOp",EDGE,"E43"),sQuery(id+"F0.wireOp",EDGE,"E44"),sQuery(id+"F0.wireOp",EDGE,"E45"),sQuery(id+"F0.wireOp",EDGE,"E46"),sQuery(id+"F0.wireOp",EDGE,"E47"),sQuery(id+"F0.wireOp",EDGE,"E48"),sQuery(id+"F0.wireOp",EDGE,"E49"),sQuery(id+"F0.wireOp",EDGE,"E50"),sQuery(id+"F0.wireOp",EDGE,"E51"),sQuery(id+"F0.wireOp",EDGE,"E52"),sQuery(id+"F0.wireOp",EDGE,"E53"),sQuery(id+"F0.wireOp",EDGE,"E54"),sQuery(id+"F0.wireOp",EDGE,"E55"),sQuery(id+"F0.wireOp",EDGE,"E56"),sQuery(id+"F0.wireOp",EDGE,"E57"),sQuery(id+"F0.wireOp",EDGE,"E58"),sQuery(id+"F0.wireOp",EDGE,"E59"),sQuery(id+"F0.wireOp",EDGE,"E60"),sQuery(id+"F0.wireOp",EDGE,"E61"),sQuery(id+"F0.wireOp",EDGE,"E62"),sQuery(id+"F0.wireOp",EDGE,"E63"),sQuery(id+"F0.wireOp",EDGE,"E64"),sQuery(id+"F0.wireOp",EDGE,"E65"),sQuery(id+"F0.wireOp",EDGE,"E66"),sQuery(id+"F0.wireOp",EDGE,"E67"),sQuery(id+"F0.wireOp",EDGE,"E68"),sQuery(id+"F0.wireOp",EDGE,"E69"),sQuery(id+"F0.wireOp",EDGE,"E70"),sQuery(id+"F0.wireOp",EDGE,"E71"),sQuery(id+"F0.wireOp",EDGE,"E72"),sQuery(id+"F0.wireOp",EDGE,"E73"),sQuery(id+"F0.wireOp",EDGE,"E74"),sQuery(id+"F0.wireOp",EDGE,"E75"),sQuery(id+"F0.wireOp",EDGE,"E76"),sQuery(id+"F0.wireOp",EDGE,"E77"),sQuery(id+"F0.wireOp",EDGE,"E78"),sQuery(id+"F0.wireOp",EDGE,"E79"),sQuery(id+"F0.wireOp",EDGE,"E80"),sQuery(id+"F0.wireOp",EDGE,"E81"),sQuery(id+"F0.wireOp",EDGE,"E82"),sQuery(id+"F0.wireOp",EDGE,"E83"),sQuery(id+"F0.wireOp",EDGE,"E84"),sQuery(id+"F0.wireOp",EDGE,"E85"),sQuery(id+"F0.wireOp",EDGE,"E86"),sQuery(id+"F0.wireOp",EDGE,"E87"),sQuery(id+"F0.wireOp",EDGE,"E88"),sQuery(id+"F0.wireOp",EDGE,"E89"),sQuery(id+"F0.wireOp",EDGE,"E90"),sQuery(id+"F0.wireOp",EDGE,"E91"),sQuery(id+"F0.wireOp",EDGE,"E92"),sQuery(id+"F0.wireOp",EDGE,"E93"),sQuery(id+"F0.wireOp",EDGE,"E94"),sQuery(id+"F0.wireOp",EDGE,"E95"),sQuery(id+"F0.wireOp",EDGE,"E96"),sQuery(id+"F0.wireOp",EDGE,"E97"),sQuery(id+"F0.wireOp",EDGE,"E98"),sQuery(id+"F0.wireOp",EDGE,"E99"),sQuery(id+"F0.wireOp",EDGE,"E100"),sQuery(id+"F0.wireOp",EDGE,"E101"),sQuery(id+"F0.wireOp",EDGE,"E102"),sQuery(id+"F0.wireOp",EDGE,"E103"),sQuery(id+"F0.wireOp",EDGE,"E104"),sQuery(id+"F0.wireOp",EDGE,"E105"),sQuery(id+"F0.wireOp",EDGE,"E106"),sQuery(id+"F0.wireOp",EDGE,"E107"),sQuery(id+"F0.wireOp",EDGE,"E108"),sQuery(id+"F0.wireOp",EDGE,"E109"),sQuery(id+"F0.wireOp",EDGE,"E110"),sQuery(id+"F0.wireOp",EDGE,"E111"),sQuery(id+"F0.wireOp",EDGE,"E112"),sQuery(id+"F0.wireOp",EDGE,"E113"),sQuery(id+"F0.wireOp",EDGE,"E114"),sQuery(id+"F0.wireOp",EDGE,"E115")])],"isStart":false})]});
            var Q15;
            Q15=makeQuery(id+"F6.opFillet","BLEND_EDGE",EDGE,{"blendedFrom":[makeQuery(id+"F5.boolean.opBoolean","COPY",EDGE,{"derivedFrom":makeQuery(id+"F5.opExtrude","CAP_EDGE",EDGE,{"disambiguationData":[OSD([sQuery(id+"F4.wireOp",EDGE,"E758.0.4.0")])],"isStart":false})}),makeQuery(id+"F1.opExtrude","CAP_FACE",FACE,{"disambiguationData":[OSD([sQuery(id+"F0.wireOp",EDGE,"E0"),sQuery(id+"F0.wireOp",EDGE,"E1"),sQuery(id+"F0.wireOp",EDGE,"E2"),sQuery(id+"F0.wireOp",EDGE,"E3"),sQuery(id+"F0.wireOp",EDGE,"E4"),sQuery(id+"F0.wireOp",EDGE,"E5"),sQuery(id+"F0.wireOp",EDGE,"E6"),sQuery(id+"F0.wireOp",EDGE,"E7"),sQuery(id+"F0.wireOp",EDGE,"E8"),sQuery(id+"F0.wireOp",EDGE,"E9"),sQuery(id+"F0.wireOp",EDGE,"E10"),sQuery(id+"F0.wireOp",EDGE,"E11"),sQuery(id+"F0.wireOp",EDGE,"E12"),sQuery(id+"F0.wireOp",EDGE,"E13"),sQuery(id+"F0.wireOp",EDGE,"E14"),sQuery(id+"F0.wireOp",EDGE,"E15"),sQuery(id+"F0.wireOp",EDGE,"E16"),sQuery(id+"F0.wireOp",EDGE,"E17"),sQuery(id+"F0.wireOp",EDGE,"E18"),sQuery(id+"F0.wireOp",EDGE,"E19"),sQuery(id+"F0.wireOp",EDGE,"E20"),sQuery(id+"F0.wireOp",EDGE,"E21"),sQuery(id+"F0.wireOp",EDGE,"E22"),sQuery(id+"F0.wireOp",EDGE,"E23"),sQuery(id+"F0.wireOp",EDGE,"E24"),sQuery(id+"F0.wireOp",EDGE,"E25"),sQuery(id+"F0.wireOp",EDGE,"E26"),sQuery(id+"F0.wireOp",EDGE,"E27"),sQuery(id+"F0.wireOp",EDGE,"E28"),sQuery(id+"F0.wireOp",EDGE,"E29"),sQuery(id+"F0.wireOp",EDGE,"E30"),sQuery(id+"F0.wireOp",EDGE,"E31"),sQuery(id+"F0.wireOp",EDGE,"E32"),sQuery(id+"F0.wireOp",EDGE,"E33"),sQuery(id+"F0.wireOp",EDGE,"E34"),sQuery(id+"F0.wireOp",EDGE,"E35"),sQuery(id+"F0.wireOp",EDGE,"E36"),sQuery(id+"F0.wireOp",EDGE,"E37"),sQuery(id+"F0.wireOp",EDGE,"E38"),sQuery(id+"F0.wireOp",EDGE,"E39"),sQuery(id+"F0.wireOp",EDGE,"E40"),sQuery(id+"F0.wireOp",EDGE,"E41"),sQuery(id+"F0.wireOp",EDGE,"E42"),sQuery(id+"F0.wireOp",EDGE,"E43"),sQuery(id+"F0.wireOp",EDGE,"E44"),sQuery(id+"F0.wireOp",EDGE,"E45"),sQuery(id+"F0.wireOp",EDGE,"E46"),sQuery(id+"F0.wireOp",EDGE,"E47"),sQuery(id+"F0.wireOp",EDGE,"E48"),sQuery(id+"F0.wireOp",EDGE,"E49"),sQuery(id+"F0.wireOp",EDGE,"E50"),sQuery(id+"F0.wireOp",EDGE,"E51"),sQuery(id+"F0.wireOp",EDGE,"E52"),sQuery(id+"F0.wireOp",EDGE,"E53"),sQuery(id+"F0.wireOp",EDGE,"E54"),sQuery(id+"F0.wireOp",EDGE,"E55"),sQuery(id+"F0.wireOp",EDGE,"E56"),sQuery(id+"F0.wireOp",EDGE,"E57"),sQuery(id+"F0.wireOp",EDGE,"E58"),sQuery(id+"F0.wireOp",EDGE,"E59"),sQuery(id+"F0.wireOp",EDGE,"E60"),sQuery(id+"F0.wireOp",EDGE,"E61"),sQuery(id+"F0.wireOp",EDGE,"E62"),sQuery(id+"F0.wireOp",EDGE,"E63"),sQuery(id+"F0.wireOp",EDGE,"E64"),sQuery(id+"F0.wireOp",EDGE,"E65"),sQuery(id+"F0.wireOp",EDGE,"E66"),sQuery(id+"F0.wireOp",EDGE,"E67"),sQuery(id+"F0.wireOp",EDGE,"E68"),sQuery(id+"F0.wireOp",EDGE,"E69"),sQuery(id+"F0.wireOp",EDGE,"E70"),sQuery(id+"F0.wireOp",EDGE,"E71"),sQuery(id+"F0.wireOp",EDGE,"E72"),sQuery(id+"F0.wireOp",EDGE,"E73"),sQuery(id+"F0.wireOp",EDGE,"E74"),sQuery(id+"F0.wireOp",EDGE,"E75"),sQuery(id+"F0.wireOp",EDGE,"E76"),sQuery(id+"F0.wireOp",EDGE,"E77"),sQuery(id+"F0.wireOp",EDGE,"E78"),sQuery(id+"F0.wireOp",EDGE,"E79"),sQuery(id+"F0.wireOp",EDGE,"E80"),sQuery(id+"F0.wireOp",EDGE,"E81"),sQuery(id+"F0.wireOp",EDGE,"E82"),sQuery(id+"F0.wireOp",EDGE,"E83"),sQuery(id+"F0.wireOp",EDGE,"E84"),sQuery(id+"F0.wireOp",EDGE,"E85"),sQuery(id+"F0.wireOp",EDGE,"E86"),sQuery(id+"F0.wireOp",EDGE,"E87"),sQuery(id+"F0.wireOp",EDGE,"E88"),sQuery(id+"F0.wireOp",EDGE,"E89"),sQuery(id+"F0.wireOp",EDGE,"E90"),sQuery(id+"F0.wireOp",EDGE,"E91"),sQuery(id+"F0.wireOp",EDGE,"E92"),sQuery(id+"F0.wireOp",EDGE,"E93"),sQuery(id+"F0.wireOp",EDGE,"E94"),sQuery(id+"F0.wireOp",EDGE,"E95"),sQuery(id+"F0.wireOp",EDGE,"E96"),sQuery(id+"F0.wireOp",EDGE,"E97"),sQuery(id+"F0.wireOp",EDGE,"E98"),sQuery(id+"F0.wireOp",EDGE,"E99"),sQuery(id+"F0.wireOp",EDGE,"E100"),sQuery(id+"F0.wireOp",EDGE,"E101"),sQuery(id+"F0.wireOp",EDGE,"E102"),sQuery(id+"F0.wireOp",EDGE,"E103"),sQuery(id+"F0.wireOp",EDGE,"E104"),sQuery(id+"F0.wireOp",EDGE,"E105"),sQuery(id+"F0.wireOp",EDGE,"E106"),sQuery(id+"F0.wireOp",EDGE,"E107"),sQuery(id+"F0.wireOp",EDGE,"E108"),sQuery(id+"F0.wireOp",EDGE,"E109"),sQuery(id+"F0.wireOp",EDGE,"E110"),sQuery(id+"F0.wireOp",EDGE,"E111"),sQuery(id+"F0.wireOp",EDGE,"E112"),sQuery(id+"F0.wireOp",EDGE,"E113"),sQuery(id+"F0.wireOp",EDGE,"E114"),sQuery(id+"F0.wireOp",EDGE,"E115")])],"isStart":false})],"blendedInto":[makeQuery(id+"F1.opExtrude","CAP_FACE",FACE,{"disambiguationData":[OSD([sQuery(id+"F0.wireOp",EDGE,"E0"),sQuery(id+"F0.wireOp",EDGE,"E1"),sQuery(id+"F0.wireOp",EDGE,"E2"),sQuery(id+"F0.wireOp",EDGE,"E3"),sQuery(id+"F0.wireOp",EDGE,"E4"),sQuery(id+"F0.wireOp",EDGE,"E5"),sQuery(id+"F0.wireOp",EDGE,"E6"),sQuery(id+"F0.wireOp",EDGE,"E7"),sQuery(id+"F0.wireOp",EDGE,"E8"),sQuery(id+"F0.wireOp",EDGE,"E9"),sQuery(id+"F0.wireOp",EDGE,"E10"),sQuery(id+"F0.wireOp",EDGE,"E11"),sQuery(id+"F0.wireOp",EDGE,"E12"),sQuery(id+"F0.wireOp",EDGE,"E13"),sQuery(id+"F0.wireOp",EDGE,"E14"),sQuery(id+"F0.wireOp",EDGE,"E15"),sQuery(id+"F0.wireOp",EDGE,"E16"),sQuery(id+"F0.wireOp",EDGE,"E17"),sQuery(id+"F0.wireOp",EDGE,"E18"),sQuery(id+"F0.wireOp",EDGE,"E19"),sQuery(id+"F0.wireOp",EDGE,"E20"),sQuery(id+"F0.wireOp",EDGE,"E21"),sQuery(id+"F0.wireOp",EDGE,"E22"),sQuery(id+"F0.wireOp",EDGE,"E23"),sQuery(id+"F0.wireOp",EDGE,"E24"),sQuery(id+"F0.wireOp",EDGE,"E25"),sQuery(id+"F0.wireOp",EDGE,"E26"),sQuery(id+"F0.wireOp",EDGE,"E27"),sQuery(id+"F0.wireOp",EDGE,"E28"),sQuery(id+"F0.wireOp",EDGE,"E29"),sQuery(id+"F0.wireOp",EDGE,"E30"),sQuery(id+"F0.wireOp",EDGE,"E31"),sQuery(id+"F0.wireOp",EDGE,"E32"),sQuery(id+"F0.wireOp",EDGE,"E33"),sQuery(id+"F0.wireOp",EDGE,"E34"),sQuery(id+"F0.wireOp",EDGE,"E35"),sQuery(id+"F0.wireOp",EDGE,"E36"),sQuery(id+"F0.wireOp",EDGE,"E37"),sQuery(id+"F0.wireOp",EDGE,"E38"),sQuery(id+"F0.wireOp",EDGE,"E39"),sQuery(id+"F0.wireOp",EDGE,"E40"),sQuery(id+"F0.wireOp",EDGE,"E41"),sQuery(id+"F0.wireOp",EDGE,"E42"),sQuery(id+"F0.wireOp",EDGE,"E43"),sQuery(id+"F0.wireOp",EDGE,"E44"),sQuery(id+"F0.wireOp",EDGE,"E45"),sQuery(id+"F0.wireOp",EDGE,"E46"),sQuery(id+"F0.wireOp",EDGE,"E47"),sQuery(id+"F0.wireOp",EDGE,"E48"),sQuery(id+"F0.wireOp",EDGE,"E49"),sQuery(id+"F0.wireOp",EDGE,"E50"),sQuery(id+"F0.wireOp",EDGE,"E51"),sQuery(id+"F0.wireOp",EDGE,"E52"),sQuery(id+"F0.wireOp",EDGE,"E53"),sQuery(id+"F0.wireOp",EDGE,"E54"),sQuery(id+"F0.wireOp",EDGE,"E55"),sQuery(id+"F0.wireOp",EDGE,"E56"),sQuery(id+"F0.wireOp",EDGE,"E57"),sQuery(id+"F0.wireOp",EDGE,"E58"),sQuery(id+"F0.wireOp",EDGE,"E59"),sQuery(id+"F0.wireOp",EDGE,"E60"),sQuery(id+"F0.wireOp",EDGE,"E61"),sQuery(id+"F0.wireOp",EDGE,"E62"),sQuery(id+"F0.wireOp",EDGE,"E63"),sQuery(id+"F0.wireOp",EDGE,"E64"),sQuery(id+"F0.wireOp",EDGE,"E65"),sQuery(id+"F0.wireOp",EDGE,"E66"),sQuery(id+"F0.wireOp",EDGE,"E67"),sQuery(id+"F0.wireOp",EDGE,"E68"),sQuery(id+"F0.wireOp",EDGE,"E69"),sQuery(id+"F0.wireOp",EDGE,"E70"),sQuery(id+"F0.wireOp",EDGE,"E71"),sQuery(id+"F0.wireOp",EDGE,"E72"),sQuery(id+"F0.wireOp",EDGE,"E73"),sQuery(id+"F0.wireOp",EDGE,"E74"),sQuery(id+"F0.wireOp",EDGE,"E75"),sQuery(id+"F0.wireOp",EDGE,"E76"),sQuery(id+"F0.wireOp",EDGE,"E77"),sQuery(id+"F0.wireOp",EDGE,"E78"),sQuery(id+"F0.wireOp",EDGE,"E79"),sQuery(id+"F0.wireOp",EDGE,"E80"),sQuery(id+"F0.wireOp",EDGE,"E81"),sQuery(id+"F0.wireOp",EDGE,"E82"),sQuery(id+"F0.wireOp",EDGE,"E83"),sQuery(id+"F0.wireOp",EDGE,"E84"),sQuery(id+"F0.wireOp",EDGE,"E85"),sQuery(id+"F0.wireOp",EDGE,"E86"),sQuery(id+"F0.wireOp",EDGE,"E87"),sQuery(id+"F0.wireOp",EDGE,"E88"),sQuery(id+"F0.wireOp",EDGE,"E89"),sQuery(id+"F0.wireOp",EDGE,"E90"),sQuery(id+"F0.wireOp",EDGE,"E91"),sQuery(id+"F0.wireOp",EDGE,"E92"),sQuery(id+"F0.wireOp",EDGE,"E93"),sQuery(id+"F0.wireOp",EDGE,"E94"),sQuery(id+"F0.wireOp",EDGE,"E95"),sQuery(id+"F0.wireOp",EDGE,"E96"),sQuery(id+"F0.wireOp",EDGE,"E97"),sQuery(id+"F0.wireOp",EDGE,"E98"),sQuery(id+"F0.wireOp",EDGE,"E99"),sQuery(id+"F0.wireOp",EDGE,"E100"),sQuery(id+"F0.wireOp",EDGE,"E101"),sQuery(id+"F0.wireOp",EDGE,"E102"),sQuery(id+"F0.wireOp",EDGE,"E103"),sQuery(id+"F0.wireOp",EDGE,"E104"),sQuery(id+"F0.wireOp",EDGE,"E105"),sQuery(id+"F0.wireOp",EDGE,"E106"),sQuery(id+"F0.wireOp",EDGE,"E107"),sQuery(id+"F0.wireOp",EDGE,"E108"),sQuery(id+"F0.wireOp",EDGE,"E109"),sQuery(id+"F0.wireOp",EDGE,"E110"),sQuery(id+"F0.wireOp",EDGE,"E111"),sQuery(id+"F0.wireOp",EDGE,"E112"),sQuery(id+"F0.wireOp",EDGE,"E113"),sQuery(id+"F0.wireOp",EDGE,"E114"),sQuery(id+"F0.wireOp",EDGE,"E115")])],"isStart":false})]});
            var Q16;
            Q16=makeQuery(id+"F6.opFillet","BLEND_EDGE",EDGE,{"blendedFrom":[makeQuery(id+"F5.boolean.opBoolean","COPY",EDGE,{"derivedFrom":makeQuery(id+"F5.opExtrude","CAP_EDGE",EDGE,{"disambiguationData":[OSD([sQuery(id+"F4.wireOp",EDGE,"E757.2.1.0")])],"isStart":false})}),makeQuery(id+"F1.opExtrude","CAP_FACE",FACE,{"disambiguationData":[OSD([sQuery(id+"F0.wireOp",EDGE,"E0"),sQuery(id+"F0.wireOp",EDGE,"E1"),sQuery(id+"F0.wireOp",EDGE,"E2"),sQuery(id+"F0.wireOp",EDGE,"E3"),sQuery(id+"F0.wireOp",EDGE,"E4"),sQuery(id+"F0.wireOp",EDGE,"E5"),sQuery(id+"F0.wireOp",EDGE,"E6"),sQuery(id+"F0.wireOp",EDGE,"E7"),sQuery(id+"F0.wireOp",EDGE,"E8"),sQuery(id+"F0.wireOp",EDGE,"E9"),sQuery(id+"F0.wireOp",EDGE,"E10"),sQuery(id+"F0.wireOp",EDGE,"E11"),sQuery(id+"F0.wireOp",EDGE,"E12"),sQuery(id+"F0.wireOp",EDGE,"E13"),sQuery(id+"F0.wireOp",EDGE,"E14"),sQuery(id+"F0.wireOp",EDGE,"E15"),sQuery(id+"F0.wireOp",EDGE,"E16"),sQuery(id+"F0.wireOp",EDGE,"E17"),sQuery(id+"F0.wireOp",EDGE,"E18"),sQuery(id+"F0.wireOp",EDGE,"E19"),sQuery(id+"F0.wireOp",EDGE,"E20"),sQuery(id+"F0.wireOp",EDGE,"E21"),sQuery(id+"F0.wireOp",EDGE,"E22"),sQuery(id+"F0.wireOp",EDGE,"E23"),sQuery(id+"F0.wireOp",EDGE,"E24"),sQuery(id+"F0.wireOp",EDGE,"E25"),sQuery(id+"F0.wireOp",EDGE,"E26"),sQuery(id+"F0.wireOp",EDGE,"E27"),sQuery(id+"F0.wireOp",EDGE,"E28"),sQuery(id+"F0.wireOp",EDGE,"E29"),sQuery(id+"F0.wireOp",EDGE,"E30"),sQuery(id+"F0.wireOp",EDGE,"E31"),sQuery(id+"F0.wireOp",EDGE,"E32"),sQuery(id+"F0.wireOp",EDGE,"E33"),sQuery(id+"F0.wireOp",EDGE,"E34"),sQuery(id+"F0.wireOp",EDGE,"E35"),sQuery(id+"F0.wireOp",EDGE,"E36"),sQuery(id+"F0.wireOp",EDGE,"E37"),sQuery(id+"F0.wireOp",EDGE,"E38"),sQuery(id+"F0.wireOp",EDGE,"E39"),sQuery(id+"F0.wireOp",EDGE,"E40"),sQuery(id+"F0.wireOp",EDGE,"E41"),sQuery(id+"F0.wireOp",EDGE,"E42"),sQuery(id+"F0.wireOp",EDGE,"E43"),sQuery(id+"F0.wireOp",EDGE,"E44"),sQuery(id+"F0.wireOp",EDGE,"E45"),sQuery(id+"F0.wireOp",EDGE,"E46"),sQuery(id+"F0.wireOp",EDGE,"E47"),sQuery(id+"F0.wireOp",EDGE,"E48"),sQuery(id+"F0.wireOp",EDGE,"E49"),sQuery(id+"F0.wireOp",EDGE,"E50"),sQuery(id+"F0.wireOp",EDGE,"E51"),sQuery(id+"F0.wireOp",EDGE,"E52"),sQuery(id+"F0.wireOp",EDGE,"E53"),sQuery(id+"F0.wireOp",EDGE,"E54"),sQuery(id+"F0.wireOp",EDGE,"E55"),sQuery(id+"F0.wireOp",EDGE,"E56"),sQuery(id+"F0.wireOp",EDGE,"E57"),sQuery(id+"F0.wireOp",EDGE,"E58"),sQuery(id+"F0.wireOp",EDGE,"E59"),sQuery(id+"F0.wireOp",EDGE,"E60"),sQuery(id+"F0.wireOp",EDGE,"E61"),sQuery(id+"F0.wireOp",EDGE,"E62"),sQuery(id+"F0.wireOp",EDGE,"E63"),sQuery(id+"F0.wireOp",EDGE,"E64"),sQuery(id+"F0.wireOp",EDGE,"E65"),sQuery(id+"F0.wireOp",EDGE,"E66"),sQuery(id+"F0.wireOp",EDGE,"E67"),sQuery(id+"F0.wireOp",EDGE,"E68"),sQuery(id+"F0.wireOp",EDGE,"E69"),sQuery(id+"F0.wireOp",EDGE,"E70"),sQuery(id+"F0.wireOp",EDGE,"E71"),sQuery(id+"F0.wireOp",EDGE,"E72"),sQuery(id+"F0.wireOp",EDGE,"E73"),sQuery(id+"F0.wireOp",EDGE,"E74"),sQuery(id+"F0.wireOp",EDGE,"E75"),sQuery(id+"F0.wireOp",EDGE,"E76"),sQuery(id+"F0.wireOp",EDGE,"E77"),sQuery(id+"F0.wireOp",EDGE,"E78"),sQuery(id+"F0.wireOp",EDGE,"E79"),sQuery(id+"F0.wireOp",EDGE,"E80"),sQuery(id+"F0.wireOp",EDGE,"E81"),sQuery(id+"F0.wireOp",EDGE,"E82"),sQuery(id+"F0.wireOp",EDGE,"E83"),sQuery(id+"F0.wireOp",EDGE,"E84"),sQuery(id+"F0.wireOp",EDGE,"E85"),sQuery(id+"F0.wireOp",EDGE,"E86"),sQuery(id+"F0.wireOp",EDGE,"E87"),sQuery(id+"F0.wireOp",EDGE,"E88"),sQuery(id+"F0.wireOp",EDGE,"E89"),sQuery(id+"F0.wireOp",EDGE,"E90"),sQuery(id+"F0.wireOp",EDGE,"E91"),sQuery(id+"F0.wireOp",EDGE,"E92"),sQuery(id+"F0.wireOp",EDGE,"E93"),sQuery(id+"F0.wireOp",EDGE,"E94"),sQuery(id+"F0.wireOp",EDGE,"E95"),sQuery(id+"F0.wireOp",EDGE,"E96"),sQuery(id+"F0.wireOp",EDGE,"E97"),sQuery(id+"F0.wireOp",EDGE,"E98"),sQuery(id+"F0.wireOp",EDGE,"E99"),sQuery(id+"F0.wireOp",EDGE,"E100"),sQuery(id+"F0.wireOp",EDGE,"E101"),sQuery(id+"F0.wireOp",EDGE,"E102"),sQuery(id+"F0.wireOp",EDGE,"E103"),sQuery(id+"F0.wireOp",EDGE,"E104"),sQuery(id+"F0.wireOp",EDGE,"E105"),sQuery(id+"F0.wireOp",EDGE,"E106"),sQuery(id+"F0.wireOp",EDGE,"E107"),sQuery(id+"F0.wireOp",EDGE,"E108"),sQuery(id+"F0.wireOp",EDGE,"E109"),sQuery(id+"F0.wireOp",EDGE,"E110"),sQuery(id+"F0.wireOp",EDGE,"E111"),sQuery(id+"F0.wireOp",EDGE,"E112"),sQuery(id+"F0.wireOp",EDGE,"E113"),sQuery(id+"F0.wireOp",EDGE,"E114"),sQuery(id+"F0.wireOp",EDGE,"E115")])],"isStart":false})],"blendedInto":[makeQuery(id+"F1.opExtrude","CAP_FACE",FACE,{"disambiguationData":[OSD([sQuery(id+"F0.wireOp",EDGE,"E0"),sQuery(id+"F0.wireOp",EDGE,"E1"),sQuery(id+"F0.wireOp",EDGE,"E2"),sQuery(id+"F0.wireOp",EDGE,"E3"),sQuery(id+"F0.wireOp",EDGE,"E4"),sQuery(id+"F0.wireOp",EDGE,"E5"),sQuery(id+"F0.wireOp",EDGE,"E6"),sQuery(id+"F0.wireOp",EDGE,"E7"),sQuery(id+"F0.wireOp",EDGE,"E8"),sQuery(id+"F0.wireOp",EDGE,"E9"),sQuery(id+"F0.wireOp",EDGE,"E10"),sQuery(id+"F0.wireOp",EDGE,"E11"),sQuery(id+"F0.wireOp",EDGE,"E12"),sQuery(id+"F0.wireOp",EDGE,"E13"),sQuery(id+"F0.wireOp",EDGE,"E14"),sQuery(id+"F0.wireOp",EDGE,"E15"),sQuery(id+"F0.wireOp",EDGE,"E16"),sQuery(id+"F0.wireOp",EDGE,"E17"),sQuery(id+"F0.wireOp",EDGE,"E18"),sQuery(id+"F0.wireOp",EDGE,"E19"),sQuery(id+"F0.wireOp",EDGE,"E20"),sQuery(id+"F0.wireOp",EDGE,"E21"),sQuery(id+"F0.wireOp",EDGE,"E22"),sQuery(id+"F0.wireOp",EDGE,"E23"),sQuery(id+"F0.wireOp",EDGE,"E24"),sQuery(id+"F0.wireOp",EDGE,"E25"),sQuery(id+"F0.wireOp",EDGE,"E26"),sQuery(id+"F0.wireOp",EDGE,"E27"),sQuery(id+"F0.wireOp",EDGE,"E28"),sQuery(id+"F0.wireOp",EDGE,"E29"),sQuery(id+"F0.wireOp",EDGE,"E30"),sQuery(id+"F0.wireOp",EDGE,"E31"),sQuery(id+"F0.wireOp",EDGE,"E32"),sQuery(id+"F0.wireOp",EDGE,"E33"),sQuery(id+"F0.wireOp",EDGE,"E34"),sQuery(id+"F0.wireOp",EDGE,"E35"),sQuery(id+"F0.wireOp",EDGE,"E36"),sQuery(id+"F0.wireOp",EDGE,"E37"),sQuery(id+"F0.wireOp",EDGE,"E38"),sQuery(id+"F0.wireOp",EDGE,"E39"),sQuery(id+"F0.wireOp",EDGE,"E40"),sQuery(id+"F0.wireOp",EDGE,"E41"),sQuery(id+"F0.wireOp",EDGE,"E42"),sQuery(id+"F0.wireOp",EDGE,"E43"),sQuery(id+"F0.wireOp",EDGE,"E44"),sQuery(id+"F0.wireOp",EDGE,"E45"),sQuery(id+"F0.wireOp",EDGE,"E46"),sQuery(id+"F0.wireOp",EDGE,"E47"),sQuery(id+"F0.wireOp",EDGE,"E48"),sQuery(id+"F0.wireOp",EDGE,"E49"),sQuery(id+"F0.wireOp",EDGE,"E50"),sQuery(id+"F0.wireOp",EDGE,"E51"),sQuery(id+"F0.wireOp",EDGE,"E52"),sQuery(id+"F0.wireOp",EDGE,"E53"),sQuery(id+"F0.wireOp",EDGE,"E54"),sQuery(id+"F0.wireOp",EDGE,"E55"),sQuery(id+"F0.wireOp",EDGE,"E56"),sQuery(id+"F0.wireOp",EDGE,"E57"),sQuery(id+"F0.wireOp",EDGE,"E58"),sQuery(id+"F0.wireOp",EDGE,"E59"),sQuery(id+"F0.wireOp",EDGE,"E60"),sQuery(id+"F0.wireOp",EDGE,"E61"),sQuery(id+"F0.wireOp",EDGE,"E62"),sQuery(id+"F0.wireOp",EDGE,"E63"),sQuery(id+"F0.wireOp",EDGE,"E64"),sQuery(id+"F0.wireOp",EDGE,"E65"),sQuery(id+"F0.wireOp",EDGE,"E66"),sQuery(id+"F0.wireOp",EDGE,"E67"),sQuery(id+"F0.wireOp",EDGE,"E68"),sQuery(id+"F0.wireOp",EDGE,"E69"),sQuery(id+"F0.wireOp",EDGE,"E70"),sQuery(id+"F0.wireOp",EDGE,"E71"),sQuery(id+"F0.wireOp",EDGE,"E72"),sQuery(id+"F0.wireOp",EDGE,"E73"),sQuery(id+"F0.wireOp",EDGE,"E74"),sQuery(id+"F0.wireOp",EDGE,"E75"),sQuery(id+"F0.wireOp",EDGE,"E76"),sQuery(id+"F0.wireOp",EDGE,"E77"),sQuery(id+"F0.wireOp",EDGE,"E78"),sQuery(id+"F0.wireOp",EDGE,"E79"),sQuery(id+"F0.wireOp",EDGE,"E80"),sQuery(id+"F0.wireOp",EDGE,"E81"),sQuery(id+"F0.wireOp",EDGE,"E82"),sQuery(id+"F0.wireOp",EDGE,"E83"),sQuery(id+"F0.wireOp",EDGE,"E84"),sQuery(id+"F0.wireOp",EDGE,"E85"),sQuery(id+"F0.wireOp",EDGE,"E86"),sQuery(id+"F0.wireOp",EDGE,"E87"),sQuery(id+"F0.wireOp",EDGE,"E88"),sQuery(id+"F0.wireOp",EDGE,"E89"),sQuery(id+"F0.wireOp",EDGE,"E90"),sQuery(id+"F0.wireOp",EDGE,"E91"),sQuery(id+"F0.wireOp",EDGE,"E92"),sQuery(id+"F0.wireOp",EDGE,"E93"),sQuery(id+"F0.wireOp",EDGE,"E94"),sQuery(id+"F0.wireOp",EDGE,"E95"),sQuery(id+"F0.wireOp",EDGE,"E96"),sQuery(id+"F0.wireOp",EDGE,"E97"),sQuery(id+"F0.wireOp",EDGE,"E98"),sQuery(id+"F0.wireOp",EDGE,"E99"),sQuery(id+"F0.wireOp",EDGE,"E100"),sQuery(id+"F0.wireOp",EDGE,"E101"),sQuery(id+"F0.wireOp",EDGE,"E102"),sQuery(id+"F0.wireOp",EDGE,"E103"),sQuery(id+"F0.wireOp",EDGE,"E104"),sQuery(id+"F0.wireOp",EDGE,"E105"),sQuery(id+"F0.wireOp",EDGE,"E106"),sQuery(id+"F0.wireOp",EDGE,"E107"),sQuery(id+"F0.wireOp",EDGE,"E108"),sQuery(id+"F0.wireOp",EDGE,"E109"),sQuery(id+"F0.wireOp",EDGE,"E110"),sQuery(id+"F0.wireOp",EDGE,"E111"),sQuery(id+"F0.wireOp",EDGE,"E112"),sQuery(id+"F0.wireOp",EDGE,"E113"),sQuery(id+"F0.wireOp",EDGE,"E114"),sQuery(id+"F0.wireOp",EDGE,"E115")])],"isStart":false})]});
            var Q17;
            Q17=makeQuery(id+"F6.opFillet","BLEND_EDGE",EDGE,{"blendedFrom":[makeQuery(id+"F5.boolean.opBoolean","COPY",EDGE,{"derivedFrom":makeQuery(id+"F5.opExtrude","CAP_EDGE",EDGE,{"disambiguationData":[OSD([sQuery(id+"F4.wireOp",EDGE,"E758.0.4.1")])],"isStart":false})}),makeQuery(id+"F1.opExtrude","CAP_FACE",FACE,{"disambiguationData":[OSD([sQuery(id+"F0.wireOp",EDGE,"E0"),sQuery(id+"F0.wireOp",EDGE,"E1"),sQuery(id+"F0.wireOp",EDGE,"E2"),sQuery(id+"F0.wireOp",EDGE,"E3"),sQuery(id+"F0.wireOp",EDGE,"E4"),sQuery(id+"F0.wireOp",EDGE,"E5"),sQuery(id+"F0.wireOp",EDGE,"E6"),sQuery(id+"F0.wireOp",EDGE,"E7"),sQuery(id+"F0.wireOp",EDGE,"E8"),sQuery(id+"F0.wireOp",EDGE,"E9"),sQuery(id+"F0.wireOp",EDGE,"E10"),sQuery(id+"F0.wireOp",EDGE,"E11"),sQuery(id+"F0.wireOp",EDGE,"E12"),sQuery(id+"F0.wireOp",EDGE,"E13"),sQuery(id+"F0.wireOp",EDGE,"E14"),sQuery(id+"F0.wireOp",EDGE,"E15"),sQuery(id+"F0.wireOp",EDGE,"E16"),sQuery(id+"F0.wireOp",EDGE,"E17"),sQuery(id+"F0.wireOp",EDGE,"E18"),sQuery(id+"F0.wireOp",EDGE,"E19"),sQuery(id+"F0.wireOp",EDGE,"E20"),sQuery(id+"F0.wireOp",EDGE,"E21"),sQuery(id+"F0.wireOp",EDGE,"E22"),sQuery(id+"F0.wireOp",EDGE,"E23"),sQuery(id+"F0.wireOp",EDGE,"E24"),sQuery(id+"F0.wireOp",EDGE,"E25"),sQuery(id+"F0.wireOp",EDGE,"E26"),sQuery(id+"F0.wireOp",EDGE,"E27"),sQuery(id+"F0.wireOp",EDGE,"E28"),sQuery(id+"F0.wireOp",EDGE,"E29"),sQuery(id+"F0.wireOp",EDGE,"E30"),sQuery(id+"F0.wireOp",EDGE,"E31"),sQuery(id+"F0.wireOp",EDGE,"E32"),sQuery(id+"F0.wireOp",EDGE,"E33"),sQuery(id+"F0.wireOp",EDGE,"E34"),sQuery(id+"F0.wireOp",EDGE,"E35"),sQuery(id+"F0.wireOp",EDGE,"E36"),sQuery(id+"F0.wireOp",EDGE,"E37"),sQuery(id+"F0.wireOp",EDGE,"E38"),sQuery(id+"F0.wireOp",EDGE,"E39"),sQuery(id+"F0.wireOp",EDGE,"E40"),sQuery(id+"F0.wireOp",EDGE,"E41"),sQuery(id+"F0.wireOp",EDGE,"E42"),sQuery(id+"F0.wireOp",EDGE,"E43"),sQuery(id+"F0.wireOp",EDGE,"E44"),sQuery(id+"F0.wireOp",EDGE,"E45"),sQuery(id+"F0.wireOp",EDGE,"E46"),sQuery(id+"F0.wireOp",EDGE,"E47"),sQuery(id+"F0.wireOp",EDGE,"E48"),sQuery(id+"F0.wireOp",EDGE,"E49"),sQuery(id+"F0.wireOp",EDGE,"E50"),sQuery(id+"F0.wireOp",EDGE,"E51"),sQuery(id+"F0.wireOp",EDGE,"E52"),sQuery(id+"F0.wireOp",EDGE,"E53"),sQuery(id+"F0.wireOp",EDGE,"E54"),sQuery(id+"F0.wireOp",EDGE,"E55"),sQuery(id+"F0.wireOp",EDGE,"E56"),sQuery(id+"F0.wireOp",EDGE,"E57"),sQuery(id+"F0.wireOp",EDGE,"E58"),sQuery(id+"F0.wireOp",EDGE,"E59"),sQuery(id+"F0.wireOp",EDGE,"E60"),sQuery(id+"F0.wireOp",EDGE,"E61"),sQuery(id+"F0.wireOp",EDGE,"E62"),sQuery(id+"F0.wireOp",EDGE,"E63"),sQuery(id+"F0.wireOp",EDGE,"E64"),sQuery(id+"F0.wireOp",EDGE,"E65"),sQuery(id+"F0.wireOp",EDGE,"E66"),sQuery(id+"F0.wireOp",EDGE,"E67"),sQuery(id+"F0.wireOp",EDGE,"E68"),sQuery(id+"F0.wireOp",EDGE,"E69"),sQuery(id+"F0.wireOp",EDGE,"E70"),sQuery(id+"F0.wireOp",EDGE,"E71"),sQuery(id+"F0.wireOp",EDGE,"E72"),sQuery(id+"F0.wireOp",EDGE,"E73"),sQuery(id+"F0.wireOp",EDGE,"E74"),sQuery(id+"F0.wireOp",EDGE,"E75"),sQuery(id+"F0.wireOp",EDGE,"E76"),sQuery(id+"F0.wireOp",EDGE,"E77"),sQuery(id+"F0.wireOp",EDGE,"E78"),sQuery(id+"F0.wireOp",EDGE,"E79"),sQuery(id+"F0.wireOp",EDGE,"E80"),sQuery(id+"F0.wireOp",EDGE,"E81"),sQuery(id+"F0.wireOp",EDGE,"E82"),sQuery(id+"F0.wireOp",EDGE,"E83"),sQuery(id+"F0.wireOp",EDGE,"E84"),sQuery(id+"F0.wireOp",EDGE,"E85"),sQuery(id+"F0.wireOp",EDGE,"E86"),sQuery(id+"F0.wireOp",EDGE,"E87"),sQuery(id+"F0.wireOp",EDGE,"E88"),sQuery(id+"F0.wireOp",EDGE,"E89"),sQuery(id+"F0.wireOp",EDGE,"E90"),sQuery(id+"F0.wireOp",EDGE,"E91"),sQuery(id+"F0.wireOp",EDGE,"E92"),sQuery(id+"F0.wireOp",EDGE,"E93"),sQuery(id+"F0.wireOp",EDGE,"E94"),sQuery(id+"F0.wireOp",EDGE,"E95"),sQuery(id+"F0.wireOp",EDGE,"E96"),sQuery(id+"F0.wireOp",EDGE,"E97"),sQuery(id+"F0.wireOp",EDGE,"E98"),sQuery(id+"F0.wireOp",EDGE,"E99"),sQuery(id+"F0.wireOp",EDGE,"E100"),sQuery(id+"F0.wireOp",EDGE,"E101"),sQuery(id+"F0.wireOp",EDGE,"E102"),sQuery(id+"F0.wireOp",EDGE,"E103"),sQuery(id+"F0.wireOp",EDGE,"E104"),sQuery(id+"F0.wireOp",EDGE,"E105"),sQuery(id+"F0.wireOp",EDGE,"E106"),sQuery(id+"F0.wireOp",EDGE,"E107"),sQuery(id+"F0.wireOp",EDGE,"E108"),sQuery(id+"F0.wireOp",EDGE,"E109"),sQuery(id+"F0.wireOp",EDGE,"E110"),sQuery(id+"F0.wireOp",EDGE,"E111"),sQuery(id+"F0.wireOp",EDGE,"E112"),sQuery(id+"F0.wireOp",EDGE,"E113"),sQuery(id+"F0.wireOp",EDGE,"E114"),sQuery(id+"F0.wireOp",EDGE,"E115")])],"isStart":false})],"blendedInto":[makeQuery(id+"F1.opExtrude","CAP_FACE",FACE,{"disambiguationData":[OSD([sQuery(id+"F0.wireOp",EDGE,"E0"),sQuery(id+"F0.wireOp",EDGE,"E1"),sQuery(id+"F0.wireOp",EDGE,"E2"),sQuery(id+"F0.wireOp",EDGE,"E3"),sQuery(id+"F0.wireOp",EDGE,"E4"),sQuery(id+"F0.wireOp",EDGE,"E5"),sQuery(id+"F0.wireOp",EDGE,"E6"),sQuery(id+"F0.wireOp",EDGE,"E7"),sQuery(id+"F0.wireOp",EDGE,"E8"),sQuery(id+"F0.wireOp",EDGE,"E9"),sQuery(id+"F0.wireOp",EDGE,"E10"),sQuery(id+"F0.wireOp",EDGE,"E11"),sQuery(id+"F0.wireOp",EDGE,"E12"),sQuery(id+"F0.wireOp",EDGE,"E13"),sQuery(id+"F0.wireOp",EDGE,"E14"),sQuery(id+"F0.wireOp",EDGE,"E15"),sQuery(id+"F0.wireOp",EDGE,"E16"),sQuery(id+"F0.wireOp",EDGE,"E17"),sQuery(id+"F0.wireOp",EDGE,"E18"),sQuery(id+"F0.wireOp",EDGE,"E19"),sQuery(id+"F0.wireOp",EDGE,"E20"),sQuery(id+"F0.wireOp",EDGE,"E21"),sQuery(id+"F0.wireOp",EDGE,"E22"),sQuery(id+"F0.wireOp",EDGE,"E23"),sQuery(id+"F0.wireOp",EDGE,"E24"),sQuery(id+"F0.wireOp",EDGE,"E25"),sQuery(id+"F0.wireOp",EDGE,"E26"),sQuery(id+"F0.wireOp",EDGE,"E27"),sQuery(id+"F0.wireOp",EDGE,"E28"),sQuery(id+"F0.wireOp",EDGE,"E29"),sQuery(id+"F0.wireOp",EDGE,"E30"),sQuery(id+"F0.wireOp",EDGE,"E31"),sQuery(id+"F0.wireOp",EDGE,"E32"),sQuery(id+"F0.wireOp",EDGE,"E33"),sQuery(id+"F0.wireOp",EDGE,"E34"),sQuery(id+"F0.wireOp",EDGE,"E35"),sQuery(id+"F0.wireOp",EDGE,"E36"),sQuery(id+"F0.wireOp",EDGE,"E37"),sQuery(id+"F0.wireOp",EDGE,"E38"),sQuery(id+"F0.wireOp",EDGE,"E39"),sQuery(id+"F0.wireOp",EDGE,"E40"),sQuery(id+"F0.wireOp",EDGE,"E41"),sQuery(id+"F0.wireOp",EDGE,"E42"),sQuery(id+"F0.wireOp",EDGE,"E43"),sQuery(id+"F0.wireOp",EDGE,"E44"),sQuery(id+"F0.wireOp",EDGE,"E45"),sQuery(id+"F0.wireOp",EDGE,"E46"),sQuery(id+"F0.wireOp",EDGE,"E47"),sQuery(id+"F0.wireOp",EDGE,"E48"),sQuery(id+"F0.wireOp",EDGE,"E49"),sQuery(id+"F0.wireOp",EDGE,"E50"),sQuery(id+"F0.wireOp",EDGE,"E51"),sQuery(id+"F0.wireOp",EDGE,"E52"),sQuery(id+"F0.wireOp",EDGE,"E53"),sQuery(id+"F0.wireOp",EDGE,"E54"),sQuery(id+"F0.wireOp",EDGE,"E55"),sQuery(id+"F0.wireOp",EDGE,"E56"),sQuery(id+"F0.wireOp",EDGE,"E57"),sQuery(id+"F0.wireOp",EDGE,"E58"),sQuery(id+"F0.wireOp",EDGE,"E59"),sQuery(id+"F0.wireOp",EDGE,"E60"),sQuery(id+"F0.wireOp",EDGE,"E61"),sQuery(id+"F0.wireOp",EDGE,"E62"),sQuery(id+"F0.wireOp",EDGE,"E63"),sQuery(id+"F0.wireOp",EDGE,"E64"),sQuery(id+"F0.wireOp",EDGE,"E65"),sQuery(id+"F0.wireOp",EDGE,"E66"),sQuery(id+"F0.wireOp",EDGE,"E67"),sQuery(id+"F0.wireOp",EDGE,"E68"),sQuery(id+"F0.wireOp",EDGE,"E69"),sQuery(id+"F0.wireOp",EDGE,"E70"),sQuery(id+"F0.wireOp",EDGE,"E71"),sQuery(id+"F0.wireOp",EDGE,"E72"),sQuery(id+"F0.wireOp",EDGE,"E73"),sQuery(id+"F0.wireOp",EDGE,"E74"),sQuery(id+"F0.wireOp",EDGE,"E75"),sQuery(id+"F0.wireOp",EDGE,"E76"),sQuery(id+"F0.wireOp",EDGE,"E77"),sQuery(id+"F0.wireOp",EDGE,"E78"),sQuery(id+"F0.wireOp",EDGE,"E79"),sQuery(id+"F0.wireOp",EDGE,"E80"),sQuery(id+"F0.wireOp",EDGE,"E81"),sQuery(id+"F0.wireOp",EDGE,"E82"),sQuery(id+"F0.wireOp",EDGE,"E83"),sQuery(id+"F0.wireOp",EDGE,"E84"),sQuery(id+"F0.wireOp",EDGE,"E85"),sQuery(id+"F0.wireOp",EDGE,"E86"),sQuery(id+"F0.wireOp",EDGE,"E87"),sQuery(id+"F0.wireOp",EDGE,"E88"),sQuery(id+"F0.wireOp",EDGE,"E89"),sQuery(id+"F0.wireOp",EDGE,"E90"),sQuery(id+"F0.wireOp",EDGE,"E91"),sQuery(id+"F0.wireOp",EDGE,"E92"),sQuery(id+"F0.wireOp",EDGE,"E93"),sQuery(id+"F0.wireOp",EDGE,"E94"),sQuery(id+"F0.wireOp",EDGE,"E95"),sQuery(id+"F0.wireOp",EDGE,"E96"),sQuery(id+"F0.wireOp",EDGE,"E97"),sQuery(id+"F0.wireOp",EDGE,"E98"),sQuery(id+"F0.wireOp",EDGE,"E99"),sQuery(id+"F0.wireOp",EDGE,"E100"),sQuery(id+"F0.wireOp",EDGE,"E101"),sQuery(id+"F0.wireOp",EDGE,"E102"),sQuery(id+"F0.wireOp",EDGE,"E103"),sQuery(id+"F0.wireOp",EDGE,"E104"),sQuery(id+"F0.wireOp",EDGE,"E105"),sQuery(id+"F0.wireOp",EDGE,"E106"),sQuery(id+"F0.wireOp",EDGE,"E107"),sQuery(id+"F0.wireOp",EDGE,"E108"),sQuery(id+"F0.wireOp",EDGE,"E109"),sQuery(id+"F0.wireOp",EDGE,"E110"),sQuery(id+"F0.wireOp",EDGE,"E111"),sQuery(id+"F0.wireOp",EDGE,"E112"),sQuery(id+"F0.wireOp",EDGE,"E113"),sQuery(id+"F0.wireOp",EDGE,"E114"),sQuery(id+"F0.wireOp",EDGE,"E115")])],"isStart":false})]});
            var Q18;
            Q18=makeQuery(id+"F6.opFillet","BLEND_EDGE",EDGE,{"blendedFrom":[makeQuery(id+"F5.boolean.opBoolean","COPY",EDGE,{"derivedFrom":makeQuery(id+"F5.opExtrude","CAP_EDGE",EDGE,{"disambiguationData":[OSD([sQuery(id+"F4.wireOp",EDGE,"E757.3.2.0")])],"isStart":false})}),makeQuery(id+"F1.opExtrude","CAP_FACE",FACE,{"disambiguationData":[OSD([sQuery(id+"F0.wireOp",EDGE,"E0"),sQuery(id+"F0.wireOp",EDGE,"E1"),sQuery(id+"F0.wireOp",EDGE,"E2"),sQuery(id+"F0.wireOp",EDGE,"E3"),sQuery(id+"F0.wireOp",EDGE,"E4"),sQuery(id+"F0.wireOp",EDGE,"E5"),sQuery(id+"F0.wireOp",EDGE,"E6"),sQuery(id+"F0.wireOp",EDGE,"E7"),sQuery(id+"F0.wireOp",EDGE,"E8"),sQuery(id+"F0.wireOp",EDGE,"E9"),sQuery(id+"F0.wireOp",EDGE,"E10"),sQuery(id+"F0.wireOp",EDGE,"E11"),sQuery(id+"F0.wireOp",EDGE,"E12"),sQuery(id+"F0.wireOp",EDGE,"E13"),sQuery(id+"F0.wireOp",EDGE,"E14"),sQuery(id+"F0.wireOp",EDGE,"E15"),sQuery(id+"F0.wireOp",EDGE,"E16"),sQuery(id+"F0.wireOp",EDGE,"E17"),sQuery(id+"F0.wireOp",EDGE,"E18"),sQuery(id+"F0.wireOp",EDGE,"E19"),sQuery(id+"F0.wireOp",EDGE,"E20"),sQuery(id+"F0.wireOp",EDGE,"E21"),sQuery(id+"F0.wireOp",EDGE,"E22"),sQuery(id+"F0.wireOp",EDGE,"E23"),sQuery(id+"F0.wireOp",EDGE,"E24"),sQuery(id+"F0.wireOp",EDGE,"E25"),sQuery(id+"F0.wireOp",EDGE,"E26"),sQuery(id+"F0.wireOp",EDGE,"E27"),sQuery(id+"F0.wireOp",EDGE,"E28"),sQuery(id+"F0.wireOp",EDGE,"E29"),sQuery(id+"F0.wireOp",EDGE,"E30"),sQuery(id+"F0.wireOp",EDGE,"E31"),sQuery(id+"F0.wireOp",EDGE,"E32"),sQuery(id+"F0.wireOp",EDGE,"E33"),sQuery(id+"F0.wireOp",EDGE,"E34"),sQuery(id+"F0.wireOp",EDGE,"E35"),sQuery(id+"F0.wireOp",EDGE,"E36"),sQuery(id+"F0.wireOp",EDGE,"E37"),sQuery(id+"F0.wireOp",EDGE,"E38"),sQuery(id+"F0.wireOp",EDGE,"E39"),sQuery(id+"F0.wireOp",EDGE,"E40"),sQuery(id+"F0.wireOp",EDGE,"E41"),sQuery(id+"F0.wireOp",EDGE,"E42"),sQuery(id+"F0.wireOp",EDGE,"E43"),sQuery(id+"F0.wireOp",EDGE,"E44"),sQuery(id+"F0.wireOp",EDGE,"E45"),sQuery(id+"F0.wireOp",EDGE,"E46"),sQuery(id+"F0.wireOp",EDGE,"E47"),sQuery(id+"F0.wireOp",EDGE,"E48"),sQuery(id+"F0.wireOp",EDGE,"E49"),sQuery(id+"F0.wireOp",EDGE,"E50"),sQuery(id+"F0.wireOp",EDGE,"E51"),sQuery(id+"F0.wireOp",EDGE,"E52"),sQuery(id+"F0.wireOp",EDGE,"E53"),sQuery(id+"F0.wireOp",EDGE,"E54"),sQuery(id+"F0.wireOp",EDGE,"E55"),sQuery(id+"F0.wireOp",EDGE,"E56"),sQuery(id+"F0.wireOp",EDGE,"E57"),sQuery(id+"F0.wireOp",EDGE,"E58"),sQuery(id+"F0.wireOp",EDGE,"E59"),sQuery(id+"F0.wireOp",EDGE,"E60"),sQuery(id+"F0.wireOp",EDGE,"E61"),sQuery(id+"F0.wireOp",EDGE,"E62"),sQuery(id+"F0.wireOp",EDGE,"E63"),sQuery(id+"F0.wireOp",EDGE,"E64"),sQuery(id+"F0.wireOp",EDGE,"E65"),sQuery(id+"F0.wireOp",EDGE,"E66"),sQuery(id+"F0.wireOp",EDGE,"E67"),sQuery(id+"F0.wireOp",EDGE,"E68"),sQuery(id+"F0.wireOp",EDGE,"E69"),sQuery(id+"F0.wireOp",EDGE,"E70"),sQuery(id+"F0.wireOp",EDGE,"E71"),sQuery(id+"F0.wireOp",EDGE,"E72"),sQuery(id+"F0.wireOp",EDGE,"E73"),sQuery(id+"F0.wireOp",EDGE,"E74"),sQuery(id+"F0.wireOp",EDGE,"E75"),sQuery(id+"F0.wireOp",EDGE,"E76"),sQuery(id+"F0.wireOp",EDGE,"E77"),sQuery(id+"F0.wireOp",EDGE,"E78"),sQuery(id+"F0.wireOp",EDGE,"E79"),sQuery(id+"F0.wireOp",EDGE,"E80"),sQuery(id+"F0.wireOp",EDGE,"E81"),sQuery(id+"F0.wireOp",EDGE,"E82"),sQuery(id+"F0.wireOp",EDGE,"E83"),sQuery(id+"F0.wireOp",EDGE,"E84"),sQuery(id+"F0.wireOp",EDGE,"E85"),sQuery(id+"F0.wireOp",EDGE,"E86"),sQuery(id+"F0.wireOp",EDGE,"E87"),sQuery(id+"F0.wireOp",EDGE,"E88"),sQuery(id+"F0.wireOp",EDGE,"E89"),sQuery(id+"F0.wireOp",EDGE,"E90"),sQuery(id+"F0.wireOp",EDGE,"E91"),sQuery(id+"F0.wireOp",EDGE,"E92"),sQuery(id+"F0.wireOp",EDGE,"E93"),sQuery(id+"F0.wireOp",EDGE,"E94"),sQuery(id+"F0.wireOp",EDGE,"E95"),sQuery(id+"F0.wireOp",EDGE,"E96"),sQuery(id+"F0.wireOp",EDGE,"E97"),sQuery(id+"F0.wireOp",EDGE,"E98"),sQuery(id+"F0.wireOp",EDGE,"E99"),sQuery(id+"F0.wireOp",EDGE,"E100"),sQuery(id+"F0.wireOp",EDGE,"E101"),sQuery(id+"F0.wireOp",EDGE,"E102"),sQuery(id+"F0.wireOp",EDGE,"E103"),sQuery(id+"F0.wireOp",EDGE,"E104"),sQuery(id+"F0.wireOp",EDGE,"E105"),sQuery(id+"F0.wireOp",EDGE,"E106"),sQuery(id+"F0.wireOp",EDGE,"E107"),sQuery(id+"F0.wireOp",EDGE,"E108"),sQuery(id+"F0.wireOp",EDGE,"E109"),sQuery(id+"F0.wireOp",EDGE,"E110"),sQuery(id+"F0.wireOp",EDGE,"E111"),sQuery(id+"F0.wireOp",EDGE,"E112"),sQuery(id+"F0.wireOp",EDGE,"E113"),sQuery(id+"F0.wireOp",EDGE,"E114"),sQuery(id+"F0.wireOp",EDGE,"E115")])],"isStart":false})],"blendedInto":[makeQuery(id+"F1.opExtrude","CAP_FACE",FACE,{"disambiguationData":[OSD([sQuery(id+"F0.wireOp",EDGE,"E0"),sQuery(id+"F0.wireOp",EDGE,"E1"),sQuery(id+"F0.wireOp",EDGE,"E2"),sQuery(id+"F0.wireOp",EDGE,"E3"),sQuery(id+"F0.wireOp",EDGE,"E4"),sQuery(id+"F0.wireOp",EDGE,"E5"),sQuery(id+"F0.wireOp",EDGE,"E6"),sQuery(id+"F0.wireOp",EDGE,"E7"),sQuery(id+"F0.wireOp",EDGE,"E8"),sQuery(id+"F0.wireOp",EDGE,"E9"),sQuery(id+"F0.wireOp",EDGE,"E10"),sQuery(id+"F0.wireOp",EDGE,"E11"),sQuery(id+"F0.wireOp",EDGE,"E12"),sQuery(id+"F0.wireOp",EDGE,"E13"),sQuery(id+"F0.wireOp",EDGE,"E14"),sQuery(id+"F0.wireOp",EDGE,"E15"),sQuery(id+"F0.wireOp",EDGE,"E16"),sQuery(id+"F0.wireOp",EDGE,"E17"),sQuery(id+"F0.wireOp",EDGE,"E18"),sQuery(id+"F0.wireOp",EDGE,"E19"),sQuery(id+"F0.wireOp",EDGE,"E20"),sQuery(id+"F0.wireOp",EDGE,"E21"),sQuery(id+"F0.wireOp",EDGE,"E22"),sQuery(id+"F0.wireOp",EDGE,"E23"),sQuery(id+"F0.wireOp",EDGE,"E24"),sQuery(id+"F0.wireOp",EDGE,"E25"),sQuery(id+"F0.wireOp",EDGE,"E26"),sQuery(id+"F0.wireOp",EDGE,"E27"),sQuery(id+"F0.wireOp",EDGE,"E28"),sQuery(id+"F0.wireOp",EDGE,"E29"),sQuery(id+"F0.wireOp",EDGE,"E30"),sQuery(id+"F0.wireOp",EDGE,"E31"),sQuery(id+"F0.wireOp",EDGE,"E32"),sQuery(id+"F0.wireOp",EDGE,"E33"),sQuery(id+"F0.wireOp",EDGE,"E34"),sQuery(id+"F0.wireOp",EDGE,"E35"),sQuery(id+"F0.wireOp",EDGE,"E36"),sQuery(id+"F0.wireOp",EDGE,"E37"),sQuery(id+"F0.wireOp",EDGE,"E38"),sQuery(id+"F0.wireOp",EDGE,"E39"),sQuery(id+"F0.wireOp",EDGE,"E40"),sQuery(id+"F0.wireOp",EDGE,"E41"),sQuery(id+"F0.wireOp",EDGE,"E42"),sQuery(id+"F0.wireOp",EDGE,"E43"),sQuery(id+"F0.wireOp",EDGE,"E44"),sQuery(id+"F0.wireOp",EDGE,"E45"),sQuery(id+"F0.wireOp",EDGE,"E46"),sQuery(id+"F0.wireOp",EDGE,"E47"),sQuery(id+"F0.wireOp",EDGE,"E48"),sQuery(id+"F0.wireOp",EDGE,"E49"),sQuery(id+"F0.wireOp",EDGE,"E50"),sQuery(id+"F0.wireOp",EDGE,"E51"),sQuery(id+"F0.wireOp",EDGE,"E52"),sQuery(id+"F0.wireOp",EDGE,"E53"),sQuery(id+"F0.wireOp",EDGE,"E54"),sQuery(id+"F0.wireOp",EDGE,"E55"),sQuery(id+"F0.wireOp",EDGE,"E56"),sQuery(id+"F0.wireOp",EDGE,"E57"),sQuery(id+"F0.wireOp",EDGE,"E58"),sQuery(id+"F0.wireOp",EDGE,"E59"),sQuery(id+"F0.wireOp",EDGE,"E60"),sQuery(id+"F0.wireOp",EDGE,"E61"),sQuery(id+"F0.wireOp",EDGE,"E62"),sQuery(id+"F0.wireOp",EDGE,"E63"),sQuery(id+"F0.wireOp",EDGE,"E64"),sQuery(id+"F0.wireOp",EDGE,"E65"),sQuery(id+"F0.wireOp",EDGE,"E66"),sQuery(id+"F0.wireOp",EDGE,"E67"),sQuery(id+"F0.wireOp",EDGE,"E68"),sQuery(id+"F0.wireOp",EDGE,"E69"),sQuery(id+"F0.wireOp",EDGE,"E70"),sQuery(id+"F0.wireOp",EDGE,"E71"),sQuery(id+"F0.wireOp",EDGE,"E72"),sQuery(id+"F0.wireOp",EDGE,"E73"),sQuery(id+"F0.wireOp",EDGE,"E74"),sQuery(id+"F0.wireOp",EDGE,"E75"),sQuery(id+"F0.wireOp",EDGE,"E76"),sQuery(id+"F0.wireOp",EDGE,"E77"),sQuery(id+"F0.wireOp",EDGE,"E78"),sQuery(id+"F0.wireOp",EDGE,"E79"),sQuery(id+"F0.wireOp",EDGE,"E80"),sQuery(id+"F0.wireOp",EDGE,"E81"),sQuery(id+"F0.wireOp",EDGE,"E82"),sQuery(id+"F0.wireOp",EDGE,"E83"),sQuery(id+"F0.wireOp",EDGE,"E84"),sQuery(id+"F0.wireOp",EDGE,"E85"),sQuery(id+"F0.wireOp",EDGE,"E86"),sQuery(id+"F0.wireOp",EDGE,"E87"),sQuery(id+"F0.wireOp",EDGE,"E88"),sQuery(id+"F0.wireOp",EDGE,"E89"),sQuery(id+"F0.wireOp",EDGE,"E90"),sQuery(id+"F0.wireOp",EDGE,"E91"),sQuery(id+"F0.wireOp",EDGE,"E92"),sQuery(id+"F0.wireOp",EDGE,"E93"),sQuery(id+"F0.wireOp",EDGE,"E94"),sQuery(id+"F0.wireOp",EDGE,"E95"),sQuery(id+"F0.wireOp",EDGE,"E96"),sQuery(id+"F0.wireOp",EDGE,"E97"),sQuery(id+"F0.wireOp",EDGE,"E98"),sQuery(id+"F0.wireOp",EDGE,"E99"),sQuery(id+"F0.wireOp",EDGE,"E100"),sQuery(id+"F0.wireOp",EDGE,"E101"),sQuery(id+"F0.wireOp",EDGE,"E102"),sQuery(id+"F0.wireOp",EDGE,"E103"),sQuery(id+"F0.wireOp",EDGE,"E104"),sQuery(id+"F0.wireOp",EDGE,"E105"),sQuery(id+"F0.wireOp",EDGE,"E106"),sQuery(id+"F0.wireOp",EDGE,"E107"),sQuery(id+"F0.wireOp",EDGE,"E108"),sQuery(id+"F0.wireOp",EDGE,"E109"),sQuery(id+"F0.wireOp",EDGE,"E110"),sQuery(id+"F0.wireOp",EDGE,"E111"),sQuery(id+"F0.wireOp",EDGE,"E112"),sQuery(id+"F0.wireOp",EDGE,"E113"),sQuery(id+"F0.wireOp",EDGE,"E114"),sQuery(id+"F0.wireOp",EDGE,"E115")])],"isStart":false})]});
            var Q19;
            Q19=makeQuery(id+"F6.opFillet","BLEND_EDGE",EDGE,{"blendedFrom":[makeQuery(id+"F5.boolean.opBoolean","COPY",EDGE,{"derivedFrom":makeQuery(id+"F5.opExtrude","CAP_EDGE",EDGE,{"disambiguationData":[OSD([sQuery(id+"F4.wireOp",EDGE,"E757.1.2.0")])],"isStart":false})}),makeQuery(id+"F1.opExtrude","CAP_FACE",FACE,{"disambiguationData":[OSD([sQuery(id+"F0.wireOp",EDGE,"E0"),sQuery(id+"F0.wireOp",EDGE,"E1"),sQuery(id+"F0.wireOp",EDGE,"E2"),sQuery(id+"F0.wireOp",EDGE,"E3"),sQuery(id+"F0.wireOp",EDGE,"E4"),sQuery(id+"F0.wireOp",EDGE,"E5"),sQuery(id+"F0.wireOp",EDGE,"E6"),sQuery(id+"F0.wireOp",EDGE,"E7"),sQuery(id+"F0.wireOp",EDGE,"E8"),sQuery(id+"F0.wireOp",EDGE,"E9"),sQuery(id+"F0.wireOp",EDGE,"E10"),sQuery(id+"F0.wireOp",EDGE,"E11"),sQuery(id+"F0.wireOp",EDGE,"E12"),sQuery(id+"F0.wireOp",EDGE,"E13"),sQuery(id+"F0.wireOp",EDGE,"E14"),sQuery(id+"F0.wireOp",EDGE,"E15"),sQuery(id+"F0.wireOp",EDGE,"E16"),sQuery(id+"F0.wireOp",EDGE,"E17"),sQuery(id+"F0.wireOp",EDGE,"E18"),sQuery(id+"F0.wireOp",EDGE,"E19"),sQuery(id+"F0.wireOp",EDGE,"E20"),sQuery(id+"F0.wireOp",EDGE,"E21"),sQuery(id+"F0.wireOp",EDGE,"E22"),sQuery(id+"F0.wireOp",EDGE,"E23"),sQuery(id+"F0.wireOp",EDGE,"E24"),sQuery(id+"F0.wireOp",EDGE,"E25"),sQuery(id+"F0.wireOp",EDGE,"E26"),sQuery(id+"F0.wireOp",EDGE,"E27"),sQuery(id+"F0.wireOp",EDGE,"E28"),sQuery(id+"F0.wireOp",EDGE,"E29"),sQuery(id+"F0.wireOp",EDGE,"E30"),sQuery(id+"F0.wireOp",EDGE,"E31"),sQuery(id+"F0.wireOp",EDGE,"E32"),sQuery(id+"F0.wireOp",EDGE,"E33"),sQuery(id+"F0.wireOp",EDGE,"E34"),sQuery(id+"F0.wireOp",EDGE,"E35"),sQuery(id+"F0.wireOp",EDGE,"E36"),sQuery(id+"F0.wireOp",EDGE,"E37"),sQuery(id+"F0.wireOp",EDGE,"E38"),sQuery(id+"F0.wireOp",EDGE,"E39"),sQuery(id+"F0.wireOp",EDGE,"E40"),sQuery(id+"F0.wireOp",EDGE,"E41"),sQuery(id+"F0.wireOp",EDGE,"E42"),sQuery(id+"F0.wireOp",EDGE,"E43"),sQuery(id+"F0.wireOp",EDGE,"E44"),sQuery(id+"F0.wireOp",EDGE,"E45"),sQuery(id+"F0.wireOp",EDGE,"E46"),sQuery(id+"F0.wireOp",EDGE,"E47"),sQuery(id+"F0.wireOp",EDGE,"E48"),sQuery(id+"F0.wireOp",EDGE,"E49"),sQuery(id+"F0.wireOp",EDGE,"E50"),sQuery(id+"F0.wireOp",EDGE,"E51"),sQuery(id+"F0.wireOp",EDGE,"E52"),sQuery(id+"F0.wireOp",EDGE,"E53"),sQuery(id+"F0.wireOp",EDGE,"E54"),sQuery(id+"F0.wireOp",EDGE,"E55"),sQuery(id+"F0.wireOp",EDGE,"E56"),sQuery(id+"F0.wireOp",EDGE,"E57"),sQuery(id+"F0.wireOp",EDGE,"E58"),sQuery(id+"F0.wireOp",EDGE,"E59"),sQuery(id+"F0.wireOp",EDGE,"E60"),sQuery(id+"F0.wireOp",EDGE,"E61"),sQuery(id+"F0.wireOp",EDGE,"E62"),sQuery(id+"F0.wireOp",EDGE,"E63"),sQuery(id+"F0.wireOp",EDGE,"E64"),sQuery(id+"F0.wireOp",EDGE,"E65"),sQuery(id+"F0.wireOp",EDGE,"E66"),sQuery(id+"F0.wireOp",EDGE,"E67"),sQuery(id+"F0.wireOp",EDGE,"E68"),sQuery(id+"F0.wireOp",EDGE,"E69"),sQuery(id+"F0.wireOp",EDGE,"E70"),sQuery(id+"F0.wireOp",EDGE,"E71"),sQuery(id+"F0.wireOp",EDGE,"E72"),sQuery(id+"F0.wireOp",EDGE,"E73"),sQuery(id+"F0.wireOp",EDGE,"E74"),sQuery(id+"F0.wireOp",EDGE,"E75"),sQuery(id+"F0.wireOp",EDGE,"E76"),sQuery(id+"F0.wireOp",EDGE,"E77"),sQuery(id+"F0.wireOp",EDGE,"E78"),sQuery(id+"F0.wireOp",EDGE,"E79"),sQuery(id+"F0.wireOp",EDGE,"E80"),sQuery(id+"F0.wireOp",EDGE,"E81"),sQuery(id+"F0.wireOp",EDGE,"E82"),sQuery(id+"F0.wireOp",EDGE,"E83"),sQuery(id+"F0.wireOp",EDGE,"E84"),sQuery(id+"F0.wireOp",EDGE,"E85"),sQuery(id+"F0.wireOp",EDGE,"E86"),sQuery(id+"F0.wireOp",EDGE,"E87"),sQuery(id+"F0.wireOp",EDGE,"E88"),sQuery(id+"F0.wireOp",EDGE,"E89"),sQuery(id+"F0.wireOp",EDGE,"E90"),sQuery(id+"F0.wireOp",EDGE,"E91"),sQuery(id+"F0.wireOp",EDGE,"E92"),sQuery(id+"F0.wireOp",EDGE,"E93"),sQuery(id+"F0.wireOp",EDGE,"E94"),sQuery(id+"F0.wireOp",EDGE,"E95"),sQuery(id+"F0.wireOp",EDGE,"E96"),sQuery(id+"F0.wireOp",EDGE,"E97"),sQuery(id+"F0.wireOp",EDGE,"E98"),sQuery(id+"F0.wireOp",EDGE,"E99"),sQuery(id+"F0.wireOp",EDGE,"E100"),sQuery(id+"F0.wireOp",EDGE,"E101"),sQuery(id+"F0.wireOp",EDGE,"E102"),sQuery(id+"F0.wireOp",EDGE,"E103"),sQuery(id+"F0.wireOp",EDGE,"E104"),sQuery(id+"F0.wireOp",EDGE,"E105"),sQuery(id+"F0.wireOp",EDGE,"E106"),sQuery(id+"F0.wireOp",EDGE,"E107"),sQuery(id+"F0.wireOp",EDGE,"E108"),sQuery(id+"F0.wireOp",EDGE,"E109"),sQuery(id+"F0.wireOp",EDGE,"E110"),sQuery(id+"F0.wireOp",EDGE,"E111"),sQuery(id+"F0.wireOp",EDGE,"E112"),sQuery(id+"F0.wireOp",EDGE,"E113"),sQuery(id+"F0.wireOp",EDGE,"E114"),sQuery(id+"F0.wireOp",EDGE,"E115")])],"isStart":false})],"blendedInto":[makeQuery(id+"F1.opExtrude","CAP_FACE",FACE,{"disambiguationData":[OSD([sQuery(id+"F0.wireOp",EDGE,"E0"),sQuery(id+"F0.wireOp",EDGE,"E1"),sQuery(id+"F0.wireOp",EDGE,"E2"),sQuery(id+"F0.wireOp",EDGE,"E3"),sQuery(id+"F0.wireOp",EDGE,"E4"),sQuery(id+"F0.wireOp",EDGE,"E5"),sQuery(id+"F0.wireOp",EDGE,"E6"),sQuery(id+"F0.wireOp",EDGE,"E7"),sQuery(id+"F0.wireOp",EDGE,"E8"),sQuery(id+"F0.wireOp",EDGE,"E9"),sQuery(id+"F0.wireOp",EDGE,"E10"),sQuery(id+"F0.wireOp",EDGE,"E11"),sQuery(id+"F0.wireOp",EDGE,"E12"),sQuery(id+"F0.wireOp",EDGE,"E13"),sQuery(id+"F0.wireOp",EDGE,"E14"),sQuery(id+"F0.wireOp",EDGE,"E15"),sQuery(id+"F0.wireOp",EDGE,"E16"),sQuery(id+"F0.wireOp",EDGE,"E17"),sQuery(id+"F0.wireOp",EDGE,"E18"),sQuery(id+"F0.wireOp",EDGE,"E19"),sQuery(id+"F0.wireOp",EDGE,"E20"),sQuery(id+"F0.wireOp",EDGE,"E21"),sQuery(id+"F0.wireOp",EDGE,"E22"),sQuery(id+"F0.wireOp",EDGE,"E23"),sQuery(id+"F0.wireOp",EDGE,"E24"),sQuery(id+"F0.wireOp",EDGE,"E25"),sQuery(id+"F0.wireOp",EDGE,"E26"),sQuery(id+"F0.wireOp",EDGE,"E27"),sQuery(id+"F0.wireOp",EDGE,"E28"),sQuery(id+"F0.wireOp",EDGE,"E29"),sQuery(id+"F0.wireOp",EDGE,"E30"),sQuery(id+"F0.wireOp",EDGE,"E31"),sQuery(id+"F0.wireOp",EDGE,"E32"),sQuery(id+"F0.wireOp",EDGE,"E33"),sQuery(id+"F0.wireOp",EDGE,"E34"),sQuery(id+"F0.wireOp",EDGE,"E35"),sQuery(id+"F0.wireOp",EDGE,"E36"),sQuery(id+"F0.wireOp",EDGE,"E37"),sQuery(id+"F0.wireOp",EDGE,"E38"),sQuery(id+"F0.wireOp",EDGE,"E39"),sQuery(id+"F0.wireOp",EDGE,"E40"),sQuery(id+"F0.wireOp",EDGE,"E41"),sQuery(id+"F0.wireOp",EDGE,"E42"),sQuery(id+"F0.wireOp",EDGE,"E43"),sQuery(id+"F0.wireOp",EDGE,"E44"),sQuery(id+"F0.wireOp",EDGE,"E45"),sQuery(id+"F0.wireOp",EDGE,"E46"),sQuery(id+"F0.wireOp",EDGE,"E47"),sQuery(id+"F0.wireOp",EDGE,"E48"),sQuery(id+"F0.wireOp",EDGE,"E49"),sQuery(id+"F0.wireOp",EDGE,"E50"),sQuery(id+"F0.wireOp",EDGE,"E51"),sQuery(id+"F0.wireOp",EDGE,"E52"),sQuery(id+"F0.wireOp",EDGE,"E53"),sQuery(id+"F0.wireOp",EDGE,"E54"),sQuery(id+"F0.wireOp",EDGE,"E55"),sQuery(id+"F0.wireOp",EDGE,"E56"),sQuery(id+"F0.wireOp",EDGE,"E57"),sQuery(id+"F0.wireOp",EDGE,"E58"),sQuery(id+"F0.wireOp",EDGE,"E59"),sQuery(id+"F0.wireOp",EDGE,"E60"),sQuery(id+"F0.wireOp",EDGE,"E61"),sQuery(id+"F0.wireOp",EDGE,"E62"),sQuery(id+"F0.wireOp",EDGE,"E63"),sQuery(id+"F0.wireOp",EDGE,"E64"),sQuery(id+"F0.wireOp",EDGE,"E65"),sQuery(id+"F0.wireOp",EDGE,"E66"),sQuery(id+"F0.wireOp",EDGE,"E67"),sQuery(id+"F0.wireOp",EDGE,"E68"),sQuery(id+"F0.wireOp",EDGE,"E69"),sQuery(id+"F0.wireOp",EDGE,"E70"),sQuery(id+"F0.wireOp",EDGE,"E71"),sQuery(id+"F0.wireOp",EDGE,"E72"),sQuery(id+"F0.wireOp",EDGE,"E73"),sQuery(id+"F0.wireOp",EDGE,"E74"),sQuery(id+"F0.wireOp",EDGE,"E75"),sQuery(id+"F0.wireOp",EDGE,"E76"),sQuery(id+"F0.wireOp",EDGE,"E77"),sQuery(id+"F0.wireOp",EDGE,"E78"),sQuery(id+"F0.wireOp",EDGE,"E79"),sQuery(id+"F0.wireOp",EDGE,"E80"),sQuery(id+"F0.wireOp",EDGE,"E81"),sQuery(id+"F0.wireOp",EDGE,"E82"),sQuery(id+"F0.wireOp",EDGE,"E83"),sQuery(id+"F0.wireOp",EDGE,"E84"),sQuery(id+"F0.wireOp",EDGE,"E85"),sQuery(id+"F0.wireOp",EDGE,"E86"),sQuery(id+"F0.wireOp",EDGE,"E87"),sQuery(id+"F0.wireOp",EDGE,"E88"),sQuery(id+"F0.wireOp",EDGE,"E89"),sQuery(id+"F0.wireOp",EDGE,"E90"),sQuery(id+"F0.wireOp",EDGE,"E91"),sQuery(id+"F0.wireOp",EDGE,"E92"),sQuery(id+"F0.wireOp",EDGE,"E93"),sQuery(id+"F0.wireOp",EDGE,"E94"),sQuery(id+"F0.wireOp",EDGE,"E95"),sQuery(id+"F0.wireOp",EDGE,"E96"),sQuery(id+"F0.wireOp",EDGE,"E97"),sQuery(id+"F0.wireOp",EDGE,"E98"),sQuery(id+"F0.wireOp",EDGE,"E99"),sQuery(id+"F0.wireOp",EDGE,"E100"),sQuery(id+"F0.wireOp",EDGE,"E101"),sQuery(id+"F0.wireOp",EDGE,"E102"),sQuery(id+"F0.wireOp",EDGE,"E103"),sQuery(id+"F0.wireOp",EDGE,"E104"),sQuery(id+"F0.wireOp",EDGE,"E105"),sQuery(id+"F0.wireOp",EDGE,"E106"),sQuery(id+"F0.wireOp",EDGE,"E107"),sQuery(id+"F0.wireOp",EDGE,"E108"),sQuery(id+"F0.wireOp",EDGE,"E109"),sQuery(id+"F0.wireOp",EDGE,"E110"),sQuery(id+"F0.wireOp",EDGE,"E111"),sQuery(id+"F0.wireOp",EDGE,"E112"),sQuery(id+"F0.wireOp",EDGE,"E113"),sQuery(id+"F0.wireOp",EDGE,"E114"),sQuery(id+"F0.wireOp",EDGE,"E115")])],"isStart":false})]});
            var Q20;
            Q20=makeQuery(id+"F6.opFillet","BLEND_EDGE",EDGE,{"blendedFrom":[makeQuery(id+"F5.boolean.opBoolean","COPY",EDGE,{"derivedFrom":makeQuery(id+"F5.opExtrude","CAP_EDGE",EDGE,{"disambiguationData":[OSD([sQuery(id+"F4.wireOp",EDGE,"E758.0.5.2")])],"isStart":false})}),makeQuery(id+"F1.opExtrude","CAP_FACE",FACE,{"disambiguationData":[OSD([sQuery(id+"F0.wireOp",EDGE,"E0"),sQuery(id+"F0.wireOp",EDGE,"E1"),sQuery(id+"F0.wireOp",EDGE,"E2"),sQuery(id+"F0.wireOp",EDGE,"E3"),sQuery(id+"F0.wireOp",EDGE,"E4"),sQuery(id+"F0.wireOp",EDGE,"E5"),sQuery(id+"F0.wireOp",EDGE,"E6"),sQuery(id+"F0.wireOp",EDGE,"E7"),sQuery(id+"F0.wireOp",EDGE,"E8"),sQuery(id+"F0.wireOp",EDGE,"E9"),sQuery(id+"F0.wireOp",EDGE,"E10"),sQuery(id+"F0.wireOp",EDGE,"E11"),sQuery(id+"F0.wireOp",EDGE,"E12"),sQuery(id+"F0.wireOp",EDGE,"E13"),sQuery(id+"F0.wireOp",EDGE,"E14"),sQuery(id+"F0.wireOp",EDGE,"E15"),sQuery(id+"F0.wireOp",EDGE,"E16"),sQuery(id+"F0.wireOp",EDGE,"E17"),sQuery(id+"F0.wireOp",EDGE,"E18"),sQuery(id+"F0.wireOp",EDGE,"E19"),sQuery(id+"F0.wireOp",EDGE,"E20"),sQuery(id+"F0.wireOp",EDGE,"E21"),sQuery(id+"F0.wireOp",EDGE,"E22"),sQuery(id+"F0.wireOp",EDGE,"E23"),sQuery(id+"F0.wireOp",EDGE,"E24"),sQuery(id+"F0.wireOp",EDGE,"E25"),sQuery(id+"F0.wireOp",EDGE,"E26"),sQuery(id+"F0.wireOp",EDGE,"E27"),sQuery(id+"F0.wireOp",EDGE,"E28"),sQuery(id+"F0.wireOp",EDGE,"E29"),sQuery(id+"F0.wireOp",EDGE,"E30"),sQuery(id+"F0.wireOp",EDGE,"E31"),sQuery(id+"F0.wireOp",EDGE,"E32"),sQuery(id+"F0.wireOp",EDGE,"E33"),sQuery(id+"F0.wireOp",EDGE,"E34"),sQuery(id+"F0.wireOp",EDGE,"E35"),sQuery(id+"F0.wireOp",EDGE,"E36"),sQuery(id+"F0.wireOp",EDGE,"E37"),sQuery(id+"F0.wireOp",EDGE,"E38"),sQuery(id+"F0.wireOp",EDGE,"E39"),sQuery(id+"F0.wireOp",EDGE,"E40"),sQuery(id+"F0.wireOp",EDGE,"E41"),sQuery(id+"F0.wireOp",EDGE,"E42"),sQuery(id+"F0.wireOp",EDGE,"E43"),sQuery(id+"F0.wireOp",EDGE,"E44"),sQuery(id+"F0.wireOp",EDGE,"E45"),sQuery(id+"F0.wireOp",EDGE,"E46"),sQuery(id+"F0.wireOp",EDGE,"E47"),sQuery(id+"F0.wireOp",EDGE,"E48"),sQuery(id+"F0.wireOp",EDGE,"E49"),sQuery(id+"F0.wireOp",EDGE,"E50"),sQuery(id+"F0.wireOp",EDGE,"E51"),sQuery(id+"F0.wireOp",EDGE,"E52"),sQuery(id+"F0.wireOp",EDGE,"E53"),sQuery(id+"F0.wireOp",EDGE,"E54"),sQuery(id+"F0.wireOp",EDGE,"E55"),sQuery(id+"F0.wireOp",EDGE,"E56"),sQuery(id+"F0.wireOp",EDGE,"E57"),sQuery(id+"F0.wireOp",EDGE,"E58"),sQuery(id+"F0.wireOp",EDGE,"E59"),sQuery(id+"F0.wireOp",EDGE,"E60"),sQuery(id+"F0.wireOp",EDGE,"E61"),sQuery(id+"F0.wireOp",EDGE,"E62"),sQuery(id+"F0.wireOp",EDGE,"E63"),sQuery(id+"F0.wireOp",EDGE,"E64"),sQuery(id+"F0.wireOp",EDGE,"E65"),sQuery(id+"F0.wireOp",EDGE,"E66"),sQuery(id+"F0.wireOp",EDGE,"E67"),sQuery(id+"F0.wireOp",EDGE,"E68"),sQuery(id+"F0.wireOp",EDGE,"E69"),sQuery(id+"F0.wireOp",EDGE,"E70"),sQuery(id+"F0.wireOp",EDGE,"E71"),sQuery(id+"F0.wireOp",EDGE,"E72"),sQuery(id+"F0.wireOp",EDGE,"E73"),sQuery(id+"F0.wireOp",EDGE,"E74"),sQuery(id+"F0.wireOp",EDGE,"E75"),sQuery(id+"F0.wireOp",EDGE,"E76"),sQuery(id+"F0.wireOp",EDGE,"E77"),sQuery(id+"F0.wireOp",EDGE,"E78"),sQuery(id+"F0.wireOp",EDGE,"E79"),sQuery(id+"F0.wireOp",EDGE,"E80"),sQuery(id+"F0.wireOp",EDGE,"E81"),sQuery(id+"F0.wireOp",EDGE,"E82"),sQuery(id+"F0.wireOp",EDGE,"E83"),sQuery(id+"F0.wireOp",EDGE,"E84"),sQuery(id+"F0.wireOp",EDGE,"E85"),sQuery(id+"F0.wireOp",EDGE,"E86"),sQuery(id+"F0.wireOp",EDGE,"E87"),sQuery(id+"F0.wireOp",EDGE,"E88"),sQuery(id+"F0.wireOp",EDGE,"E89"),sQuery(id+"F0.wireOp",EDGE,"E90"),sQuery(id+"F0.wireOp",EDGE,"E91"),sQuery(id+"F0.wireOp",EDGE,"E92"),sQuery(id+"F0.wireOp",EDGE,"E93"),sQuery(id+"F0.wireOp",EDGE,"E94"),sQuery(id+"F0.wireOp",EDGE,"E95"),sQuery(id+"F0.wireOp",EDGE,"E96"),sQuery(id+"F0.wireOp",EDGE,"E97"),sQuery(id+"F0.wireOp",EDGE,"E98"),sQuery(id+"F0.wireOp",EDGE,"E99"),sQuery(id+"F0.wireOp",EDGE,"E100"),sQuery(id+"F0.wireOp",EDGE,"E101"),sQuery(id+"F0.wireOp",EDGE,"E102"),sQuery(id+"F0.wireOp",EDGE,"E103"),sQuery(id+"F0.wireOp",EDGE,"E104"),sQuery(id+"F0.wireOp",EDGE,"E105"),sQuery(id+"F0.wireOp",EDGE,"E106"),sQuery(id+"F0.wireOp",EDGE,"E107"),sQuery(id+"F0.wireOp",EDGE,"E108"),sQuery(id+"F0.wireOp",EDGE,"E109"),sQuery(id+"F0.wireOp",EDGE,"E110"),sQuery(id+"F0.wireOp",EDGE,"E111"),sQuery(id+"F0.wireOp",EDGE,"E112"),sQuery(id+"F0.wireOp",EDGE,"E113"),sQuery(id+"F0.wireOp",EDGE,"E114"),sQuery(id+"F0.wireOp",EDGE,"E115")])],"isStart":false})],"blendedInto":[makeQuery(id+"F1.opExtrude","CAP_FACE",FACE,{"disambiguationData":[OSD([sQuery(id+"F0.wireOp",EDGE,"E0"),sQuery(id+"F0.wireOp",EDGE,"E1"),sQuery(id+"F0.wireOp",EDGE,"E2"),sQuery(id+"F0.wireOp",EDGE,"E3"),sQuery(id+"F0.wireOp",EDGE,"E4"),sQuery(id+"F0.wireOp",EDGE,"E5"),sQuery(id+"F0.wireOp",EDGE,"E6"),sQuery(id+"F0.wireOp",EDGE,"E7"),sQuery(id+"F0.wireOp",EDGE,"E8"),sQuery(id+"F0.wireOp",EDGE,"E9"),sQuery(id+"F0.wireOp",EDGE,"E10"),sQuery(id+"F0.wireOp",EDGE,"E11"),sQuery(id+"F0.wireOp",EDGE,"E12"),sQuery(id+"F0.wireOp",EDGE,"E13"),sQuery(id+"F0.wireOp",EDGE,"E14"),sQuery(id+"F0.wireOp",EDGE,"E15"),sQuery(id+"F0.wireOp",EDGE,"E16"),sQuery(id+"F0.wireOp",EDGE,"E17"),sQuery(id+"F0.wireOp",EDGE,"E18"),sQuery(id+"F0.wireOp",EDGE,"E19"),sQuery(id+"F0.wireOp",EDGE,"E20"),sQuery(id+"F0.wireOp",EDGE,"E21"),sQuery(id+"F0.wireOp",EDGE,"E22"),sQuery(id+"F0.wireOp",EDGE,"E23"),sQuery(id+"F0.wireOp",EDGE,"E24"),sQuery(id+"F0.wireOp",EDGE,"E25"),sQuery(id+"F0.wireOp",EDGE,"E26"),sQuery(id+"F0.wireOp",EDGE,"E27"),sQuery(id+"F0.wireOp",EDGE,"E28"),sQuery(id+"F0.wireOp",EDGE,"E29"),sQuery(id+"F0.wireOp",EDGE,"E30"),sQuery(id+"F0.wireOp",EDGE,"E31"),sQuery(id+"F0.wireOp",EDGE,"E32"),sQuery(id+"F0.wireOp",EDGE,"E33"),sQuery(id+"F0.wireOp",EDGE,"E34"),sQuery(id+"F0.wireOp",EDGE,"E35"),sQuery(id+"F0.wireOp",EDGE,"E36"),sQuery(id+"F0.wireOp",EDGE,"E37"),sQuery(id+"F0.wireOp",EDGE,"E38"),sQuery(id+"F0.wireOp",EDGE,"E39"),sQuery(id+"F0.wireOp",EDGE,"E40"),sQuery(id+"F0.wireOp",EDGE,"E41"),sQuery(id+"F0.wireOp",EDGE,"E42"),sQuery(id+"F0.wireOp",EDGE,"E43"),sQuery(id+"F0.wireOp",EDGE,"E44"),sQuery(id+"F0.wireOp",EDGE,"E45"),sQuery(id+"F0.wireOp",EDGE,"E46"),sQuery(id+"F0.wireOp",EDGE,"E47"),sQuery(id+"F0.wireOp",EDGE,"E48"),sQuery(id+"F0.wireOp",EDGE,"E49"),sQuery(id+"F0.wireOp",EDGE,"E50"),sQuery(id+"F0.wireOp",EDGE,"E51"),sQuery(id+"F0.wireOp",EDGE,"E52"),sQuery(id+"F0.wireOp",EDGE,"E53"),sQuery(id+"F0.wireOp",EDGE,"E54"),sQuery(id+"F0.wireOp",EDGE,"E55"),sQuery(id+"F0.wireOp",EDGE,"E56"),sQuery(id+"F0.wireOp",EDGE,"E57"),sQuery(id+"F0.wireOp",EDGE,"E58"),sQuery(id+"F0.wireOp",EDGE,"E59"),sQuery(id+"F0.wireOp",EDGE,"E60"),sQuery(id+"F0.wireOp",EDGE,"E61"),sQuery(id+"F0.wireOp",EDGE,"E62"),sQuery(id+"F0.wireOp",EDGE,"E63"),sQuery(id+"F0.wireOp",EDGE,"E64"),sQuery(id+"F0.wireOp",EDGE,"E65"),sQuery(id+"F0.wireOp",EDGE,"E66"),sQuery(id+"F0.wireOp",EDGE,"E67"),sQuery(id+"F0.wireOp",EDGE,"E68"),sQuery(id+"F0.wireOp",EDGE,"E69"),sQuery(id+"F0.wireOp",EDGE,"E70"),sQuery(id+"F0.wireOp",EDGE,"E71"),sQuery(id+"F0.wireOp",EDGE,"E72"),sQuery(id+"F0.wireOp",EDGE,"E73"),sQuery(id+"F0.wireOp",EDGE,"E74"),sQuery(id+"F0.wireOp",EDGE,"E75"),sQuery(id+"F0.wireOp",EDGE,"E76"),sQuery(id+"F0.wireOp",EDGE,"E77"),sQuery(id+"F0.wireOp",EDGE,"E78"),sQuery(id+"F0.wireOp",EDGE,"E79"),sQuery(id+"F0.wireOp",EDGE,"E80"),sQuery(id+"F0.wireOp",EDGE,"E81"),sQuery(id+"F0.wireOp",EDGE,"E82"),sQuery(id+"F0.wireOp",EDGE,"E83"),sQuery(id+"F0.wireOp",EDGE,"E84"),sQuery(id+"F0.wireOp",EDGE,"E85"),sQuery(id+"F0.wireOp",EDGE,"E86"),sQuery(id+"F0.wireOp",EDGE,"E87"),sQuery(id+"F0.wireOp",EDGE,"E88"),sQuery(id+"F0.wireOp",EDGE,"E89"),sQuery(id+"F0.wireOp",EDGE,"E90"),sQuery(id+"F0.wireOp",EDGE,"E91"),sQuery(id+"F0.wireOp",EDGE,"E92"),sQuery(id+"F0.wireOp",EDGE,"E93"),sQuery(id+"F0.wireOp",EDGE,"E94"),sQuery(id+"F0.wireOp",EDGE,"E95"),sQuery(id+"F0.wireOp",EDGE,"E96"),sQuery(id+"F0.wireOp",EDGE,"E97"),sQuery(id+"F0.wireOp",EDGE,"E98"),sQuery(id+"F0.wireOp",EDGE,"E99"),sQuery(id+"F0.wireOp",EDGE,"E100"),sQuery(id+"F0.wireOp",EDGE,"E101"),sQuery(id+"F0.wireOp",EDGE,"E102"),sQuery(id+"F0.wireOp",EDGE,"E103"),sQuery(id+"F0.wireOp",EDGE,"E104"),sQuery(id+"F0.wireOp",EDGE,"E105"),sQuery(id+"F0.wireOp",EDGE,"E106"),sQuery(id+"F0.wireOp",EDGE,"E107"),sQuery(id+"F0.wireOp",EDGE,"E108"),sQuery(id+"F0.wireOp",EDGE,"E109"),sQuery(id+"F0.wireOp",EDGE,"E110"),sQuery(id+"F0.wireOp",EDGE,"E111"),sQuery(id+"F0.wireOp",EDGE,"E112"),sQuery(id+"F0.wireOp",EDGE,"E113"),sQuery(id+"F0.wireOp",EDGE,"E114"),sQuery(id+"F0.wireOp",EDGE,"E115")])],"isStart":false})]});
            var Q21;
            Q21=makeQuery(id+"F6.opFillet","BLEND_EDGE",EDGE,{"blendedFrom":[makeQuery(id+"F5.boolean.opBoolean","COPY",EDGE,{"derivedFrom":makeQuery(id+"F5.opExtrude","CAP_EDGE",EDGE,{"disambiguationData":[OSD([sQuery(id+"F4.wireOp",EDGE,"E758.0.5.1")])],"isStart":false})}),makeQuery(id+"F1.opExtrude","CAP_FACE",FACE,{"disambiguationData":[OSD([sQuery(id+"F0.wireOp",EDGE,"E0"),sQuery(id+"F0.wireOp",EDGE,"E1"),sQuery(id+"F0.wireOp",EDGE,"E2"),sQuery(id+"F0.wireOp",EDGE,"E3"),sQuery(id+"F0.wireOp",EDGE,"E4"),sQuery(id+"F0.wireOp",EDGE,"E5"),sQuery(id+"F0.wireOp",EDGE,"E6"),sQuery(id+"F0.wireOp",EDGE,"E7"),sQuery(id+"F0.wireOp",EDGE,"E8"),sQuery(id+"F0.wireOp",EDGE,"E9"),sQuery(id+"F0.wireOp",EDGE,"E10"),sQuery(id+"F0.wireOp",EDGE,"E11"),sQuery(id+"F0.wireOp",EDGE,"E12"),sQuery(id+"F0.wireOp",EDGE,"E13"),sQuery(id+"F0.wireOp",EDGE,"E14"),sQuery(id+"F0.wireOp",EDGE,"E15"),sQuery(id+"F0.wireOp",EDGE,"E16"),sQuery(id+"F0.wireOp",EDGE,"E17"),sQuery(id+"F0.wireOp",EDGE,"E18"),sQuery(id+"F0.wireOp",EDGE,"E19"),sQuery(id+"F0.wireOp",EDGE,"E20"),sQuery(id+"F0.wireOp",EDGE,"E21"),sQuery(id+"F0.wireOp",EDGE,"E22"),sQuery(id+"F0.wireOp",EDGE,"E23"),sQuery(id+"F0.wireOp",EDGE,"E24"),sQuery(id+"F0.wireOp",EDGE,"E25"),sQuery(id+"F0.wireOp",EDGE,"E26"),sQuery(id+"F0.wireOp",EDGE,"E27"),sQuery(id+"F0.wireOp",EDGE,"E28"),sQuery(id+"F0.wireOp",EDGE,"E29"),sQuery(id+"F0.wireOp",EDGE,"E30"),sQuery(id+"F0.wireOp",EDGE,"E31"),sQuery(id+"F0.wireOp",EDGE,"E32"),sQuery(id+"F0.wireOp",EDGE,"E33"),sQuery(id+"F0.wireOp",EDGE,"E34"),sQuery(id+"F0.wireOp",EDGE,"E35"),sQuery(id+"F0.wireOp",EDGE,"E36"),sQuery(id+"F0.wireOp",EDGE,"E37"),sQuery(id+"F0.wireOp",EDGE,"E38"),sQuery(id+"F0.wireOp",EDGE,"E39"),sQuery(id+"F0.wireOp",EDGE,"E40"),sQuery(id+"F0.wireOp",EDGE,"E41"),sQuery(id+"F0.wireOp",EDGE,"E42"),sQuery(id+"F0.wireOp",EDGE,"E43"),sQuery(id+"F0.wireOp",EDGE,"E44"),sQuery(id+"F0.wireOp",EDGE,"E45"),sQuery(id+"F0.wireOp",EDGE,"E46"),sQuery(id+"F0.wireOp",EDGE,"E47"),sQuery(id+"F0.wireOp",EDGE,"E48"),sQuery(id+"F0.wireOp",EDGE,"E49"),sQuery(id+"F0.wireOp",EDGE,"E50"),sQuery(id+"F0.wireOp",EDGE,"E51"),sQuery(id+"F0.wireOp",EDGE,"E52"),sQuery(id+"F0.wireOp",EDGE,"E53"),sQuery(id+"F0.wireOp",EDGE,"E54"),sQuery(id+"F0.wireOp",EDGE,"E55"),sQuery(id+"F0.wireOp",EDGE,"E56"),sQuery(id+"F0.wireOp",EDGE,"E57"),sQuery(id+"F0.wireOp",EDGE,"E58"),sQuery(id+"F0.wireOp",EDGE,"E59"),sQuery(id+"F0.wireOp",EDGE,"E60"),sQuery(id+"F0.wireOp",EDGE,"E61"),sQuery(id+"F0.wireOp",EDGE,"E62"),sQuery(id+"F0.wireOp",EDGE,"E63"),sQuery(id+"F0.wireOp",EDGE,"E64"),sQuery(id+"F0.wireOp",EDGE,"E65"),sQuery(id+"F0.wireOp",EDGE,"E66"),sQuery(id+"F0.wireOp",EDGE,"E67"),sQuery(id+"F0.wireOp",EDGE,"E68"),sQuery(id+"F0.wireOp",EDGE,"E69"),sQuery(id+"F0.wireOp",EDGE,"E70"),sQuery(id+"F0.wireOp",EDGE,"E71"),sQuery(id+"F0.wireOp",EDGE,"E72"),sQuery(id+"F0.wireOp",EDGE,"E73"),sQuery(id+"F0.wireOp",EDGE,"E74"),sQuery(id+"F0.wireOp",EDGE,"E75"),sQuery(id+"F0.wireOp",EDGE,"E76"),sQuery(id+"F0.wireOp",EDGE,"E77"),sQuery(id+"F0.wireOp",EDGE,"E78"),sQuery(id+"F0.wireOp",EDGE,"E79"),sQuery(id+"F0.wireOp",EDGE,"E80"),sQuery(id+"F0.wireOp",EDGE,"E81"),sQuery(id+"F0.wireOp",EDGE,"E82"),sQuery(id+"F0.wireOp",EDGE,"E83"),sQuery(id+"F0.wireOp",EDGE,"E84"),sQuery(id+"F0.wireOp",EDGE,"E85"),sQuery(id+"F0.wireOp",EDGE,"E86"),sQuery(id+"F0.wireOp",EDGE,"E87"),sQuery(id+"F0.wireOp",EDGE,"E88"),sQuery(id+"F0.wireOp",EDGE,"E89"),sQuery(id+"F0.wireOp",EDGE,"E90"),sQuery(id+"F0.wireOp",EDGE,"E91"),sQuery(id+"F0.wireOp",EDGE,"E92"),sQuery(id+"F0.wireOp",EDGE,"E93"),sQuery(id+"F0.wireOp",EDGE,"E94"),sQuery(id+"F0.wireOp",EDGE,"E95"),sQuery(id+"F0.wireOp",EDGE,"E96"),sQuery(id+"F0.wireOp",EDGE,"E97"),sQuery(id+"F0.wireOp",EDGE,"E98"),sQuery(id+"F0.wireOp",EDGE,"E99"),sQuery(id+"F0.wireOp",EDGE,"E100"),sQuery(id+"F0.wireOp",EDGE,"E101"),sQuery(id+"F0.wireOp",EDGE,"E102"),sQuery(id+"F0.wireOp",EDGE,"E103"),sQuery(id+"F0.wireOp",EDGE,"E104"),sQuery(id+"F0.wireOp",EDGE,"E105"),sQuery(id+"F0.wireOp",EDGE,"E106"),sQuery(id+"F0.wireOp",EDGE,"E107"),sQuery(id+"F0.wireOp",EDGE,"E108"),sQuery(id+"F0.wireOp",EDGE,"E109"),sQuery(id+"F0.wireOp",EDGE,"E110"),sQuery(id+"F0.wireOp",EDGE,"E111"),sQuery(id+"F0.wireOp",EDGE,"E112"),sQuery(id+"F0.wireOp",EDGE,"E113"),sQuery(id+"F0.wireOp",EDGE,"E114"),sQuery(id+"F0.wireOp",EDGE,"E115")])],"isStart":false})],"blendedInto":[makeQuery(id+"F1.opExtrude","CAP_FACE",FACE,{"disambiguationData":[OSD([sQuery(id+"F0.wireOp",EDGE,"E0"),sQuery(id+"F0.wireOp",EDGE,"E1"),sQuery(id+"F0.wireOp",EDGE,"E2"),sQuery(id+"F0.wireOp",EDGE,"E3"),sQuery(id+"F0.wireOp",EDGE,"E4"),sQuery(id+"F0.wireOp",EDGE,"E5"),sQuery(id+"F0.wireOp",EDGE,"E6"),sQuery(id+"F0.wireOp",EDGE,"E7"),sQuery(id+"F0.wireOp",EDGE,"E8"),sQuery(id+"F0.wireOp",EDGE,"E9"),sQuery(id+"F0.wireOp",EDGE,"E10"),sQuery(id+"F0.wireOp",EDGE,"E11"),sQuery(id+"F0.wireOp",EDGE,"E12"),sQuery(id+"F0.wireOp",EDGE,"E13"),sQuery(id+"F0.wireOp",EDGE,"E14"),sQuery(id+"F0.wireOp",EDGE,"E15"),sQuery(id+"F0.wireOp",EDGE,"E16"),sQuery(id+"F0.wireOp",EDGE,"E17"),sQuery(id+"F0.wireOp",EDGE,"E18"),sQuery(id+"F0.wireOp",EDGE,"E19"),sQuery(id+"F0.wireOp",EDGE,"E20"),sQuery(id+"F0.wireOp",EDGE,"E21"),sQuery(id+"F0.wireOp",EDGE,"E22"),sQuery(id+"F0.wireOp",EDGE,"E23"),sQuery(id+"F0.wireOp",EDGE,"E24"),sQuery(id+"F0.wireOp",EDGE,"E25"),sQuery(id+"F0.wireOp",EDGE,"E26"),sQuery(id+"F0.wireOp",EDGE,"E27"),sQuery(id+"F0.wireOp",EDGE,"E28"),sQuery(id+"F0.wireOp",EDGE,"E29"),sQuery(id+"F0.wireOp",EDGE,"E30"),sQuery(id+"F0.wireOp",EDGE,"E31"),sQuery(id+"F0.wireOp",EDGE,"E32"),sQuery(id+"F0.wireOp",EDGE,"E33"),sQuery(id+"F0.wireOp",EDGE,"E34"),sQuery(id+"F0.wireOp",EDGE,"E35"),sQuery(id+"F0.wireOp",EDGE,"E36"),sQuery(id+"F0.wireOp",EDGE,"E37"),sQuery(id+"F0.wireOp",EDGE,"E38"),sQuery(id+"F0.wireOp",EDGE,"E39"),sQuery(id+"F0.wireOp",EDGE,"E40"),sQuery(id+"F0.wireOp",EDGE,"E41"),sQuery(id+"F0.wireOp",EDGE,"E42"),sQuery(id+"F0.wireOp",EDGE,"E43"),sQuery(id+"F0.wireOp",EDGE,"E44"),sQuery(id+"F0.wireOp",EDGE,"E45"),sQuery(id+"F0.wireOp",EDGE,"E46"),sQuery(id+"F0.wireOp",EDGE,"E47"),sQuery(id+"F0.wireOp",EDGE,"E48"),sQuery(id+"F0.wireOp",EDGE,"E49"),sQuery(id+"F0.wireOp",EDGE,"E50"),sQuery(id+"F0.wireOp",EDGE,"E51"),sQuery(id+"F0.wireOp",EDGE,"E52"),sQuery(id+"F0.wireOp",EDGE,"E53"),sQuery(id+"F0.wireOp",EDGE,"E54"),sQuery(id+"F0.wireOp",EDGE,"E55"),sQuery(id+"F0.wireOp",EDGE,"E56"),sQuery(id+"F0.wireOp",EDGE,"E57"),sQuery(id+"F0.wireOp",EDGE,"E58"),sQuery(id+"F0.wireOp",EDGE,"E59"),sQuery(id+"F0.wireOp",EDGE,"E60"),sQuery(id+"F0.wireOp",EDGE,"E61"),sQuery(id+"F0.wireOp",EDGE,"E62"),sQuery(id+"F0.wireOp",EDGE,"E63"),sQuery(id+"F0.wireOp",EDGE,"E64"),sQuery(id+"F0.wireOp",EDGE,"E65"),sQuery(id+"F0.wireOp",EDGE,"E66"),sQuery(id+"F0.wireOp",EDGE,"E67"),sQuery(id+"F0.wireOp",EDGE,"E68"),sQuery(id+"F0.wireOp",EDGE,"E69"),sQuery(id+"F0.wireOp",EDGE,"E70"),sQuery(id+"F0.wireOp",EDGE,"E71"),sQuery(id+"F0.wireOp",EDGE,"E72"),sQuery(id+"F0.wireOp",EDGE,"E73"),sQuery(id+"F0.wireOp",EDGE,"E74"),sQuery(id+"F0.wireOp",EDGE,"E75"),sQuery(id+"F0.wireOp",EDGE,"E76"),sQuery(id+"F0.wireOp",EDGE,"E77"),sQuery(id+"F0.wireOp",EDGE,"E78"),sQuery(id+"F0.wireOp",EDGE,"E79"),sQuery(id+"F0.wireOp",EDGE,"E80"),sQuery(id+"F0.wireOp",EDGE,"E81"),sQuery(id+"F0.wireOp",EDGE,"E82"),sQuery(id+"F0.wireOp",EDGE,"E83"),sQuery(id+"F0.wireOp",EDGE,"E84"),sQuery(id+"F0.wireOp",EDGE,"E85"),sQuery(id+"F0.wireOp",EDGE,"E86"),sQuery(id+"F0.wireOp",EDGE,"E87"),sQuery(id+"F0.wireOp",EDGE,"E88"),sQuery(id+"F0.wireOp",EDGE,"E89"),sQuery(id+"F0.wireOp",EDGE,"E90"),sQuery(id+"F0.wireOp",EDGE,"E91"),sQuery(id+"F0.wireOp",EDGE,"E92"),sQuery(id+"F0.wireOp",EDGE,"E93"),sQuery(id+"F0.wireOp",EDGE,"E94"),sQuery(id+"F0.wireOp",EDGE,"E95"),sQuery(id+"F0.wireOp",EDGE,"E96"),sQuery(id+"F0.wireOp",EDGE,"E97"),sQuery(id+"F0.wireOp",EDGE,"E98"),sQuery(id+"F0.wireOp",EDGE,"E99"),sQuery(id+"F0.wireOp",EDGE,"E100"),sQuery(id+"F0.wireOp",EDGE,"E101"),sQuery(id+"F0.wireOp",EDGE,"E102"),sQuery(id+"F0.wireOp",EDGE,"E103"),sQuery(id+"F0.wireOp",EDGE,"E104"),sQuery(id+"F0.wireOp",EDGE,"E105"),sQuery(id+"F0.wireOp",EDGE,"E106"),sQuery(id+"F0.wireOp",EDGE,"E107"),sQuery(id+"F0.wireOp",EDGE,"E108"),sQuery(id+"F0.wireOp",EDGE,"E109"),sQuery(id+"F0.wireOp",EDGE,"E110"),sQuery(id+"F0.wireOp",EDGE,"E111"),sQuery(id+"F0.wireOp",EDGE,"E112"),sQuery(id+"F0.wireOp",EDGE,"E113"),sQuery(id+"F0.wireOp",EDGE,"E114"),sQuery(id+"F0.wireOp",EDGE,"E115")])],"isStart":false})]});
            var Q22;
            Q22=makeQuery(id+"F6.opFillet","BLEND_EDGE",EDGE,{"blendedFrom":[makeQuery(id+"F5.boolean.opBoolean","COPY",EDGE,{"derivedFrom":makeQuery(id+"F5.opExtrude","CAP_EDGE",EDGE,{"disambiguationData":[OSD([sQuery(id+"F4.wireOp",EDGE,"E758.0.5.0")])],"isStart":false})}),makeQuery(id+"F1.opExtrude","CAP_FACE",FACE,{"disambiguationData":[OSD([sQuery(id+"F0.wireOp",EDGE,"E0"),sQuery(id+"F0.wireOp",EDGE,"E1"),sQuery(id+"F0.wireOp",EDGE,"E2"),sQuery(id+"F0.wireOp",EDGE,"E3"),sQuery(id+"F0.wireOp",EDGE,"E4"),sQuery(id+"F0.wireOp",EDGE,"E5"),sQuery(id+"F0.wireOp",EDGE,"E6"),sQuery(id+"F0.wireOp",EDGE,"E7"),sQuery(id+"F0.wireOp",EDGE,"E8"),sQuery(id+"F0.wireOp",EDGE,"E9"),sQuery(id+"F0.wireOp",EDGE,"E10"),sQuery(id+"F0.wireOp",EDGE,"E11"),sQuery(id+"F0.wireOp",EDGE,"E12"),sQuery(id+"F0.wireOp",EDGE,"E13"),sQuery(id+"F0.wireOp",EDGE,"E14"),sQuery(id+"F0.wireOp",EDGE,"E15"),sQuery(id+"F0.wireOp",EDGE,"E16"),sQuery(id+"F0.wireOp",EDGE,"E17"),sQuery(id+"F0.wireOp",EDGE,"E18"),sQuery(id+"F0.wireOp",EDGE,"E19"),sQuery(id+"F0.wireOp",EDGE,"E20"),sQuery(id+"F0.wireOp",EDGE,"E21"),sQuery(id+"F0.wireOp",EDGE,"E22"),sQuery(id+"F0.wireOp",EDGE,"E23"),sQuery(id+"F0.wireOp",EDGE,"E24"),sQuery(id+"F0.wireOp",EDGE,"E25"),sQuery(id+"F0.wireOp",EDGE,"E26"),sQuery(id+"F0.wireOp",EDGE,"E27"),sQuery(id+"F0.wireOp",EDGE,"E28"),sQuery(id+"F0.wireOp",EDGE,"E29"),sQuery(id+"F0.wireOp",EDGE,"E30"),sQuery(id+"F0.wireOp",EDGE,"E31"),sQuery(id+"F0.wireOp",EDGE,"E32"),sQuery(id+"F0.wireOp",EDGE,"E33"),sQuery(id+"F0.wireOp",EDGE,"E34"),sQuery(id+"F0.wireOp",EDGE,"E35"),sQuery(id+"F0.wireOp",EDGE,"E36"),sQuery(id+"F0.wireOp",EDGE,"E37"),sQuery(id+"F0.wireOp",EDGE,"E38"),sQuery(id+"F0.wireOp",EDGE,"E39"),sQuery(id+"F0.wireOp",EDGE,"E40"),sQuery(id+"F0.wireOp",EDGE,"E41"),sQuery(id+"F0.wireOp",EDGE,"E42"),sQuery(id+"F0.wireOp",EDGE,"E43"),sQuery(id+"F0.wireOp",EDGE,"E44"),sQuery(id+"F0.wireOp",EDGE,"E45"),sQuery(id+"F0.wireOp",EDGE,"E46"),sQuery(id+"F0.wireOp",EDGE,"E47"),sQuery(id+"F0.wireOp",EDGE,"E48"),sQuery(id+"F0.wireOp",EDGE,"E49"),sQuery(id+"F0.wireOp",EDGE,"E50"),sQuery(id+"F0.wireOp",EDGE,"E51"),sQuery(id+"F0.wireOp",EDGE,"E52"),sQuery(id+"F0.wireOp",EDGE,"E53"),sQuery(id+"F0.wireOp",EDGE,"E54"),sQuery(id+"F0.wireOp",EDGE,"E55"),sQuery(id+"F0.wireOp",EDGE,"E56"),sQuery(id+"F0.wireOp",EDGE,"E57"),sQuery(id+"F0.wireOp",EDGE,"E58"),sQuery(id+"F0.wireOp",EDGE,"E59"),sQuery(id+"F0.wireOp",EDGE,"E60"),sQuery(id+"F0.wireOp",EDGE,"E61"),sQuery(id+"F0.wireOp",EDGE,"E62"),sQuery(id+"F0.wireOp",EDGE,"E63"),sQuery(id+"F0.wireOp",EDGE,"E64"),sQuery(id+"F0.wireOp",EDGE,"E65"),sQuery(id+"F0.wireOp",EDGE,"E66"),sQuery(id+"F0.wireOp",EDGE,"E67"),sQuery(id+"F0.wireOp",EDGE,"E68"),sQuery(id+"F0.wireOp",EDGE,"E69"),sQuery(id+"F0.wireOp",EDGE,"E70"),sQuery(id+"F0.wireOp",EDGE,"E71"),sQuery(id+"F0.wireOp",EDGE,"E72"),sQuery(id+"F0.wireOp",EDGE,"E73"),sQuery(id+"F0.wireOp",EDGE,"E74"),sQuery(id+"F0.wireOp",EDGE,"E75"),sQuery(id+"F0.wireOp",EDGE,"E76"),sQuery(id+"F0.wireOp",EDGE,"E77"),sQuery(id+"F0.wireOp",EDGE,"E78"),sQuery(id+"F0.wireOp",EDGE,"E79"),sQuery(id+"F0.wireOp",EDGE,"E80"),sQuery(id+"F0.wireOp",EDGE,"E81"),sQuery(id+"F0.wireOp",EDGE,"E82"),sQuery(id+"F0.wireOp",EDGE,"E83"),sQuery(id+"F0.wireOp",EDGE,"E84"),sQuery(id+"F0.wireOp",EDGE,"E85"),sQuery(id+"F0.wireOp",EDGE,"E86"),sQuery(id+"F0.wireOp",EDGE,"E87"),sQuery(id+"F0.wireOp",EDGE,"E88"),sQuery(id+"F0.wireOp",EDGE,"E89"),sQuery(id+"F0.wireOp",EDGE,"E90"),sQuery(id+"F0.wireOp",EDGE,"E91"),sQuery(id+"F0.wireOp",EDGE,"E92"),sQuery(id+"F0.wireOp",EDGE,"E93"),sQuery(id+"F0.wireOp",EDGE,"E94"),sQuery(id+"F0.wireOp",EDGE,"E95"),sQuery(id+"F0.wireOp",EDGE,"E96"),sQuery(id+"F0.wireOp",EDGE,"E97"),sQuery(id+"F0.wireOp",EDGE,"E98"),sQuery(id+"F0.wireOp",EDGE,"E99"),sQuery(id+"F0.wireOp",EDGE,"E100"),sQuery(id+"F0.wireOp",EDGE,"E101"),sQuery(id+"F0.wireOp",EDGE,"E102"),sQuery(id+"F0.wireOp",EDGE,"E103"),sQuery(id+"F0.wireOp",EDGE,"E104"),sQuery(id+"F0.wireOp",EDGE,"E105"),sQuery(id+"F0.wireOp",EDGE,"E106"),sQuery(id+"F0.wireOp",EDGE,"E107"),sQuery(id+"F0.wireOp",EDGE,"E108"),sQuery(id+"F0.wireOp",EDGE,"E109"),sQuery(id+"F0.wireOp",EDGE,"E110"),sQuery(id+"F0.wireOp",EDGE,"E111"),sQuery(id+"F0.wireOp",EDGE,"E112"),sQuery(id+"F0.wireOp",EDGE,"E113"),sQuery(id+"F0.wireOp",EDGE,"E114"),sQuery(id+"F0.wireOp",EDGE,"E115")])],"isStart":false})],"blendedInto":[makeQuery(id+"F1.opExtrude","CAP_FACE",FACE,{"disambiguationData":[OSD([sQuery(id+"F0.wireOp",EDGE,"E0"),sQuery(id+"F0.wireOp",EDGE,"E1"),sQuery(id+"F0.wireOp",EDGE,"E2"),sQuery(id+"F0.wireOp",EDGE,"E3"),sQuery(id+"F0.wireOp",EDGE,"E4"),sQuery(id+"F0.wireOp",EDGE,"E5"),sQuery(id+"F0.wireOp",EDGE,"E6"),sQuery(id+"F0.wireOp",EDGE,"E7"),sQuery(id+"F0.wireOp",EDGE,"E8"),sQuery(id+"F0.wireOp",EDGE,"E9"),sQuery(id+"F0.wireOp",EDGE,"E10"),sQuery(id+"F0.wireOp",EDGE,"E11"),sQuery(id+"F0.wireOp",EDGE,"E12"),sQuery(id+"F0.wireOp",EDGE,"E13"),sQuery(id+"F0.wireOp",EDGE,"E14"),sQuery(id+"F0.wireOp",EDGE,"E15"),sQuery(id+"F0.wireOp",EDGE,"E16"),sQuery(id+"F0.wireOp",EDGE,"E17"),sQuery(id+"F0.wireOp",EDGE,"E18"),sQuery(id+"F0.wireOp",EDGE,"E19"),sQuery(id+"F0.wireOp",EDGE,"E20"),sQuery(id+"F0.wireOp",EDGE,"E21"),sQuery(id+"F0.wireOp",EDGE,"E22"),sQuery(id+"F0.wireOp",EDGE,"E23"),sQuery(id+"F0.wireOp",EDGE,"E24"),sQuery(id+"F0.wireOp",EDGE,"E25"),sQuery(id+"F0.wireOp",EDGE,"E26"),sQuery(id+"F0.wireOp",EDGE,"E27"),sQuery(id+"F0.wireOp",EDGE,"E28"),sQuery(id+"F0.wireOp",EDGE,"E29"),sQuery(id+"F0.wireOp",EDGE,"E30"),sQuery(id+"F0.wireOp",EDGE,"E31"),sQuery(id+"F0.wireOp",EDGE,"E32"),sQuery(id+"F0.wireOp",EDGE,"E33"),sQuery(id+"F0.wireOp",EDGE,"E34"),sQuery(id+"F0.wireOp",EDGE,"E35"),sQuery(id+"F0.wireOp",EDGE,"E36"),sQuery(id+"F0.wireOp",EDGE,"E37"),sQuery(id+"F0.wireOp",EDGE,"E38"),sQuery(id+"F0.wireOp",EDGE,"E39"),sQuery(id+"F0.wireOp",EDGE,"E40"),sQuery(id+"F0.wireOp",EDGE,"E41"),sQuery(id+"F0.wireOp",EDGE,"E42"),sQuery(id+"F0.wireOp",EDGE,"E43"),sQuery(id+"F0.wireOp",EDGE,"E44"),sQuery(id+"F0.wireOp",EDGE,"E45"),sQuery(id+"F0.wireOp",EDGE,"E46"),sQuery(id+"F0.wireOp",EDGE,"E47"),sQuery(id+"F0.wireOp",EDGE,"E48"),sQuery(id+"F0.wireOp",EDGE,"E49"),sQuery(id+"F0.wireOp",EDGE,"E50"),sQuery(id+"F0.wireOp",EDGE,"E51"),sQuery(id+"F0.wireOp",EDGE,"E52"),sQuery(id+"F0.wireOp",EDGE,"E53"),sQuery(id+"F0.wireOp",EDGE,"E54"),sQuery(id+"F0.wireOp",EDGE,"E55"),sQuery(id+"F0.wireOp",EDGE,"E56"),sQuery(id+"F0.wireOp",EDGE,"E57"),sQuery(id+"F0.wireOp",EDGE,"E58"),sQuery(id+"F0.wireOp",EDGE,"E59"),sQuery(id+"F0.wireOp",EDGE,"E60"),sQuery(id+"F0.wireOp",EDGE,"E61"),sQuery(id+"F0.wireOp",EDGE,"E62"),sQuery(id+"F0.wireOp",EDGE,"E63"),sQuery(id+"F0.wireOp",EDGE,"E64"),sQuery(id+"F0.wireOp",EDGE,"E65"),sQuery(id+"F0.wireOp",EDGE,"E66"),sQuery(id+"F0.wireOp",EDGE,"E67"),sQuery(id+"F0.wireOp",EDGE,"E68"),sQuery(id+"F0.wireOp",EDGE,"E69"),sQuery(id+"F0.wireOp",EDGE,"E70"),sQuery(id+"F0.wireOp",EDGE,"E71"),sQuery(id+"F0.wireOp",EDGE,"E72"),sQuery(id+"F0.wireOp",EDGE,"E73"),sQuery(id+"F0.wireOp",EDGE,"E74"),sQuery(id+"F0.wireOp",EDGE,"E75"),sQuery(id+"F0.wireOp",EDGE,"E76"),sQuery(id+"F0.wireOp",EDGE,"E77"),sQuery(id+"F0.wireOp",EDGE,"E78"),sQuery(id+"F0.wireOp",EDGE,"E79"),sQuery(id+"F0.wireOp",EDGE,"E80"),sQuery(id+"F0.wireOp",EDGE,"E81"),sQuery(id+"F0.wireOp",EDGE,"E82"),sQuery(id+"F0.wireOp",EDGE,"E83"),sQuery(id+"F0.wireOp",EDGE,"E84"),sQuery(id+"F0.wireOp",EDGE,"E85"),sQuery(id+"F0.wireOp",EDGE,"E86"),sQuery(id+"F0.wireOp",EDGE,"E87"),sQuery(id+"F0.wireOp",EDGE,"E88"),sQuery(id+"F0.wireOp",EDGE,"E89"),sQuery(id+"F0.wireOp",EDGE,"E90"),sQuery(id+"F0.wireOp",EDGE,"E91"),sQuery(id+"F0.wireOp",EDGE,"E92"),sQuery(id+"F0.wireOp",EDGE,"E93"),sQuery(id+"F0.wireOp",EDGE,"E94"),sQuery(id+"F0.wireOp",EDGE,"E95"),sQuery(id+"F0.wireOp",EDGE,"E96"),sQuery(id+"F0.wireOp",EDGE,"E97"),sQuery(id+"F0.wireOp",EDGE,"E98"),sQuery(id+"F0.wireOp",EDGE,"E99"),sQuery(id+"F0.wireOp",EDGE,"E100"),sQuery(id+"F0.wireOp",EDGE,"E101"),sQuery(id+"F0.wireOp",EDGE,"E102"),sQuery(id+"F0.wireOp",EDGE,"E103"),sQuery(id+"F0.wireOp",EDGE,"E104"),sQuery(id+"F0.wireOp",EDGE,"E105"),sQuery(id+"F0.wireOp",EDGE,"E106"),sQuery(id+"F0.wireOp",EDGE,"E107"),sQuery(id+"F0.wireOp",EDGE,"E108"),sQuery(id+"F0.wireOp",EDGE,"E109"),sQuery(id+"F0.wireOp",EDGE,"E110"),sQuery(id+"F0.wireOp",EDGE,"E111"),sQuery(id+"F0.wireOp",EDGE,"E112"),sQuery(id+"F0.wireOp",EDGE,"E113"),sQuery(id+"F0.wireOp",EDGE,"E114"),sQuery(id+"F0.wireOp",EDGE,"E115")])],"isStart":false})]});
            var Q23;
            Q23=makeQuery(id+"F6.opFillet","BLEND_EDGE",EDGE,{"blendedFrom":[makeQuery(id+"F5.boolean.opBoolean","COPY",EDGE,{"derivedFrom":makeQuery(id+"F5.opExtrude","CAP_EDGE",EDGE,{"disambiguationData":[OSD([sQuery(id+"F4.wireOp",EDGE,"E758.0.5.3")])],"isStart":false})}),makeQuery(id+"F1.opExtrude","CAP_FACE",FACE,{"disambiguationData":[OSD([sQuery(id+"F0.wireOp",EDGE,"E0"),sQuery(id+"F0.wireOp",EDGE,"E1"),sQuery(id+"F0.wireOp",EDGE,"E2"),sQuery(id+"F0.wireOp",EDGE,"E3"),sQuery(id+"F0.wireOp",EDGE,"E4"),sQuery(id+"F0.wireOp",EDGE,"E5"),sQuery(id+"F0.wireOp",EDGE,"E6"),sQuery(id+"F0.wireOp",EDGE,"E7"),sQuery(id+"F0.wireOp",EDGE,"E8"),sQuery(id+"F0.wireOp",EDGE,"E9"),sQuery(id+"F0.wireOp",EDGE,"E10"),sQuery(id+"F0.wireOp",EDGE,"E11"),sQuery(id+"F0.wireOp",EDGE,"E12"),sQuery(id+"F0.wireOp",EDGE,"E13"),sQuery(id+"F0.wireOp",EDGE,"E14"),sQuery(id+"F0.wireOp",EDGE,"E15"),sQuery(id+"F0.wireOp",EDGE,"E16"),sQuery(id+"F0.wireOp",EDGE,"E17"),sQuery(id+"F0.wireOp",EDGE,"E18"),sQuery(id+"F0.wireOp",EDGE,"E19"),sQuery(id+"F0.wireOp",EDGE,"E20"),sQuery(id+"F0.wireOp",EDGE,"E21"),sQuery(id+"F0.wireOp",EDGE,"E22"),sQuery(id+"F0.wireOp",EDGE,"E23"),sQuery(id+"F0.wireOp",EDGE,"E24"),sQuery(id+"F0.wireOp",EDGE,"E25"),sQuery(id+"F0.wireOp",EDGE,"E26"),sQuery(id+"F0.wireOp",EDGE,"E27"),sQuery(id+"F0.wireOp",EDGE,"E28"),sQuery(id+"F0.wireOp",EDGE,"E29"),sQuery(id+"F0.wireOp",EDGE,"E30"),sQuery(id+"F0.wireOp",EDGE,"E31"),sQuery(id+"F0.wireOp",EDGE,"E32"),sQuery(id+"F0.wireOp",EDGE,"E33"),sQuery(id+"F0.wireOp",EDGE,"E34"),sQuery(id+"F0.wireOp",EDGE,"E35"),sQuery(id+"F0.wireOp",EDGE,"E36"),sQuery(id+"F0.wireOp",EDGE,"E37"),sQuery(id+"F0.wireOp",EDGE,"E38"),sQuery(id+"F0.wireOp",EDGE,"E39"),sQuery(id+"F0.wireOp",EDGE,"E40"),sQuery(id+"F0.wireOp",EDGE,"E41"),sQuery(id+"F0.wireOp",EDGE,"E42"),sQuery(id+"F0.wireOp",EDGE,"E43"),sQuery(id+"F0.wireOp",EDGE,"E44"),sQuery(id+"F0.wireOp",EDGE,"E45"),sQuery(id+"F0.wireOp",EDGE,"E46"),sQuery(id+"F0.wireOp",EDGE,"E47"),sQuery(id+"F0.wireOp",EDGE,"E48"),sQuery(id+"F0.wireOp",EDGE,"E49"),sQuery(id+"F0.wireOp",EDGE,"E50"),sQuery(id+"F0.wireOp",EDGE,"E51"),sQuery(id+"F0.wireOp",EDGE,"E52"),sQuery(id+"F0.wireOp",EDGE,"E53"),sQuery(id+"F0.wireOp",EDGE,"E54"),sQuery(id+"F0.wireOp",EDGE,"E55"),sQuery(id+"F0.wireOp",EDGE,"E56"),sQuery(id+"F0.wireOp",EDGE,"E57"),sQuery(id+"F0.wireOp",EDGE,"E58"),sQuery(id+"F0.wireOp",EDGE,"E59"),sQuery(id+"F0.wireOp",EDGE,"E60"),sQuery(id+"F0.wireOp",EDGE,"E61"),sQuery(id+"F0.wireOp",EDGE,"E62"),sQuery(id+"F0.wireOp",EDGE,"E63"),sQuery(id+"F0.wireOp",EDGE,"E64"),sQuery(id+"F0.wireOp",EDGE,"E65"),sQuery(id+"F0.wireOp",EDGE,"E66"),sQuery(id+"F0.wireOp",EDGE,"E67"),sQuery(id+"F0.wireOp",EDGE,"E68"),sQuery(id+"F0.wireOp",EDGE,"E69"),sQuery(id+"F0.wireOp",EDGE,"E70"),sQuery(id+"F0.wireOp",EDGE,"E71"),sQuery(id+"F0.wireOp",EDGE,"E72"),sQuery(id+"F0.wireOp",EDGE,"E73"),sQuery(id+"F0.wireOp",EDGE,"E74"),sQuery(id+"F0.wireOp",EDGE,"E75"),sQuery(id+"F0.wireOp",EDGE,"E76"),sQuery(id+"F0.wireOp",EDGE,"E77"),sQuery(id+"F0.wireOp",EDGE,"E78"),sQuery(id+"F0.wireOp",EDGE,"E79"),sQuery(id+"F0.wireOp",EDGE,"E80"),sQuery(id+"F0.wireOp",EDGE,"E81"),sQuery(id+"F0.wireOp",EDGE,"E82"),sQuery(id+"F0.wireOp",EDGE,"E83"),sQuery(id+"F0.wireOp",EDGE,"E84"),sQuery(id+"F0.wireOp",EDGE,"E85"),sQuery(id+"F0.wireOp",EDGE,"E86"),sQuery(id+"F0.wireOp",EDGE,"E87"),sQuery(id+"F0.wireOp",EDGE,"E88"),sQuery(id+"F0.wireOp",EDGE,"E89"),sQuery(id+"F0.wireOp",EDGE,"E90"),sQuery(id+"F0.wireOp",EDGE,"E91"),sQuery(id+"F0.wireOp",EDGE,"E92"),sQuery(id+"F0.wireOp",EDGE,"E93"),sQuery(id+"F0.wireOp",EDGE,"E94"),sQuery(id+"F0.wireOp",EDGE,"E95"),sQuery(id+"F0.wireOp",EDGE,"E96"),sQuery(id+"F0.wireOp",EDGE,"E97"),sQuery(id+"F0.wireOp",EDGE,"E98"),sQuery(id+"F0.wireOp",EDGE,"E99"),sQuery(id+"F0.wireOp",EDGE,"E100"),sQuery(id+"F0.wireOp",EDGE,"E101"),sQuery(id+"F0.wireOp",EDGE,"E102"),sQuery(id+"F0.wireOp",EDGE,"E103"),sQuery(id+"F0.wireOp",EDGE,"E104"),sQuery(id+"F0.wireOp",EDGE,"E105"),sQuery(id+"F0.wireOp",EDGE,"E106"),sQuery(id+"F0.wireOp",EDGE,"E107"),sQuery(id+"F0.wireOp",EDGE,"E108"),sQuery(id+"F0.wireOp",EDGE,"E109"),sQuery(id+"F0.wireOp",EDGE,"E110"),sQuery(id+"F0.wireOp",EDGE,"E111"),sQuery(id+"F0.wireOp",EDGE,"E112"),sQuery(id+"F0.wireOp",EDGE,"E113"),sQuery(id+"F0.wireOp",EDGE,"E114"),sQuery(id+"F0.wireOp",EDGE,"E115")])],"isStart":false})],"blendedInto":[makeQuery(id+"F1.opExtrude","CAP_FACE",FACE,{"disambiguationData":[OSD([sQuery(id+"F0.wireOp",EDGE,"E0"),sQuery(id+"F0.wireOp",EDGE,"E1"),sQuery(id+"F0.wireOp",EDGE,"E2"),sQuery(id+"F0.wireOp",EDGE,"E3"),sQuery(id+"F0.wireOp",EDGE,"E4"),sQuery(id+"F0.wireOp",EDGE,"E5"),sQuery(id+"F0.wireOp",EDGE,"E6"),sQuery(id+"F0.wireOp",EDGE,"E7"),sQuery(id+"F0.wireOp",EDGE,"E8"),sQuery(id+"F0.wireOp",EDGE,"E9"),sQuery(id+"F0.wireOp",EDGE,"E10"),sQuery(id+"F0.wireOp",EDGE,"E11"),sQuery(id+"F0.wireOp",EDGE,"E12"),sQuery(id+"F0.wireOp",EDGE,"E13"),sQuery(id+"F0.wireOp",EDGE,"E14"),sQuery(id+"F0.wireOp",EDGE,"E15"),sQuery(id+"F0.wireOp",EDGE,"E16"),sQuery(id+"F0.wireOp",EDGE,"E17"),sQuery(id+"F0.wireOp",EDGE,"E18"),sQuery(id+"F0.wireOp",EDGE,"E19"),sQuery(id+"F0.wireOp",EDGE,"E20"),sQuery(id+"F0.wireOp",EDGE,"E21"),sQuery(id+"F0.wireOp",EDGE,"E22"),sQuery(id+"F0.wireOp",EDGE,"E23"),sQuery(id+"F0.wireOp",EDGE,"E24"),sQuery(id+"F0.wireOp",EDGE,"E25"),sQuery(id+"F0.wireOp",EDGE,"E26"),sQuery(id+"F0.wireOp",EDGE,"E27"),sQuery(id+"F0.wireOp",EDGE,"E28"),sQuery(id+"F0.wireOp",EDGE,"E29"),sQuery(id+"F0.wireOp",EDGE,"E30"),sQuery(id+"F0.wireOp",EDGE,"E31"),sQuery(id+"F0.wireOp",EDGE,"E32"),sQuery(id+"F0.wireOp",EDGE,"E33"),sQuery(id+"F0.wireOp",EDGE,"E34"),sQuery(id+"F0.wireOp",EDGE,"E35"),sQuery(id+"F0.wireOp",EDGE,"E36"),sQuery(id+"F0.wireOp",EDGE,"E37"),sQuery(id+"F0.wireOp",EDGE,"E38"),sQuery(id+"F0.wireOp",EDGE,"E39"),sQuery(id+"F0.wireOp",EDGE,"E40"),sQuery(id+"F0.wireOp",EDGE,"E41"),sQuery(id+"F0.wireOp",EDGE,"E42"),sQuery(id+"F0.wireOp",EDGE,"E43"),sQuery(id+"F0.wireOp",EDGE,"E44"),sQuery(id+"F0.wireOp",EDGE,"E45"),sQuery(id+"F0.wireOp",EDGE,"E46"),sQuery(id+"F0.wireOp",EDGE,"E47"),sQuery(id+"F0.wireOp",EDGE,"E48"),sQuery(id+"F0.wireOp",EDGE,"E49"),sQuery(id+"F0.wireOp",EDGE,"E50"),sQuery(id+"F0.wireOp",EDGE,"E51"),sQuery(id+"F0.wireOp",EDGE,"E52"),sQuery(id+"F0.wireOp",EDGE,"E53"),sQuery(id+"F0.wireOp",EDGE,"E54"),sQuery(id+"F0.wireOp",EDGE,"E55"),sQuery(id+"F0.wireOp",EDGE,"E56"),sQuery(id+"F0.wireOp",EDGE,"E57"),sQuery(id+"F0.wireOp",EDGE,"E58"),sQuery(id+"F0.wireOp",EDGE,"E59"),sQuery(id+"F0.wireOp",EDGE,"E60"),sQuery(id+"F0.wireOp",EDGE,"E61"),sQuery(id+"F0.wireOp",EDGE,"E62"),sQuery(id+"F0.wireOp",EDGE,"E63"),sQuery(id+"F0.wireOp",EDGE,"E64"),sQuery(id+"F0.wireOp",EDGE,"E65"),sQuery(id+"F0.wireOp",EDGE,"E66"),sQuery(id+"F0.wireOp",EDGE,"E67"),sQuery(id+"F0.wireOp",EDGE,"E68"),sQuery(id+"F0.wireOp",EDGE,"E69"),sQuery(id+"F0.wireOp",EDGE,"E70"),sQuery(id+"F0.wireOp",EDGE,"E71"),sQuery(id+"F0.wireOp",EDGE,"E72"),sQuery(id+"F0.wireOp",EDGE,"E73"),sQuery(id+"F0.wireOp",EDGE,"E74"),sQuery(id+"F0.wireOp",EDGE,"E75"),sQuery(id+"F0.wireOp",EDGE,"E76"),sQuery(id+"F0.wireOp",EDGE,"E77"),sQuery(id+"F0.wireOp",EDGE,"E78"),sQuery(id+"F0.wireOp",EDGE,"E79"),sQuery(id+"F0.wireOp",EDGE,"E80"),sQuery(id+"F0.wireOp",EDGE,"E81"),sQuery(id+"F0.wireOp",EDGE,"E82"),sQuery(id+"F0.wireOp",EDGE,"E83"),sQuery(id+"F0.wireOp",EDGE,"E84"),sQuery(id+"F0.wireOp",EDGE,"E85"),sQuery(id+"F0.wireOp",EDGE,"E86"),sQuery(id+"F0.wireOp",EDGE,"E87"),sQuery(id+"F0.wireOp",EDGE,"E88"),sQuery(id+"F0.wireOp",EDGE,"E89"),sQuery(id+"F0.wireOp",EDGE,"E90"),sQuery(id+"F0.wireOp",EDGE,"E91"),sQuery(id+"F0.wireOp",EDGE,"E92"),sQuery(id+"F0.wireOp",EDGE,"E93"),sQuery(id+"F0.wireOp",EDGE,"E94"),sQuery(id+"F0.wireOp",EDGE,"E95"),sQuery(id+"F0.wireOp",EDGE,"E96"),sQuery(id+"F0.wireOp",EDGE,"E97"),sQuery(id+"F0.wireOp",EDGE,"E98"),sQuery(id+"F0.wireOp",EDGE,"E99"),sQuery(id+"F0.wireOp",EDGE,"E100"),sQuery(id+"F0.wireOp",EDGE,"E101"),sQuery(id+"F0.wireOp",EDGE,"E102"),sQuery(id+"F0.wireOp",EDGE,"E103"),sQuery(id+"F0.wireOp",EDGE,"E104"),sQuery(id+"F0.wireOp",EDGE,"E105"),sQuery(id+"F0.wireOp",EDGE,"E106"),sQuery(id+"F0.wireOp",EDGE,"E107"),sQuery(id+"F0.wireOp",EDGE,"E108"),sQuery(id+"F0.wireOp",EDGE,"E109"),sQuery(id+"F0.wireOp",EDGE,"E110"),sQuery(id+"F0.wireOp",EDGE,"E111"),sQuery(id+"F0.wireOp",EDGE,"E112"),sQuery(id+"F0.wireOp",EDGE,"E113"),sQuery(id+"F0.wireOp",EDGE,"E114"),sQuery(id+"F0.wireOp",EDGE,"E115")])],"isStart":false})]});
            var Q24;
            Q24=makeQuery(id+"F6.opFillet","BLEND_EDGE",EDGE,{"blendedFrom":[makeQuery(id+"F5.boolean.opBoolean","COPY",EDGE,{"derivedFrom":makeQuery(id+"F5.opExtrude","CAP_EDGE",EDGE,{"disambiguationData":[OSD([sQuery(id+"F4.wireOp",EDGE,"E759.0.5.4")])],"isStart":false})}),makeQuery(id+"F1.opExtrude","CAP_FACE",FACE,{"disambiguationData":[OSD([sQuery(id+"F0.wireOp",EDGE,"E0"),sQuery(id+"F0.wireOp",EDGE,"E1"),sQuery(id+"F0.wireOp",EDGE,"E2"),sQuery(id+"F0.wireOp",EDGE,"E3"),sQuery(id+"F0.wireOp",EDGE,"E4"),sQuery(id+"F0.wireOp",EDGE,"E5"),sQuery(id+"F0.wireOp",EDGE,"E6"),sQuery(id+"F0.wireOp",EDGE,"E7"),sQuery(id+"F0.wireOp",EDGE,"E8"),sQuery(id+"F0.wireOp",EDGE,"E9"),sQuery(id+"F0.wireOp",EDGE,"E10"),sQuery(id+"F0.wireOp",EDGE,"E11"),sQuery(id+"F0.wireOp",EDGE,"E12"),sQuery(id+"F0.wireOp",EDGE,"E13"),sQuery(id+"F0.wireOp",EDGE,"E14"),sQuery(id+"F0.wireOp",EDGE,"E15"),sQuery(id+"F0.wireOp",EDGE,"E16"),sQuery(id+"F0.wireOp",EDGE,"E17"),sQuery(id+"F0.wireOp",EDGE,"E18"),sQuery(id+"F0.wireOp",EDGE,"E19"),sQuery(id+"F0.wireOp",EDGE,"E20"),sQuery(id+"F0.wireOp",EDGE,"E21"),sQuery(id+"F0.wireOp",EDGE,"E22"),sQuery(id+"F0.wireOp",EDGE,"E23"),sQuery(id+"F0.wireOp",EDGE,"E24"),sQuery(id+"F0.wireOp",EDGE,"E25"),sQuery(id+"F0.wireOp",EDGE,"E26"),sQuery(id+"F0.wireOp",EDGE,"E27"),sQuery(id+"F0.wireOp",EDGE,"E28"),sQuery(id+"F0.wireOp",EDGE,"E29"),sQuery(id+"F0.wireOp",EDGE,"E30"),sQuery(id+"F0.wireOp",EDGE,"E31"),sQuery(id+"F0.wireOp",EDGE,"E32"),sQuery(id+"F0.wireOp",EDGE,"E33"),sQuery(id+"F0.wireOp",EDGE,"E34"),sQuery(id+"F0.wireOp",EDGE,"E35"),sQuery(id+"F0.wireOp",EDGE,"E36"),sQuery(id+"F0.wireOp",EDGE,"E37"),sQuery(id+"F0.wireOp",EDGE,"E38"),sQuery(id+"F0.wireOp",EDGE,"E39"),sQuery(id+"F0.wireOp",EDGE,"E40"),sQuery(id+"F0.wireOp",EDGE,"E41"),sQuery(id+"F0.wireOp",EDGE,"E42"),sQuery(id+"F0.wireOp",EDGE,"E43"),sQuery(id+"F0.wireOp",EDGE,"E44"),sQuery(id+"F0.wireOp",EDGE,"E45"),sQuery(id+"F0.wireOp",EDGE,"E46"),sQuery(id+"F0.wireOp",EDGE,"E47"),sQuery(id+"F0.wireOp",EDGE,"E48"),sQuery(id+"F0.wireOp",EDGE,"E49"),sQuery(id+"F0.wireOp",EDGE,"E50"),sQuery(id+"F0.wireOp",EDGE,"E51"),sQuery(id+"F0.wireOp",EDGE,"E52"),sQuery(id+"F0.wireOp",EDGE,"E53"),sQuery(id+"F0.wireOp",EDGE,"E54"),sQuery(id+"F0.wireOp",EDGE,"E55"),sQuery(id+"F0.wireOp",EDGE,"E56"),sQuery(id+"F0.wireOp",EDGE,"E57"),sQuery(id+"F0.wireOp",EDGE,"E58"),sQuery(id+"F0.wireOp",EDGE,"E59"),sQuery(id+"F0.wireOp",EDGE,"E60"),sQuery(id+"F0.wireOp",EDGE,"E61"),sQuery(id+"F0.wireOp",EDGE,"E62"),sQuery(id+"F0.wireOp",EDGE,"E63"),sQuery(id+"F0.wireOp",EDGE,"E64"),sQuery(id+"F0.wireOp",EDGE,"E65"),sQuery(id+"F0.wireOp",EDGE,"E66"),sQuery(id+"F0.wireOp",EDGE,"E67"),sQuery(id+"F0.wireOp",EDGE,"E68"),sQuery(id+"F0.wireOp",EDGE,"E69"),sQuery(id+"F0.wireOp",EDGE,"E70"),sQuery(id+"F0.wireOp",EDGE,"E71"),sQuery(id+"F0.wireOp",EDGE,"E72"),sQuery(id+"F0.wireOp",EDGE,"E73"),sQuery(id+"F0.wireOp",EDGE,"E74"),sQuery(id+"F0.wireOp",EDGE,"E75"),sQuery(id+"F0.wireOp",EDGE,"E76"),sQuery(id+"F0.wireOp",EDGE,"E77"),sQuery(id+"F0.wireOp",EDGE,"E78"),sQuery(id+"F0.wireOp",EDGE,"E79"),sQuery(id+"F0.wireOp",EDGE,"E80"),sQuery(id+"F0.wireOp",EDGE,"E81"),sQuery(id+"F0.wireOp",EDGE,"E82"),sQuery(id+"F0.wireOp",EDGE,"E83"),sQuery(id+"F0.wireOp",EDGE,"E84"),sQuery(id+"F0.wireOp",EDGE,"E85"),sQuery(id+"F0.wireOp",EDGE,"E86"),sQuery(id+"F0.wireOp",EDGE,"E87"),sQuery(id+"F0.wireOp",EDGE,"E88"),sQuery(id+"F0.wireOp",EDGE,"E89"),sQuery(id+"F0.wireOp",EDGE,"E90"),sQuery(id+"F0.wireOp",EDGE,"E91"),sQuery(id+"F0.wireOp",EDGE,"E92"),sQuery(id+"F0.wireOp",EDGE,"E93"),sQuery(id+"F0.wireOp",EDGE,"E94"),sQuery(id+"F0.wireOp",EDGE,"E95"),sQuery(id+"F0.wireOp",EDGE,"E96"),sQuery(id+"F0.wireOp",EDGE,"E97"),sQuery(id+"F0.wireOp",EDGE,"E98"),sQuery(id+"F0.wireOp",EDGE,"E99"),sQuery(id+"F0.wireOp",EDGE,"E100"),sQuery(id+"F0.wireOp",EDGE,"E101"),sQuery(id+"F0.wireOp",EDGE,"E102"),sQuery(id+"F0.wireOp",EDGE,"E103"),sQuery(id+"F0.wireOp",EDGE,"E104"),sQuery(id+"F0.wireOp",EDGE,"E105"),sQuery(id+"F0.wireOp",EDGE,"E106"),sQuery(id+"F0.wireOp",EDGE,"E107"),sQuery(id+"F0.wireOp",EDGE,"E108"),sQuery(id+"F0.wireOp",EDGE,"E109"),sQuery(id+"F0.wireOp",EDGE,"E110"),sQuery(id+"F0.wireOp",EDGE,"E111"),sQuery(id+"F0.wireOp",EDGE,"E112"),sQuery(id+"F0.wireOp",EDGE,"E113"),sQuery(id+"F0.wireOp",EDGE,"E114"),sQuery(id+"F0.wireOp",EDGE,"E115")])],"isStart":false})],"blendedInto":[makeQuery(id+"F1.opExtrude","CAP_FACE",FACE,{"disambiguationData":[OSD([sQuery(id+"F0.wireOp",EDGE,"E0"),sQuery(id+"F0.wireOp",EDGE,"E1"),sQuery(id+"F0.wireOp",EDGE,"E2"),sQuery(id+"F0.wireOp",EDGE,"E3"),sQuery(id+"F0.wireOp",EDGE,"E4"),sQuery(id+"F0.wireOp",EDGE,"E5"),sQuery(id+"F0.wireOp",EDGE,"E6"),sQuery(id+"F0.wireOp",EDGE,"E7"),sQuery(id+"F0.wireOp",EDGE,"E8"),sQuery(id+"F0.wireOp",EDGE,"E9"),sQuery(id+"F0.wireOp",EDGE,"E10"),sQuery(id+"F0.wireOp",EDGE,"E11"),sQuery(id+"F0.wireOp",EDGE,"E12"),sQuery(id+"F0.wireOp",EDGE,"E13"),sQuery(id+"F0.wireOp",EDGE,"E14"),sQuery(id+"F0.wireOp",EDGE,"E15"),sQuery(id+"F0.wireOp",EDGE,"E16"),sQuery(id+"F0.wireOp",EDGE,"E17"),sQuery(id+"F0.wireOp",EDGE,"E18"),sQuery(id+"F0.wireOp",EDGE,"E19"),sQuery(id+"F0.wireOp",EDGE,"E20"),sQuery(id+"F0.wireOp",EDGE,"E21"),sQuery(id+"F0.wireOp",EDGE,"E22"),sQuery(id+"F0.wireOp",EDGE,"E23"),sQuery(id+"F0.wireOp",EDGE,"E24"),sQuery(id+"F0.wireOp",EDGE,"E25"),sQuery(id+"F0.wireOp",EDGE,"E26"),sQuery(id+"F0.wireOp",EDGE,"E27"),sQuery(id+"F0.wireOp",EDGE,"E28"),sQuery(id+"F0.wireOp",EDGE,"E29"),sQuery(id+"F0.wireOp",EDGE,"E30"),sQuery(id+"F0.wireOp",EDGE,"E31"),sQuery(id+"F0.wireOp",EDGE,"E32"),sQuery(id+"F0.wireOp",EDGE,"E33"),sQuery(id+"F0.wireOp",EDGE,"E34"),sQuery(id+"F0.wireOp",EDGE,"E35"),sQuery(id+"F0.wireOp",EDGE,"E36"),sQuery(id+"F0.wireOp",EDGE,"E37"),sQuery(id+"F0.wireOp",EDGE,"E38"),sQuery(id+"F0.wireOp",EDGE,"E39"),sQuery(id+"F0.wireOp",EDGE,"E40"),sQuery(id+"F0.wireOp",EDGE,"E41"),sQuery(id+"F0.wireOp",EDGE,"E42"),sQuery(id+"F0.wireOp",EDGE,"E43"),sQuery(id+"F0.wireOp",EDGE,"E44"),sQuery(id+"F0.wireOp",EDGE,"E45"),sQuery(id+"F0.wireOp",EDGE,"E46"),sQuery(id+"F0.wireOp",EDGE,"E47"),sQuery(id+"F0.wireOp",EDGE,"E48"),sQuery(id+"F0.wireOp",EDGE,"E49"),sQuery(id+"F0.wireOp",EDGE,"E50"),sQuery(id+"F0.wireOp",EDGE,"E51"),sQuery(id+"F0.wireOp",EDGE,"E52"),sQuery(id+"F0.wireOp",EDGE,"E53"),sQuery(id+"F0.wireOp",EDGE,"E54"),sQuery(id+"F0.wireOp",EDGE,"E55"),sQuery(id+"F0.wireOp",EDGE,"E56"),sQuery(id+"F0.wireOp",EDGE,"E57"),sQuery(id+"F0.wireOp",EDGE,"E58"),sQuery(id+"F0.wireOp",EDGE,"E59"),sQuery(id+"F0.wireOp",EDGE,"E60"),sQuery(id+"F0.wireOp",EDGE,"E61"),sQuery(id+"F0.wireOp",EDGE,"E62"),sQuery(id+"F0.wireOp",EDGE,"E63"),sQuery(id+"F0.wireOp",EDGE,"E64"),sQuery(id+"F0.wireOp",EDGE,"E65"),sQuery(id+"F0.wireOp",EDGE,"E66"),sQuery(id+"F0.wireOp",EDGE,"E67"),sQuery(id+"F0.wireOp",EDGE,"E68"),sQuery(id+"F0.wireOp",EDGE,"E69"),sQuery(id+"F0.wireOp",EDGE,"E70"),sQuery(id+"F0.wireOp",EDGE,"E71"),sQuery(id+"F0.wireOp",EDGE,"E72"),sQuery(id+"F0.wireOp",EDGE,"E73"),sQuery(id+"F0.wireOp",EDGE,"E74"),sQuery(id+"F0.wireOp",EDGE,"E75"),sQuery(id+"F0.wireOp",EDGE,"E76"),sQuery(id+"F0.wireOp",EDGE,"E77"),sQuery(id+"F0.wireOp",EDGE,"E78"),sQuery(id+"F0.wireOp",EDGE,"E79"),sQuery(id+"F0.wireOp",EDGE,"E80"),sQuery(id+"F0.wireOp",EDGE,"E81"),sQuery(id+"F0.wireOp",EDGE,"E82"),sQuery(id+"F0.wireOp",EDGE,"E83"),sQuery(id+"F0.wireOp",EDGE,"E84"),sQuery(id+"F0.wireOp",EDGE,"E85"),sQuery(id+"F0.wireOp",EDGE,"E86"),sQuery(id+"F0.wireOp",EDGE,"E87"),sQuery(id+"F0.wireOp",EDGE,"E88"),sQuery(id+"F0.wireOp",EDGE,"E89"),sQuery(id+"F0.wireOp",EDGE,"E90"),sQuery(id+"F0.wireOp",EDGE,"E91"),sQuery(id+"F0.wireOp",EDGE,"E92"),sQuery(id+"F0.wireOp",EDGE,"E93"),sQuery(id+"F0.wireOp",EDGE,"E94"),sQuery(id+"F0.wireOp",EDGE,"E95"),sQuery(id+"F0.wireOp",EDGE,"E96"),sQuery(id+"F0.wireOp",EDGE,"E97"),sQuery(id+"F0.wireOp",EDGE,"E98"),sQuery(id+"F0.wireOp",EDGE,"E99"),sQuery(id+"F0.wireOp",EDGE,"E100"),sQuery(id+"F0.wireOp",EDGE,"E101"),sQuery(id+"F0.wireOp",EDGE,"E102"),sQuery(id+"F0.wireOp",EDGE,"E103"),sQuery(id+"F0.wireOp",EDGE,"E104"),sQuery(id+"F0.wireOp",EDGE,"E105"),sQuery(id+"F0.wireOp",EDGE,"E106"),sQuery(id+"F0.wireOp",EDGE,"E107"),sQuery(id+"F0.wireOp",EDGE,"E108"),sQuery(id+"F0.wireOp",EDGE,"E109"),sQuery(id+"F0.wireOp",EDGE,"E110"),sQuery(id+"F0.wireOp",EDGE,"E111"),sQuery(id+"F0.wireOp",EDGE,"E112"),sQuery(id+"F0.wireOp",EDGE,"E113"),sQuery(id+"F0.wireOp",EDGE,"E114"),sQuery(id+"F0.wireOp",EDGE,"E115")])],"isStart":false})]});
            var Q25;
            Q25=makeQuery(id+"F6.opFillet","BLEND_EDGE",EDGE,{"blendedFrom":[makeQuery(id+"F5.boolean.opBoolean","COPY",EDGE,{"derivedFrom":makeQuery(id+"F5.opExtrude","CAP_EDGE",EDGE,{"disambiguationData":[OSD([sQuery(id+"F4.wireOp",EDGE,"E759.0.4.4")])],"isStart":false})}),makeQuery(id+"F1.opExtrude","CAP_FACE",FACE,{"disambiguationData":[OSD([sQuery(id+"F0.wireOp",EDGE,"E0"),sQuery(id+"F0.wireOp",EDGE,"E1"),sQuery(id+"F0.wireOp",EDGE,"E2"),sQuery(id+"F0.wireOp",EDGE,"E3"),sQuery(id+"F0.wireOp",EDGE,"E4"),sQuery(id+"F0.wireOp",EDGE,"E5"),sQuery(id+"F0.wireOp",EDGE,"E6"),sQuery(id+"F0.wireOp",EDGE,"E7"),sQuery(id+"F0.wireOp",EDGE,"E8"),sQuery(id+"F0.wireOp",EDGE,"E9"),sQuery(id+"F0.wireOp",EDGE,"E10"),sQuery(id+"F0.wireOp",EDGE,"E11"),sQuery(id+"F0.wireOp",EDGE,"E12"),sQuery(id+"F0.wireOp",EDGE,"E13"),sQuery(id+"F0.wireOp",EDGE,"E14"),sQuery(id+"F0.wireOp",EDGE,"E15"),sQuery(id+"F0.wireOp",EDGE,"E16"),sQuery(id+"F0.wireOp",EDGE,"E17"),sQuery(id+"F0.wireOp",EDGE,"E18"),sQuery(id+"F0.wireOp",EDGE,"E19"),sQuery(id+"F0.wireOp",EDGE,"E20"),sQuery(id+"F0.wireOp",EDGE,"E21"),sQuery(id+"F0.wireOp",EDGE,"E22"),sQuery(id+"F0.wireOp",EDGE,"E23"),sQuery(id+"F0.wireOp",EDGE,"E24"),sQuery(id+"F0.wireOp",EDGE,"E25"),sQuery(id+"F0.wireOp",EDGE,"E26"),sQuery(id+"F0.wireOp",EDGE,"E27"),sQuery(id+"F0.wireOp",EDGE,"E28"),sQuery(id+"F0.wireOp",EDGE,"E29"),sQuery(id+"F0.wireOp",EDGE,"E30"),sQuery(id+"F0.wireOp",EDGE,"E31"),sQuery(id+"F0.wireOp",EDGE,"E32"),sQuery(id+"F0.wireOp",EDGE,"E33"),sQuery(id+"F0.wireOp",EDGE,"E34"),sQuery(id+"F0.wireOp",EDGE,"E35"),sQuery(id+"F0.wireOp",EDGE,"E36"),sQuery(id+"F0.wireOp",EDGE,"E37"),sQuery(id+"F0.wireOp",EDGE,"E38"),sQuery(id+"F0.wireOp",EDGE,"E39"),sQuery(id+"F0.wireOp",EDGE,"E40"),sQuery(id+"F0.wireOp",EDGE,"E41"),sQuery(id+"F0.wireOp",EDGE,"E42"),sQuery(id+"F0.wireOp",EDGE,"E43"),sQuery(id+"F0.wireOp",EDGE,"E44"),sQuery(id+"F0.wireOp",EDGE,"E45"),sQuery(id+"F0.wireOp",EDGE,"E46"),sQuery(id+"F0.wireOp",EDGE,"E47"),sQuery(id+"F0.wireOp",EDGE,"E48"),sQuery(id+"F0.wireOp",EDGE,"E49"),sQuery(id+"F0.wireOp",EDGE,"E50"),sQuery(id+"F0.wireOp",EDGE,"E51"),sQuery(id+"F0.wireOp",EDGE,"E52"),sQuery(id+"F0.wireOp",EDGE,"E53"),sQuery(id+"F0.wireOp",EDGE,"E54"),sQuery(id+"F0.wireOp",EDGE,"E55"),sQuery(id+"F0.wireOp",EDGE,"E56"),sQuery(id+"F0.wireOp",EDGE,"E57"),sQuery(id+"F0.wireOp",EDGE,"E58"),sQuery(id+"F0.wireOp",EDGE,"E59"),sQuery(id+"F0.wireOp",EDGE,"E60"),sQuery(id+"F0.wireOp",EDGE,"E61"),sQuery(id+"F0.wireOp",EDGE,"E62"),sQuery(id+"F0.wireOp",EDGE,"E63"),sQuery(id+"F0.wireOp",EDGE,"E64"),sQuery(id+"F0.wireOp",EDGE,"E65"),sQuery(id+"F0.wireOp",EDGE,"E66"),sQuery(id+"F0.wireOp",EDGE,"E67"),sQuery(id+"F0.wireOp",EDGE,"E68"),sQuery(id+"F0.wireOp",EDGE,"E69"),sQuery(id+"F0.wireOp",EDGE,"E70"),sQuery(id+"F0.wireOp",EDGE,"E71"),sQuery(id+"F0.wireOp",EDGE,"E72"),sQuery(id+"F0.wireOp",EDGE,"E73"),sQuery(id+"F0.wireOp",EDGE,"E74"),sQuery(id+"F0.wireOp",EDGE,"E75"),sQuery(id+"F0.wireOp",EDGE,"E76"),sQuery(id+"F0.wireOp",EDGE,"E77"),sQuery(id+"F0.wireOp",EDGE,"E78"),sQuery(id+"F0.wireOp",EDGE,"E79"),sQuery(id+"F0.wireOp",EDGE,"E80"),sQuery(id+"F0.wireOp",EDGE,"E81"),sQuery(id+"F0.wireOp",EDGE,"E82"),sQuery(id+"F0.wireOp",EDGE,"E83"),sQuery(id+"F0.wireOp",EDGE,"E84"),sQuery(id+"F0.wireOp",EDGE,"E85"),sQuery(id+"F0.wireOp",EDGE,"E86"),sQuery(id+"F0.wireOp",EDGE,"E87"),sQuery(id+"F0.wireOp",EDGE,"E88"),sQuery(id+"F0.wireOp",EDGE,"E89"),sQuery(id+"F0.wireOp",EDGE,"E90"),sQuery(id+"F0.wireOp",EDGE,"E91"),sQuery(id+"F0.wireOp",EDGE,"E92"),sQuery(id+"F0.wireOp",EDGE,"E93"),sQuery(id+"F0.wireOp",EDGE,"E94"),sQuery(id+"F0.wireOp",EDGE,"E95"),sQuery(id+"F0.wireOp",EDGE,"E96"),sQuery(id+"F0.wireOp",EDGE,"E97"),sQuery(id+"F0.wireOp",EDGE,"E98"),sQuery(id+"F0.wireOp",EDGE,"E99"),sQuery(id+"F0.wireOp",EDGE,"E100"),sQuery(id+"F0.wireOp",EDGE,"E101"),sQuery(id+"F0.wireOp",EDGE,"E102"),sQuery(id+"F0.wireOp",EDGE,"E103"),sQuery(id+"F0.wireOp",EDGE,"E104"),sQuery(id+"F0.wireOp",EDGE,"E105"),sQuery(id+"F0.wireOp",EDGE,"E106"),sQuery(id+"F0.wireOp",EDGE,"E107"),sQuery(id+"F0.wireOp",EDGE,"E108"),sQuery(id+"F0.wireOp",EDGE,"E109"),sQuery(id+"F0.wireOp",EDGE,"E110"),sQuery(id+"F0.wireOp",EDGE,"E111"),sQuery(id+"F0.wireOp",EDGE,"E112"),sQuery(id+"F0.wireOp",EDGE,"E113"),sQuery(id+"F0.wireOp",EDGE,"E114"),sQuery(id+"F0.wireOp",EDGE,"E115")])],"isStart":false})],"blendedInto":[makeQuery(id+"F1.opExtrude","CAP_FACE",FACE,{"disambiguationData":[OSD([sQuery(id+"F0.wireOp",EDGE,"E0"),sQuery(id+"F0.wireOp",EDGE,"E1"),sQuery(id+"F0.wireOp",EDGE,"E2"),sQuery(id+"F0.wireOp",EDGE,"E3"),sQuery(id+"F0.wireOp",EDGE,"E4"),sQuery(id+"F0.wireOp",EDGE,"E5"),sQuery(id+"F0.wireOp",EDGE,"E6"),sQuery(id+"F0.wireOp",EDGE,"E7"),sQuery(id+"F0.wireOp",EDGE,"E8"),sQuery(id+"F0.wireOp",EDGE,"E9"),sQuery(id+"F0.wireOp",EDGE,"E10"),sQuery(id+"F0.wireOp",EDGE,"E11"),sQuery(id+"F0.wireOp",EDGE,"E12"),sQuery(id+"F0.wireOp",EDGE,"E13"),sQuery(id+"F0.wireOp",EDGE,"E14"),sQuery(id+"F0.wireOp",EDGE,"E15"),sQuery(id+"F0.wireOp",EDGE,"E16"),sQuery(id+"F0.wireOp",EDGE,"E17"),sQuery(id+"F0.wireOp",EDGE,"E18"),sQuery(id+"F0.wireOp",EDGE,"E19"),sQuery(id+"F0.wireOp",EDGE,"E20"),sQuery(id+"F0.wireOp",EDGE,"E21"),sQuery(id+"F0.wireOp",EDGE,"E22"),sQuery(id+"F0.wireOp",EDGE,"E23"),sQuery(id+"F0.wireOp",EDGE,"E24"),sQuery(id+"F0.wireOp",EDGE,"E25"),sQuery(id+"F0.wireOp",EDGE,"E26"),sQuery(id+"F0.wireOp",EDGE,"E27"),sQuery(id+"F0.wireOp",EDGE,"E28"),sQuery(id+"F0.wireOp",EDGE,"E29"),sQuery(id+"F0.wireOp",EDGE,"E30"),sQuery(id+"F0.wireOp",EDGE,"E31"),sQuery(id+"F0.wireOp",EDGE,"E32"),sQuery(id+"F0.wireOp",EDGE,"E33"),sQuery(id+"F0.wireOp",EDGE,"E34"),sQuery(id+"F0.wireOp",EDGE,"E35"),sQuery(id+"F0.wireOp",EDGE,"E36"),sQuery(id+"F0.wireOp",EDGE,"E37"),sQuery(id+"F0.wireOp",EDGE,"E38"),sQuery(id+"F0.wireOp",EDGE,"E39"),sQuery(id+"F0.wireOp",EDGE,"E40"),sQuery(id+"F0.wireOp",EDGE,"E41"),sQuery(id+"F0.wireOp",EDGE,"E42"),sQuery(id+"F0.wireOp",EDGE,"E43"),sQuery(id+"F0.wireOp",EDGE,"E44"),sQuery(id+"F0.wireOp",EDGE,"E45"),sQuery(id+"F0.wireOp",EDGE,"E46"),sQuery(id+"F0.wireOp",EDGE,"E47"),sQuery(id+"F0.wireOp",EDGE,"E48"),sQuery(id+"F0.wireOp",EDGE,"E49"),sQuery(id+"F0.wireOp",EDGE,"E50"),sQuery(id+"F0.wireOp",EDGE,"E51"),sQuery(id+"F0.wireOp",EDGE,"E52"),sQuery(id+"F0.wireOp",EDGE,"E53"),sQuery(id+"F0.wireOp",EDGE,"E54"),sQuery(id+"F0.wireOp",EDGE,"E55"),sQuery(id+"F0.wireOp",EDGE,"E56"),sQuery(id+"F0.wireOp",EDGE,"E57"),sQuery(id+"F0.wireOp",EDGE,"E58"),sQuery(id+"F0.wireOp",EDGE,"E59"),sQuery(id+"F0.wireOp",EDGE,"E60"),sQuery(id+"F0.wireOp",EDGE,"E61"),sQuery(id+"F0.wireOp",EDGE,"E62"),sQuery(id+"F0.wireOp",EDGE,"E63"),sQuery(id+"F0.wireOp",EDGE,"E64"),sQuery(id+"F0.wireOp",EDGE,"E65"),sQuery(id+"F0.wireOp",EDGE,"E66"),sQuery(id+"F0.wireOp",EDGE,"E67"),sQuery(id+"F0.wireOp",EDGE,"E68"),sQuery(id+"F0.wireOp",EDGE,"E69"),sQuery(id+"F0.wireOp",EDGE,"E70"),sQuery(id+"F0.wireOp",EDGE,"E71"),sQuery(id+"F0.wireOp",EDGE,"E72"),sQuery(id+"F0.wireOp",EDGE,"E73"),sQuery(id+"F0.wireOp",EDGE,"E74"),sQuery(id+"F0.wireOp",EDGE,"E75"),sQuery(id+"F0.wireOp",EDGE,"E76"),sQuery(id+"F0.wireOp",EDGE,"E77"),sQuery(id+"F0.wireOp",EDGE,"E78"),sQuery(id+"F0.wireOp",EDGE,"E79"),sQuery(id+"F0.wireOp",EDGE,"E80"),sQuery(id+"F0.wireOp",EDGE,"E81"),sQuery(id+"F0.wireOp",EDGE,"E82"),sQuery(id+"F0.wireOp",EDGE,"E83"),sQuery(id+"F0.wireOp",EDGE,"E84"),sQuery(id+"F0.wireOp",EDGE,"E85"),sQuery(id+"F0.wireOp",EDGE,"E86"),sQuery(id+"F0.wireOp",EDGE,"E87"),sQuery(id+"F0.wireOp",EDGE,"E88"),sQuery(id+"F0.wireOp",EDGE,"E89"),sQuery(id+"F0.wireOp",EDGE,"E90"),sQuery(id+"F0.wireOp",EDGE,"E91"),sQuery(id+"F0.wireOp",EDGE,"E92"),sQuery(id+"F0.wireOp",EDGE,"E93"),sQuery(id+"F0.wireOp",EDGE,"E94"),sQuery(id+"F0.wireOp",EDGE,"E95"),sQuery(id+"F0.wireOp",EDGE,"E96"),sQuery(id+"F0.wireOp",EDGE,"E97"),sQuery(id+"F0.wireOp",EDGE,"E98"),sQuery(id+"F0.wireOp",EDGE,"E99"),sQuery(id+"F0.wireOp",EDGE,"E100"),sQuery(id+"F0.wireOp",EDGE,"E101"),sQuery(id+"F0.wireOp",EDGE,"E102"),sQuery(id+"F0.wireOp",EDGE,"E103"),sQuery(id+"F0.wireOp",EDGE,"E104"),sQuery(id+"F0.wireOp",EDGE,"E105"),sQuery(id+"F0.wireOp",EDGE,"E106"),sQuery(id+"F0.wireOp",EDGE,"E107"),sQuery(id+"F0.wireOp",EDGE,"E108"),sQuery(id+"F0.wireOp",EDGE,"E109"),sQuery(id+"F0.wireOp",EDGE,"E110"),sQuery(id+"F0.wireOp",EDGE,"E111"),sQuery(id+"F0.wireOp",EDGE,"E112"),sQuery(id+"F0.wireOp",EDGE,"E113"),sQuery(id+"F0.wireOp",EDGE,"E114"),sQuery(id+"F0.wireOp",EDGE,"E115")])],"isStart":false})]});
            var Q26;
            Q26=makeQuery(id+"F6.opFillet","BLEND_EDGE",EDGE,{"blendedFrom":[makeQuery(id+"F5.boolean.opBoolean","COPY",EDGE,{"derivedFrom":makeQuery(id+"F5.opExtrude","CAP_EDGE",EDGE,{"disambiguationData":[OSD([sQuery(id+"F4.wireOp",EDGE,"E759.0.3.4")])],"isStart":false})}),makeQuery(id+"F1.opExtrude","CAP_FACE",FACE,{"disambiguationData":[OSD([sQuery(id+"F0.wireOp",EDGE,"E0"),sQuery(id+"F0.wireOp",EDGE,"E1"),sQuery(id+"F0.wireOp",EDGE,"E2"),sQuery(id+"F0.wireOp",EDGE,"E3"),sQuery(id+"F0.wireOp",EDGE,"E4"),sQuery(id+"F0.wireOp",EDGE,"E5"),sQuery(id+"F0.wireOp",EDGE,"E6"),sQuery(id+"F0.wireOp",EDGE,"E7"),sQuery(id+"F0.wireOp",EDGE,"E8"),sQuery(id+"F0.wireOp",EDGE,"E9"),sQuery(id+"F0.wireOp",EDGE,"E10"),sQuery(id+"F0.wireOp",EDGE,"E11"),sQuery(id+"F0.wireOp",EDGE,"E12"),sQuery(id+"F0.wireOp",EDGE,"E13"),sQuery(id+"F0.wireOp",EDGE,"E14"),sQuery(id+"F0.wireOp",EDGE,"E15"),sQuery(id+"F0.wireOp",EDGE,"E16"),sQuery(id+"F0.wireOp",EDGE,"E17"),sQuery(id+"F0.wireOp",EDGE,"E18"),sQuery(id+"F0.wireOp",EDGE,"E19"),sQuery(id+"F0.wireOp",EDGE,"E20"),sQuery(id+"F0.wireOp",EDGE,"E21"),sQuery(id+"F0.wireOp",EDGE,"E22"),sQuery(id+"F0.wireOp",EDGE,"E23"),sQuery(id+"F0.wireOp",EDGE,"E24"),sQuery(id+"F0.wireOp",EDGE,"E25"),sQuery(id+"F0.wireOp",EDGE,"E26"),sQuery(id+"F0.wireOp",EDGE,"E27"),sQuery(id+"F0.wireOp",EDGE,"E28"),sQuery(id+"F0.wireOp",EDGE,"E29"),sQuery(id+"F0.wireOp",EDGE,"E30"),sQuery(id+"F0.wireOp",EDGE,"E31"),sQuery(id+"F0.wireOp",EDGE,"E32"),sQuery(id+"F0.wireOp",EDGE,"E33"),sQuery(id+"F0.wireOp",EDGE,"E34"),sQuery(id+"F0.wireOp",EDGE,"E35"),sQuery(id+"F0.wireOp",EDGE,"E36"),sQuery(id+"F0.wireOp",EDGE,"E37"),sQuery(id+"F0.wireOp",EDGE,"E38"),sQuery(id+"F0.wireOp",EDGE,"E39"),sQuery(id+"F0.wireOp",EDGE,"E40"),sQuery(id+"F0.wireOp",EDGE,"E41"),sQuery(id+"F0.wireOp",EDGE,"E42"),sQuery(id+"F0.wireOp",EDGE,"E43"),sQuery(id+"F0.wireOp",EDGE,"E44"),sQuery(id+"F0.wireOp",EDGE,"E45"),sQuery(id+"F0.wireOp",EDGE,"E46"),sQuery(id+"F0.wireOp",EDGE,"E47"),sQuery(id+"F0.wireOp",EDGE,"E48"),sQuery(id+"F0.wireOp",EDGE,"E49"),sQuery(id+"F0.wireOp",EDGE,"E50"),sQuery(id+"F0.wireOp",EDGE,"E51"),sQuery(id+"F0.wireOp",EDGE,"E52"),sQuery(id+"F0.wireOp",EDGE,"E53"),sQuery(id+"F0.wireOp",EDGE,"E54"),sQuery(id+"F0.wireOp",EDGE,"E55"),sQuery(id+"F0.wireOp",EDGE,"E56"),sQuery(id+"F0.wireOp",EDGE,"E57"),sQuery(id+"F0.wireOp",EDGE,"E58"),sQuery(id+"F0.wireOp",EDGE,"E59"),sQuery(id+"F0.wireOp",EDGE,"E60"),sQuery(id+"F0.wireOp",EDGE,"E61"),sQuery(id+"F0.wireOp",EDGE,"E62"),sQuery(id+"F0.wireOp",EDGE,"E63"),sQuery(id+"F0.wireOp",EDGE,"E64"),sQuery(id+"F0.wireOp",EDGE,"E65"),sQuery(id+"F0.wireOp",EDGE,"E66"),sQuery(id+"F0.wireOp",EDGE,"E67"),sQuery(id+"F0.wireOp",EDGE,"E68"),sQuery(id+"F0.wireOp",EDGE,"E69"),sQuery(id+"F0.wireOp",EDGE,"E70"),sQuery(id+"F0.wireOp",EDGE,"E71"),sQuery(id+"F0.wireOp",EDGE,"E72"),sQuery(id+"F0.wireOp",EDGE,"E73"),sQuery(id+"F0.wireOp",EDGE,"E74"),sQuery(id+"F0.wireOp",EDGE,"E75"),sQuery(id+"F0.wireOp",EDGE,"E76"),sQuery(id+"F0.wireOp",EDGE,"E77"),sQuery(id+"F0.wireOp",EDGE,"E78"),sQuery(id+"F0.wireOp",EDGE,"E79"),sQuery(id+"F0.wireOp",EDGE,"E80"),sQuery(id+"F0.wireOp",EDGE,"E81"),sQuery(id+"F0.wireOp",EDGE,"E82"),sQuery(id+"F0.wireOp",EDGE,"E83"),sQuery(id+"F0.wireOp",EDGE,"E84"),sQuery(id+"F0.wireOp",EDGE,"E85"),sQuery(id+"F0.wireOp",EDGE,"E86"),sQuery(id+"F0.wireOp",EDGE,"E87"),sQuery(id+"F0.wireOp",EDGE,"E88"),sQuery(id+"F0.wireOp",EDGE,"E89"),sQuery(id+"F0.wireOp",EDGE,"E90"),sQuery(id+"F0.wireOp",EDGE,"E91"),sQuery(id+"F0.wireOp",EDGE,"E92"),sQuery(id+"F0.wireOp",EDGE,"E93"),sQuery(id+"F0.wireOp",EDGE,"E94"),sQuery(id+"F0.wireOp",EDGE,"E95"),sQuery(id+"F0.wireOp",EDGE,"E96"),sQuery(id+"F0.wireOp",EDGE,"E97"),sQuery(id+"F0.wireOp",EDGE,"E98"),sQuery(id+"F0.wireOp",EDGE,"E99"),sQuery(id+"F0.wireOp",EDGE,"E100"),sQuery(id+"F0.wireOp",EDGE,"E101"),sQuery(id+"F0.wireOp",EDGE,"E102"),sQuery(id+"F0.wireOp",EDGE,"E103"),sQuery(id+"F0.wireOp",EDGE,"E104"),sQuery(id+"F0.wireOp",EDGE,"E105"),sQuery(id+"F0.wireOp",EDGE,"E106"),sQuery(id+"F0.wireOp",EDGE,"E107"),sQuery(id+"F0.wireOp",EDGE,"E108"),sQuery(id+"F0.wireOp",EDGE,"E109"),sQuery(id+"F0.wireOp",EDGE,"E110"),sQuery(id+"F0.wireOp",EDGE,"E111"),sQuery(id+"F0.wireOp",EDGE,"E112"),sQuery(id+"F0.wireOp",EDGE,"E113"),sQuery(id+"F0.wireOp",EDGE,"E114"),sQuery(id+"F0.wireOp",EDGE,"E115")])],"isStart":false})],"blendedInto":[makeQuery(id+"F1.opExtrude","CAP_FACE",FACE,{"disambiguationData":[OSD([sQuery(id+"F0.wireOp",EDGE,"E0"),sQuery(id+"F0.wireOp",EDGE,"E1"),sQuery(id+"F0.wireOp",EDGE,"E2"),sQuery(id+"F0.wireOp",EDGE,"E3"),sQuery(id+"F0.wireOp",EDGE,"E4"),sQuery(id+"F0.wireOp",EDGE,"E5"),sQuery(id+"F0.wireOp",EDGE,"E6"),sQuery(id+"F0.wireOp",EDGE,"E7"),sQuery(id+"F0.wireOp",EDGE,"E8"),sQuery(id+"F0.wireOp",EDGE,"E9"),sQuery(id+"F0.wireOp",EDGE,"E10"),sQuery(id+"F0.wireOp",EDGE,"E11"),sQuery(id+"F0.wireOp",EDGE,"E12"),sQuery(id+"F0.wireOp",EDGE,"E13"),sQuery(id+"F0.wireOp",EDGE,"E14"),sQuery(id+"F0.wireOp",EDGE,"E15"),sQuery(id+"F0.wireOp",EDGE,"E16"),sQuery(id+"F0.wireOp",EDGE,"E17"),sQuery(id+"F0.wireOp",EDGE,"E18"),sQuery(id+"F0.wireOp",EDGE,"E19"),sQuery(id+"F0.wireOp",EDGE,"E20"),sQuery(id+"F0.wireOp",EDGE,"E21"),sQuery(id+"F0.wireOp",EDGE,"E22"),sQuery(id+"F0.wireOp",EDGE,"E23"),sQuery(id+"F0.wireOp",EDGE,"E24"),sQuery(id+"F0.wireOp",EDGE,"E25"),sQuery(id+"F0.wireOp",EDGE,"E26"),sQuery(id+"F0.wireOp",EDGE,"E27"),sQuery(id+"F0.wireOp",EDGE,"E28"),sQuery(id+"F0.wireOp",EDGE,"E29"),sQuery(id+"F0.wireOp",EDGE,"E30"),sQuery(id+"F0.wireOp",EDGE,"E31"),sQuery(id+"F0.wireOp",EDGE,"E32"),sQuery(id+"F0.wireOp",EDGE,"E33"),sQuery(id+"F0.wireOp",EDGE,"E34"),sQuery(id+"F0.wireOp",EDGE,"E35"),sQuery(id+"F0.wireOp",EDGE,"E36"),sQuery(id+"F0.wireOp",EDGE,"E37"),sQuery(id+"F0.wireOp",EDGE,"E38"),sQuery(id+"F0.wireOp",EDGE,"E39"),sQuery(id+"F0.wireOp",EDGE,"E40"),sQuery(id+"F0.wireOp",EDGE,"E41"),sQuery(id+"F0.wireOp",EDGE,"E42"),sQuery(id+"F0.wireOp",EDGE,"E43"),sQuery(id+"F0.wireOp",EDGE,"E44"),sQuery(id+"F0.wireOp",EDGE,"E45"),sQuery(id+"F0.wireOp",EDGE,"E46"),sQuery(id+"F0.wireOp",EDGE,"E47"),sQuery(id+"F0.wireOp",EDGE,"E48"),sQuery(id+"F0.wireOp",EDGE,"E49"),sQuery(id+"F0.wireOp",EDGE,"E50"),sQuery(id+"F0.wireOp",EDGE,"E51"),sQuery(id+"F0.wireOp",EDGE,"E52"),sQuery(id+"F0.wireOp",EDGE,"E53"),sQuery(id+"F0.wireOp",EDGE,"E54"),sQuery(id+"F0.wireOp",EDGE,"E55"),sQuery(id+"F0.wireOp",EDGE,"E56"),sQuery(id+"F0.wireOp",EDGE,"E57"),sQuery(id+"F0.wireOp",EDGE,"E58"),sQuery(id+"F0.wireOp",EDGE,"E59"),sQuery(id+"F0.wireOp",EDGE,"E60"),sQuery(id+"F0.wireOp",EDGE,"E61"),sQuery(id+"F0.wireOp",EDGE,"E62"),sQuery(id+"F0.wireOp",EDGE,"E63"),sQuery(id+"F0.wireOp",EDGE,"E64"),sQuery(id+"F0.wireOp",EDGE,"E65"),sQuery(id+"F0.wireOp",EDGE,"E66"),sQuery(id+"F0.wireOp",EDGE,"E67"),sQuery(id+"F0.wireOp",EDGE,"E68"),sQuery(id+"F0.wireOp",EDGE,"E69"),sQuery(id+"F0.wireOp",EDGE,"E70"),sQuery(id+"F0.wireOp",EDGE,"E71"),sQuery(id+"F0.wireOp",EDGE,"E72"),sQuery(id+"F0.wireOp",EDGE,"E73"),sQuery(id+"F0.wireOp",EDGE,"E74"),sQuery(id+"F0.wireOp",EDGE,"E75"),sQuery(id+"F0.wireOp",EDGE,"E76"),sQuery(id+"F0.wireOp",EDGE,"E77"),sQuery(id+"F0.wireOp",EDGE,"E78"),sQuery(id+"F0.wireOp",EDGE,"E79"),sQuery(id+"F0.wireOp",EDGE,"E80"),sQuery(id+"F0.wireOp",EDGE,"E81"),sQuery(id+"F0.wireOp",EDGE,"E82"),sQuery(id+"F0.wireOp",EDGE,"E83"),sQuery(id+"F0.wireOp",EDGE,"E84"),sQuery(id+"F0.wireOp",EDGE,"E85"),sQuery(id+"F0.wireOp",EDGE,"E86"),sQuery(id+"F0.wireOp",EDGE,"E87"),sQuery(id+"F0.wireOp",EDGE,"E88"),sQuery(id+"F0.wireOp",EDGE,"E89"),sQuery(id+"F0.wireOp",EDGE,"E90"),sQuery(id+"F0.wireOp",EDGE,"E91"),sQuery(id+"F0.wireOp",EDGE,"E92"),sQuery(id+"F0.wireOp",EDGE,"E93"),sQuery(id+"F0.wireOp",EDGE,"E94"),sQuery(id+"F0.wireOp",EDGE,"E95"),sQuery(id+"F0.wireOp",EDGE,"E96"),sQuery(id+"F0.wireOp",EDGE,"E97"),sQuery(id+"F0.wireOp",EDGE,"E98"),sQuery(id+"F0.wireOp",EDGE,"E99"),sQuery(id+"F0.wireOp",EDGE,"E100"),sQuery(id+"F0.wireOp",EDGE,"E101"),sQuery(id+"F0.wireOp",EDGE,"E102"),sQuery(id+"F0.wireOp",EDGE,"E103"),sQuery(id+"F0.wireOp",EDGE,"E104"),sQuery(id+"F0.wireOp",EDGE,"E105"),sQuery(id+"F0.wireOp",EDGE,"E106"),sQuery(id+"F0.wireOp",EDGE,"E107"),sQuery(id+"F0.wireOp",EDGE,"E108"),sQuery(id+"F0.wireOp",EDGE,"E109"),sQuery(id+"F0.wireOp",EDGE,"E110"),sQuery(id+"F0.wireOp",EDGE,"E111"),sQuery(id+"F0.wireOp",EDGE,"E112"),sQuery(id+"F0.wireOp",EDGE,"E113"),sQuery(id+"F0.wireOp",EDGE,"E114"),sQuery(id+"F0.wireOp",EDGE,"E115")])],"isStart":false})]});
            var Q27;
            Q27=makeQuery(id+"F6.opFillet","BLEND_EDGE",EDGE,{"blendedFrom":[makeQuery(id+"F5.boolean.opBoolean","COPY",EDGE,{"derivedFrom":makeQuery(id+"F5.opExtrude","CAP_EDGE",EDGE,{"disambiguationData":[OSD([sQuery(id+"F4.wireOp",EDGE,"E759.0.2.4")])],"isStart":false})}),makeQuery(id+"F1.opExtrude","CAP_FACE",FACE,{"disambiguationData":[OSD([sQuery(id+"F0.wireOp",EDGE,"E0"),sQuery(id+"F0.wireOp",EDGE,"E1"),sQuery(id+"F0.wireOp",EDGE,"E2"),sQuery(id+"F0.wireOp",EDGE,"E3"),sQuery(id+"F0.wireOp",EDGE,"E4"),sQuery(id+"F0.wireOp",EDGE,"E5"),sQuery(id+"F0.wireOp",EDGE,"E6"),sQuery(id+"F0.wireOp",EDGE,"E7"),sQuery(id+"F0.wireOp",EDGE,"E8"),sQuery(id+"F0.wireOp",EDGE,"E9"),sQuery(id+"F0.wireOp",EDGE,"E10"),sQuery(id+"F0.wireOp",EDGE,"E11"),sQuery(id+"F0.wireOp",EDGE,"E12"),sQuery(id+"F0.wireOp",EDGE,"E13"),sQuery(id+"F0.wireOp",EDGE,"E14"),sQuery(id+"F0.wireOp",EDGE,"E15"),sQuery(id+"F0.wireOp",EDGE,"E16"),sQuery(id+"F0.wireOp",EDGE,"E17"),sQuery(id+"F0.wireOp",EDGE,"E18"),sQuery(id+"F0.wireOp",EDGE,"E19"),sQuery(id+"F0.wireOp",EDGE,"E20"),sQuery(id+"F0.wireOp",EDGE,"E21"),sQuery(id+"F0.wireOp",EDGE,"E22"),sQuery(id+"F0.wireOp",EDGE,"E23"),sQuery(id+"F0.wireOp",EDGE,"E24"),sQuery(id+"F0.wireOp",EDGE,"E25"),sQuery(id+"F0.wireOp",EDGE,"E26"),sQuery(id+"F0.wireOp",EDGE,"E27"),sQuery(id+"F0.wireOp",EDGE,"E28"),sQuery(id+"F0.wireOp",EDGE,"E29"),sQuery(id+"F0.wireOp",EDGE,"E30"),sQuery(id+"F0.wireOp",EDGE,"E31"),sQuery(id+"F0.wireOp",EDGE,"E32"),sQuery(id+"F0.wireOp",EDGE,"E33"),sQuery(id+"F0.wireOp",EDGE,"E34"),sQuery(id+"F0.wireOp",EDGE,"E35"),sQuery(id+"F0.wireOp",EDGE,"E36"),sQuery(id+"F0.wireOp",EDGE,"E37"),sQuery(id+"F0.wireOp",EDGE,"E38"),sQuery(id+"F0.wireOp",EDGE,"E39"),sQuery(id+"F0.wireOp",EDGE,"E40"),sQuery(id+"F0.wireOp",EDGE,"E41"),sQuery(id+"F0.wireOp",EDGE,"E42"),sQuery(id+"F0.wireOp",EDGE,"E43"),sQuery(id+"F0.wireOp",EDGE,"E44"),sQuery(id+"F0.wireOp",EDGE,"E45"),sQuery(id+"F0.wireOp",EDGE,"E46"),sQuery(id+"F0.wireOp",EDGE,"E47"),sQuery(id+"F0.wireOp",EDGE,"E48"),sQuery(id+"F0.wireOp",EDGE,"E49"),sQuery(id+"F0.wireOp",EDGE,"E50"),sQuery(id+"F0.wireOp",EDGE,"E51"),sQuery(id+"F0.wireOp",EDGE,"E52"),sQuery(id+"F0.wireOp",EDGE,"E53"),sQuery(id+"F0.wireOp",EDGE,"E54"),sQuery(id+"F0.wireOp",EDGE,"E55"),sQuery(id+"F0.wireOp",EDGE,"E56"),sQuery(id+"F0.wireOp",EDGE,"E57"),sQuery(id+"F0.wireOp",EDGE,"E58"),sQuery(id+"F0.wireOp",EDGE,"E59"),sQuery(id+"F0.wireOp",EDGE,"E60"),sQuery(id+"F0.wireOp",EDGE,"E61"),sQuery(id+"F0.wireOp",EDGE,"E62"),sQuery(id+"F0.wireOp",EDGE,"E63"),sQuery(id+"F0.wireOp",EDGE,"E64"),sQuery(id+"F0.wireOp",EDGE,"E65"),sQuery(id+"F0.wireOp",EDGE,"E66"),sQuery(id+"F0.wireOp",EDGE,"E67"),sQuery(id+"F0.wireOp",EDGE,"E68"),sQuery(id+"F0.wireOp",EDGE,"E69"),sQuery(id+"F0.wireOp",EDGE,"E70"),sQuery(id+"F0.wireOp",EDGE,"E71"),sQuery(id+"F0.wireOp",EDGE,"E72"),sQuery(id+"F0.wireOp",EDGE,"E73"),sQuery(id+"F0.wireOp",EDGE,"E74"),sQuery(id+"F0.wireOp",EDGE,"E75"),sQuery(id+"F0.wireOp",EDGE,"E76"),sQuery(id+"F0.wireOp",EDGE,"E77"),sQuery(id+"F0.wireOp",EDGE,"E78"),sQuery(id+"F0.wireOp",EDGE,"E79"),sQuery(id+"F0.wireOp",EDGE,"E80"),sQuery(id+"F0.wireOp",EDGE,"E81"),sQuery(id+"F0.wireOp",EDGE,"E82"),sQuery(id+"F0.wireOp",EDGE,"E83"),sQuery(id+"F0.wireOp",EDGE,"E84"),sQuery(id+"F0.wireOp",EDGE,"E85"),sQuery(id+"F0.wireOp",EDGE,"E86"),sQuery(id+"F0.wireOp",EDGE,"E87"),sQuery(id+"F0.wireOp",EDGE,"E88"),sQuery(id+"F0.wireOp",EDGE,"E89"),sQuery(id+"F0.wireOp",EDGE,"E90"),sQuery(id+"F0.wireOp",EDGE,"E91"),sQuery(id+"F0.wireOp",EDGE,"E92"),sQuery(id+"F0.wireOp",EDGE,"E93"),sQuery(id+"F0.wireOp",EDGE,"E94"),sQuery(id+"F0.wireOp",EDGE,"E95"),sQuery(id+"F0.wireOp",EDGE,"E96"),sQuery(id+"F0.wireOp",EDGE,"E97"),sQuery(id+"F0.wireOp",EDGE,"E98"),sQuery(id+"F0.wireOp",EDGE,"E99"),sQuery(id+"F0.wireOp",EDGE,"E100"),sQuery(id+"F0.wireOp",EDGE,"E101"),sQuery(id+"F0.wireOp",EDGE,"E102"),sQuery(id+"F0.wireOp",EDGE,"E103"),sQuery(id+"F0.wireOp",EDGE,"E104"),sQuery(id+"F0.wireOp",EDGE,"E105"),sQuery(id+"F0.wireOp",EDGE,"E106"),sQuery(id+"F0.wireOp",EDGE,"E107"),sQuery(id+"F0.wireOp",EDGE,"E108"),sQuery(id+"F0.wireOp",EDGE,"E109"),sQuery(id+"F0.wireOp",EDGE,"E110"),sQuery(id+"F0.wireOp",EDGE,"E111"),sQuery(id+"F0.wireOp",EDGE,"E112"),sQuery(id+"F0.wireOp",EDGE,"E113"),sQuery(id+"F0.wireOp",EDGE,"E114"),sQuery(id+"F0.wireOp",EDGE,"E115")])],"isStart":false})],"blendedInto":[makeQuery(id+"F1.opExtrude","CAP_FACE",FACE,{"disambiguationData":[OSD([sQuery(id+"F0.wireOp",EDGE,"E0"),sQuery(id+"F0.wireOp",EDGE,"E1"),sQuery(id+"F0.wireOp",EDGE,"E2"),sQuery(id+"F0.wireOp",EDGE,"E3"),sQuery(id+"F0.wireOp",EDGE,"E4"),sQuery(id+"F0.wireOp",EDGE,"E5"),sQuery(id+"F0.wireOp",EDGE,"E6"),sQuery(id+"F0.wireOp",EDGE,"E7"),sQuery(id+"F0.wireOp",EDGE,"E8"),sQuery(id+"F0.wireOp",EDGE,"E9"),sQuery(id+"F0.wireOp",EDGE,"E10"),sQuery(id+"F0.wireOp",EDGE,"E11"),sQuery(id+"F0.wireOp",EDGE,"E12"),sQuery(id+"F0.wireOp",EDGE,"E13"),sQuery(id+"F0.wireOp",EDGE,"E14"),sQuery(id+"F0.wireOp",EDGE,"E15"),sQuery(id+"F0.wireOp",EDGE,"E16"),sQuery(id+"F0.wireOp",EDGE,"E17"),sQuery(id+"F0.wireOp",EDGE,"E18"),sQuery(id+"F0.wireOp",EDGE,"E19"),sQuery(id+"F0.wireOp",EDGE,"E20"),sQuery(id+"F0.wireOp",EDGE,"E21"),sQuery(id+"F0.wireOp",EDGE,"E22"),sQuery(id+"F0.wireOp",EDGE,"E23"),sQuery(id+"F0.wireOp",EDGE,"E24"),sQuery(id+"F0.wireOp",EDGE,"E25"),sQuery(id+"F0.wireOp",EDGE,"E26"),sQuery(id+"F0.wireOp",EDGE,"E27"),sQuery(id+"F0.wireOp",EDGE,"E28"),sQuery(id+"F0.wireOp",EDGE,"E29"),sQuery(id+"F0.wireOp",EDGE,"E30"),sQuery(id+"F0.wireOp",EDGE,"E31"),sQuery(id+"F0.wireOp",EDGE,"E32"),sQuery(id+"F0.wireOp",EDGE,"E33"),sQuery(id+"F0.wireOp",EDGE,"E34"),sQuery(id+"F0.wireOp",EDGE,"E35"),sQuery(id+"F0.wireOp",EDGE,"E36"),sQuery(id+"F0.wireOp",EDGE,"E37"),sQuery(id+"F0.wireOp",EDGE,"E38"),sQuery(id+"F0.wireOp",EDGE,"E39"),sQuery(id+"F0.wireOp",EDGE,"E40"),sQuery(id+"F0.wireOp",EDGE,"E41"),sQuery(id+"F0.wireOp",EDGE,"E42"),sQuery(id+"F0.wireOp",EDGE,"E43"),sQuery(id+"F0.wireOp",EDGE,"E44"),sQuery(id+"F0.wireOp",EDGE,"E45"),sQuery(id+"F0.wireOp",EDGE,"E46"),sQuery(id+"F0.wireOp",EDGE,"E47"),sQuery(id+"F0.wireOp",EDGE,"E48"),sQuery(id+"F0.wireOp",EDGE,"E49"),sQuery(id+"F0.wireOp",EDGE,"E50"),sQuery(id+"F0.wireOp",EDGE,"E51"),sQuery(id+"F0.wireOp",EDGE,"E52"),sQuery(id+"F0.wireOp",EDGE,"E53"),sQuery(id+"F0.wireOp",EDGE,"E54"),sQuery(id+"F0.wireOp",EDGE,"E55"),sQuery(id+"F0.wireOp",EDGE,"E56"),sQuery(id+"F0.wireOp",EDGE,"E57"),sQuery(id+"F0.wireOp",EDGE,"E58"),sQuery(id+"F0.wireOp",EDGE,"E59"),sQuery(id+"F0.wireOp",EDGE,"E60"),sQuery(id+"F0.wireOp",EDGE,"E61"),sQuery(id+"F0.wireOp",EDGE,"E62"),sQuery(id+"F0.wireOp",EDGE,"E63"),sQuery(id+"F0.wireOp",EDGE,"E64"),sQuery(id+"F0.wireOp",EDGE,"E65"),sQuery(id+"F0.wireOp",EDGE,"E66"),sQuery(id+"F0.wireOp",EDGE,"E67"),sQuery(id+"F0.wireOp",EDGE,"E68"),sQuery(id+"F0.wireOp",EDGE,"E69"),sQuery(id+"F0.wireOp",EDGE,"E70"),sQuery(id+"F0.wireOp",EDGE,"E71"),sQuery(id+"F0.wireOp",EDGE,"E72"),sQuery(id+"F0.wireOp",EDGE,"E73"),sQuery(id+"F0.wireOp",EDGE,"E74"),sQuery(id+"F0.wireOp",EDGE,"E75"),sQuery(id+"F0.wireOp",EDGE,"E76"),sQuery(id+"F0.wireOp",EDGE,"E77"),sQuery(id+"F0.wireOp",EDGE,"E78"),sQuery(id+"F0.wireOp",EDGE,"E79"),sQuery(id+"F0.wireOp",EDGE,"E80"),sQuery(id+"F0.wireOp",EDGE,"E81"),sQuery(id+"F0.wireOp",EDGE,"E82"),sQuery(id+"F0.wireOp",EDGE,"E83"),sQuery(id+"F0.wireOp",EDGE,"E84"),sQuery(id+"F0.wireOp",EDGE,"E85"),sQuery(id+"F0.wireOp",EDGE,"E86"),sQuery(id+"F0.wireOp",EDGE,"E87"),sQuery(id+"F0.wireOp",EDGE,"E88"),sQuery(id+"F0.wireOp",EDGE,"E89"),sQuery(id+"F0.wireOp",EDGE,"E90"),sQuery(id+"F0.wireOp",EDGE,"E91"),sQuery(id+"F0.wireOp",EDGE,"E92"),sQuery(id+"F0.wireOp",EDGE,"E93"),sQuery(id+"F0.wireOp",EDGE,"E94"),sQuery(id+"F0.wireOp",EDGE,"E95"),sQuery(id+"F0.wireOp",EDGE,"E96"),sQuery(id+"F0.wireOp",EDGE,"E97"),sQuery(id+"F0.wireOp",EDGE,"E98"),sQuery(id+"F0.wireOp",EDGE,"E99"),sQuery(id+"F0.wireOp",EDGE,"E100"),sQuery(id+"F0.wireOp",EDGE,"E101"),sQuery(id+"F0.wireOp",EDGE,"E102"),sQuery(id+"F0.wireOp",EDGE,"E103"),sQuery(id+"F0.wireOp",EDGE,"E104"),sQuery(id+"F0.wireOp",EDGE,"E105"),sQuery(id+"F0.wireOp",EDGE,"E106"),sQuery(id+"F0.wireOp",EDGE,"E107"),sQuery(id+"F0.wireOp",EDGE,"E108"),sQuery(id+"F0.wireOp",EDGE,"E109"),sQuery(id+"F0.wireOp",EDGE,"E110"),sQuery(id+"F0.wireOp",EDGE,"E111"),sQuery(id+"F0.wireOp",EDGE,"E112"),sQuery(id+"F0.wireOp",EDGE,"E113"),sQuery(id+"F0.wireOp",EDGE,"E114"),sQuery(id+"F0.wireOp",EDGE,"E115")])],"isStart":false})]});
            var Q28;
            Q28=makeQuery(id+"F6.opFillet","BLEND_EDGE",EDGE,{"blendedFrom":[makeQuery(id+"F5.boolean.opBoolean","COPY",EDGE,{"derivedFrom":makeQuery(id+"F5.opExtrude","CAP_EDGE",EDGE,{"disambiguationData":[OSD([sQuery(id+"F4.wireOp",EDGE,"E757.2.3.0")])],"isStart":false})}),makeQuery(id+"F1.opExtrude","CAP_FACE",FACE,{"disambiguationData":[OSD([sQuery(id+"F0.wireOp",EDGE,"E0"),sQuery(id+"F0.wireOp",EDGE,"E1"),sQuery(id+"F0.wireOp",EDGE,"E2"),sQuery(id+"F0.wireOp",EDGE,"E3"),sQuery(id+"F0.wireOp",EDGE,"E4"),sQuery(id+"F0.wireOp",EDGE,"E5"),sQuery(id+"F0.wireOp",EDGE,"E6"),sQuery(id+"F0.wireOp",EDGE,"E7"),sQuery(id+"F0.wireOp",EDGE,"E8"),sQuery(id+"F0.wireOp",EDGE,"E9"),sQuery(id+"F0.wireOp",EDGE,"E10"),sQuery(id+"F0.wireOp",EDGE,"E11"),sQuery(id+"F0.wireOp",EDGE,"E12"),sQuery(id+"F0.wireOp",EDGE,"E13"),sQuery(id+"F0.wireOp",EDGE,"E14"),sQuery(id+"F0.wireOp",EDGE,"E15"),sQuery(id+"F0.wireOp",EDGE,"E16"),sQuery(id+"F0.wireOp",EDGE,"E17"),sQuery(id+"F0.wireOp",EDGE,"E18"),sQuery(id+"F0.wireOp",EDGE,"E19"),sQuery(id+"F0.wireOp",EDGE,"E20"),sQuery(id+"F0.wireOp",EDGE,"E21"),sQuery(id+"F0.wireOp",EDGE,"E22"),sQuery(id+"F0.wireOp",EDGE,"E23"),sQuery(id+"F0.wireOp",EDGE,"E24"),sQuery(id+"F0.wireOp",EDGE,"E25"),sQuery(id+"F0.wireOp",EDGE,"E26"),sQuery(id+"F0.wireOp",EDGE,"E27"),sQuery(id+"F0.wireOp",EDGE,"E28"),sQuery(id+"F0.wireOp",EDGE,"E29"),sQuery(id+"F0.wireOp",EDGE,"E30"),sQuery(id+"F0.wireOp",EDGE,"E31"),sQuery(id+"F0.wireOp",EDGE,"E32"),sQuery(id+"F0.wireOp",EDGE,"E33"),sQuery(id+"F0.wireOp",EDGE,"E34"),sQuery(id+"F0.wireOp",EDGE,"E35"),sQuery(id+"F0.wireOp",EDGE,"E36"),sQuery(id+"F0.wireOp",EDGE,"E37"),sQuery(id+"F0.wireOp",EDGE,"E38"),sQuery(id+"F0.wireOp",EDGE,"E39"),sQuery(id+"F0.wireOp",EDGE,"E40"),sQuery(id+"F0.wireOp",EDGE,"E41"),sQuery(id+"F0.wireOp",EDGE,"E42"),sQuery(id+"F0.wireOp",EDGE,"E43"),sQuery(id+"F0.wireOp",EDGE,"E44"),sQuery(id+"F0.wireOp",EDGE,"E45"),sQuery(id+"F0.wireOp",EDGE,"E46"),sQuery(id+"F0.wireOp",EDGE,"E47"),sQuery(id+"F0.wireOp",EDGE,"E48"),sQuery(id+"F0.wireOp",EDGE,"E49"),sQuery(id+"F0.wireOp",EDGE,"E50"),sQuery(id+"F0.wireOp",EDGE,"E51"),sQuery(id+"F0.wireOp",EDGE,"E52"),sQuery(id+"F0.wireOp",EDGE,"E53"),sQuery(id+"F0.wireOp",EDGE,"E54"),sQuery(id+"F0.wireOp",EDGE,"E55"),sQuery(id+"F0.wireOp",EDGE,"E56"),sQuery(id+"F0.wireOp",EDGE,"E57"),sQuery(id+"F0.wireOp",EDGE,"E58"),sQuery(id+"F0.wireOp",EDGE,"E59"),sQuery(id+"F0.wireOp",EDGE,"E60"),sQuery(id+"F0.wireOp",EDGE,"E61"),sQuery(id+"F0.wireOp",EDGE,"E62"),sQuery(id+"F0.wireOp",EDGE,"E63"),sQuery(id+"F0.wireOp",EDGE,"E64"),sQuery(id+"F0.wireOp",EDGE,"E65"),sQuery(id+"F0.wireOp",EDGE,"E66"),sQuery(id+"F0.wireOp",EDGE,"E67"),sQuery(id+"F0.wireOp",EDGE,"E68"),sQuery(id+"F0.wireOp",EDGE,"E69"),sQuery(id+"F0.wireOp",EDGE,"E70"),sQuery(id+"F0.wireOp",EDGE,"E71"),sQuery(id+"F0.wireOp",EDGE,"E72"),sQuery(id+"F0.wireOp",EDGE,"E73"),sQuery(id+"F0.wireOp",EDGE,"E74"),sQuery(id+"F0.wireOp",EDGE,"E75"),sQuery(id+"F0.wireOp",EDGE,"E76"),sQuery(id+"F0.wireOp",EDGE,"E77"),sQuery(id+"F0.wireOp",EDGE,"E78"),sQuery(id+"F0.wireOp",EDGE,"E79"),sQuery(id+"F0.wireOp",EDGE,"E80"),sQuery(id+"F0.wireOp",EDGE,"E81"),sQuery(id+"F0.wireOp",EDGE,"E82"),sQuery(id+"F0.wireOp",EDGE,"E83"),sQuery(id+"F0.wireOp",EDGE,"E84"),sQuery(id+"F0.wireOp",EDGE,"E85"),sQuery(id+"F0.wireOp",EDGE,"E86"),sQuery(id+"F0.wireOp",EDGE,"E87"),sQuery(id+"F0.wireOp",EDGE,"E88"),sQuery(id+"F0.wireOp",EDGE,"E89"),sQuery(id+"F0.wireOp",EDGE,"E90"),sQuery(id+"F0.wireOp",EDGE,"E91"),sQuery(id+"F0.wireOp",EDGE,"E92"),sQuery(id+"F0.wireOp",EDGE,"E93"),sQuery(id+"F0.wireOp",EDGE,"E94"),sQuery(id+"F0.wireOp",EDGE,"E95"),sQuery(id+"F0.wireOp",EDGE,"E96"),sQuery(id+"F0.wireOp",EDGE,"E97"),sQuery(id+"F0.wireOp",EDGE,"E98"),sQuery(id+"F0.wireOp",EDGE,"E99"),sQuery(id+"F0.wireOp",EDGE,"E100"),sQuery(id+"F0.wireOp",EDGE,"E101"),sQuery(id+"F0.wireOp",EDGE,"E102"),sQuery(id+"F0.wireOp",EDGE,"E103"),sQuery(id+"F0.wireOp",EDGE,"E104"),sQuery(id+"F0.wireOp",EDGE,"E105"),sQuery(id+"F0.wireOp",EDGE,"E106"),sQuery(id+"F0.wireOp",EDGE,"E107"),sQuery(id+"F0.wireOp",EDGE,"E108"),sQuery(id+"F0.wireOp",EDGE,"E109"),sQuery(id+"F0.wireOp",EDGE,"E110"),sQuery(id+"F0.wireOp",EDGE,"E111"),sQuery(id+"F0.wireOp",EDGE,"E112"),sQuery(id+"F0.wireOp",EDGE,"E113"),sQuery(id+"F0.wireOp",EDGE,"E114"),sQuery(id+"F0.wireOp",EDGE,"E115")])],"isStart":false})],"blendedInto":[makeQuery(id+"F1.opExtrude","CAP_FACE",FACE,{"disambiguationData":[OSD([sQuery(id+"F0.wireOp",EDGE,"E0"),sQuery(id+"F0.wireOp",EDGE,"E1"),sQuery(id+"F0.wireOp",EDGE,"E2"),sQuery(id+"F0.wireOp",EDGE,"E3"),sQuery(id+"F0.wireOp",EDGE,"E4"),sQuery(id+"F0.wireOp",EDGE,"E5"),sQuery(id+"F0.wireOp",EDGE,"E6"),sQuery(id+"F0.wireOp",EDGE,"E7"),sQuery(id+"F0.wireOp",EDGE,"E8"),sQuery(id+"F0.wireOp",EDGE,"E9"),sQuery(id+"F0.wireOp",EDGE,"E10"),sQuery(id+"F0.wireOp",EDGE,"E11"),sQuery(id+"F0.wireOp",EDGE,"E12"),sQuery(id+"F0.wireOp",EDGE,"E13"),sQuery(id+"F0.wireOp",EDGE,"E14"),sQuery(id+"F0.wireOp",EDGE,"E15"),sQuery(id+"F0.wireOp",EDGE,"E16"),sQuery(id+"F0.wireOp",EDGE,"E17"),sQuery(id+"F0.wireOp",EDGE,"E18"),sQuery(id+"F0.wireOp",EDGE,"E19"),sQuery(id+"F0.wireOp",EDGE,"E20"),sQuery(id+"F0.wireOp",EDGE,"E21"),sQuery(id+"F0.wireOp",EDGE,"E22"),sQuery(id+"F0.wireOp",EDGE,"E23"),sQuery(id+"F0.wireOp",EDGE,"E24"),sQuery(id+"F0.wireOp",EDGE,"E25"),sQuery(id+"F0.wireOp",EDGE,"E26"),sQuery(id+"F0.wireOp",EDGE,"E27"),sQuery(id+"F0.wireOp",EDGE,"E28"),sQuery(id+"F0.wireOp",EDGE,"E29"),sQuery(id+"F0.wireOp",EDGE,"E30"),sQuery(id+"F0.wireOp",EDGE,"E31"),sQuery(id+"F0.wireOp",EDGE,"E32"),sQuery(id+"F0.wireOp",EDGE,"E33"),sQuery(id+"F0.wireOp",EDGE,"E34"),sQuery(id+"F0.wireOp",EDGE,"E35"),sQuery(id+"F0.wireOp",EDGE,"E36"),sQuery(id+"F0.wireOp",EDGE,"E37"),sQuery(id+"F0.wireOp",EDGE,"E38"),sQuery(id+"F0.wireOp",EDGE,"E39"),sQuery(id+"F0.wireOp",EDGE,"E40"),sQuery(id+"F0.wireOp",EDGE,"E41"),sQuery(id+"F0.wireOp",EDGE,"E42"),sQuery(id+"F0.wireOp",EDGE,"E43"),sQuery(id+"F0.wireOp",EDGE,"E44"),sQuery(id+"F0.wireOp",EDGE,"E45"),sQuery(id+"F0.wireOp",EDGE,"E46"),sQuery(id+"F0.wireOp",EDGE,"E47"),sQuery(id+"F0.wireOp",EDGE,"E48"),sQuery(id+"F0.wireOp",EDGE,"E49"),sQuery(id+"F0.wireOp",EDGE,"E50"),sQuery(id+"F0.wireOp",EDGE,"E51"),sQuery(id+"F0.wireOp",EDGE,"E52"),sQuery(id+"F0.wireOp",EDGE,"E53"),sQuery(id+"F0.wireOp",EDGE,"E54"),sQuery(id+"F0.wireOp",EDGE,"E55"),sQuery(id+"F0.wireOp",EDGE,"E56"),sQuery(id+"F0.wireOp",EDGE,"E57"),sQuery(id+"F0.wireOp",EDGE,"E58"),sQuery(id+"F0.wireOp",EDGE,"E59"),sQuery(id+"F0.wireOp",EDGE,"E60"),sQuery(id+"F0.wireOp",EDGE,"E61"),sQuery(id+"F0.wireOp",EDGE,"E62"),sQuery(id+"F0.wireOp",EDGE,"E63"),sQuery(id+"F0.wireOp",EDGE,"E64"),sQuery(id+"F0.wireOp",EDGE,"E65"),sQuery(id+"F0.wireOp",EDGE,"E66"),sQuery(id+"F0.wireOp",EDGE,"E67"),sQuery(id+"F0.wireOp",EDGE,"E68"),sQuery(id+"F0.wireOp",EDGE,"E69"),sQuery(id+"F0.wireOp",EDGE,"E70"),sQuery(id+"F0.wireOp",EDGE,"E71"),sQuery(id+"F0.wireOp",EDGE,"E72"),sQuery(id+"F0.wireOp",EDGE,"E73"),sQuery(id+"F0.wireOp",EDGE,"E74"),sQuery(id+"F0.wireOp",EDGE,"E75"),sQuery(id+"F0.wireOp",EDGE,"E76"),sQuery(id+"F0.wireOp",EDGE,"E77"),sQuery(id+"F0.wireOp",EDGE,"E78"),sQuery(id+"F0.wireOp",EDGE,"E79"),sQuery(id+"F0.wireOp",EDGE,"E80"),sQuery(id+"F0.wireOp",EDGE,"E81"),sQuery(id+"F0.wireOp",EDGE,"E82"),sQuery(id+"F0.wireOp",EDGE,"E83"),sQuery(id+"F0.wireOp",EDGE,"E84"),sQuery(id+"F0.wireOp",EDGE,"E85"),sQuery(id+"F0.wireOp",EDGE,"E86"),sQuery(id+"F0.wireOp",EDGE,"E87"),sQuery(id+"F0.wireOp",EDGE,"E88"),sQuery(id+"F0.wireOp",EDGE,"E89"),sQuery(id+"F0.wireOp",EDGE,"E90"),sQuery(id+"F0.wireOp",EDGE,"E91"),sQuery(id+"F0.wireOp",EDGE,"E92"),sQuery(id+"F0.wireOp",EDGE,"E93"),sQuery(id+"F0.wireOp",EDGE,"E94"),sQuery(id+"F0.wireOp",EDGE,"E95"),sQuery(id+"F0.wireOp",EDGE,"E96"),sQuery(id+"F0.wireOp",EDGE,"E97"),sQuery(id+"F0.wireOp",EDGE,"E98"),sQuery(id+"F0.wireOp",EDGE,"E99"),sQuery(id+"F0.wireOp",EDGE,"E100"),sQuery(id+"F0.wireOp",EDGE,"E101"),sQuery(id+"F0.wireOp",EDGE,"E102"),sQuery(id+"F0.wireOp",EDGE,"E103"),sQuery(id+"F0.wireOp",EDGE,"E104"),sQuery(id+"F0.wireOp",EDGE,"E105"),sQuery(id+"F0.wireOp",EDGE,"E106"),sQuery(id+"F0.wireOp",EDGE,"E107"),sQuery(id+"F0.wireOp",EDGE,"E108"),sQuery(id+"F0.wireOp",EDGE,"E109"),sQuery(id+"F0.wireOp",EDGE,"E110"),sQuery(id+"F0.wireOp",EDGE,"E111"),sQuery(id+"F0.wireOp",EDGE,"E112"),sQuery(id+"F0.wireOp",EDGE,"E113"),sQuery(id+"F0.wireOp",EDGE,"E114"),sQuery(id+"F0.wireOp",EDGE,"E115")])],"isStart":false})]});
            var Q29;
            Q29=makeQuery(id+"F6.opFillet","BLEND_EDGE",EDGE,{"blendedFrom":[makeQuery(id+"F5.boolean.opBoolean","COPY",EDGE,{"derivedFrom":makeQuery(id+"F5.opExtrude","CAP_EDGE",EDGE,{"disambiguationData":[OSD([sQuery(id+"F4.wireOp",EDGE,"E757.1.3.0")])],"isStart":false})}),makeQuery(id+"F1.opExtrude","CAP_FACE",FACE,{"disambiguationData":[OSD([sQuery(id+"F0.wireOp",EDGE,"E0"),sQuery(id+"F0.wireOp",EDGE,"E1"),sQuery(id+"F0.wireOp",EDGE,"E2"),sQuery(id+"F0.wireOp",EDGE,"E3"),sQuery(id+"F0.wireOp",EDGE,"E4"),sQuery(id+"F0.wireOp",EDGE,"E5"),sQuery(id+"F0.wireOp",EDGE,"E6"),sQuery(id+"F0.wireOp",EDGE,"E7"),sQuery(id+"F0.wireOp",EDGE,"E8"),sQuery(id+"F0.wireOp",EDGE,"E9"),sQuery(id+"F0.wireOp",EDGE,"E10"),sQuery(id+"F0.wireOp",EDGE,"E11"),sQuery(id+"F0.wireOp",EDGE,"E12"),sQuery(id+"F0.wireOp",EDGE,"E13"),sQuery(id+"F0.wireOp",EDGE,"E14"),sQuery(id+"F0.wireOp",EDGE,"E15"),sQuery(id+"F0.wireOp",EDGE,"E16"),sQuery(id+"F0.wireOp",EDGE,"E17"),sQuery(id+"F0.wireOp",EDGE,"E18"),sQuery(id+"F0.wireOp",EDGE,"E19"),sQuery(id+"F0.wireOp",EDGE,"E20"),sQuery(id+"F0.wireOp",EDGE,"E21"),sQuery(id+"F0.wireOp",EDGE,"E22"),sQuery(id+"F0.wireOp",EDGE,"E23"),sQuery(id+"F0.wireOp",EDGE,"E24"),sQuery(id+"F0.wireOp",EDGE,"E25"),sQuery(id+"F0.wireOp",EDGE,"E26"),sQuery(id+"F0.wireOp",EDGE,"E27"),sQuery(id+"F0.wireOp",EDGE,"E28"),sQuery(id+"F0.wireOp",EDGE,"E29"),sQuery(id+"F0.wireOp",EDGE,"E30"),sQuery(id+"F0.wireOp",EDGE,"E31"),sQuery(id+"F0.wireOp",EDGE,"E32"),sQuery(id+"F0.wireOp",EDGE,"E33"),sQuery(id+"F0.wireOp",EDGE,"E34"),sQuery(id+"F0.wireOp",EDGE,"E35"),sQuery(id+"F0.wireOp",EDGE,"E36"),sQuery(id+"F0.wireOp",EDGE,"E37"),sQuery(id+"F0.wireOp",EDGE,"E38"),sQuery(id+"F0.wireOp",EDGE,"E39"),sQuery(id+"F0.wireOp",EDGE,"E40"),sQuery(id+"F0.wireOp",EDGE,"E41"),sQuery(id+"F0.wireOp",EDGE,"E42"),sQuery(id+"F0.wireOp",EDGE,"E43"),sQuery(id+"F0.wireOp",EDGE,"E44"),sQuery(id+"F0.wireOp",EDGE,"E45"),sQuery(id+"F0.wireOp",EDGE,"E46"),sQuery(id+"F0.wireOp",EDGE,"E47"),sQuery(id+"F0.wireOp",EDGE,"E48"),sQuery(id+"F0.wireOp",EDGE,"E49"),sQuery(id+"F0.wireOp",EDGE,"E50"),sQuery(id+"F0.wireOp",EDGE,"E51"),sQuery(id+"F0.wireOp",EDGE,"E52"),sQuery(id+"F0.wireOp",EDGE,"E53"),sQuery(id+"F0.wireOp",EDGE,"E54"),sQuery(id+"F0.wireOp",EDGE,"E55"),sQuery(id+"F0.wireOp",EDGE,"E56"),sQuery(id+"F0.wireOp",EDGE,"E57"),sQuery(id+"F0.wireOp",EDGE,"E58"),sQuery(id+"F0.wireOp",EDGE,"E59"),sQuery(id+"F0.wireOp",EDGE,"E60"),sQuery(id+"F0.wireOp",EDGE,"E61"),sQuery(id+"F0.wireOp",EDGE,"E62"),sQuery(id+"F0.wireOp",EDGE,"E63"),sQuery(id+"F0.wireOp",EDGE,"E64"),sQuery(id+"F0.wireOp",EDGE,"E65"),sQuery(id+"F0.wireOp",EDGE,"E66"),sQuery(id+"F0.wireOp",EDGE,"E67"),sQuery(id+"F0.wireOp",EDGE,"E68"),sQuery(id+"F0.wireOp",EDGE,"E69"),sQuery(id+"F0.wireOp",EDGE,"E70"),sQuery(id+"F0.wireOp",EDGE,"E71"),sQuery(id+"F0.wireOp",EDGE,"E72"),sQuery(id+"F0.wireOp",EDGE,"E73"),sQuery(id+"F0.wireOp",EDGE,"E74"),sQuery(id+"F0.wireOp",EDGE,"E75"),sQuery(id+"F0.wireOp",EDGE,"E76"),sQuery(id+"F0.wireOp",EDGE,"E77"),sQuery(id+"F0.wireOp",EDGE,"E78"),sQuery(id+"F0.wireOp",EDGE,"E79"),sQuery(id+"F0.wireOp",EDGE,"E80"),sQuery(id+"F0.wireOp",EDGE,"E81"),sQuery(id+"F0.wireOp",EDGE,"E82"),sQuery(id+"F0.wireOp",EDGE,"E83"),sQuery(id+"F0.wireOp",EDGE,"E84"),sQuery(id+"F0.wireOp",EDGE,"E85"),sQuery(id+"F0.wireOp",EDGE,"E86"),sQuery(id+"F0.wireOp",EDGE,"E87"),sQuery(id+"F0.wireOp",EDGE,"E88"),sQuery(id+"F0.wireOp",EDGE,"E89"),sQuery(id+"F0.wireOp",EDGE,"E90"),sQuery(id+"F0.wireOp",EDGE,"E91"),sQuery(id+"F0.wireOp",EDGE,"E92"),sQuery(id+"F0.wireOp",EDGE,"E93"),sQuery(id+"F0.wireOp",EDGE,"E94"),sQuery(id+"F0.wireOp",EDGE,"E95"),sQuery(id+"F0.wireOp",EDGE,"E96"),sQuery(id+"F0.wireOp",EDGE,"E97"),sQuery(id+"F0.wireOp",EDGE,"E98"),sQuery(id+"F0.wireOp",EDGE,"E99"),sQuery(id+"F0.wireOp",EDGE,"E100"),sQuery(id+"F0.wireOp",EDGE,"E101"),sQuery(id+"F0.wireOp",EDGE,"E102"),sQuery(id+"F0.wireOp",EDGE,"E103"),sQuery(id+"F0.wireOp",EDGE,"E104"),sQuery(id+"F0.wireOp",EDGE,"E105"),sQuery(id+"F0.wireOp",EDGE,"E106"),sQuery(id+"F0.wireOp",EDGE,"E107"),sQuery(id+"F0.wireOp",EDGE,"E108"),sQuery(id+"F0.wireOp",EDGE,"E109"),sQuery(id+"F0.wireOp",EDGE,"E110"),sQuery(id+"F0.wireOp",EDGE,"E111"),sQuery(id+"F0.wireOp",EDGE,"E112"),sQuery(id+"F0.wireOp",EDGE,"E113"),sQuery(id+"F0.wireOp",EDGE,"E114"),sQuery(id+"F0.wireOp",EDGE,"E115")])],"isStart":false})],"blendedInto":[makeQuery(id+"F1.opExtrude","CAP_FACE",FACE,{"disambiguationData":[OSD([sQuery(id+"F0.wireOp",EDGE,"E0"),sQuery(id+"F0.wireOp",EDGE,"E1"),sQuery(id+"F0.wireOp",EDGE,"E2"),sQuery(id+"F0.wireOp",EDGE,"E3"),sQuery(id+"F0.wireOp",EDGE,"E4"),sQuery(id+"F0.wireOp",EDGE,"E5"),sQuery(id+"F0.wireOp",EDGE,"E6"),sQuery(id+"F0.wireOp",EDGE,"E7"),sQuery(id+"F0.wireOp",EDGE,"E8"),sQuery(id+"F0.wireOp",EDGE,"E9"),sQuery(id+"F0.wireOp",EDGE,"E10"),sQuery(id+"F0.wireOp",EDGE,"E11"),sQuery(id+"F0.wireOp",EDGE,"E12"),sQuery(id+"F0.wireOp",EDGE,"E13"),sQuery(id+"F0.wireOp",EDGE,"E14"),sQuery(id+"F0.wireOp",EDGE,"E15"),sQuery(id+"F0.wireOp",EDGE,"E16"),sQuery(id+"F0.wireOp",EDGE,"E17"),sQuery(id+"F0.wireOp",EDGE,"E18"),sQuery(id+"F0.wireOp",EDGE,"E19"),sQuery(id+"F0.wireOp",EDGE,"E20"),sQuery(id+"F0.wireOp",EDGE,"E21"),sQuery(id+"F0.wireOp",EDGE,"E22"),sQuery(id+"F0.wireOp",EDGE,"E23"),sQuery(id+"F0.wireOp",EDGE,"E24"),sQuery(id+"F0.wireOp",EDGE,"E25"),sQuery(id+"F0.wireOp",EDGE,"E26"),sQuery(id+"F0.wireOp",EDGE,"E27"),sQuery(id+"F0.wireOp",EDGE,"E28"),sQuery(id+"F0.wireOp",EDGE,"E29"),sQuery(id+"F0.wireOp",EDGE,"E30"),sQuery(id+"F0.wireOp",EDGE,"E31"),sQuery(id+"F0.wireOp",EDGE,"E32"),sQuery(id+"F0.wireOp",EDGE,"E33"),sQuery(id+"F0.wireOp",EDGE,"E34"),sQuery(id+"F0.wireOp",EDGE,"E35"),sQuery(id+"F0.wireOp",EDGE,"E36"),sQuery(id+"F0.wireOp",EDGE,"E37"),sQuery(id+"F0.wireOp",EDGE,"E38"),sQuery(id+"F0.wireOp",EDGE,"E39"),sQuery(id+"F0.wireOp",EDGE,"E40"),sQuery(id+"F0.wireOp",EDGE,"E41"),sQuery(id+"F0.wireOp",EDGE,"E42"),sQuery(id+"F0.wireOp",EDGE,"E43"),sQuery(id+"F0.wireOp",EDGE,"E44"),sQuery(id+"F0.wireOp",EDGE,"E45"),sQuery(id+"F0.wireOp",EDGE,"E46"),sQuery(id+"F0.wireOp",EDGE,"E47"),sQuery(id+"F0.wireOp",EDGE,"E48"),sQuery(id+"F0.wireOp",EDGE,"E49"),sQuery(id+"F0.wireOp",EDGE,"E50"),sQuery(id+"F0.wireOp",EDGE,"E51"),sQuery(id+"F0.wireOp",EDGE,"E52"),sQuery(id+"F0.wireOp",EDGE,"E53"),sQuery(id+"F0.wireOp",EDGE,"E54"),sQuery(id+"F0.wireOp",EDGE,"E55"),sQuery(id+"F0.wireOp",EDGE,"E56"),sQuery(id+"F0.wireOp",EDGE,"E57"),sQuery(id+"F0.wireOp",EDGE,"E58"),sQuery(id+"F0.wireOp",EDGE,"E59"),sQuery(id+"F0.wireOp",EDGE,"E60"),sQuery(id+"F0.wireOp",EDGE,"E61"),sQuery(id+"F0.wireOp",EDGE,"E62"),sQuery(id+"F0.wireOp",EDGE,"E63"),sQuery(id+"F0.wireOp",EDGE,"E64"),sQuery(id+"F0.wireOp",EDGE,"E65"),sQuery(id+"F0.wireOp",EDGE,"E66"),sQuery(id+"F0.wireOp",EDGE,"E67"),sQuery(id+"F0.wireOp",EDGE,"E68"),sQuery(id+"F0.wireOp",EDGE,"E69"),sQuery(id+"F0.wireOp",EDGE,"E70"),sQuery(id+"F0.wireOp",EDGE,"E71"),sQuery(id+"F0.wireOp",EDGE,"E72"),sQuery(id+"F0.wireOp",EDGE,"E73"),sQuery(id+"F0.wireOp",EDGE,"E74"),sQuery(id+"F0.wireOp",EDGE,"E75"),sQuery(id+"F0.wireOp",EDGE,"E76"),sQuery(id+"F0.wireOp",EDGE,"E77"),sQuery(id+"F0.wireOp",EDGE,"E78"),sQuery(id+"F0.wireOp",EDGE,"E79"),sQuery(id+"F0.wireOp",EDGE,"E80"),sQuery(id+"F0.wireOp",EDGE,"E81"),sQuery(id+"F0.wireOp",EDGE,"E82"),sQuery(id+"F0.wireOp",EDGE,"E83"),sQuery(id+"F0.wireOp",EDGE,"E84"),sQuery(id+"F0.wireOp",EDGE,"E85"),sQuery(id+"F0.wireOp",EDGE,"E86"),sQuery(id+"F0.wireOp",EDGE,"E87"),sQuery(id+"F0.wireOp",EDGE,"E88"),sQuery(id+"F0.wireOp",EDGE,"E89"),sQuery(id+"F0.wireOp",EDGE,"E90"),sQuery(id+"F0.wireOp",EDGE,"E91"),sQuery(id+"F0.wireOp",EDGE,"E92"),sQuery(id+"F0.wireOp",EDGE,"E93"),sQuery(id+"F0.wireOp",EDGE,"E94"),sQuery(id+"F0.wireOp",EDGE,"E95"),sQuery(id+"F0.wireOp",EDGE,"E96"),sQuery(id+"F0.wireOp",EDGE,"E97"),sQuery(id+"F0.wireOp",EDGE,"E98"),sQuery(id+"F0.wireOp",EDGE,"E99"),sQuery(id+"F0.wireOp",EDGE,"E100"),sQuery(id+"F0.wireOp",EDGE,"E101"),sQuery(id+"F0.wireOp",EDGE,"E102"),sQuery(id+"F0.wireOp",EDGE,"E103"),sQuery(id+"F0.wireOp",EDGE,"E104"),sQuery(id+"F0.wireOp",EDGE,"E105"),sQuery(id+"F0.wireOp",EDGE,"E106"),sQuery(id+"F0.wireOp",EDGE,"E107"),sQuery(id+"F0.wireOp",EDGE,"E108"),sQuery(id+"F0.wireOp",EDGE,"E109"),sQuery(id+"F0.wireOp",EDGE,"E110"),sQuery(id+"F0.wireOp",EDGE,"E111"),sQuery(id+"F0.wireOp",EDGE,"E112"),sQuery(id+"F0.wireOp",EDGE,"E113"),sQuery(id+"F0.wireOp",EDGE,"E114"),sQuery(id+"F0.wireOp",EDGE,"E115")])],"isStart":false})]});
            var Q30;
            Q30=makeQuery(id+"F6.opFillet","BLEND_EDGE",EDGE,{"blendedFrom":[makeQuery(id+"F5.boolean.opBoolean","COPY",EDGE,{"derivedFrom":makeQuery(id+"F5.opExtrude","CAP_EDGE",EDGE,{"disambiguationData":[OSD([sQuery(id+"F4.wireOp",EDGE,"E757.0.3.0")])],"isStart":false})}),makeQuery(id+"F1.opExtrude","CAP_FACE",FACE,{"disambiguationData":[OSD([sQuery(id+"F0.wireOp",EDGE,"E0"),sQuery(id+"F0.wireOp",EDGE,"E1"),sQuery(id+"F0.wireOp",EDGE,"E2"),sQuery(id+"F0.wireOp",EDGE,"E3"),sQuery(id+"F0.wireOp",EDGE,"E4"),sQuery(id+"F0.wireOp",EDGE,"E5"),sQuery(id+"F0.wireOp",EDGE,"E6"),sQuery(id+"F0.wireOp",EDGE,"E7"),sQuery(id+"F0.wireOp",EDGE,"E8"),sQuery(id+"F0.wireOp",EDGE,"E9"),sQuery(id+"F0.wireOp",EDGE,"E10"),sQuery(id+"F0.wireOp",EDGE,"E11"),sQuery(id+"F0.wireOp",EDGE,"E12"),sQuery(id+"F0.wireOp",EDGE,"E13"),sQuery(id+"F0.wireOp",EDGE,"E14"),sQuery(id+"F0.wireOp",EDGE,"E15"),sQuery(id+"F0.wireOp",EDGE,"E16"),sQuery(id+"F0.wireOp",EDGE,"E17"),sQuery(id+"F0.wireOp",EDGE,"E18"),sQuery(id+"F0.wireOp",EDGE,"E19"),sQuery(id+"F0.wireOp",EDGE,"E20"),sQuery(id+"F0.wireOp",EDGE,"E21"),sQuery(id+"F0.wireOp",EDGE,"E22"),sQuery(id+"F0.wireOp",EDGE,"E23"),sQuery(id+"F0.wireOp",EDGE,"E24"),sQuery(id+"F0.wireOp",EDGE,"E25"),sQuery(id+"F0.wireOp",EDGE,"E26"),sQuery(id+"F0.wireOp",EDGE,"E27"),sQuery(id+"F0.wireOp",EDGE,"E28"),sQuery(id+"F0.wireOp",EDGE,"E29"),sQuery(id+"F0.wireOp",EDGE,"E30"),sQuery(id+"F0.wireOp",EDGE,"E31"),sQuery(id+"F0.wireOp",EDGE,"E32"),sQuery(id+"F0.wireOp",EDGE,"E33"),sQuery(id+"F0.wireOp",EDGE,"E34"),sQuery(id+"F0.wireOp",EDGE,"E35"),sQuery(id+"F0.wireOp",EDGE,"E36"),sQuery(id+"F0.wireOp",EDGE,"E37"),sQuery(id+"F0.wireOp",EDGE,"E38"),sQuery(id+"F0.wireOp",EDGE,"E39"),sQuery(id+"F0.wireOp",EDGE,"E40"),sQuery(id+"F0.wireOp",EDGE,"E41"),sQuery(id+"F0.wireOp",EDGE,"E42"),sQuery(id+"F0.wireOp",EDGE,"E43"),sQuery(id+"F0.wireOp",EDGE,"E44"),sQuery(id+"F0.wireOp",EDGE,"E45"),sQuery(id+"F0.wireOp",EDGE,"E46"),sQuery(id+"F0.wireOp",EDGE,"E47"),sQuery(id+"F0.wireOp",EDGE,"E48"),sQuery(id+"F0.wireOp",EDGE,"E49"),sQuery(id+"F0.wireOp",EDGE,"E50"),sQuery(id+"F0.wireOp",EDGE,"E51"),sQuery(id+"F0.wireOp",EDGE,"E52"),sQuery(id+"F0.wireOp",EDGE,"E53"),sQuery(id+"F0.wireOp",EDGE,"E54"),sQuery(id+"F0.wireOp",EDGE,"E55"),sQuery(id+"F0.wireOp",EDGE,"E56"),sQuery(id+"F0.wireOp",EDGE,"E57"),sQuery(id+"F0.wireOp",EDGE,"E58"),sQuery(id+"F0.wireOp",EDGE,"E59"),sQuery(id+"F0.wireOp",EDGE,"E60"),sQuery(id+"F0.wireOp",EDGE,"E61"),sQuery(id+"F0.wireOp",EDGE,"E62"),sQuery(id+"F0.wireOp",EDGE,"E63"),sQuery(id+"F0.wireOp",EDGE,"E64"),sQuery(id+"F0.wireOp",EDGE,"E65"),sQuery(id+"F0.wireOp",EDGE,"E66"),sQuery(id+"F0.wireOp",EDGE,"E67"),sQuery(id+"F0.wireOp",EDGE,"E68"),sQuery(id+"F0.wireOp",EDGE,"E69"),sQuery(id+"F0.wireOp",EDGE,"E70"),sQuery(id+"F0.wireOp",EDGE,"E71"),sQuery(id+"F0.wireOp",EDGE,"E72"),sQuery(id+"F0.wireOp",EDGE,"E73"),sQuery(id+"F0.wireOp",EDGE,"E74"),sQuery(id+"F0.wireOp",EDGE,"E75"),sQuery(id+"F0.wireOp",EDGE,"E76"),sQuery(id+"F0.wireOp",EDGE,"E77"),sQuery(id+"F0.wireOp",EDGE,"E78"),sQuery(id+"F0.wireOp",EDGE,"E79"),sQuery(id+"F0.wireOp",EDGE,"E80"),sQuery(id+"F0.wireOp",EDGE,"E81"),sQuery(id+"F0.wireOp",EDGE,"E82"),sQuery(id+"F0.wireOp",EDGE,"E83"),sQuery(id+"F0.wireOp",EDGE,"E84"),sQuery(id+"F0.wireOp",EDGE,"E85"),sQuery(id+"F0.wireOp",EDGE,"E86"),sQuery(id+"F0.wireOp",EDGE,"E87"),sQuery(id+"F0.wireOp",EDGE,"E88"),sQuery(id+"F0.wireOp",EDGE,"E89"),sQuery(id+"F0.wireOp",EDGE,"E90"),sQuery(id+"F0.wireOp",EDGE,"E91"),sQuery(id+"F0.wireOp",EDGE,"E92"),sQuery(id+"F0.wireOp",EDGE,"E93"),sQuery(id+"F0.wireOp",EDGE,"E94"),sQuery(id+"F0.wireOp",EDGE,"E95"),sQuery(id+"F0.wireOp",EDGE,"E96"),sQuery(id+"F0.wireOp",EDGE,"E97"),sQuery(id+"F0.wireOp",EDGE,"E98"),sQuery(id+"F0.wireOp",EDGE,"E99"),sQuery(id+"F0.wireOp",EDGE,"E100"),sQuery(id+"F0.wireOp",EDGE,"E101"),sQuery(id+"F0.wireOp",EDGE,"E102"),sQuery(id+"F0.wireOp",EDGE,"E103"),sQuery(id+"F0.wireOp",EDGE,"E104"),sQuery(id+"F0.wireOp",EDGE,"E105"),sQuery(id+"F0.wireOp",EDGE,"E106"),sQuery(id+"F0.wireOp",EDGE,"E107"),sQuery(id+"F0.wireOp",EDGE,"E108"),sQuery(id+"F0.wireOp",EDGE,"E109"),sQuery(id+"F0.wireOp",EDGE,"E110"),sQuery(id+"F0.wireOp",EDGE,"E111"),sQuery(id+"F0.wireOp",EDGE,"E112"),sQuery(id+"F0.wireOp",EDGE,"E113"),sQuery(id+"F0.wireOp",EDGE,"E114"),sQuery(id+"F0.wireOp",EDGE,"E115")])],"isStart":false})],"blendedInto":[makeQuery(id+"F1.opExtrude","CAP_FACE",FACE,{"disambiguationData":[OSD([sQuery(id+"F0.wireOp",EDGE,"E0"),sQuery(id+"F0.wireOp",EDGE,"E1"),sQuery(id+"F0.wireOp",EDGE,"E2"),sQuery(id+"F0.wireOp",EDGE,"E3"),sQuery(id+"F0.wireOp",EDGE,"E4"),sQuery(id+"F0.wireOp",EDGE,"E5"),sQuery(id+"F0.wireOp",EDGE,"E6"),sQuery(id+"F0.wireOp",EDGE,"E7"),sQuery(id+"F0.wireOp",EDGE,"E8"),sQuery(id+"F0.wireOp",EDGE,"E9"),sQuery(id+"F0.wireOp",EDGE,"E10"),sQuery(id+"F0.wireOp",EDGE,"E11"),sQuery(id+"F0.wireOp",EDGE,"E12"),sQuery(id+"F0.wireOp",EDGE,"E13"),sQuery(id+"F0.wireOp",EDGE,"E14"),sQuery(id+"F0.wireOp",EDGE,"E15"),sQuery(id+"F0.wireOp",EDGE,"E16"),sQuery(id+"F0.wireOp",EDGE,"E17"),sQuery(id+"F0.wireOp",EDGE,"E18"),sQuery(id+"F0.wireOp",EDGE,"E19"),sQuery(id+"F0.wireOp",EDGE,"E20"),sQuery(id+"F0.wireOp",EDGE,"E21"),sQuery(id+"F0.wireOp",EDGE,"E22"),sQuery(id+"F0.wireOp",EDGE,"E23"),sQuery(id+"F0.wireOp",EDGE,"E24"),sQuery(id+"F0.wireOp",EDGE,"E25"),sQuery(id+"F0.wireOp",EDGE,"E26"),sQuery(id+"F0.wireOp",EDGE,"E27"),sQuery(id+"F0.wireOp",EDGE,"E28"),sQuery(id+"F0.wireOp",EDGE,"E29"),sQuery(id+"F0.wireOp",EDGE,"E30"),sQuery(id+"F0.wireOp",EDGE,"E31"),sQuery(id+"F0.wireOp",EDGE,"E32"),sQuery(id+"F0.wireOp",EDGE,"E33"),sQuery(id+"F0.wireOp",EDGE,"E34"),sQuery(id+"F0.wireOp",EDGE,"E35"),sQuery(id+"F0.wireOp",EDGE,"E36"),sQuery(id+"F0.wireOp",EDGE,"E37"),sQuery(id+"F0.wireOp",EDGE,"E38"),sQuery(id+"F0.wireOp",EDGE,"E39"),sQuery(id+"F0.wireOp",EDGE,"E40"),sQuery(id+"F0.wireOp",EDGE,"E41"),sQuery(id+"F0.wireOp",EDGE,"E42"),sQuery(id+"F0.wireOp",EDGE,"E43"),sQuery(id+"F0.wireOp",EDGE,"E44"),sQuery(id+"F0.wireOp",EDGE,"E45"),sQuery(id+"F0.wireOp",EDGE,"E46"),sQuery(id+"F0.wireOp",EDGE,"E47"),sQuery(id+"F0.wireOp",EDGE,"E48"),sQuery(id+"F0.wireOp",EDGE,"E49"),sQuery(id+"F0.wireOp",EDGE,"E50"),sQuery(id+"F0.wireOp",EDGE,"E51"),sQuery(id+"F0.wireOp",EDGE,"E52"),sQuery(id+"F0.wireOp",EDGE,"E53"),sQuery(id+"F0.wireOp",EDGE,"E54"),sQuery(id+"F0.wireOp",EDGE,"E55"),sQuery(id+"F0.wireOp",EDGE,"E56"),sQuery(id+"F0.wireOp",EDGE,"E57"),sQuery(id+"F0.wireOp",EDGE,"E58"),sQuery(id+"F0.wireOp",EDGE,"E59"),sQuery(id+"F0.wireOp",EDGE,"E60"),sQuery(id+"F0.wireOp",EDGE,"E61"),sQuery(id+"F0.wireOp",EDGE,"E62"),sQuery(id+"F0.wireOp",EDGE,"E63"),sQuery(id+"F0.wireOp",EDGE,"E64"),sQuery(id+"F0.wireOp",EDGE,"E65"),sQuery(id+"F0.wireOp",EDGE,"E66"),sQuery(id+"F0.wireOp",EDGE,"E67"),sQuery(id+"F0.wireOp",EDGE,"E68"),sQuery(id+"F0.wireOp",EDGE,"E69"),sQuery(id+"F0.wireOp",EDGE,"E70"),sQuery(id+"F0.wireOp",EDGE,"E71"),sQuery(id+"F0.wireOp",EDGE,"E72"),sQuery(id+"F0.wireOp",EDGE,"E73"),sQuery(id+"F0.wireOp",EDGE,"E74"),sQuery(id+"F0.wireOp",EDGE,"E75"),sQuery(id+"F0.wireOp",EDGE,"E76"),sQuery(id+"F0.wireOp",EDGE,"E77"),sQuery(id+"F0.wireOp",EDGE,"E78"),sQuery(id+"F0.wireOp",EDGE,"E79"),sQuery(id+"F0.wireOp",EDGE,"E80"),sQuery(id+"F0.wireOp",EDGE,"E81"),sQuery(id+"F0.wireOp",EDGE,"E82"),sQuery(id+"F0.wireOp",EDGE,"E83"),sQuery(id+"F0.wireOp",EDGE,"E84"),sQuery(id+"F0.wireOp",EDGE,"E85"),sQuery(id+"F0.wireOp",EDGE,"E86"),sQuery(id+"F0.wireOp",EDGE,"E87"),sQuery(id+"F0.wireOp",EDGE,"E88"),sQuery(id+"F0.wireOp",EDGE,"E89"),sQuery(id+"F0.wireOp",EDGE,"E90"),sQuery(id+"F0.wireOp",EDGE,"E91"),sQuery(id+"F0.wireOp",EDGE,"E92"),sQuery(id+"F0.wireOp",EDGE,"E93"),sQuery(id+"F0.wireOp",EDGE,"E94"),sQuery(id+"F0.wireOp",EDGE,"E95"),sQuery(id+"F0.wireOp",EDGE,"E96"),sQuery(id+"F0.wireOp",EDGE,"E97"),sQuery(id+"F0.wireOp",EDGE,"E98"),sQuery(id+"F0.wireOp",EDGE,"E99"),sQuery(id+"F0.wireOp",EDGE,"E100"),sQuery(id+"F0.wireOp",EDGE,"E101"),sQuery(id+"F0.wireOp",EDGE,"E102"),sQuery(id+"F0.wireOp",EDGE,"E103"),sQuery(id+"F0.wireOp",EDGE,"E104"),sQuery(id+"F0.wireOp",EDGE,"E105"),sQuery(id+"F0.wireOp",EDGE,"E106"),sQuery(id+"F0.wireOp",EDGE,"E107"),sQuery(id+"F0.wireOp",EDGE,"E108"),sQuery(id+"F0.wireOp",EDGE,"E109"),sQuery(id+"F0.wireOp",EDGE,"E110"),sQuery(id+"F0.wireOp",EDGE,"E111"),sQuery(id+"F0.wireOp",EDGE,"E112"),sQuery(id+"F0.wireOp",EDGE,"E113"),sQuery(id+"F0.wireOp",EDGE,"E114"),sQuery(id+"F0.wireOp",EDGE,"E115")])],"isStart":false})]});
            var Q31;
            Q31=makeQuery(id+"F6.opFillet","BLEND_EDGE",EDGE,{"blendedFrom":[makeQuery(id+"F5.boolean.opBoolean","COPY",EDGE,{"derivedFrom":makeQuery(id+"F5.opExtrude","CAP_EDGE",EDGE,{"disambiguationData":[OSD([sQuery(id+"F4.wireOp",EDGE,"E759.0.0.4")])],"isStart":false})}),makeQuery(id+"F1.opExtrude","CAP_FACE",FACE,{"disambiguationData":[OSD([sQuery(id+"F0.wireOp",EDGE,"E0"),sQuery(id+"F0.wireOp",EDGE,"E1"),sQuery(id+"F0.wireOp",EDGE,"E2"),sQuery(id+"F0.wireOp",EDGE,"E3"),sQuery(id+"F0.wireOp",EDGE,"E4"),sQuery(id+"F0.wireOp",EDGE,"E5"),sQuery(id+"F0.wireOp",EDGE,"E6"),sQuery(id+"F0.wireOp",EDGE,"E7"),sQuery(id+"F0.wireOp",EDGE,"E8"),sQuery(id+"F0.wireOp",EDGE,"E9"),sQuery(id+"F0.wireOp",EDGE,"E10"),sQuery(id+"F0.wireOp",EDGE,"E11"),sQuery(id+"F0.wireOp",EDGE,"E12"),sQuery(id+"F0.wireOp",EDGE,"E13"),sQuery(id+"F0.wireOp",EDGE,"E14"),sQuery(id+"F0.wireOp",EDGE,"E15"),sQuery(id+"F0.wireOp",EDGE,"E16"),sQuery(id+"F0.wireOp",EDGE,"E17"),sQuery(id+"F0.wireOp",EDGE,"E18"),sQuery(id+"F0.wireOp",EDGE,"E19"),sQuery(id+"F0.wireOp",EDGE,"E20"),sQuery(id+"F0.wireOp",EDGE,"E21"),sQuery(id+"F0.wireOp",EDGE,"E22"),sQuery(id+"F0.wireOp",EDGE,"E23"),sQuery(id+"F0.wireOp",EDGE,"E24"),sQuery(id+"F0.wireOp",EDGE,"E25"),sQuery(id+"F0.wireOp",EDGE,"E26"),sQuery(id+"F0.wireOp",EDGE,"E27"),sQuery(id+"F0.wireOp",EDGE,"E28"),sQuery(id+"F0.wireOp",EDGE,"E29"),sQuery(id+"F0.wireOp",EDGE,"E30"),sQuery(id+"F0.wireOp",EDGE,"E31"),sQuery(id+"F0.wireOp",EDGE,"E32"),sQuery(id+"F0.wireOp",EDGE,"E33"),sQuery(id+"F0.wireOp",EDGE,"E34"),sQuery(id+"F0.wireOp",EDGE,"E35"),sQuery(id+"F0.wireOp",EDGE,"E36"),sQuery(id+"F0.wireOp",EDGE,"E37"),sQuery(id+"F0.wireOp",EDGE,"E38"),sQuery(id+"F0.wireOp",EDGE,"E39"),sQuery(id+"F0.wireOp",EDGE,"E40"),sQuery(id+"F0.wireOp",EDGE,"E41"),sQuery(id+"F0.wireOp",EDGE,"E42"),sQuery(id+"F0.wireOp",EDGE,"E43"),sQuery(id+"F0.wireOp",EDGE,"E44"),sQuery(id+"F0.wireOp",EDGE,"E45"),sQuery(id+"F0.wireOp",EDGE,"E46"),sQuery(id+"F0.wireOp",EDGE,"E47"),sQuery(id+"F0.wireOp",EDGE,"E48"),sQuery(id+"F0.wireOp",EDGE,"E49"),sQuery(id+"F0.wireOp",EDGE,"E50"),sQuery(id+"F0.wireOp",EDGE,"E51"),sQuery(id+"F0.wireOp",EDGE,"E52"),sQuery(id+"F0.wireOp",EDGE,"E53"),sQuery(id+"F0.wireOp",EDGE,"E54"),sQuery(id+"F0.wireOp",EDGE,"E55"),sQuery(id+"F0.wireOp",EDGE,"E56"),sQuery(id+"F0.wireOp",EDGE,"E57"),sQuery(id+"F0.wireOp",EDGE,"E58"),sQuery(id+"F0.wireOp",EDGE,"E59"),sQuery(id+"F0.wireOp",EDGE,"E60"),sQuery(id+"F0.wireOp",EDGE,"E61"),sQuery(id+"F0.wireOp",EDGE,"E62"),sQuery(id+"F0.wireOp",EDGE,"E63"),sQuery(id+"F0.wireOp",EDGE,"E64"),sQuery(id+"F0.wireOp",EDGE,"E65"),sQuery(id+"F0.wireOp",EDGE,"E66"),sQuery(id+"F0.wireOp",EDGE,"E67"),sQuery(id+"F0.wireOp",EDGE,"E68"),sQuery(id+"F0.wireOp",EDGE,"E69"),sQuery(id+"F0.wireOp",EDGE,"E70"),sQuery(id+"F0.wireOp",EDGE,"E71"),sQuery(id+"F0.wireOp",EDGE,"E72"),sQuery(id+"F0.wireOp",EDGE,"E73"),sQuery(id+"F0.wireOp",EDGE,"E74"),sQuery(id+"F0.wireOp",EDGE,"E75"),sQuery(id+"F0.wireOp",EDGE,"E76"),sQuery(id+"F0.wireOp",EDGE,"E77"),sQuery(id+"F0.wireOp",EDGE,"E78"),sQuery(id+"F0.wireOp",EDGE,"E79"),sQuery(id+"F0.wireOp",EDGE,"E80"),sQuery(id+"F0.wireOp",EDGE,"E81"),sQuery(id+"F0.wireOp",EDGE,"E82"),sQuery(id+"F0.wireOp",EDGE,"E83"),sQuery(id+"F0.wireOp",EDGE,"E84"),sQuery(id+"F0.wireOp",EDGE,"E85"),sQuery(id+"F0.wireOp",EDGE,"E86"),sQuery(id+"F0.wireOp",EDGE,"E87"),sQuery(id+"F0.wireOp",EDGE,"E88"),sQuery(id+"F0.wireOp",EDGE,"E89"),sQuery(id+"F0.wireOp",EDGE,"E90"),sQuery(id+"F0.wireOp",EDGE,"E91"),sQuery(id+"F0.wireOp",EDGE,"E92"),sQuery(id+"F0.wireOp",EDGE,"E93"),sQuery(id+"F0.wireOp",EDGE,"E94"),sQuery(id+"F0.wireOp",EDGE,"E95"),sQuery(id+"F0.wireOp",EDGE,"E96"),sQuery(id+"F0.wireOp",EDGE,"E97"),sQuery(id+"F0.wireOp",EDGE,"E98"),sQuery(id+"F0.wireOp",EDGE,"E99"),sQuery(id+"F0.wireOp",EDGE,"E100"),sQuery(id+"F0.wireOp",EDGE,"E101"),sQuery(id+"F0.wireOp",EDGE,"E102"),sQuery(id+"F0.wireOp",EDGE,"E103"),sQuery(id+"F0.wireOp",EDGE,"E104"),sQuery(id+"F0.wireOp",EDGE,"E105"),sQuery(id+"F0.wireOp",EDGE,"E106"),sQuery(id+"F0.wireOp",EDGE,"E107"),sQuery(id+"F0.wireOp",EDGE,"E108"),sQuery(id+"F0.wireOp",EDGE,"E109"),sQuery(id+"F0.wireOp",EDGE,"E110"),sQuery(id+"F0.wireOp",EDGE,"E111"),sQuery(id+"F0.wireOp",EDGE,"E112"),sQuery(id+"F0.wireOp",EDGE,"E113"),sQuery(id+"F0.wireOp",EDGE,"E114"),sQuery(id+"F0.wireOp",EDGE,"E115")])],"isStart":false})],"blendedInto":[makeQuery(id+"F1.opExtrude","CAP_FACE",FACE,{"disambiguationData":[OSD([sQuery(id+"F0.wireOp",EDGE,"E0"),sQuery(id+"F0.wireOp",EDGE,"E1"),sQuery(id+"F0.wireOp",EDGE,"E2"),sQuery(id+"F0.wireOp",EDGE,"E3"),sQuery(id+"F0.wireOp",EDGE,"E4"),sQuery(id+"F0.wireOp",EDGE,"E5"),sQuery(id+"F0.wireOp",EDGE,"E6"),sQuery(id+"F0.wireOp",EDGE,"E7"),sQuery(id+"F0.wireOp",EDGE,"E8"),sQuery(id+"F0.wireOp",EDGE,"E9"),sQuery(id+"F0.wireOp",EDGE,"E10"),sQuery(id+"F0.wireOp",EDGE,"E11"),sQuery(id+"F0.wireOp",EDGE,"E12"),sQuery(id+"F0.wireOp",EDGE,"E13"),sQuery(id+"F0.wireOp",EDGE,"E14"),sQuery(id+"F0.wireOp",EDGE,"E15"),sQuery(id+"F0.wireOp",EDGE,"E16"),sQuery(id+"F0.wireOp",EDGE,"E17"),sQuery(id+"F0.wireOp",EDGE,"E18"),sQuery(id+"F0.wireOp",EDGE,"E19"),sQuery(id+"F0.wireOp",EDGE,"E20"),sQuery(id+"F0.wireOp",EDGE,"E21"),sQuery(id+"F0.wireOp",EDGE,"E22"),sQuery(id+"F0.wireOp",EDGE,"E23"),sQuery(id+"F0.wireOp",EDGE,"E24"),sQuery(id+"F0.wireOp",EDGE,"E25"),sQuery(id+"F0.wireOp",EDGE,"E26"),sQuery(id+"F0.wireOp",EDGE,"E27"),sQuery(id+"F0.wireOp",EDGE,"E28"),sQuery(id+"F0.wireOp",EDGE,"E29"),sQuery(id+"F0.wireOp",EDGE,"E30"),sQuery(id+"F0.wireOp",EDGE,"E31"),sQuery(id+"F0.wireOp",EDGE,"E32"),sQuery(id+"F0.wireOp",EDGE,"E33"),sQuery(id+"F0.wireOp",EDGE,"E34"),sQuery(id+"F0.wireOp",EDGE,"E35"),sQuery(id+"F0.wireOp",EDGE,"E36"),sQuery(id+"F0.wireOp",EDGE,"E37"),sQuery(id+"F0.wireOp",EDGE,"E38"),sQuery(id+"F0.wireOp",EDGE,"E39"),sQuery(id+"F0.wireOp",EDGE,"E40"),sQuery(id+"F0.wireOp",EDGE,"E41"),sQuery(id+"F0.wireOp",EDGE,"E42"),sQuery(id+"F0.wireOp",EDGE,"E43"),sQuery(id+"F0.wireOp",EDGE,"E44"),sQuery(id+"F0.wireOp",EDGE,"E45"),sQuery(id+"F0.wireOp",EDGE,"E46"),sQuery(id+"F0.wireOp",EDGE,"E47"),sQuery(id+"F0.wireOp",EDGE,"E48"),sQuery(id+"F0.wireOp",EDGE,"E49"),sQuery(id+"F0.wireOp",EDGE,"E50"),sQuery(id+"F0.wireOp",EDGE,"E51"),sQuery(id+"F0.wireOp",EDGE,"E52"),sQuery(id+"F0.wireOp",EDGE,"E53"),sQuery(id+"F0.wireOp",EDGE,"E54"),sQuery(id+"F0.wireOp",EDGE,"E55"),sQuery(id+"F0.wireOp",EDGE,"E56"),sQuery(id+"F0.wireOp",EDGE,"E57"),sQuery(id+"F0.wireOp",EDGE,"E58"),sQuery(id+"F0.wireOp",EDGE,"E59"),sQuery(id+"F0.wireOp",EDGE,"E60"),sQuery(id+"F0.wireOp",EDGE,"E61"),sQuery(id+"F0.wireOp",EDGE,"E62"),sQuery(id+"F0.wireOp",EDGE,"E63"),sQuery(id+"F0.wireOp",EDGE,"E64"),sQuery(id+"F0.wireOp",EDGE,"E65"),sQuery(id+"F0.wireOp",EDGE,"E66"),sQuery(id+"F0.wireOp",EDGE,"E67"),sQuery(id+"F0.wireOp",EDGE,"E68"),sQuery(id+"F0.wireOp",EDGE,"E69"),sQuery(id+"F0.wireOp",EDGE,"E70"),sQuery(id+"F0.wireOp",EDGE,"E71"),sQuery(id+"F0.wireOp",EDGE,"E72"),sQuery(id+"F0.wireOp",EDGE,"E73"),sQuery(id+"F0.wireOp",EDGE,"E74"),sQuery(id+"F0.wireOp",EDGE,"E75"),sQuery(id+"F0.wireOp",EDGE,"E76"),sQuery(id+"F0.wireOp",EDGE,"E77"),sQuery(id+"F0.wireOp",EDGE,"E78"),sQuery(id+"F0.wireOp",EDGE,"E79"),sQuery(id+"F0.wireOp",EDGE,"E80"),sQuery(id+"F0.wireOp",EDGE,"E81"),sQuery(id+"F0.wireOp",EDGE,"E82"),sQuery(id+"F0.wireOp",EDGE,"E83"),sQuery(id+"F0.wireOp",EDGE,"E84"),sQuery(id+"F0.wireOp",EDGE,"E85"),sQuery(id+"F0.wireOp",EDGE,"E86"),sQuery(id+"F0.wireOp",EDGE,"E87"),sQuery(id+"F0.wireOp",EDGE,"E88"),sQuery(id+"F0.wireOp",EDGE,"E89"),sQuery(id+"F0.wireOp",EDGE,"E90"),sQuery(id+"F0.wireOp",EDGE,"E91"),sQuery(id+"F0.wireOp",EDGE,"E92"),sQuery(id+"F0.wireOp",EDGE,"E93"),sQuery(id+"F0.wireOp",EDGE,"E94"),sQuery(id+"F0.wireOp",EDGE,"E95"),sQuery(id+"F0.wireOp",EDGE,"E96"),sQuery(id+"F0.wireOp",EDGE,"E97"),sQuery(id+"F0.wireOp",EDGE,"E98"),sQuery(id+"F0.wireOp",EDGE,"E99"),sQuery(id+"F0.wireOp",EDGE,"E100"),sQuery(id+"F0.wireOp",EDGE,"E101"),sQuery(id+"F0.wireOp",EDGE,"E102"),sQuery(id+"F0.wireOp",EDGE,"E103"),sQuery(id+"F0.wireOp",EDGE,"E104"),sQuery(id+"F0.wireOp",EDGE,"E105"),sQuery(id+"F0.wireOp",EDGE,"E106"),sQuery(id+"F0.wireOp",EDGE,"E107"),sQuery(id+"F0.wireOp",EDGE,"E108"),sQuery(id+"F0.wireOp",EDGE,"E109"),sQuery(id+"F0.wireOp",EDGE,"E110"),sQuery(id+"F0.wireOp",EDGE,"E111"),sQuery(id+"F0.wireOp",EDGE,"E112"),sQuery(id+"F0.wireOp",EDGE,"E113"),sQuery(id+"F0.wireOp",EDGE,"E114"),sQuery(id+"F0.wireOp",EDGE,"E115")])],"isStart":false})]});
            var Q32;
            Q32=makeQuery(id+"F6.opFillet","BLEND_EDGE",EDGE,{"blendedFrom":[makeQuery(id+"F5.boolean.opBoolean","COPY",EDGE,{"derivedFrom":makeQuery(id+"F5.opExtrude","CAP_EDGE",EDGE,{"disambiguationData":[OSD([sQuery(id+"F4.wireOp",EDGE,"E759.0.1.4")])],"isStart":false})}),makeQuery(id+"F1.opExtrude","CAP_FACE",FACE,{"disambiguationData":[OSD([sQuery(id+"F0.wireOp",EDGE,"E0"),sQuery(id+"F0.wireOp",EDGE,"E1"),sQuery(id+"F0.wireOp",EDGE,"E2"),sQuery(id+"F0.wireOp",EDGE,"E3"),sQuery(id+"F0.wireOp",EDGE,"E4"),sQuery(id+"F0.wireOp",EDGE,"E5"),sQuery(id+"F0.wireOp",EDGE,"E6"),sQuery(id+"F0.wireOp",EDGE,"E7"),sQuery(id+"F0.wireOp",EDGE,"E8"),sQuery(id+"F0.wireOp",EDGE,"E9"),sQuery(id+"F0.wireOp",EDGE,"E10"),sQuery(id+"F0.wireOp",EDGE,"E11"),sQuery(id+"F0.wireOp",EDGE,"E12"),sQuery(id+"F0.wireOp",EDGE,"E13"),sQuery(id+"F0.wireOp",EDGE,"E14"),sQuery(id+"F0.wireOp",EDGE,"E15"),sQuery(id+"F0.wireOp",EDGE,"E16"),sQuery(id+"F0.wireOp",EDGE,"E17"),sQuery(id+"F0.wireOp",EDGE,"E18"),sQuery(id+"F0.wireOp",EDGE,"E19"),sQuery(id+"F0.wireOp",EDGE,"E20"),sQuery(id+"F0.wireOp",EDGE,"E21"),sQuery(id+"F0.wireOp",EDGE,"E22"),sQuery(id+"F0.wireOp",EDGE,"E23"),sQuery(id+"F0.wireOp",EDGE,"E24"),sQuery(id+"F0.wireOp",EDGE,"E25"),sQuery(id+"F0.wireOp",EDGE,"E26"),sQuery(id+"F0.wireOp",EDGE,"E27"),sQuery(id+"F0.wireOp",EDGE,"E28"),sQuery(id+"F0.wireOp",EDGE,"E29"),sQuery(id+"F0.wireOp",EDGE,"E30"),sQuery(id+"F0.wireOp",EDGE,"E31"),sQuery(id+"F0.wireOp",EDGE,"E32"),sQuery(id+"F0.wireOp",EDGE,"E33"),sQuery(id+"F0.wireOp",EDGE,"E34"),sQuery(id+"F0.wireOp",EDGE,"E35"),sQuery(id+"F0.wireOp",EDGE,"E36"),sQuery(id+"F0.wireOp",EDGE,"E37"),sQuery(id+"F0.wireOp",EDGE,"E38"),sQuery(id+"F0.wireOp",EDGE,"E39"),sQuery(id+"F0.wireOp",EDGE,"E40"),sQuery(id+"F0.wireOp",EDGE,"E41"),sQuery(id+"F0.wireOp",EDGE,"E42"),sQuery(id+"F0.wireOp",EDGE,"E43"),sQuery(id+"F0.wireOp",EDGE,"E44"),sQuery(id+"F0.wireOp",EDGE,"E45"),sQuery(id+"F0.wireOp",EDGE,"E46"),sQuery(id+"F0.wireOp",EDGE,"E47"),sQuery(id+"F0.wireOp",EDGE,"E48"),sQuery(id+"F0.wireOp",EDGE,"E49"),sQuery(id+"F0.wireOp",EDGE,"E50"),sQuery(id+"F0.wireOp",EDGE,"E51"),sQuery(id+"F0.wireOp",EDGE,"E52"),sQuery(id+"F0.wireOp",EDGE,"E53"),sQuery(id+"F0.wireOp",EDGE,"E54"),sQuery(id+"F0.wireOp",EDGE,"E55"),sQuery(id+"F0.wireOp",EDGE,"E56"),sQuery(id+"F0.wireOp",EDGE,"E57"),sQuery(id+"F0.wireOp",EDGE,"E58"),sQuery(id+"F0.wireOp",EDGE,"E59"),sQuery(id+"F0.wireOp",EDGE,"E60"),sQuery(id+"F0.wireOp",EDGE,"E61"),sQuery(id+"F0.wireOp",EDGE,"E62"),sQuery(id+"F0.wireOp",EDGE,"E63"),sQuery(id+"F0.wireOp",EDGE,"E64"),sQuery(id+"F0.wireOp",EDGE,"E65"),sQuery(id+"F0.wireOp",EDGE,"E66"),sQuery(id+"F0.wireOp",EDGE,"E67"),sQuery(id+"F0.wireOp",EDGE,"E68"),sQuery(id+"F0.wireOp",EDGE,"E69"),sQuery(id+"F0.wireOp",EDGE,"E70"),sQuery(id+"F0.wireOp",EDGE,"E71"),sQuery(id+"F0.wireOp",EDGE,"E72"),sQuery(id+"F0.wireOp",EDGE,"E73"),sQuery(id+"F0.wireOp",EDGE,"E74"),sQuery(id+"F0.wireOp",EDGE,"E75"),sQuery(id+"F0.wireOp",EDGE,"E76"),sQuery(id+"F0.wireOp",EDGE,"E77"),sQuery(id+"F0.wireOp",EDGE,"E78"),sQuery(id+"F0.wireOp",EDGE,"E79"),sQuery(id+"F0.wireOp",EDGE,"E80"),sQuery(id+"F0.wireOp",EDGE,"E81"),sQuery(id+"F0.wireOp",EDGE,"E82"),sQuery(id+"F0.wireOp",EDGE,"E83"),sQuery(id+"F0.wireOp",EDGE,"E84"),sQuery(id+"F0.wireOp",EDGE,"E85"),sQuery(id+"F0.wireOp",EDGE,"E86"),sQuery(id+"F0.wireOp",EDGE,"E87"),sQuery(id+"F0.wireOp",EDGE,"E88"),sQuery(id+"F0.wireOp",EDGE,"E89"),sQuery(id+"F0.wireOp",EDGE,"E90"),sQuery(id+"F0.wireOp",EDGE,"E91"),sQuery(id+"F0.wireOp",EDGE,"E92"),sQuery(id+"F0.wireOp",EDGE,"E93"),sQuery(id+"F0.wireOp",EDGE,"E94"),sQuery(id+"F0.wireOp",EDGE,"E95"),sQuery(id+"F0.wireOp",EDGE,"E96"),sQuery(id+"F0.wireOp",EDGE,"E97"),sQuery(id+"F0.wireOp",EDGE,"E98"),sQuery(id+"F0.wireOp",EDGE,"E99"),sQuery(id+"F0.wireOp",EDGE,"E100"),sQuery(id+"F0.wireOp",EDGE,"E101"),sQuery(id+"F0.wireOp",EDGE,"E102"),sQuery(id+"F0.wireOp",EDGE,"E103"),sQuery(id+"F0.wireOp",EDGE,"E104"),sQuery(id+"F0.wireOp",EDGE,"E105"),sQuery(id+"F0.wireOp",EDGE,"E106"),sQuery(id+"F0.wireOp",EDGE,"E107"),sQuery(id+"F0.wireOp",EDGE,"E108"),sQuery(id+"F0.wireOp",EDGE,"E109"),sQuery(id+"F0.wireOp",EDGE,"E110"),sQuery(id+"F0.wireOp",EDGE,"E111"),sQuery(id+"F0.wireOp",EDGE,"E112"),sQuery(id+"F0.wireOp",EDGE,"E113"),sQuery(id+"F0.wireOp",EDGE,"E114"),sQuery(id+"F0.wireOp",EDGE,"E115")])],"isStart":false})],"blendedInto":[makeQuery(id+"F1.opExtrude","CAP_FACE",FACE,{"disambiguationData":[OSD([sQuery(id+"F0.wireOp",EDGE,"E0"),sQuery(id+"F0.wireOp",EDGE,"E1"),sQuery(id+"F0.wireOp",EDGE,"E2"),sQuery(id+"F0.wireOp",EDGE,"E3"),sQuery(id+"F0.wireOp",EDGE,"E4"),sQuery(id+"F0.wireOp",EDGE,"E5"),sQuery(id+"F0.wireOp",EDGE,"E6"),sQuery(id+"F0.wireOp",EDGE,"E7"),sQuery(id+"F0.wireOp",EDGE,"E8"),sQuery(id+"F0.wireOp",EDGE,"E9"),sQuery(id+"F0.wireOp",EDGE,"E10"),sQuery(id+"F0.wireOp",EDGE,"E11"),sQuery(id+"F0.wireOp",EDGE,"E12"),sQuery(id+"F0.wireOp",EDGE,"E13"),sQuery(id+"F0.wireOp",EDGE,"E14"),sQuery(id+"F0.wireOp",EDGE,"E15"),sQuery(id+"F0.wireOp",EDGE,"E16"),sQuery(id+"F0.wireOp",EDGE,"E17"),sQuery(id+"F0.wireOp",EDGE,"E18"),sQuery(id+"F0.wireOp",EDGE,"E19"),sQuery(id+"F0.wireOp",EDGE,"E20"),sQuery(id+"F0.wireOp",EDGE,"E21"),sQuery(id+"F0.wireOp",EDGE,"E22"),sQuery(id+"F0.wireOp",EDGE,"E23"),sQuery(id+"F0.wireOp",EDGE,"E24"),sQuery(id+"F0.wireOp",EDGE,"E25"),sQuery(id+"F0.wireOp",EDGE,"E26"),sQuery(id+"F0.wireOp",EDGE,"E27"),sQuery(id+"F0.wireOp",EDGE,"E28"),sQuery(id+"F0.wireOp",EDGE,"E29"),sQuery(id+"F0.wireOp",EDGE,"E30"),sQuery(id+"F0.wireOp",EDGE,"E31"),sQuery(id+"F0.wireOp",EDGE,"E32"),sQuery(id+"F0.wireOp",EDGE,"E33"),sQuery(id+"F0.wireOp",EDGE,"E34"),sQuery(id+"F0.wireOp",EDGE,"E35"),sQuery(id+"F0.wireOp",EDGE,"E36"),sQuery(id+"F0.wireOp",EDGE,"E37"),sQuery(id+"F0.wireOp",EDGE,"E38"),sQuery(id+"F0.wireOp",EDGE,"E39"),sQuery(id+"F0.wireOp",EDGE,"E40"),sQuery(id+"F0.wireOp",EDGE,"E41"),sQuery(id+"F0.wireOp",EDGE,"E42"),sQuery(id+"F0.wireOp",EDGE,"E43"),sQuery(id+"F0.wireOp",EDGE,"E44"),sQuery(id+"F0.wireOp",EDGE,"E45"),sQuery(id+"F0.wireOp",EDGE,"E46"),sQuery(id+"F0.wireOp",EDGE,"E47"),sQuery(id+"F0.wireOp",EDGE,"E48"),sQuery(id+"F0.wireOp",EDGE,"E49"),sQuery(id+"F0.wireOp",EDGE,"E50"),sQuery(id+"F0.wireOp",EDGE,"E51"),sQuery(id+"F0.wireOp",EDGE,"E52"),sQuery(id+"F0.wireOp",EDGE,"E53"),sQuery(id+"F0.wireOp",EDGE,"E54"),sQuery(id+"F0.wireOp",EDGE,"E55"),sQuery(id+"F0.wireOp",EDGE,"E56"),sQuery(id+"F0.wireOp",EDGE,"E57"),sQuery(id+"F0.wireOp",EDGE,"E58"),sQuery(id+"F0.wireOp",EDGE,"E59"),sQuery(id+"F0.wireOp",EDGE,"E60"),sQuery(id+"F0.wireOp",EDGE,"E61"),sQuery(id+"F0.wireOp",EDGE,"E62"),sQuery(id+"F0.wireOp",EDGE,"E63"),sQuery(id+"F0.wireOp",EDGE,"E64"),sQuery(id+"F0.wireOp",EDGE,"E65"),sQuery(id+"F0.wireOp",EDGE,"E66"),sQuery(id+"F0.wireOp",EDGE,"E67"),sQuery(id+"F0.wireOp",EDGE,"E68"),sQuery(id+"F0.wireOp",EDGE,"E69"),sQuery(id+"F0.wireOp",EDGE,"E70"),sQuery(id+"F0.wireOp",EDGE,"E71"),sQuery(id+"F0.wireOp",EDGE,"E72"),sQuery(id+"F0.wireOp",EDGE,"E73"),sQuery(id+"F0.wireOp",EDGE,"E74"),sQuery(id+"F0.wireOp",EDGE,"E75"),sQuery(id+"F0.wireOp",EDGE,"E76"),sQuery(id+"F0.wireOp",EDGE,"E77"),sQuery(id+"F0.wireOp",EDGE,"E78"),sQuery(id+"F0.wireOp",EDGE,"E79"),sQuery(id+"F0.wireOp",EDGE,"E80"),sQuery(id+"F0.wireOp",EDGE,"E81"),sQuery(id+"F0.wireOp",EDGE,"E82"),sQuery(id+"F0.wireOp",EDGE,"E83"),sQuery(id+"F0.wireOp",EDGE,"E84"),sQuery(id+"F0.wireOp",EDGE,"E85"),sQuery(id+"F0.wireOp",EDGE,"E86"),sQuery(id+"F0.wireOp",EDGE,"E87"),sQuery(id+"F0.wireOp",EDGE,"E88"),sQuery(id+"F0.wireOp",EDGE,"E89"),sQuery(id+"F0.wireOp",EDGE,"E90"),sQuery(id+"F0.wireOp",EDGE,"E91"),sQuery(id+"F0.wireOp",EDGE,"E92"),sQuery(id+"F0.wireOp",EDGE,"E93"),sQuery(id+"F0.wireOp",EDGE,"E94"),sQuery(id+"F0.wireOp",EDGE,"E95"),sQuery(id+"F0.wireOp",EDGE,"E96"),sQuery(id+"F0.wireOp",EDGE,"E97"),sQuery(id+"F0.wireOp",EDGE,"E98"),sQuery(id+"F0.wireOp",EDGE,"E99"),sQuery(id+"F0.wireOp",EDGE,"E100"),sQuery(id+"F0.wireOp",EDGE,"E101"),sQuery(id+"F0.wireOp",EDGE,"E102"),sQuery(id+"F0.wireOp",EDGE,"E103"),sQuery(id+"F0.wireOp",EDGE,"E104"),sQuery(id+"F0.wireOp",EDGE,"E105"),sQuery(id+"F0.wireOp",EDGE,"E106"),sQuery(id+"F0.wireOp",EDGE,"E107"),sQuery(id+"F0.wireOp",EDGE,"E108"),sQuery(id+"F0.wireOp",EDGE,"E109"),sQuery(id+"F0.wireOp",EDGE,"E110"),sQuery(id+"F0.wireOp",EDGE,"E111"),sQuery(id+"F0.wireOp",EDGE,"E112"),sQuery(id+"F0.wireOp",EDGE,"E113"),sQuery(id+"F0.wireOp",EDGE,"E114"),sQuery(id+"F0.wireOp",EDGE,"E115")])],"isStart":false})]});
            var Q33;
            Q33=makeQuery(id+"F6.opFillet","BLEND_EDGE",EDGE,{"blendedFrom":[makeQuery(id+"F5.boolean.opBoolean","COPY",EDGE,{"derivedFrom":makeQuery(id+"F5.opExtrude","CAP_EDGE",EDGE,{"disambiguationData":[OSD([sQuery(id+"F4.wireOp",EDGE,"E759.0.0.5")])],"isStart":false})}),makeQuery(id+"F1.opExtrude","CAP_FACE",FACE,{"disambiguationData":[OSD([sQuery(id+"F0.wireOp",EDGE,"E0"),sQuery(id+"F0.wireOp",EDGE,"E1"),sQuery(id+"F0.wireOp",EDGE,"E2"),sQuery(id+"F0.wireOp",EDGE,"E3"),sQuery(id+"F0.wireOp",EDGE,"E4"),sQuery(id+"F0.wireOp",EDGE,"E5"),sQuery(id+"F0.wireOp",EDGE,"E6"),sQuery(id+"F0.wireOp",EDGE,"E7"),sQuery(id+"F0.wireOp",EDGE,"E8"),sQuery(id+"F0.wireOp",EDGE,"E9"),sQuery(id+"F0.wireOp",EDGE,"E10"),sQuery(id+"F0.wireOp",EDGE,"E11"),sQuery(id+"F0.wireOp",EDGE,"E12"),sQuery(id+"F0.wireOp",EDGE,"E13"),sQuery(id+"F0.wireOp",EDGE,"E14"),sQuery(id+"F0.wireOp",EDGE,"E15"),sQuery(id+"F0.wireOp",EDGE,"E16"),sQuery(id+"F0.wireOp",EDGE,"E17"),sQuery(id+"F0.wireOp",EDGE,"E18"),sQuery(id+"F0.wireOp",EDGE,"E19"),sQuery(id+"F0.wireOp",EDGE,"E20"),sQuery(id+"F0.wireOp",EDGE,"E21"),sQuery(id+"F0.wireOp",EDGE,"E22"),sQuery(id+"F0.wireOp",EDGE,"E23"),sQuery(id+"F0.wireOp",EDGE,"E24"),sQuery(id+"F0.wireOp",EDGE,"E25"),sQuery(id+"F0.wireOp",EDGE,"E26"),sQuery(id+"F0.wireOp",EDGE,"E27"),sQuery(id+"F0.wireOp",EDGE,"E28"),sQuery(id+"F0.wireOp",EDGE,"E29"),sQuery(id+"F0.wireOp",EDGE,"E30"),sQuery(id+"F0.wireOp",EDGE,"E31"),sQuery(id+"F0.wireOp",EDGE,"E32"),sQuery(id+"F0.wireOp",EDGE,"E33"),sQuery(id+"F0.wireOp",EDGE,"E34"),sQuery(id+"F0.wireOp",EDGE,"E35"),sQuery(id+"F0.wireOp",EDGE,"E36"),sQuery(id+"F0.wireOp",EDGE,"E37"),sQuery(id+"F0.wireOp",EDGE,"E38"),sQuery(id+"F0.wireOp",EDGE,"E39"),sQuery(id+"F0.wireOp",EDGE,"E40"),sQuery(id+"F0.wireOp",EDGE,"E41"),sQuery(id+"F0.wireOp",EDGE,"E42"),sQuery(id+"F0.wireOp",EDGE,"E43"),sQuery(id+"F0.wireOp",EDGE,"E44"),sQuery(id+"F0.wireOp",EDGE,"E45"),sQuery(id+"F0.wireOp",EDGE,"E46"),sQuery(id+"F0.wireOp",EDGE,"E47"),sQuery(id+"F0.wireOp",EDGE,"E48"),sQuery(id+"F0.wireOp",EDGE,"E49"),sQuery(id+"F0.wireOp",EDGE,"E50"),sQuery(id+"F0.wireOp",EDGE,"E51"),sQuery(id+"F0.wireOp",EDGE,"E52"),sQuery(id+"F0.wireOp",EDGE,"E53"),sQuery(id+"F0.wireOp",EDGE,"E54"),sQuery(id+"F0.wireOp",EDGE,"E55"),sQuery(id+"F0.wireOp",EDGE,"E56"),sQuery(id+"F0.wireOp",EDGE,"E57"),sQuery(id+"F0.wireOp",EDGE,"E58"),sQuery(id+"F0.wireOp",EDGE,"E59"),sQuery(id+"F0.wireOp",EDGE,"E60"),sQuery(id+"F0.wireOp",EDGE,"E61"),sQuery(id+"F0.wireOp",EDGE,"E62"),sQuery(id+"F0.wireOp",EDGE,"E63"),sQuery(id+"F0.wireOp",EDGE,"E64"),sQuery(id+"F0.wireOp",EDGE,"E65"),sQuery(id+"F0.wireOp",EDGE,"E66"),sQuery(id+"F0.wireOp",EDGE,"E67"),sQuery(id+"F0.wireOp",EDGE,"E68"),sQuery(id+"F0.wireOp",EDGE,"E69"),sQuery(id+"F0.wireOp",EDGE,"E70"),sQuery(id+"F0.wireOp",EDGE,"E71"),sQuery(id+"F0.wireOp",EDGE,"E72"),sQuery(id+"F0.wireOp",EDGE,"E73"),sQuery(id+"F0.wireOp",EDGE,"E74"),sQuery(id+"F0.wireOp",EDGE,"E75"),sQuery(id+"F0.wireOp",EDGE,"E76"),sQuery(id+"F0.wireOp",EDGE,"E77"),sQuery(id+"F0.wireOp",EDGE,"E78"),sQuery(id+"F0.wireOp",EDGE,"E79"),sQuery(id+"F0.wireOp",EDGE,"E80"),sQuery(id+"F0.wireOp",EDGE,"E81"),sQuery(id+"F0.wireOp",EDGE,"E82"),sQuery(id+"F0.wireOp",EDGE,"E83"),sQuery(id+"F0.wireOp",EDGE,"E84"),sQuery(id+"F0.wireOp",EDGE,"E85"),sQuery(id+"F0.wireOp",EDGE,"E86"),sQuery(id+"F0.wireOp",EDGE,"E87"),sQuery(id+"F0.wireOp",EDGE,"E88"),sQuery(id+"F0.wireOp",EDGE,"E89"),sQuery(id+"F0.wireOp",EDGE,"E90"),sQuery(id+"F0.wireOp",EDGE,"E91"),sQuery(id+"F0.wireOp",EDGE,"E92"),sQuery(id+"F0.wireOp",EDGE,"E93"),sQuery(id+"F0.wireOp",EDGE,"E94"),sQuery(id+"F0.wireOp",EDGE,"E95"),sQuery(id+"F0.wireOp",EDGE,"E96"),sQuery(id+"F0.wireOp",EDGE,"E97"),sQuery(id+"F0.wireOp",EDGE,"E98"),sQuery(id+"F0.wireOp",EDGE,"E99"),sQuery(id+"F0.wireOp",EDGE,"E100"),sQuery(id+"F0.wireOp",EDGE,"E101"),sQuery(id+"F0.wireOp",EDGE,"E102"),sQuery(id+"F0.wireOp",EDGE,"E103"),sQuery(id+"F0.wireOp",EDGE,"E104"),sQuery(id+"F0.wireOp",EDGE,"E105"),sQuery(id+"F0.wireOp",EDGE,"E106"),sQuery(id+"F0.wireOp",EDGE,"E107"),sQuery(id+"F0.wireOp",EDGE,"E108"),sQuery(id+"F0.wireOp",EDGE,"E109"),sQuery(id+"F0.wireOp",EDGE,"E110"),sQuery(id+"F0.wireOp",EDGE,"E111"),sQuery(id+"F0.wireOp",EDGE,"E112"),sQuery(id+"F0.wireOp",EDGE,"E113"),sQuery(id+"F0.wireOp",EDGE,"E114"),sQuery(id+"F0.wireOp",EDGE,"E115")])],"isStart":false})],"blendedInto":[makeQuery(id+"F1.opExtrude","CAP_FACE",FACE,{"disambiguationData":[OSD([sQuery(id+"F0.wireOp",EDGE,"E0"),sQuery(id+"F0.wireOp",EDGE,"E1"),sQuery(id+"F0.wireOp",EDGE,"E2"),sQuery(id+"F0.wireOp",EDGE,"E3"),sQuery(id+"F0.wireOp",EDGE,"E4"),sQuery(id+"F0.wireOp",EDGE,"E5"),sQuery(id+"F0.wireOp",EDGE,"E6"),sQuery(id+"F0.wireOp",EDGE,"E7"),sQuery(id+"F0.wireOp",EDGE,"E8"),sQuery(id+"F0.wireOp",EDGE,"E9"),sQuery(id+"F0.wireOp",EDGE,"E10"),sQuery(id+"F0.wireOp",EDGE,"E11"),sQuery(id+"F0.wireOp",EDGE,"E12"),sQuery(id+"F0.wireOp",EDGE,"E13"),sQuery(id+"F0.wireOp",EDGE,"E14"),sQuery(id+"F0.wireOp",EDGE,"E15"),sQuery(id+"F0.wireOp",EDGE,"E16"),sQuery(id+"F0.wireOp",EDGE,"E17"),sQuery(id+"F0.wireOp",EDGE,"E18"),sQuery(id+"F0.wireOp",EDGE,"E19"),sQuery(id+"F0.wireOp",EDGE,"E20"),sQuery(id+"F0.wireOp",EDGE,"E21"),sQuery(id+"F0.wireOp",EDGE,"E22"),sQuery(id+"F0.wireOp",EDGE,"E23"),sQuery(id+"F0.wireOp",EDGE,"E24"),sQuery(id+"F0.wireOp",EDGE,"E25"),sQuery(id+"F0.wireOp",EDGE,"E26"),sQuery(id+"F0.wireOp",EDGE,"E27"),sQuery(id+"F0.wireOp",EDGE,"E28"),sQuery(id+"F0.wireOp",EDGE,"E29"),sQuery(id+"F0.wireOp",EDGE,"E30"),sQuery(id+"F0.wireOp",EDGE,"E31"),sQuery(id+"F0.wireOp",EDGE,"E32"),sQuery(id+"F0.wireOp",EDGE,"E33"),sQuery(id+"F0.wireOp",EDGE,"E34"),sQuery(id+"F0.wireOp",EDGE,"E35"),sQuery(id+"F0.wireOp",EDGE,"E36"),sQuery(id+"F0.wireOp",EDGE,"E37"),sQuery(id+"F0.wireOp",EDGE,"E38"),sQuery(id+"F0.wireOp",EDGE,"E39"),sQuery(id+"F0.wireOp",EDGE,"E40"),sQuery(id+"F0.wireOp",EDGE,"E41"),sQuery(id+"F0.wireOp",EDGE,"E42"),sQuery(id+"F0.wireOp",EDGE,"E43"),sQuery(id+"F0.wireOp",EDGE,"E44"),sQuery(id+"F0.wireOp",EDGE,"E45"),sQuery(id+"F0.wireOp",EDGE,"E46"),sQuery(id+"F0.wireOp",EDGE,"E47"),sQuery(id+"F0.wireOp",EDGE,"E48"),sQuery(id+"F0.wireOp",EDGE,"E49"),sQuery(id+"F0.wireOp",EDGE,"E50"),sQuery(id+"F0.wireOp",EDGE,"E51"),sQuery(id+"F0.wireOp",EDGE,"E52"),sQuery(id+"F0.wireOp",EDGE,"E53"),sQuery(id+"F0.wireOp",EDGE,"E54"),sQuery(id+"F0.wireOp",EDGE,"E55"),sQuery(id+"F0.wireOp",EDGE,"E56"),sQuery(id+"F0.wireOp",EDGE,"E57"),sQuery(id+"F0.wireOp",EDGE,"E58"),sQuery(id+"F0.wireOp",EDGE,"E59"),sQuery(id+"F0.wireOp",EDGE,"E60"),sQuery(id+"F0.wireOp",EDGE,"E61"),sQuery(id+"F0.wireOp",EDGE,"E62"),sQuery(id+"F0.wireOp",EDGE,"E63"),sQuery(id+"F0.wireOp",EDGE,"E64"),sQuery(id+"F0.wireOp",EDGE,"E65"),sQuery(id+"F0.wireOp",EDGE,"E66"),sQuery(id+"F0.wireOp",EDGE,"E67"),sQuery(id+"F0.wireOp",EDGE,"E68"),sQuery(id+"F0.wireOp",EDGE,"E69"),sQuery(id+"F0.wireOp",EDGE,"E70"),sQuery(id+"F0.wireOp",EDGE,"E71"),sQuery(id+"F0.wireOp",EDGE,"E72"),sQuery(id+"F0.wireOp",EDGE,"E73"),sQuery(id+"F0.wireOp",EDGE,"E74"),sQuery(id+"F0.wireOp",EDGE,"E75"),sQuery(id+"F0.wireOp",EDGE,"E76"),sQuery(id+"F0.wireOp",EDGE,"E77"),sQuery(id+"F0.wireOp",EDGE,"E78"),sQuery(id+"F0.wireOp",EDGE,"E79"),sQuery(id+"F0.wireOp",EDGE,"E80"),sQuery(id+"F0.wireOp",EDGE,"E81"),sQuery(id+"F0.wireOp",EDGE,"E82"),sQuery(id+"F0.wireOp",EDGE,"E83"),sQuery(id+"F0.wireOp",EDGE,"E84"),sQuery(id+"F0.wireOp",EDGE,"E85"),sQuery(id+"F0.wireOp",EDGE,"E86"),sQuery(id+"F0.wireOp",EDGE,"E87"),sQuery(id+"F0.wireOp",EDGE,"E88"),sQuery(id+"F0.wireOp",EDGE,"E89"),sQuery(id+"F0.wireOp",EDGE,"E90"),sQuery(id+"F0.wireOp",EDGE,"E91"),sQuery(id+"F0.wireOp",EDGE,"E92"),sQuery(id+"F0.wireOp",EDGE,"E93"),sQuery(id+"F0.wireOp",EDGE,"E94"),sQuery(id+"F0.wireOp",EDGE,"E95"),sQuery(id+"F0.wireOp",EDGE,"E96"),sQuery(id+"F0.wireOp",EDGE,"E97"),sQuery(id+"F0.wireOp",EDGE,"E98"),sQuery(id+"F0.wireOp",EDGE,"E99"),sQuery(id+"F0.wireOp",EDGE,"E100"),sQuery(id+"F0.wireOp",EDGE,"E101"),sQuery(id+"F0.wireOp",EDGE,"E102"),sQuery(id+"F0.wireOp",EDGE,"E103"),sQuery(id+"F0.wireOp",EDGE,"E104"),sQuery(id+"F0.wireOp",EDGE,"E105"),sQuery(id+"F0.wireOp",EDGE,"E106"),sQuery(id+"F0.wireOp",EDGE,"E107"),sQuery(id+"F0.wireOp",EDGE,"E108"),sQuery(id+"F0.wireOp",EDGE,"E109"),sQuery(id+"F0.wireOp",EDGE,"E110"),sQuery(id+"F0.wireOp",EDGE,"E111"),sQuery(id+"F0.wireOp",EDGE,"E112"),sQuery(id+"F0.wireOp",EDGE,"E113"),sQuery(id+"F0.wireOp",EDGE,"E114"),sQuery(id+"F0.wireOp",EDGE,"E115")])],"isStart":false})]});
            var Q34;
            Q34=makeQuery(id+"F6.opFillet","BLEND_EDGE",EDGE,{"blendedFrom":[makeQuery(id+"F5.boolean.opBoolean","COPY",EDGE,{"derivedFrom":makeQuery(id+"F5.opExtrude","CAP_EDGE",EDGE,{"disambiguationData":[OSD([sQuery(id+"F4.wireOp",EDGE,"E759.0.1.5")])],"isStart":false})}),makeQuery(id+"F1.opExtrude","CAP_FACE",FACE,{"disambiguationData":[OSD([sQuery(id+"F0.wireOp",EDGE,"E0"),sQuery(id+"F0.wireOp",EDGE,"E1"),sQuery(id+"F0.wireOp",EDGE,"E2"),sQuery(id+"F0.wireOp",EDGE,"E3"),sQuery(id+"F0.wireOp",EDGE,"E4"),sQuery(id+"F0.wireOp",EDGE,"E5"),sQuery(id+"F0.wireOp",EDGE,"E6"),sQuery(id+"F0.wireOp",EDGE,"E7"),sQuery(id+"F0.wireOp",EDGE,"E8"),sQuery(id+"F0.wireOp",EDGE,"E9"),sQuery(id+"F0.wireOp",EDGE,"E10"),sQuery(id+"F0.wireOp",EDGE,"E11"),sQuery(id+"F0.wireOp",EDGE,"E12"),sQuery(id+"F0.wireOp",EDGE,"E13"),sQuery(id+"F0.wireOp",EDGE,"E14"),sQuery(id+"F0.wireOp",EDGE,"E15"),sQuery(id+"F0.wireOp",EDGE,"E16"),sQuery(id+"F0.wireOp",EDGE,"E17"),sQuery(id+"F0.wireOp",EDGE,"E18"),sQuery(id+"F0.wireOp",EDGE,"E19"),sQuery(id+"F0.wireOp",EDGE,"E20"),sQuery(id+"F0.wireOp",EDGE,"E21"),sQuery(id+"F0.wireOp",EDGE,"E22"),sQuery(id+"F0.wireOp",EDGE,"E23"),sQuery(id+"F0.wireOp",EDGE,"E24"),sQuery(id+"F0.wireOp",EDGE,"E25"),sQuery(id+"F0.wireOp",EDGE,"E26"),sQuery(id+"F0.wireOp",EDGE,"E27"),sQuery(id+"F0.wireOp",EDGE,"E28"),sQuery(id+"F0.wireOp",EDGE,"E29"),sQuery(id+"F0.wireOp",EDGE,"E30"),sQuery(id+"F0.wireOp",EDGE,"E31"),sQuery(id+"F0.wireOp",EDGE,"E32"),sQuery(id+"F0.wireOp",EDGE,"E33"),sQuery(id+"F0.wireOp",EDGE,"E34"),sQuery(id+"F0.wireOp",EDGE,"E35"),sQuery(id+"F0.wireOp",EDGE,"E36"),sQuery(id+"F0.wireOp",EDGE,"E37"),sQuery(id+"F0.wireOp",EDGE,"E38"),sQuery(id+"F0.wireOp",EDGE,"E39"),sQuery(id+"F0.wireOp",EDGE,"E40"),sQuery(id+"F0.wireOp",EDGE,"E41"),sQuery(id+"F0.wireOp",EDGE,"E42"),sQuery(id+"F0.wireOp",EDGE,"E43"),sQuery(id+"F0.wireOp",EDGE,"E44"),sQuery(id+"F0.wireOp",EDGE,"E45"),sQuery(id+"F0.wireOp",EDGE,"E46"),sQuery(id+"F0.wireOp",EDGE,"E47"),sQuery(id+"F0.wireOp",EDGE,"E48"),sQuery(id+"F0.wireOp",EDGE,"E49"),sQuery(id+"F0.wireOp",EDGE,"E50"),sQuery(id+"F0.wireOp",EDGE,"E51"),sQuery(id+"F0.wireOp",EDGE,"E52"),sQuery(id+"F0.wireOp",EDGE,"E53"),sQuery(id+"F0.wireOp",EDGE,"E54"),sQuery(id+"F0.wireOp",EDGE,"E55"),sQuery(id+"F0.wireOp",EDGE,"E56"),sQuery(id+"F0.wireOp",EDGE,"E57"),sQuery(id+"F0.wireOp",EDGE,"E58"),sQuery(id+"F0.wireOp",EDGE,"E59"),sQuery(id+"F0.wireOp",EDGE,"E60"),sQuery(id+"F0.wireOp",EDGE,"E61"),sQuery(id+"F0.wireOp",EDGE,"E62"),sQuery(id+"F0.wireOp",EDGE,"E63"),sQuery(id+"F0.wireOp",EDGE,"E64"),sQuery(id+"F0.wireOp",EDGE,"E65"),sQuery(id+"F0.wireOp",EDGE,"E66"),sQuery(id+"F0.wireOp",EDGE,"E67"),sQuery(id+"F0.wireOp",EDGE,"E68"),sQuery(id+"F0.wireOp",EDGE,"E69"),sQuery(id+"F0.wireOp",EDGE,"E70"),sQuery(id+"F0.wireOp",EDGE,"E71"),sQuery(id+"F0.wireOp",EDGE,"E72"),sQuery(id+"F0.wireOp",EDGE,"E73"),sQuery(id+"F0.wireOp",EDGE,"E74"),sQuery(id+"F0.wireOp",EDGE,"E75"),sQuery(id+"F0.wireOp",EDGE,"E76"),sQuery(id+"F0.wireOp",EDGE,"E77"),sQuery(id+"F0.wireOp",EDGE,"E78"),sQuery(id+"F0.wireOp",EDGE,"E79"),sQuery(id+"F0.wireOp",EDGE,"E80"),sQuery(id+"F0.wireOp",EDGE,"E81"),sQuery(id+"F0.wireOp",EDGE,"E82"),sQuery(id+"F0.wireOp",EDGE,"E83"),sQuery(id+"F0.wireOp",EDGE,"E84"),sQuery(id+"F0.wireOp",EDGE,"E85"),sQuery(id+"F0.wireOp",EDGE,"E86"),sQuery(id+"F0.wireOp",EDGE,"E87"),sQuery(id+"F0.wireOp",EDGE,"E88"),sQuery(id+"F0.wireOp",EDGE,"E89"),sQuery(id+"F0.wireOp",EDGE,"E90"),sQuery(id+"F0.wireOp",EDGE,"E91"),sQuery(id+"F0.wireOp",EDGE,"E92"),sQuery(id+"F0.wireOp",EDGE,"E93"),sQuery(id+"F0.wireOp",EDGE,"E94"),sQuery(id+"F0.wireOp",EDGE,"E95"),sQuery(id+"F0.wireOp",EDGE,"E96"),sQuery(id+"F0.wireOp",EDGE,"E97"),sQuery(id+"F0.wireOp",EDGE,"E98"),sQuery(id+"F0.wireOp",EDGE,"E99"),sQuery(id+"F0.wireOp",EDGE,"E100"),sQuery(id+"F0.wireOp",EDGE,"E101"),sQuery(id+"F0.wireOp",EDGE,"E102"),sQuery(id+"F0.wireOp",EDGE,"E103"),sQuery(id+"F0.wireOp",EDGE,"E104"),sQuery(id+"F0.wireOp",EDGE,"E105"),sQuery(id+"F0.wireOp",EDGE,"E106"),sQuery(id+"F0.wireOp",EDGE,"E107"),sQuery(id+"F0.wireOp",EDGE,"E108"),sQuery(id+"F0.wireOp",EDGE,"E109"),sQuery(id+"F0.wireOp",EDGE,"E110"),sQuery(id+"F0.wireOp",EDGE,"E111"),sQuery(id+"F0.wireOp",EDGE,"E112"),sQuery(id+"F0.wireOp",EDGE,"E113"),sQuery(id+"F0.wireOp",EDGE,"E114"),sQuery(id+"F0.wireOp",EDGE,"E115")])],"isStart":false})],"blendedInto":[makeQuery(id+"F1.opExtrude","CAP_FACE",FACE,{"disambiguationData":[OSD([sQuery(id+"F0.wireOp",EDGE,"E0"),sQuery(id+"F0.wireOp",EDGE,"E1"),sQuery(id+"F0.wireOp",EDGE,"E2"),sQuery(id+"F0.wireOp",EDGE,"E3"),sQuery(id+"F0.wireOp",EDGE,"E4"),sQuery(id+"F0.wireOp",EDGE,"E5"),sQuery(id+"F0.wireOp",EDGE,"E6"),sQuery(id+"F0.wireOp",EDGE,"E7"),sQuery(id+"F0.wireOp",EDGE,"E8"),sQuery(id+"F0.wireOp",EDGE,"E9"),sQuery(id+"F0.wireOp",EDGE,"E10"),sQuery(id+"F0.wireOp",EDGE,"E11"),sQuery(id+"F0.wireOp",EDGE,"E12"),sQuery(id+"F0.wireOp",EDGE,"E13"),sQuery(id+"F0.wireOp",EDGE,"E14"),sQuery(id+"F0.wireOp",EDGE,"E15"),sQuery(id+"F0.wireOp",EDGE,"E16"),sQuery(id+"F0.wireOp",EDGE,"E17"),sQuery(id+"F0.wireOp",EDGE,"E18"),sQuery(id+"F0.wireOp",EDGE,"E19"),sQuery(id+"F0.wireOp",EDGE,"E20"),sQuery(id+"F0.wireOp",EDGE,"E21"),sQuery(id+"F0.wireOp",EDGE,"E22"),sQuery(id+"F0.wireOp",EDGE,"E23"),sQuery(id+"F0.wireOp",EDGE,"E24"),sQuery(id+"F0.wireOp",EDGE,"E25"),sQuery(id+"F0.wireOp",EDGE,"E26"),sQuery(id+"F0.wireOp",EDGE,"E27"),sQuery(id+"F0.wireOp",EDGE,"E28"),sQuery(id+"F0.wireOp",EDGE,"E29"),sQuery(id+"F0.wireOp",EDGE,"E30"),sQuery(id+"F0.wireOp",EDGE,"E31"),sQuery(id+"F0.wireOp",EDGE,"E32"),sQuery(id+"F0.wireOp",EDGE,"E33"),sQuery(id+"F0.wireOp",EDGE,"E34"),sQuery(id+"F0.wireOp",EDGE,"E35"),sQuery(id+"F0.wireOp",EDGE,"E36"),sQuery(id+"F0.wireOp",EDGE,"E37"),sQuery(id+"F0.wireOp",EDGE,"E38"),sQuery(id+"F0.wireOp",EDGE,"E39"),sQuery(id+"F0.wireOp",EDGE,"E40"),sQuery(id+"F0.wireOp",EDGE,"E41"),sQuery(id+"F0.wireOp",EDGE,"E42"),sQuery(id+"F0.wireOp",EDGE,"E43"),sQuery(id+"F0.wireOp",EDGE,"E44"),sQuery(id+"F0.wireOp",EDGE,"E45"),sQuery(id+"F0.wireOp",EDGE,"E46"),sQuery(id+"F0.wireOp",EDGE,"E47"),sQuery(id+"F0.wireOp",EDGE,"E48"),sQuery(id+"F0.wireOp",EDGE,"E49"),sQuery(id+"F0.wireOp",EDGE,"E50"),sQuery(id+"F0.wireOp",EDGE,"E51"),sQuery(id+"F0.wireOp",EDGE,"E52"),sQuery(id+"F0.wireOp",EDGE,"E53"),sQuery(id+"F0.wireOp",EDGE,"E54"),sQuery(id+"F0.wireOp",EDGE,"E55"),sQuery(id+"F0.wireOp",EDGE,"E56"),sQuery(id+"F0.wireOp",EDGE,"E57"),sQuery(id+"F0.wireOp",EDGE,"E58"),sQuery(id+"F0.wireOp",EDGE,"E59"),sQuery(id+"F0.wireOp",EDGE,"E60"),sQuery(id+"F0.wireOp",EDGE,"E61"),sQuery(id+"F0.wireOp",EDGE,"E62"),sQuery(id+"F0.wireOp",EDGE,"E63"),sQuery(id+"F0.wireOp",EDGE,"E64"),sQuery(id+"F0.wireOp",EDGE,"E65"),sQuery(id+"F0.wireOp",EDGE,"E66"),sQuery(id+"F0.wireOp",EDGE,"E67"),sQuery(id+"F0.wireOp",EDGE,"E68"),sQuery(id+"F0.wireOp",EDGE,"E69"),sQuery(id+"F0.wireOp",EDGE,"E70"),sQuery(id+"F0.wireOp",EDGE,"E71"),sQuery(id+"F0.wireOp",EDGE,"E72"),sQuery(id+"F0.wireOp",EDGE,"E73"),sQuery(id+"F0.wireOp",EDGE,"E74"),sQuery(id+"F0.wireOp",EDGE,"E75"),sQuery(id+"F0.wireOp",EDGE,"E76"),sQuery(id+"F0.wireOp",EDGE,"E77"),sQuery(id+"F0.wireOp",EDGE,"E78"),sQuery(id+"F0.wireOp",EDGE,"E79"),sQuery(id+"F0.wireOp",EDGE,"E80"),sQuery(id+"F0.wireOp",EDGE,"E81"),sQuery(id+"F0.wireOp",EDGE,"E82"),sQuery(id+"F0.wireOp",EDGE,"E83"),sQuery(id+"F0.wireOp",EDGE,"E84"),sQuery(id+"F0.wireOp",EDGE,"E85"),sQuery(id+"F0.wireOp",EDGE,"E86"),sQuery(id+"F0.wireOp",EDGE,"E87"),sQuery(id+"F0.wireOp",EDGE,"E88"),sQuery(id+"F0.wireOp",EDGE,"E89"),sQuery(id+"F0.wireOp",EDGE,"E90"),sQuery(id+"F0.wireOp",EDGE,"E91"),sQuery(id+"F0.wireOp",EDGE,"E92"),sQuery(id+"F0.wireOp",EDGE,"E93"),sQuery(id+"F0.wireOp",EDGE,"E94"),sQuery(id+"F0.wireOp",EDGE,"E95"),sQuery(id+"F0.wireOp",EDGE,"E96"),sQuery(id+"F0.wireOp",EDGE,"E97"),sQuery(id+"F0.wireOp",EDGE,"E98"),sQuery(id+"F0.wireOp",EDGE,"E99"),sQuery(id+"F0.wireOp",EDGE,"E100"),sQuery(id+"F0.wireOp",EDGE,"E101"),sQuery(id+"F0.wireOp",EDGE,"E102"),sQuery(id+"F0.wireOp",EDGE,"E103"),sQuery(id+"F0.wireOp",EDGE,"E104"),sQuery(id+"F0.wireOp",EDGE,"E105"),sQuery(id+"F0.wireOp",EDGE,"E106"),sQuery(id+"F0.wireOp",EDGE,"E107"),sQuery(id+"F0.wireOp",EDGE,"E108"),sQuery(id+"F0.wireOp",EDGE,"E109"),sQuery(id+"F0.wireOp",EDGE,"E110"),sQuery(id+"F0.wireOp",EDGE,"E111"),sQuery(id+"F0.wireOp",EDGE,"E112"),sQuery(id+"F0.wireOp",EDGE,"E113"),sQuery(id+"F0.wireOp",EDGE,"E114"),sQuery(id+"F0.wireOp",EDGE,"E115")])],"isStart":false})]});
            var Q35;
            Q35=makeQuery(id+"F6.opFillet","BLEND_EDGE",EDGE,{"blendedFrom":[makeQuery(id+"F5.boolean.opBoolean","COPY",EDGE,{"derivedFrom":makeQuery(id+"F5.opExtrude","CAP_EDGE",EDGE,{"disambiguationData":[OSD([sQuery(id+"F4.wireOp",EDGE,"E759.0.2.5")])],"isStart":false})}),makeQuery(id+"F1.opExtrude","CAP_FACE",FACE,{"disambiguationData":[OSD([sQuery(id+"F0.wireOp",EDGE,"E0"),sQuery(id+"F0.wireOp",EDGE,"E1"),sQuery(id+"F0.wireOp",EDGE,"E2"),sQuery(id+"F0.wireOp",EDGE,"E3"),sQuery(id+"F0.wireOp",EDGE,"E4"),sQuery(id+"F0.wireOp",EDGE,"E5"),sQuery(id+"F0.wireOp",EDGE,"E6"),sQuery(id+"F0.wireOp",EDGE,"E7"),sQuery(id+"F0.wireOp",EDGE,"E8"),sQuery(id+"F0.wireOp",EDGE,"E9"),sQuery(id+"F0.wireOp",EDGE,"E10"),sQuery(id+"F0.wireOp",EDGE,"E11"),sQuery(id+"F0.wireOp",EDGE,"E12"),sQuery(id+"F0.wireOp",EDGE,"E13"),sQuery(id+"F0.wireOp",EDGE,"E14"),sQuery(id+"F0.wireOp",EDGE,"E15"),sQuery(id+"F0.wireOp",EDGE,"E16"),sQuery(id+"F0.wireOp",EDGE,"E17"),sQuery(id+"F0.wireOp",EDGE,"E18"),sQuery(id+"F0.wireOp",EDGE,"E19"),sQuery(id+"F0.wireOp",EDGE,"E20"),sQuery(id+"F0.wireOp",EDGE,"E21"),sQuery(id+"F0.wireOp",EDGE,"E22"),sQuery(id+"F0.wireOp",EDGE,"E23"),sQuery(id+"F0.wireOp",EDGE,"E24"),sQuery(id+"F0.wireOp",EDGE,"E25"),sQuery(id+"F0.wireOp",EDGE,"E26"),sQuery(id+"F0.wireOp",EDGE,"E27"),sQuery(id+"F0.wireOp",EDGE,"E28"),sQuery(id+"F0.wireOp",EDGE,"E29"),sQuery(id+"F0.wireOp",EDGE,"E30"),sQuery(id+"F0.wireOp",EDGE,"E31"),sQuery(id+"F0.wireOp",EDGE,"E32"),sQuery(id+"F0.wireOp",EDGE,"E33"),sQuery(id+"F0.wireOp",EDGE,"E34"),sQuery(id+"F0.wireOp",EDGE,"E35"),sQuery(id+"F0.wireOp",EDGE,"E36"),sQuery(id+"F0.wireOp",EDGE,"E37"),sQuery(id+"F0.wireOp",EDGE,"E38"),sQuery(id+"F0.wireOp",EDGE,"E39"),sQuery(id+"F0.wireOp",EDGE,"E40"),sQuery(id+"F0.wireOp",EDGE,"E41"),sQuery(id+"F0.wireOp",EDGE,"E42"),sQuery(id+"F0.wireOp",EDGE,"E43"),sQuery(id+"F0.wireOp",EDGE,"E44"),sQuery(id+"F0.wireOp",EDGE,"E45"),sQuery(id+"F0.wireOp",EDGE,"E46"),sQuery(id+"F0.wireOp",EDGE,"E47"),sQuery(id+"F0.wireOp",EDGE,"E48"),sQuery(id+"F0.wireOp",EDGE,"E49"),sQuery(id+"F0.wireOp",EDGE,"E50"),sQuery(id+"F0.wireOp",EDGE,"E51"),sQuery(id+"F0.wireOp",EDGE,"E52"),sQuery(id+"F0.wireOp",EDGE,"E53"),sQuery(id+"F0.wireOp",EDGE,"E54"),sQuery(id+"F0.wireOp",EDGE,"E55"),sQuery(id+"F0.wireOp",EDGE,"E56"),sQuery(id+"F0.wireOp",EDGE,"E57"),sQuery(id+"F0.wireOp",EDGE,"E58"),sQuery(id+"F0.wireOp",EDGE,"E59"),sQuery(id+"F0.wireOp",EDGE,"E60"),sQuery(id+"F0.wireOp",EDGE,"E61"),sQuery(id+"F0.wireOp",EDGE,"E62"),sQuery(id+"F0.wireOp",EDGE,"E63"),sQuery(id+"F0.wireOp",EDGE,"E64"),sQuery(id+"F0.wireOp",EDGE,"E65"),sQuery(id+"F0.wireOp",EDGE,"E66"),sQuery(id+"F0.wireOp",EDGE,"E67"),sQuery(id+"F0.wireOp",EDGE,"E68"),sQuery(id+"F0.wireOp",EDGE,"E69"),sQuery(id+"F0.wireOp",EDGE,"E70"),sQuery(id+"F0.wireOp",EDGE,"E71"),sQuery(id+"F0.wireOp",EDGE,"E72"),sQuery(id+"F0.wireOp",EDGE,"E73"),sQuery(id+"F0.wireOp",EDGE,"E74"),sQuery(id+"F0.wireOp",EDGE,"E75"),sQuery(id+"F0.wireOp",EDGE,"E76"),sQuery(id+"F0.wireOp",EDGE,"E77"),sQuery(id+"F0.wireOp",EDGE,"E78"),sQuery(id+"F0.wireOp",EDGE,"E79"),sQuery(id+"F0.wireOp",EDGE,"E80"),sQuery(id+"F0.wireOp",EDGE,"E81"),sQuery(id+"F0.wireOp",EDGE,"E82"),sQuery(id+"F0.wireOp",EDGE,"E83"),sQuery(id+"F0.wireOp",EDGE,"E84"),sQuery(id+"F0.wireOp",EDGE,"E85"),sQuery(id+"F0.wireOp",EDGE,"E86"),sQuery(id+"F0.wireOp",EDGE,"E87"),sQuery(id+"F0.wireOp",EDGE,"E88"),sQuery(id+"F0.wireOp",EDGE,"E89"),sQuery(id+"F0.wireOp",EDGE,"E90"),sQuery(id+"F0.wireOp",EDGE,"E91"),sQuery(id+"F0.wireOp",EDGE,"E92"),sQuery(id+"F0.wireOp",EDGE,"E93"),sQuery(id+"F0.wireOp",EDGE,"E94"),sQuery(id+"F0.wireOp",EDGE,"E95"),sQuery(id+"F0.wireOp",EDGE,"E96"),sQuery(id+"F0.wireOp",EDGE,"E97"),sQuery(id+"F0.wireOp",EDGE,"E98"),sQuery(id+"F0.wireOp",EDGE,"E99"),sQuery(id+"F0.wireOp",EDGE,"E100"),sQuery(id+"F0.wireOp",EDGE,"E101"),sQuery(id+"F0.wireOp",EDGE,"E102"),sQuery(id+"F0.wireOp",EDGE,"E103"),sQuery(id+"F0.wireOp",EDGE,"E104"),sQuery(id+"F0.wireOp",EDGE,"E105"),sQuery(id+"F0.wireOp",EDGE,"E106"),sQuery(id+"F0.wireOp",EDGE,"E107"),sQuery(id+"F0.wireOp",EDGE,"E108"),sQuery(id+"F0.wireOp",EDGE,"E109"),sQuery(id+"F0.wireOp",EDGE,"E110"),sQuery(id+"F0.wireOp",EDGE,"E111"),sQuery(id+"F0.wireOp",EDGE,"E112"),sQuery(id+"F0.wireOp",EDGE,"E113"),sQuery(id+"F0.wireOp",EDGE,"E114"),sQuery(id+"F0.wireOp",EDGE,"E115")])],"isStart":false})],"blendedInto":[makeQuery(id+"F1.opExtrude","CAP_FACE",FACE,{"disambiguationData":[OSD([sQuery(id+"F0.wireOp",EDGE,"E0"),sQuery(id+"F0.wireOp",EDGE,"E1"),sQuery(id+"F0.wireOp",EDGE,"E2"),sQuery(id+"F0.wireOp",EDGE,"E3"),sQuery(id+"F0.wireOp",EDGE,"E4"),sQuery(id+"F0.wireOp",EDGE,"E5"),sQuery(id+"F0.wireOp",EDGE,"E6"),sQuery(id+"F0.wireOp",EDGE,"E7"),sQuery(id+"F0.wireOp",EDGE,"E8"),sQuery(id+"F0.wireOp",EDGE,"E9"),sQuery(id+"F0.wireOp",EDGE,"E10"),sQuery(id+"F0.wireOp",EDGE,"E11"),sQuery(id+"F0.wireOp",EDGE,"E12"),sQuery(id+"F0.wireOp",EDGE,"E13"),sQuery(id+"F0.wireOp",EDGE,"E14"),sQuery(id+"F0.wireOp",EDGE,"E15"),sQuery(id+"F0.wireOp",EDGE,"E16"),sQuery(id+"F0.wireOp",EDGE,"E17"),sQuery(id+"F0.wireOp",EDGE,"E18"),sQuery(id+"F0.wireOp",EDGE,"E19"),sQuery(id+"F0.wireOp",EDGE,"E20"),sQuery(id+"F0.wireOp",EDGE,"E21"),sQuery(id+"F0.wireOp",EDGE,"E22"),sQuery(id+"F0.wireOp",EDGE,"E23"),sQuery(id+"F0.wireOp",EDGE,"E24"),sQuery(id+"F0.wireOp",EDGE,"E25"),sQuery(id+"F0.wireOp",EDGE,"E26"),sQuery(id+"F0.wireOp",EDGE,"E27"),sQuery(id+"F0.wireOp",EDGE,"E28"),sQuery(id+"F0.wireOp",EDGE,"E29"),sQuery(id+"F0.wireOp",EDGE,"E30"),sQuery(id+"F0.wireOp",EDGE,"E31"),sQuery(id+"F0.wireOp",EDGE,"E32"),sQuery(id+"F0.wireOp",EDGE,"E33"),sQuery(id+"F0.wireOp",EDGE,"E34"),sQuery(id+"F0.wireOp",EDGE,"E35"),sQuery(id+"F0.wireOp",EDGE,"E36"),sQuery(id+"F0.wireOp",EDGE,"E37"),sQuery(id+"F0.wireOp",EDGE,"E38"),sQuery(id+"F0.wireOp",EDGE,"E39"),sQuery(id+"F0.wireOp",EDGE,"E40"),sQuery(id+"F0.wireOp",EDGE,"E41"),sQuery(id+"F0.wireOp",EDGE,"E42"),sQuery(id+"F0.wireOp",EDGE,"E43"),sQuery(id+"F0.wireOp",EDGE,"E44"),sQuery(id+"F0.wireOp",EDGE,"E45"),sQuery(id+"F0.wireOp",EDGE,"E46"),sQuery(id+"F0.wireOp",EDGE,"E47"),sQuery(id+"F0.wireOp",EDGE,"E48"),sQuery(id+"F0.wireOp",EDGE,"E49"),sQuery(id+"F0.wireOp",EDGE,"E50"),sQuery(id+"F0.wireOp",EDGE,"E51"),sQuery(id+"F0.wireOp",EDGE,"E52"),sQuery(id+"F0.wireOp",EDGE,"E53"),sQuery(id+"F0.wireOp",EDGE,"E54"),sQuery(id+"F0.wireOp",EDGE,"E55"),sQuery(id+"F0.wireOp",EDGE,"E56"),sQuery(id+"F0.wireOp",EDGE,"E57"),sQuery(id+"F0.wireOp",EDGE,"E58"),sQuery(id+"F0.wireOp",EDGE,"E59"),sQuery(id+"F0.wireOp",EDGE,"E60"),sQuery(id+"F0.wireOp",EDGE,"E61"),sQuery(id+"F0.wireOp",EDGE,"E62"),sQuery(id+"F0.wireOp",EDGE,"E63"),sQuery(id+"F0.wireOp",EDGE,"E64"),sQuery(id+"F0.wireOp",EDGE,"E65"),sQuery(id+"F0.wireOp",EDGE,"E66"),sQuery(id+"F0.wireOp",EDGE,"E67"),sQuery(id+"F0.wireOp",EDGE,"E68"),sQuery(id+"F0.wireOp",EDGE,"E69"),sQuery(id+"F0.wireOp",EDGE,"E70"),sQuery(id+"F0.wireOp",EDGE,"E71"),sQuery(id+"F0.wireOp",EDGE,"E72"),sQuery(id+"F0.wireOp",EDGE,"E73"),sQuery(id+"F0.wireOp",EDGE,"E74"),sQuery(id+"F0.wireOp",EDGE,"E75"),sQuery(id+"F0.wireOp",EDGE,"E76"),sQuery(id+"F0.wireOp",EDGE,"E77"),sQuery(id+"F0.wireOp",EDGE,"E78"),sQuery(id+"F0.wireOp",EDGE,"E79"),sQuery(id+"F0.wireOp",EDGE,"E80"),sQuery(id+"F0.wireOp",EDGE,"E81"),sQuery(id+"F0.wireOp",EDGE,"E82"),sQuery(id+"F0.wireOp",EDGE,"E83"),sQuery(id+"F0.wireOp",EDGE,"E84"),sQuery(id+"F0.wireOp",EDGE,"E85"),sQuery(id+"F0.wireOp",EDGE,"E86"),sQuery(id+"F0.wireOp",EDGE,"E87"),sQuery(id+"F0.wireOp",EDGE,"E88"),sQuery(id+"F0.wireOp",EDGE,"E89"),sQuery(id+"F0.wireOp",EDGE,"E90"),sQuery(id+"F0.wireOp",EDGE,"E91"),sQuery(id+"F0.wireOp",EDGE,"E92"),sQuery(id+"F0.wireOp",EDGE,"E93"),sQuery(id+"F0.wireOp",EDGE,"E94"),sQuery(id+"F0.wireOp",EDGE,"E95"),sQuery(id+"F0.wireOp",EDGE,"E96"),sQuery(id+"F0.wireOp",EDGE,"E97"),sQuery(id+"F0.wireOp",EDGE,"E98"),sQuery(id+"F0.wireOp",EDGE,"E99"),sQuery(id+"F0.wireOp",EDGE,"E100"),sQuery(id+"F0.wireOp",EDGE,"E101"),sQuery(id+"F0.wireOp",EDGE,"E102"),sQuery(id+"F0.wireOp",EDGE,"E103"),sQuery(id+"F0.wireOp",EDGE,"E104"),sQuery(id+"F0.wireOp",EDGE,"E105"),sQuery(id+"F0.wireOp",EDGE,"E106"),sQuery(id+"F0.wireOp",EDGE,"E107"),sQuery(id+"F0.wireOp",EDGE,"E108"),sQuery(id+"F0.wireOp",EDGE,"E109"),sQuery(id+"F0.wireOp",EDGE,"E110"),sQuery(id+"F0.wireOp",EDGE,"E111"),sQuery(id+"F0.wireOp",EDGE,"E112"),sQuery(id+"F0.wireOp",EDGE,"E113"),sQuery(id+"F0.wireOp",EDGE,"E114"),sQuery(id+"F0.wireOp",EDGE,"E115")])],"isStart":false})]});
            var Q36;
            Q36=makeQuery(id+"F6.opFillet","BLEND_EDGE",EDGE,{"blendedFrom":[makeQuery(id+"F5.boolean.opBoolean","COPY",EDGE,{"derivedFrom":makeQuery(id+"F5.opExtrude","CAP_EDGE",EDGE,{"disambiguationData":[OSD([sQuery(id+"F4.wireOp",EDGE,"E759.0.3.5")])],"isStart":false})}),makeQuery(id+"F1.opExtrude","CAP_FACE",FACE,{"disambiguationData":[OSD([sQuery(id+"F0.wireOp",EDGE,"E0"),sQuery(id+"F0.wireOp",EDGE,"E1"),sQuery(id+"F0.wireOp",EDGE,"E2"),sQuery(id+"F0.wireOp",EDGE,"E3"),sQuery(id+"F0.wireOp",EDGE,"E4"),sQuery(id+"F0.wireOp",EDGE,"E5"),sQuery(id+"F0.wireOp",EDGE,"E6"),sQuery(id+"F0.wireOp",EDGE,"E7"),sQuery(id+"F0.wireOp",EDGE,"E8"),sQuery(id+"F0.wireOp",EDGE,"E9"),sQuery(id+"F0.wireOp",EDGE,"E10"),sQuery(id+"F0.wireOp",EDGE,"E11"),sQuery(id+"F0.wireOp",EDGE,"E12"),sQuery(id+"F0.wireOp",EDGE,"E13"),sQuery(id+"F0.wireOp",EDGE,"E14"),sQuery(id+"F0.wireOp",EDGE,"E15"),sQuery(id+"F0.wireOp",EDGE,"E16"),sQuery(id+"F0.wireOp",EDGE,"E17"),sQuery(id+"F0.wireOp",EDGE,"E18"),sQuery(id+"F0.wireOp",EDGE,"E19"),sQuery(id+"F0.wireOp",EDGE,"E20"),sQuery(id+"F0.wireOp",EDGE,"E21"),sQuery(id+"F0.wireOp",EDGE,"E22"),sQuery(id+"F0.wireOp",EDGE,"E23"),sQuery(id+"F0.wireOp",EDGE,"E24"),sQuery(id+"F0.wireOp",EDGE,"E25"),sQuery(id+"F0.wireOp",EDGE,"E26"),sQuery(id+"F0.wireOp",EDGE,"E27"),sQuery(id+"F0.wireOp",EDGE,"E28"),sQuery(id+"F0.wireOp",EDGE,"E29"),sQuery(id+"F0.wireOp",EDGE,"E30"),sQuery(id+"F0.wireOp",EDGE,"E31"),sQuery(id+"F0.wireOp",EDGE,"E32"),sQuery(id+"F0.wireOp",EDGE,"E33"),sQuery(id+"F0.wireOp",EDGE,"E34"),sQuery(id+"F0.wireOp",EDGE,"E35"),sQuery(id+"F0.wireOp",EDGE,"E36"),sQuery(id+"F0.wireOp",EDGE,"E37"),sQuery(id+"F0.wireOp",EDGE,"E38"),sQuery(id+"F0.wireOp",EDGE,"E39"),sQuery(id+"F0.wireOp",EDGE,"E40"),sQuery(id+"F0.wireOp",EDGE,"E41"),sQuery(id+"F0.wireOp",EDGE,"E42"),sQuery(id+"F0.wireOp",EDGE,"E43"),sQuery(id+"F0.wireOp",EDGE,"E44"),sQuery(id+"F0.wireOp",EDGE,"E45"),sQuery(id+"F0.wireOp",EDGE,"E46"),sQuery(id+"F0.wireOp",EDGE,"E47"),sQuery(id+"F0.wireOp",EDGE,"E48"),sQuery(id+"F0.wireOp",EDGE,"E49"),sQuery(id+"F0.wireOp",EDGE,"E50"),sQuery(id+"F0.wireOp",EDGE,"E51"),sQuery(id+"F0.wireOp",EDGE,"E52"),sQuery(id+"F0.wireOp",EDGE,"E53"),sQuery(id+"F0.wireOp",EDGE,"E54"),sQuery(id+"F0.wireOp",EDGE,"E55"),sQuery(id+"F0.wireOp",EDGE,"E56"),sQuery(id+"F0.wireOp",EDGE,"E57"),sQuery(id+"F0.wireOp",EDGE,"E58"),sQuery(id+"F0.wireOp",EDGE,"E59"),sQuery(id+"F0.wireOp",EDGE,"E60"),sQuery(id+"F0.wireOp",EDGE,"E61"),sQuery(id+"F0.wireOp",EDGE,"E62"),sQuery(id+"F0.wireOp",EDGE,"E63"),sQuery(id+"F0.wireOp",EDGE,"E64"),sQuery(id+"F0.wireOp",EDGE,"E65"),sQuery(id+"F0.wireOp",EDGE,"E66"),sQuery(id+"F0.wireOp",EDGE,"E67"),sQuery(id+"F0.wireOp",EDGE,"E68"),sQuery(id+"F0.wireOp",EDGE,"E69"),sQuery(id+"F0.wireOp",EDGE,"E70"),sQuery(id+"F0.wireOp",EDGE,"E71"),sQuery(id+"F0.wireOp",EDGE,"E72"),sQuery(id+"F0.wireOp",EDGE,"E73"),sQuery(id+"F0.wireOp",EDGE,"E74"),sQuery(id+"F0.wireOp",EDGE,"E75"),sQuery(id+"F0.wireOp",EDGE,"E76"),sQuery(id+"F0.wireOp",EDGE,"E77"),sQuery(id+"F0.wireOp",EDGE,"E78"),sQuery(id+"F0.wireOp",EDGE,"E79"),sQuery(id+"F0.wireOp",EDGE,"E80"),sQuery(id+"F0.wireOp",EDGE,"E81"),sQuery(id+"F0.wireOp",EDGE,"E82"),sQuery(id+"F0.wireOp",EDGE,"E83"),sQuery(id+"F0.wireOp",EDGE,"E84"),sQuery(id+"F0.wireOp",EDGE,"E85"),sQuery(id+"F0.wireOp",EDGE,"E86"),sQuery(id+"F0.wireOp",EDGE,"E87"),sQuery(id+"F0.wireOp",EDGE,"E88"),sQuery(id+"F0.wireOp",EDGE,"E89"),sQuery(id+"F0.wireOp",EDGE,"E90"),sQuery(id+"F0.wireOp",EDGE,"E91"),sQuery(id+"F0.wireOp",EDGE,"E92"),sQuery(id+"F0.wireOp",EDGE,"E93"),sQuery(id+"F0.wireOp",EDGE,"E94"),sQuery(id+"F0.wireOp",EDGE,"E95"),sQuery(id+"F0.wireOp",EDGE,"E96"),sQuery(id+"F0.wireOp",EDGE,"E97"),sQuery(id+"F0.wireOp",EDGE,"E98"),sQuery(id+"F0.wireOp",EDGE,"E99"),sQuery(id+"F0.wireOp",EDGE,"E100"),sQuery(id+"F0.wireOp",EDGE,"E101"),sQuery(id+"F0.wireOp",EDGE,"E102"),sQuery(id+"F0.wireOp",EDGE,"E103"),sQuery(id+"F0.wireOp",EDGE,"E104"),sQuery(id+"F0.wireOp",EDGE,"E105"),sQuery(id+"F0.wireOp",EDGE,"E106"),sQuery(id+"F0.wireOp",EDGE,"E107"),sQuery(id+"F0.wireOp",EDGE,"E108"),sQuery(id+"F0.wireOp",EDGE,"E109"),sQuery(id+"F0.wireOp",EDGE,"E110"),sQuery(id+"F0.wireOp",EDGE,"E111"),sQuery(id+"F0.wireOp",EDGE,"E112"),sQuery(id+"F0.wireOp",EDGE,"E113"),sQuery(id+"F0.wireOp",EDGE,"E114"),sQuery(id+"F0.wireOp",EDGE,"E115")])],"isStart":false})],"blendedInto":[makeQuery(id+"F1.opExtrude","CAP_FACE",FACE,{"disambiguationData":[OSD([sQuery(id+"F0.wireOp",EDGE,"E0"),sQuery(id+"F0.wireOp",EDGE,"E1"),sQuery(id+"F0.wireOp",EDGE,"E2"),sQuery(id+"F0.wireOp",EDGE,"E3"),sQuery(id+"F0.wireOp",EDGE,"E4"),sQuery(id+"F0.wireOp",EDGE,"E5"),sQuery(id+"F0.wireOp",EDGE,"E6"),sQuery(id+"F0.wireOp",EDGE,"E7"),sQuery(id+"F0.wireOp",EDGE,"E8"),sQuery(id+"F0.wireOp",EDGE,"E9"),sQuery(id+"F0.wireOp",EDGE,"E10"),sQuery(id+"F0.wireOp",EDGE,"E11"),sQuery(id+"F0.wireOp",EDGE,"E12"),sQuery(id+"F0.wireOp",EDGE,"E13"),sQuery(id+"F0.wireOp",EDGE,"E14"),sQuery(id+"F0.wireOp",EDGE,"E15"),sQuery(id+"F0.wireOp",EDGE,"E16"),sQuery(id+"F0.wireOp",EDGE,"E17"),sQuery(id+"F0.wireOp",EDGE,"E18"),sQuery(id+"F0.wireOp",EDGE,"E19"),sQuery(id+"F0.wireOp",EDGE,"E20"),sQuery(id+"F0.wireOp",EDGE,"E21"),sQuery(id+"F0.wireOp",EDGE,"E22"),sQuery(id+"F0.wireOp",EDGE,"E23"),sQuery(id+"F0.wireOp",EDGE,"E24"),sQuery(id+"F0.wireOp",EDGE,"E25"),sQuery(id+"F0.wireOp",EDGE,"E26"),sQuery(id+"F0.wireOp",EDGE,"E27"),sQuery(id+"F0.wireOp",EDGE,"E28"),sQuery(id+"F0.wireOp",EDGE,"E29"),sQuery(id+"F0.wireOp",EDGE,"E30"),sQuery(id+"F0.wireOp",EDGE,"E31"),sQuery(id+"F0.wireOp",EDGE,"E32"),sQuery(id+"F0.wireOp",EDGE,"E33"),sQuery(id+"F0.wireOp",EDGE,"E34"),sQuery(id+"F0.wireOp",EDGE,"E35"),sQuery(id+"F0.wireOp",EDGE,"E36"),sQuery(id+"F0.wireOp",EDGE,"E37"),sQuery(id+"F0.wireOp",EDGE,"E38"),sQuery(id+"F0.wireOp",EDGE,"E39"),sQuery(id+"F0.wireOp",EDGE,"E40"),sQuery(id+"F0.wireOp",EDGE,"E41"),sQuery(id+"F0.wireOp",EDGE,"E42"),sQuery(id+"F0.wireOp",EDGE,"E43"),sQuery(id+"F0.wireOp",EDGE,"E44"),sQuery(id+"F0.wireOp",EDGE,"E45"),sQuery(id+"F0.wireOp",EDGE,"E46"),sQuery(id+"F0.wireOp",EDGE,"E47"),sQuery(id+"F0.wireOp",EDGE,"E48"),sQuery(id+"F0.wireOp",EDGE,"E49"),sQuery(id+"F0.wireOp",EDGE,"E50"),sQuery(id+"F0.wireOp",EDGE,"E51"),sQuery(id+"F0.wireOp",EDGE,"E52"),sQuery(id+"F0.wireOp",EDGE,"E53"),sQuery(id+"F0.wireOp",EDGE,"E54"),sQuery(id+"F0.wireOp",EDGE,"E55"),sQuery(id+"F0.wireOp",EDGE,"E56"),sQuery(id+"F0.wireOp",EDGE,"E57"),sQuery(id+"F0.wireOp",EDGE,"E58"),sQuery(id+"F0.wireOp",EDGE,"E59"),sQuery(id+"F0.wireOp",EDGE,"E60"),sQuery(id+"F0.wireOp",EDGE,"E61"),sQuery(id+"F0.wireOp",EDGE,"E62"),sQuery(id+"F0.wireOp",EDGE,"E63"),sQuery(id+"F0.wireOp",EDGE,"E64"),sQuery(id+"F0.wireOp",EDGE,"E65"),sQuery(id+"F0.wireOp",EDGE,"E66"),sQuery(id+"F0.wireOp",EDGE,"E67"),sQuery(id+"F0.wireOp",EDGE,"E68"),sQuery(id+"F0.wireOp",EDGE,"E69"),sQuery(id+"F0.wireOp",EDGE,"E70"),sQuery(id+"F0.wireOp",EDGE,"E71"),sQuery(id+"F0.wireOp",EDGE,"E72"),sQuery(id+"F0.wireOp",EDGE,"E73"),sQuery(id+"F0.wireOp",EDGE,"E74"),sQuery(id+"F0.wireOp",EDGE,"E75"),sQuery(id+"F0.wireOp",EDGE,"E76"),sQuery(id+"F0.wireOp",EDGE,"E77"),sQuery(id+"F0.wireOp",EDGE,"E78"),sQuery(id+"F0.wireOp",EDGE,"E79"),sQuery(id+"F0.wireOp",EDGE,"E80"),sQuery(id+"F0.wireOp",EDGE,"E81"),sQuery(id+"F0.wireOp",EDGE,"E82"),sQuery(id+"F0.wireOp",EDGE,"E83"),sQuery(id+"F0.wireOp",EDGE,"E84"),sQuery(id+"F0.wireOp",EDGE,"E85"),sQuery(id+"F0.wireOp",EDGE,"E86"),sQuery(id+"F0.wireOp",EDGE,"E87"),sQuery(id+"F0.wireOp",EDGE,"E88"),sQuery(id+"F0.wireOp",EDGE,"E89"),sQuery(id+"F0.wireOp",EDGE,"E90"),sQuery(id+"F0.wireOp",EDGE,"E91"),sQuery(id+"F0.wireOp",EDGE,"E92"),sQuery(id+"F0.wireOp",EDGE,"E93"),sQuery(id+"F0.wireOp",EDGE,"E94"),sQuery(id+"F0.wireOp",EDGE,"E95"),sQuery(id+"F0.wireOp",EDGE,"E96"),sQuery(id+"F0.wireOp",EDGE,"E97"),sQuery(id+"F0.wireOp",EDGE,"E98"),sQuery(id+"F0.wireOp",EDGE,"E99"),sQuery(id+"F0.wireOp",EDGE,"E100"),sQuery(id+"F0.wireOp",EDGE,"E101"),sQuery(id+"F0.wireOp",EDGE,"E102"),sQuery(id+"F0.wireOp",EDGE,"E103"),sQuery(id+"F0.wireOp",EDGE,"E104"),sQuery(id+"F0.wireOp",EDGE,"E105"),sQuery(id+"F0.wireOp",EDGE,"E106"),sQuery(id+"F0.wireOp",EDGE,"E107"),sQuery(id+"F0.wireOp",EDGE,"E108"),sQuery(id+"F0.wireOp",EDGE,"E109"),sQuery(id+"F0.wireOp",EDGE,"E110"),sQuery(id+"F0.wireOp",EDGE,"E111"),sQuery(id+"F0.wireOp",EDGE,"E112"),sQuery(id+"F0.wireOp",EDGE,"E113"),sQuery(id+"F0.wireOp",EDGE,"E114"),sQuery(id+"F0.wireOp",EDGE,"E115")])],"isStart":false})]});
            var Q37;
            Q37=makeQuery(id+"F6.opFillet","BLEND_EDGE",EDGE,{"blendedFrom":[makeQuery(id+"F5.boolean.opBoolean","COPY",EDGE,{"derivedFrom":makeQuery(id+"F5.opExtrude","CAP_EDGE",EDGE,{"disambiguationData":[OSD([sQuery(id+"F4.wireOp",EDGE,"E759.0.4.5")])],"isStart":false})}),makeQuery(id+"F1.opExtrude","CAP_FACE",FACE,{"disambiguationData":[OSD([sQuery(id+"F0.wireOp",EDGE,"E0"),sQuery(id+"F0.wireOp",EDGE,"E1"),sQuery(id+"F0.wireOp",EDGE,"E2"),sQuery(id+"F0.wireOp",EDGE,"E3"),sQuery(id+"F0.wireOp",EDGE,"E4"),sQuery(id+"F0.wireOp",EDGE,"E5"),sQuery(id+"F0.wireOp",EDGE,"E6"),sQuery(id+"F0.wireOp",EDGE,"E7"),sQuery(id+"F0.wireOp",EDGE,"E8"),sQuery(id+"F0.wireOp",EDGE,"E9"),sQuery(id+"F0.wireOp",EDGE,"E10"),sQuery(id+"F0.wireOp",EDGE,"E11"),sQuery(id+"F0.wireOp",EDGE,"E12"),sQuery(id+"F0.wireOp",EDGE,"E13"),sQuery(id+"F0.wireOp",EDGE,"E14"),sQuery(id+"F0.wireOp",EDGE,"E15"),sQuery(id+"F0.wireOp",EDGE,"E16"),sQuery(id+"F0.wireOp",EDGE,"E17"),sQuery(id+"F0.wireOp",EDGE,"E18"),sQuery(id+"F0.wireOp",EDGE,"E19"),sQuery(id+"F0.wireOp",EDGE,"E20"),sQuery(id+"F0.wireOp",EDGE,"E21"),sQuery(id+"F0.wireOp",EDGE,"E22"),sQuery(id+"F0.wireOp",EDGE,"E23"),sQuery(id+"F0.wireOp",EDGE,"E24"),sQuery(id+"F0.wireOp",EDGE,"E25"),sQuery(id+"F0.wireOp",EDGE,"E26"),sQuery(id+"F0.wireOp",EDGE,"E27"),sQuery(id+"F0.wireOp",EDGE,"E28"),sQuery(id+"F0.wireOp",EDGE,"E29"),sQuery(id+"F0.wireOp",EDGE,"E30"),sQuery(id+"F0.wireOp",EDGE,"E31"),sQuery(id+"F0.wireOp",EDGE,"E32"),sQuery(id+"F0.wireOp",EDGE,"E33"),sQuery(id+"F0.wireOp",EDGE,"E34"),sQuery(id+"F0.wireOp",EDGE,"E35"),sQuery(id+"F0.wireOp",EDGE,"E36"),sQuery(id+"F0.wireOp",EDGE,"E37"),sQuery(id+"F0.wireOp",EDGE,"E38"),sQuery(id+"F0.wireOp",EDGE,"E39"),sQuery(id+"F0.wireOp",EDGE,"E40"),sQuery(id+"F0.wireOp",EDGE,"E41"),sQuery(id+"F0.wireOp",EDGE,"E42"),sQuery(id+"F0.wireOp",EDGE,"E43"),sQuery(id+"F0.wireOp",EDGE,"E44"),sQuery(id+"F0.wireOp",EDGE,"E45"),sQuery(id+"F0.wireOp",EDGE,"E46"),sQuery(id+"F0.wireOp",EDGE,"E47"),sQuery(id+"F0.wireOp",EDGE,"E48"),sQuery(id+"F0.wireOp",EDGE,"E49"),sQuery(id+"F0.wireOp",EDGE,"E50"),sQuery(id+"F0.wireOp",EDGE,"E51"),sQuery(id+"F0.wireOp",EDGE,"E52"),sQuery(id+"F0.wireOp",EDGE,"E53"),sQuery(id+"F0.wireOp",EDGE,"E54"),sQuery(id+"F0.wireOp",EDGE,"E55"),sQuery(id+"F0.wireOp",EDGE,"E56"),sQuery(id+"F0.wireOp",EDGE,"E57"),sQuery(id+"F0.wireOp",EDGE,"E58"),sQuery(id+"F0.wireOp",EDGE,"E59"),sQuery(id+"F0.wireOp",EDGE,"E60"),sQuery(id+"F0.wireOp",EDGE,"E61"),sQuery(id+"F0.wireOp",EDGE,"E62"),sQuery(id+"F0.wireOp",EDGE,"E63"),sQuery(id+"F0.wireOp",EDGE,"E64"),sQuery(id+"F0.wireOp",EDGE,"E65"),sQuery(id+"F0.wireOp",EDGE,"E66"),sQuery(id+"F0.wireOp",EDGE,"E67"),sQuery(id+"F0.wireOp",EDGE,"E68"),sQuery(id+"F0.wireOp",EDGE,"E69"),sQuery(id+"F0.wireOp",EDGE,"E70"),sQuery(id+"F0.wireOp",EDGE,"E71"),sQuery(id+"F0.wireOp",EDGE,"E72"),sQuery(id+"F0.wireOp",EDGE,"E73"),sQuery(id+"F0.wireOp",EDGE,"E74"),sQuery(id+"F0.wireOp",EDGE,"E75"),sQuery(id+"F0.wireOp",EDGE,"E76"),sQuery(id+"F0.wireOp",EDGE,"E77"),sQuery(id+"F0.wireOp",EDGE,"E78"),sQuery(id+"F0.wireOp",EDGE,"E79"),sQuery(id+"F0.wireOp",EDGE,"E80"),sQuery(id+"F0.wireOp",EDGE,"E81"),sQuery(id+"F0.wireOp",EDGE,"E82"),sQuery(id+"F0.wireOp",EDGE,"E83"),sQuery(id+"F0.wireOp",EDGE,"E84"),sQuery(id+"F0.wireOp",EDGE,"E85"),sQuery(id+"F0.wireOp",EDGE,"E86"),sQuery(id+"F0.wireOp",EDGE,"E87"),sQuery(id+"F0.wireOp",EDGE,"E88"),sQuery(id+"F0.wireOp",EDGE,"E89"),sQuery(id+"F0.wireOp",EDGE,"E90"),sQuery(id+"F0.wireOp",EDGE,"E91"),sQuery(id+"F0.wireOp",EDGE,"E92"),sQuery(id+"F0.wireOp",EDGE,"E93"),sQuery(id+"F0.wireOp",EDGE,"E94"),sQuery(id+"F0.wireOp",EDGE,"E95"),sQuery(id+"F0.wireOp",EDGE,"E96"),sQuery(id+"F0.wireOp",EDGE,"E97"),sQuery(id+"F0.wireOp",EDGE,"E98"),sQuery(id+"F0.wireOp",EDGE,"E99"),sQuery(id+"F0.wireOp",EDGE,"E100"),sQuery(id+"F0.wireOp",EDGE,"E101"),sQuery(id+"F0.wireOp",EDGE,"E102"),sQuery(id+"F0.wireOp",EDGE,"E103"),sQuery(id+"F0.wireOp",EDGE,"E104"),sQuery(id+"F0.wireOp",EDGE,"E105"),sQuery(id+"F0.wireOp",EDGE,"E106"),sQuery(id+"F0.wireOp",EDGE,"E107"),sQuery(id+"F0.wireOp",EDGE,"E108"),sQuery(id+"F0.wireOp",EDGE,"E109"),sQuery(id+"F0.wireOp",EDGE,"E110"),sQuery(id+"F0.wireOp",EDGE,"E111"),sQuery(id+"F0.wireOp",EDGE,"E112"),sQuery(id+"F0.wireOp",EDGE,"E113"),sQuery(id+"F0.wireOp",EDGE,"E114"),sQuery(id+"F0.wireOp",EDGE,"E115")])],"isStart":false})],"blendedInto":[makeQuery(id+"F1.opExtrude","CAP_FACE",FACE,{"disambiguationData":[OSD([sQuery(id+"F0.wireOp",EDGE,"E0"),sQuery(id+"F0.wireOp",EDGE,"E1"),sQuery(id+"F0.wireOp",EDGE,"E2"),sQuery(id+"F0.wireOp",EDGE,"E3"),sQuery(id+"F0.wireOp",EDGE,"E4"),sQuery(id+"F0.wireOp",EDGE,"E5"),sQuery(id+"F0.wireOp",EDGE,"E6"),sQuery(id+"F0.wireOp",EDGE,"E7"),sQuery(id+"F0.wireOp",EDGE,"E8"),sQuery(id+"F0.wireOp",EDGE,"E9"),sQuery(id+"F0.wireOp",EDGE,"E10"),sQuery(id+"F0.wireOp",EDGE,"E11"),sQuery(id+"F0.wireOp",EDGE,"E12"),sQuery(id+"F0.wireOp",EDGE,"E13"),sQuery(id+"F0.wireOp",EDGE,"E14"),sQuery(id+"F0.wireOp",EDGE,"E15"),sQuery(id+"F0.wireOp",EDGE,"E16"),sQuery(id+"F0.wireOp",EDGE,"E17"),sQuery(id+"F0.wireOp",EDGE,"E18"),sQuery(id+"F0.wireOp",EDGE,"E19"),sQuery(id+"F0.wireOp",EDGE,"E20"),sQuery(id+"F0.wireOp",EDGE,"E21"),sQuery(id+"F0.wireOp",EDGE,"E22"),sQuery(id+"F0.wireOp",EDGE,"E23"),sQuery(id+"F0.wireOp",EDGE,"E24"),sQuery(id+"F0.wireOp",EDGE,"E25"),sQuery(id+"F0.wireOp",EDGE,"E26"),sQuery(id+"F0.wireOp",EDGE,"E27"),sQuery(id+"F0.wireOp",EDGE,"E28"),sQuery(id+"F0.wireOp",EDGE,"E29"),sQuery(id+"F0.wireOp",EDGE,"E30"),sQuery(id+"F0.wireOp",EDGE,"E31"),sQuery(id+"F0.wireOp",EDGE,"E32"),sQuery(id+"F0.wireOp",EDGE,"E33"),sQuery(id+"F0.wireOp",EDGE,"E34"),sQuery(id+"F0.wireOp",EDGE,"E35"),sQuery(id+"F0.wireOp",EDGE,"E36"),sQuery(id+"F0.wireOp",EDGE,"E37"),sQuery(id+"F0.wireOp",EDGE,"E38"),sQuery(id+"F0.wireOp",EDGE,"E39"),sQuery(id+"F0.wireOp",EDGE,"E40"),sQuery(id+"F0.wireOp",EDGE,"E41"),sQuery(id+"F0.wireOp",EDGE,"E42"),sQuery(id+"F0.wireOp",EDGE,"E43"),sQuery(id+"F0.wireOp",EDGE,"E44"),sQuery(id+"F0.wireOp",EDGE,"E45"),sQuery(id+"F0.wireOp",EDGE,"E46"),sQuery(id+"F0.wireOp",EDGE,"E47"),sQuery(id+"F0.wireOp",EDGE,"E48"),sQuery(id+"F0.wireOp",EDGE,"E49"),sQuery(id+"F0.wireOp",EDGE,"E50"),sQuery(id+"F0.wireOp",EDGE,"E51"),sQuery(id+"F0.wireOp",EDGE,"E52"),sQuery(id+"F0.wireOp",EDGE,"E53"),sQuery(id+"F0.wireOp",EDGE,"E54"),sQuery(id+"F0.wireOp",EDGE,"E55"),sQuery(id+"F0.wireOp",EDGE,"E56"),sQuery(id+"F0.wireOp",EDGE,"E57"),sQuery(id+"F0.wireOp",EDGE,"E58"),sQuery(id+"F0.wireOp",EDGE,"E59"),sQuery(id+"F0.wireOp",EDGE,"E60"),sQuery(id+"F0.wireOp",EDGE,"E61"),sQuery(id+"F0.wireOp",EDGE,"E62"),sQuery(id+"F0.wireOp",EDGE,"E63"),sQuery(id+"F0.wireOp",EDGE,"E64"),sQuery(id+"F0.wireOp",EDGE,"E65"),sQuery(id+"F0.wireOp",EDGE,"E66"),sQuery(id+"F0.wireOp",EDGE,"E67"),sQuery(id+"F0.wireOp",EDGE,"E68"),sQuery(id+"F0.wireOp",EDGE,"E69"),sQuery(id+"F0.wireOp",EDGE,"E70"),sQuery(id+"F0.wireOp",EDGE,"E71"),sQuery(id+"F0.wireOp",EDGE,"E72"),sQuery(id+"F0.wireOp",EDGE,"E73"),sQuery(id+"F0.wireOp",EDGE,"E74"),sQuery(id+"F0.wireOp",EDGE,"E75"),sQuery(id+"F0.wireOp",EDGE,"E76"),sQuery(id+"F0.wireOp",EDGE,"E77"),sQuery(id+"F0.wireOp",EDGE,"E78"),sQuery(id+"F0.wireOp",EDGE,"E79"),sQuery(id+"F0.wireOp",EDGE,"E80"),sQuery(id+"F0.wireOp",EDGE,"E81"),sQuery(id+"F0.wireOp",EDGE,"E82"),sQuery(id+"F0.wireOp",EDGE,"E83"),sQuery(id+"F0.wireOp",EDGE,"E84"),sQuery(id+"F0.wireOp",EDGE,"E85"),sQuery(id+"F0.wireOp",EDGE,"E86"),sQuery(id+"F0.wireOp",EDGE,"E87"),sQuery(id+"F0.wireOp",EDGE,"E88"),sQuery(id+"F0.wireOp",EDGE,"E89"),sQuery(id+"F0.wireOp",EDGE,"E90"),sQuery(id+"F0.wireOp",EDGE,"E91"),sQuery(id+"F0.wireOp",EDGE,"E92"),sQuery(id+"F0.wireOp",EDGE,"E93"),sQuery(id+"F0.wireOp",EDGE,"E94"),sQuery(id+"F0.wireOp",EDGE,"E95"),sQuery(id+"F0.wireOp",EDGE,"E96"),sQuery(id+"F0.wireOp",EDGE,"E97"),sQuery(id+"F0.wireOp",EDGE,"E98"),sQuery(id+"F0.wireOp",EDGE,"E99"),sQuery(id+"F0.wireOp",EDGE,"E100"),sQuery(id+"F0.wireOp",EDGE,"E101"),sQuery(id+"F0.wireOp",EDGE,"E102"),sQuery(id+"F0.wireOp",EDGE,"E103"),sQuery(id+"F0.wireOp",EDGE,"E104"),sQuery(id+"F0.wireOp",EDGE,"E105"),sQuery(id+"F0.wireOp",EDGE,"E106"),sQuery(id+"F0.wireOp",EDGE,"E107"),sQuery(id+"F0.wireOp",EDGE,"E108"),sQuery(id+"F0.wireOp",EDGE,"E109"),sQuery(id+"F0.wireOp",EDGE,"E110"),sQuery(id+"F0.wireOp",EDGE,"E111"),sQuery(id+"F0.wireOp",EDGE,"E112"),sQuery(id+"F0.wireOp",EDGE,"E113"),sQuery(id+"F0.wireOp",EDGE,"E114"),sQuery(id+"F0.wireOp",EDGE,"E115")])],"isStart":false})]});
            var Q38;
            Q38=makeQuery(id+"F6.opFillet","BLEND_EDGE",EDGE,{"blendedFrom":[makeQuery(id+"F5.boolean.opBoolean","COPY",EDGE,{"derivedFrom":makeQuery(id+"F5.opExtrude","CAP_EDGE",EDGE,{"disambiguationData":[OSD([sQuery(id+"F4.wireOp",EDGE,"E759.0.5.5")])],"isStart":false})}),makeQuery(id+"F1.opExtrude","CAP_FACE",FACE,{"disambiguationData":[OSD([sQuery(id+"F0.wireOp",EDGE,"E0"),sQuery(id+"F0.wireOp",EDGE,"E1"),sQuery(id+"F0.wireOp",EDGE,"E2"),sQuery(id+"F0.wireOp",EDGE,"E3"),sQuery(id+"F0.wireOp",EDGE,"E4"),sQuery(id+"F0.wireOp",EDGE,"E5"),sQuery(id+"F0.wireOp",EDGE,"E6"),sQuery(id+"F0.wireOp",EDGE,"E7"),sQuery(id+"F0.wireOp",EDGE,"E8"),sQuery(id+"F0.wireOp",EDGE,"E9"),sQuery(id+"F0.wireOp",EDGE,"E10"),sQuery(id+"F0.wireOp",EDGE,"E11"),sQuery(id+"F0.wireOp",EDGE,"E12"),sQuery(id+"F0.wireOp",EDGE,"E13"),sQuery(id+"F0.wireOp",EDGE,"E14"),sQuery(id+"F0.wireOp",EDGE,"E15"),sQuery(id+"F0.wireOp",EDGE,"E16"),sQuery(id+"F0.wireOp",EDGE,"E17"),sQuery(id+"F0.wireOp",EDGE,"E18"),sQuery(id+"F0.wireOp",EDGE,"E19"),sQuery(id+"F0.wireOp",EDGE,"E20"),sQuery(id+"F0.wireOp",EDGE,"E21"),sQuery(id+"F0.wireOp",EDGE,"E22"),sQuery(id+"F0.wireOp",EDGE,"E23"),sQuery(id+"F0.wireOp",EDGE,"E24"),sQuery(id+"F0.wireOp",EDGE,"E25"),sQuery(id+"F0.wireOp",EDGE,"E26"),sQuery(id+"F0.wireOp",EDGE,"E27"),sQuery(id+"F0.wireOp",EDGE,"E28"),sQuery(id+"F0.wireOp",EDGE,"E29"),sQuery(id+"F0.wireOp",EDGE,"E30"),sQuery(id+"F0.wireOp",EDGE,"E31"),sQuery(id+"F0.wireOp",EDGE,"E32"),sQuery(id+"F0.wireOp",EDGE,"E33"),sQuery(id+"F0.wireOp",EDGE,"E34"),sQuery(id+"F0.wireOp",EDGE,"E35"),sQuery(id+"F0.wireOp",EDGE,"E36"),sQuery(id+"F0.wireOp",EDGE,"E37"),sQuery(id+"F0.wireOp",EDGE,"E38"),sQuery(id+"F0.wireOp",EDGE,"E39"),sQuery(id+"F0.wireOp",EDGE,"E40"),sQuery(id+"F0.wireOp",EDGE,"E41"),sQuery(id+"F0.wireOp",EDGE,"E42"),sQuery(id+"F0.wireOp",EDGE,"E43"),sQuery(id+"F0.wireOp",EDGE,"E44"),sQuery(id+"F0.wireOp",EDGE,"E45"),sQuery(id+"F0.wireOp",EDGE,"E46"),sQuery(id+"F0.wireOp",EDGE,"E47"),sQuery(id+"F0.wireOp",EDGE,"E48"),sQuery(id+"F0.wireOp",EDGE,"E49"),sQuery(id+"F0.wireOp",EDGE,"E50"),sQuery(id+"F0.wireOp",EDGE,"E51"),sQuery(id+"F0.wireOp",EDGE,"E52"),sQuery(id+"F0.wireOp",EDGE,"E53"),sQuery(id+"F0.wireOp",EDGE,"E54"),sQuery(id+"F0.wireOp",EDGE,"E55"),sQuery(id+"F0.wireOp",EDGE,"E56"),sQuery(id+"F0.wireOp",EDGE,"E57"),sQuery(id+"F0.wireOp",EDGE,"E58"),sQuery(id+"F0.wireOp",EDGE,"E59"),sQuery(id+"F0.wireOp",EDGE,"E60"),sQuery(id+"F0.wireOp",EDGE,"E61"),sQuery(id+"F0.wireOp",EDGE,"E62"),sQuery(id+"F0.wireOp",EDGE,"E63"),sQuery(id+"F0.wireOp",EDGE,"E64"),sQuery(id+"F0.wireOp",EDGE,"E65"),sQuery(id+"F0.wireOp",EDGE,"E66"),sQuery(id+"F0.wireOp",EDGE,"E67"),sQuery(id+"F0.wireOp",EDGE,"E68"),sQuery(id+"F0.wireOp",EDGE,"E69"),sQuery(id+"F0.wireOp",EDGE,"E70"),sQuery(id+"F0.wireOp",EDGE,"E71"),sQuery(id+"F0.wireOp",EDGE,"E72"),sQuery(id+"F0.wireOp",EDGE,"E73"),sQuery(id+"F0.wireOp",EDGE,"E74"),sQuery(id+"F0.wireOp",EDGE,"E75"),sQuery(id+"F0.wireOp",EDGE,"E76"),sQuery(id+"F0.wireOp",EDGE,"E77"),sQuery(id+"F0.wireOp",EDGE,"E78"),sQuery(id+"F0.wireOp",EDGE,"E79"),sQuery(id+"F0.wireOp",EDGE,"E80"),sQuery(id+"F0.wireOp",EDGE,"E81"),sQuery(id+"F0.wireOp",EDGE,"E82"),sQuery(id+"F0.wireOp",EDGE,"E83"),sQuery(id+"F0.wireOp",EDGE,"E84"),sQuery(id+"F0.wireOp",EDGE,"E85"),sQuery(id+"F0.wireOp",EDGE,"E86"),sQuery(id+"F0.wireOp",EDGE,"E87"),sQuery(id+"F0.wireOp",EDGE,"E88"),sQuery(id+"F0.wireOp",EDGE,"E89"),sQuery(id+"F0.wireOp",EDGE,"E90"),sQuery(id+"F0.wireOp",EDGE,"E91"),sQuery(id+"F0.wireOp",EDGE,"E92"),sQuery(id+"F0.wireOp",EDGE,"E93"),sQuery(id+"F0.wireOp",EDGE,"E94"),sQuery(id+"F0.wireOp",EDGE,"E95"),sQuery(id+"F0.wireOp",EDGE,"E96"),sQuery(id+"F0.wireOp",EDGE,"E97"),sQuery(id+"F0.wireOp",EDGE,"E98"),sQuery(id+"F0.wireOp",EDGE,"E99"),sQuery(id+"F0.wireOp",EDGE,"E100"),sQuery(id+"F0.wireOp",EDGE,"E101"),sQuery(id+"F0.wireOp",EDGE,"E102"),sQuery(id+"F0.wireOp",EDGE,"E103"),sQuery(id+"F0.wireOp",EDGE,"E104"),sQuery(id+"F0.wireOp",EDGE,"E105"),sQuery(id+"F0.wireOp",EDGE,"E106"),sQuery(id+"F0.wireOp",EDGE,"E107"),sQuery(id+"F0.wireOp",EDGE,"E108"),sQuery(id+"F0.wireOp",EDGE,"E109"),sQuery(id+"F0.wireOp",EDGE,"E110"),sQuery(id+"F0.wireOp",EDGE,"E111"),sQuery(id+"F0.wireOp",EDGE,"E112"),sQuery(id+"F0.wireOp",EDGE,"E113"),sQuery(id+"F0.wireOp",EDGE,"E114"),sQuery(id+"F0.wireOp",EDGE,"E115")])],"isStart":false})],"blendedInto":[makeQuery(id+"F1.opExtrude","CAP_FACE",FACE,{"disambiguationData":[OSD([sQuery(id+"F0.wireOp",EDGE,"E0"),sQuery(id+"F0.wireOp",EDGE,"E1"),sQuery(id+"F0.wireOp",EDGE,"E2"),sQuery(id+"F0.wireOp",EDGE,"E3"),sQuery(id+"F0.wireOp",EDGE,"E4"),sQuery(id+"F0.wireOp",EDGE,"E5"),sQuery(id+"F0.wireOp",EDGE,"E6"),sQuery(id+"F0.wireOp",EDGE,"E7"),sQuery(id+"F0.wireOp",EDGE,"E8"),sQuery(id+"F0.wireOp",EDGE,"E9"),sQuery(id+"F0.wireOp",EDGE,"E10"),sQuery(id+"F0.wireOp",EDGE,"E11"),sQuery(id+"F0.wireOp",EDGE,"E12"),sQuery(id+"F0.wireOp",EDGE,"E13"),sQuery(id+"F0.wireOp",EDGE,"E14"),sQuery(id+"F0.wireOp",EDGE,"E15"),sQuery(id+"F0.wireOp",EDGE,"E16"),sQuery(id+"F0.wireOp",EDGE,"E17"),sQuery(id+"F0.wireOp",EDGE,"E18"),sQuery(id+"F0.wireOp",EDGE,"E19"),sQuery(id+"F0.wireOp",EDGE,"E20"),sQuery(id+"F0.wireOp",EDGE,"E21"),sQuery(id+"F0.wireOp",EDGE,"E22"),sQuery(id+"F0.wireOp",EDGE,"E23"),sQuery(id+"F0.wireOp",EDGE,"E24"),sQuery(id+"F0.wireOp",EDGE,"E25"),sQuery(id+"F0.wireOp",EDGE,"E26"),sQuery(id+"F0.wireOp",EDGE,"E27"),sQuery(id+"F0.wireOp",EDGE,"E28"),sQuery(id+"F0.wireOp",EDGE,"E29"),sQuery(id+"F0.wireOp",EDGE,"E30"),sQuery(id+"F0.wireOp",EDGE,"E31"),sQuery(id+"F0.wireOp",EDGE,"E32"),sQuery(id+"F0.wireOp",EDGE,"E33"),sQuery(id+"F0.wireOp",EDGE,"E34"),sQuery(id+"F0.wireOp",EDGE,"E35"),sQuery(id+"F0.wireOp",EDGE,"E36"),sQuery(id+"F0.wireOp",EDGE,"E37"),sQuery(id+"F0.wireOp",EDGE,"E38"),sQuery(id+"F0.wireOp",EDGE,"E39"),sQuery(id+"F0.wireOp",EDGE,"E40"),sQuery(id+"F0.wireOp",EDGE,"E41"),sQuery(id+"F0.wireOp",EDGE,"E42"),sQuery(id+"F0.wireOp",EDGE,"E43"),sQuery(id+"F0.wireOp",EDGE,"E44"),sQuery(id+"F0.wireOp",EDGE,"E45"),sQuery(id+"F0.wireOp",EDGE,"E46"),sQuery(id+"F0.wireOp",EDGE,"E47"),sQuery(id+"F0.wireOp",EDGE,"E48"),sQuery(id+"F0.wireOp",EDGE,"E49"),sQuery(id+"F0.wireOp",EDGE,"E50"),sQuery(id+"F0.wireOp",EDGE,"E51"),sQuery(id+"F0.wireOp",EDGE,"E52"),sQuery(id+"F0.wireOp",EDGE,"E53"),sQuery(id+"F0.wireOp",EDGE,"E54"),sQuery(id+"F0.wireOp",EDGE,"E55"),sQuery(id+"F0.wireOp",EDGE,"E56"),sQuery(id+"F0.wireOp",EDGE,"E57"),sQuery(id+"F0.wireOp",EDGE,"E58"),sQuery(id+"F0.wireOp",EDGE,"E59"),sQuery(id+"F0.wireOp",EDGE,"E60"),sQuery(id+"F0.wireOp",EDGE,"E61"),sQuery(id+"F0.wireOp",EDGE,"E62"),sQuery(id+"F0.wireOp",EDGE,"E63"),sQuery(id+"F0.wireOp",EDGE,"E64"),sQuery(id+"F0.wireOp",EDGE,"E65"),sQuery(id+"F0.wireOp",EDGE,"E66"),sQuery(id+"F0.wireOp",EDGE,"E67"),sQuery(id+"F0.wireOp",EDGE,"E68"),sQuery(id+"F0.wireOp",EDGE,"E69"),sQuery(id+"F0.wireOp",EDGE,"E70"),sQuery(id+"F0.wireOp",EDGE,"E71"),sQuery(id+"F0.wireOp",EDGE,"E72"),sQuery(id+"F0.wireOp",EDGE,"E73"),sQuery(id+"F0.wireOp",EDGE,"E74"),sQuery(id+"F0.wireOp",EDGE,"E75"),sQuery(id+"F0.wireOp",EDGE,"E76"),sQuery(id+"F0.wireOp",EDGE,"E77"),sQuery(id+"F0.wireOp",EDGE,"E78"),sQuery(id+"F0.wireOp",EDGE,"E79"),sQuery(id+"F0.wireOp",EDGE,"E80"),sQuery(id+"F0.wireOp",EDGE,"E81"),sQuery(id+"F0.wireOp",EDGE,"E82"),sQuery(id+"F0.wireOp",EDGE,"E83"),sQuery(id+"F0.wireOp",EDGE,"E84"),sQuery(id+"F0.wireOp",EDGE,"E85"),sQuery(id+"F0.wireOp",EDGE,"E86"),sQuery(id+"F0.wireOp",EDGE,"E87"),sQuery(id+"F0.wireOp",EDGE,"E88"),sQuery(id+"F0.wireOp",EDGE,"E89"),sQuery(id+"F0.wireOp",EDGE,"E90"),sQuery(id+"F0.wireOp",EDGE,"E91"),sQuery(id+"F0.wireOp",EDGE,"E92"),sQuery(id+"F0.wireOp",EDGE,"E93"),sQuery(id+"F0.wireOp",EDGE,"E94"),sQuery(id+"F0.wireOp",EDGE,"E95"),sQuery(id+"F0.wireOp",EDGE,"E96"),sQuery(id+"F0.wireOp",EDGE,"E97"),sQuery(id+"F0.wireOp",EDGE,"E98"),sQuery(id+"F0.wireOp",EDGE,"E99"),sQuery(id+"F0.wireOp",EDGE,"E100"),sQuery(id+"F0.wireOp",EDGE,"E101"),sQuery(id+"F0.wireOp",EDGE,"E102"),sQuery(id+"F0.wireOp",EDGE,"E103"),sQuery(id+"F0.wireOp",EDGE,"E104"),sQuery(id+"F0.wireOp",EDGE,"E105"),sQuery(id+"F0.wireOp",EDGE,"E106"),sQuery(id+"F0.wireOp",EDGE,"E107"),sQuery(id+"F0.wireOp",EDGE,"E108"),sQuery(id+"F0.wireOp",EDGE,"E109"),sQuery(id+"F0.wireOp",EDGE,"E110"),sQuery(id+"F0.wireOp",EDGE,"E111"),sQuery(id+"F0.wireOp",EDGE,"E112"),sQuery(id+"F0.wireOp",EDGE,"E113"),sQuery(id+"F0.wireOp",EDGE,"E114"),sQuery(id+"F0.wireOp",EDGE,"E115")])],"isStart":false})]});
            fillet(context, id + "F7", {"entities" : qUnion([Q0, Q1, Q2, Q3, Q4, Q5, Q6, Q7, Q8, Q9, Q10, Q11, Q12, Q13, Q14, Q15, Q16, Q17, Q18, Q19, Q20, Q21, Q22, Q23, Q24, Q25, Q26, Q27, Q28, Q29, Q30, Q31, Q32, Q33, Q34, Q35, Q36, Q37, Q38]), "radius" : 45.72 * mm, "tangentPropagation" : true, "allowEdgeOverflow" : false});
        }
        {
            var Q0;
            Q0=makeQuery(id+"F1.opExtrude","CAP_FACE",FACE,{"disambiguationData":[OSD([sQuery(id+"F0.wireOp",EDGE,"E580"),sQuery(id+"F0.wireOp",EDGE,"E581"),sQuery(id+"F0.wireOp",EDGE,"E582"),sQuery(id+"F0.wireOp",EDGE,"E583"),sQuery(id+"F0.wireOp",EDGE,"E584"),sQuery(id+"F0.wireOp",EDGE,"E585"),sQuery(id+"F0.wireOp",EDGE,"E586"),sQuery(id+"F0.wireOp",EDGE,"E587"),sQuery(id+"F0.wireOp",EDGE,"E588"),sQuery(id+"F0.wireOp",EDGE,"E589"),sQuery(id+"F0.wireOp",EDGE,"E590"),sQuery(id+"F0.wireOp",EDGE,"E591"),sQuery(id+"F0.wireOp",EDGE,"E592"),sQuery(id+"F0.wireOp",EDGE,"E593"),sQuery(id+"F0.wireOp",EDGE,"E594"),sQuery(id+"F0.wireOp",EDGE,"E595"),sQuery(id+"F0.wireOp",EDGE,"E596"),sQuery(id+"F0.wireOp",EDGE,"E597"),sQuery(id+"F0.wireOp",EDGE,"E598"),sQuery(id+"F0.wireOp",EDGE,"E599"),sQuery(id+"F0.wireOp",EDGE,"E600"),sQuery(id+"F0.wireOp",EDGE,"E601"),sQuery(id+"F0.wireOp",EDGE,"E602"),sQuery(id+"F0.wireOp",EDGE,"E603"),sQuery(id+"F0.wireOp",EDGE,"E604"),sQuery(id+"F0.wireOp",EDGE,"E605"),sQuery(id+"F0.wireOp",EDGE,"E606"),sQuery(id+"F0.wireOp",EDGE,"E607"),sQuery(id+"F0.wireOp",EDGE,"E608"),sQuery(id+"F0.wireOp",EDGE,"E609"),sQuery(id+"F0.wireOp",EDGE,"E610"),sQuery(id+"F0.wireOp",EDGE,"E611"),sQuery(id+"F0.wireOp",EDGE,"E612"),sQuery(id+"F0.wireOp",EDGE,"E613"),sQuery(id+"F0.wireOp",EDGE,"E614"),sQuery(id+"F0.wireOp",EDGE,"E615"),sQuery(id+"F0.wireOp",EDGE,"E616"),sQuery(id+"F0.wireOp",EDGE,"E617"),sQuery(id+"F0.wireOp",EDGE,"E618"),sQuery(id+"F0.wireOp",EDGE,"E619"),sQuery(id+"F0.wireOp",EDGE,"E620"),sQuery(id+"F0.wireOp",EDGE,"E621"),sQuery(id+"F0.wireOp",EDGE,"E622"),sQuery(id+"F0.wireOp",EDGE,"E623"),sQuery(id+"F0.wireOp",EDGE,"E624"),sQuery(id+"F0.wireOp",EDGE,"E625"),sQuery(id+"F0.wireOp",EDGE,"E626"),sQuery(id+"F0.wireOp",EDGE,"E627"),sQuery(id+"F0.wireOp",EDGE,"E628"),sQuery(id+"F0.wireOp",EDGE,"E629"),sQuery(id+"F0.wireOp",EDGE,"E630"),sQuery(id+"F0.wireOp",EDGE,"E631"),sQuery(id+"F0.wireOp",EDGE,"E632"),sQuery(id+"F0.wireOp",EDGE,"E633"),sQuery(id+"F0.wireOp",EDGE,"E634"),sQuery(id+"F0.wireOp",EDGE,"E635"),sQuery(id+"F0.wireOp",EDGE,"E636"),sQuery(id+"F0.wireOp",EDGE,"E637"),sQuery(id+"F0.wireOp",EDGE,"E638"),sQuery(id+"F0.wireOp",EDGE,"E639"),sQuery(id+"F0.wireOp",EDGE,"E640"),sQuery(id+"F0.wireOp",EDGE,"E641"),sQuery(id+"F0.wireOp",EDGE,"E642"),sQuery(id+"F0.wireOp",EDGE,"E643"),sQuery(id+"F0.wireOp",EDGE,"E644"),sQuery(id+"F0.wireOp",EDGE,"E645"),sQuery(id+"F0.wireOp",EDGE,"E646"),sQuery(id+"F0.wireOp",EDGE,"E647"),sQuery(id+"F0.wireOp",EDGE,"E648"),sQuery(id+"F0.wireOp",EDGE,"E649"),sQuery(id+"F0.wireOp",EDGE,"E650"),sQuery(id+"F0.wireOp",EDGE,"E651"),sQuery(id+"F0.wireOp",EDGE,"E652"),sQuery(id+"F0.wireOp",EDGE,"E653"),sQuery(id+"F0.wireOp",EDGE,"E654"),sQuery(id+"F0.wireOp",EDGE,"E655"),sQuery(id+"F0.wireOp",EDGE,"E656"),sQuery(id+"F0.wireOp",EDGE,"E657"),sQuery(id+"F0.wireOp",EDGE,"E658"),sQuery(id+"F0.wireOp",EDGE,"E659"),sQuery(id+"F0.wireOp",EDGE,"E660"),sQuery(id+"F0.wireOp",EDGE,"E661"),sQuery(id+"F0.wireOp",EDGE,"E662"),sQuery(id+"F0.wireOp",EDGE,"E663"),sQuery(id+"F0.wireOp",EDGE,"E664"),sQuery(id+"F0.wireOp",EDGE,"E665"),sQuery(id+"F0.wireOp",EDGE,"E666"),sQuery(id+"F0.wireOp",EDGE,"E667"),sQuery(id+"F0.wireOp",EDGE,"E668"),sQuery(id+"F0.wireOp",EDGE,"E669"),sQuery(id+"F0.wireOp",EDGE,"E670"),sQuery(id+"F0.wireOp",EDGE,"E671"),sQuery(id+"F0.wireOp",EDGE,"E672"),sQuery(id+"F0.wireOp",EDGE,"E673"),sQuery(id+"F0.wireOp",EDGE,"E674"),sQuery(id+"F0.wireOp",EDGE,"E675"),sQuery(id+"F0.wireOp",EDGE,"E676"),sQuery(id+"F0.wireOp",EDGE,"E677"),sQuery(id+"F0.wireOp",EDGE,"E678"),sQuery(id+"F0.wireOp",EDGE,"E679"),sQuery(id+"F0.wireOp",EDGE,"E680"),sQuery(id+"F0.wireOp",EDGE,"E681"),sQuery(id+"F0.wireOp",EDGE,"E682"),sQuery(id+"F0.wireOp",EDGE,"E683"),sQuery(id+"F0.wireOp",EDGE,"E684"),sQuery(id+"F0.wireOp",EDGE,"E685"),sQuery(id+"F0.wireOp",EDGE,"E686"),sQuery(id+"F0.wireOp",EDGE,"E687"),sQuery(id+"F0.wireOp",EDGE,"E688"),sQuery(id+"F0.wireOp",EDGE,"E689"),sQuery(id+"F0.wireOp",EDGE,"E690"),sQuery(id+"F0.wireOp",EDGE,"E691"),sQuery(id+"F0.wireOp",EDGE,"E692"),sQuery(id+"F0.wireOp",EDGE,"E693"),sQuery(id+"F0.wireOp",EDGE,"E694"),sQuery(id+"F0.wireOp",EDGE,"E695")])],"isStart":false});
            var sketch = newSketch(context, id + "F8", { "sketchPlane" : qUnion([Q0])});
            skCircle(sketch, "E760", {"center": v(-255.95, 1384.79) * mm, "radius": 1.27 * mm});
            skCircle(sketch, "E761", {"center": v(0, 1345.33) * mm, "radius": 1.27 * mm});
            skCircle(sketch, "E762", {"center": v(-208.17, 950.49) * mm, "radius": 1.27 * mm});
            skCircle(sketch, "E763", {"center": v(147.95, 922.26) * mm, "radius": 1.27 * mm});
            skCircle(sketch, "E764", {"center": v(0, 1011.29) * mm, "radius": 1.27 * mm});
            skCircle(sketch, "E765", {"center": v(134.92, 1376.1) * mm, "radius": 1.27 * mm});
            skCircle(sketch, "E766", {"center": v(178.35, 1161.12) * mm, "radius": 1.27 * mm});
            skCircle(sketch, "E767", {"center": v(-182.12, 1211.07) * mm, "radius": 1.27 * mm});
            skSolve(sketch);
        }
        {
            var Q0;
            Q0=makeQuery(id+"F8.imprint","IMPRINT",FACE,{"disambiguationData":[TD([[makeQuery(id+"F8.imprint","IMPRINT",EDGE,{"derivedFrom":sQuery(id+"F8.wireOp",EDGE,"E765")}),1.0]])]});
            var Q1;
            Q1=makeQuery(id+"F8.imprint","IMPRINT",FACE,{"disambiguationData":[TD([[makeQuery(id+"F8.imprint","IMPRINT",EDGE,{"derivedFrom":sQuery(id+"F8.wireOp",EDGE,"E761")}),1.0]])]});
            var Q2;
            Q2=makeQuery(id+"F8.imprint","IMPRINT",FACE,{"disambiguationData":[TD([[makeQuery(id+"F8.imprint","IMPRINT",EDGE,{"derivedFrom":sQuery(id+"F8.wireOp",EDGE,"E766")}),1.0]])]});
            var Q3;
            Q3=makeQuery(id+"F8.imprint","IMPRINT",FACE,{"disambiguationData":[TD([[makeQuery(id+"F8.imprint","IMPRINT",EDGE,{"derivedFrom":sQuery(id+"F8.wireOp",EDGE,"E764")}),1.0]])]});
            var Q4;
            Q4=makeQuery(id+"F8.imprint","IMPRINT",FACE,{"disambiguationData":[TD([[makeQuery(id+"F8.imprint","IMPRINT",EDGE,{"derivedFrom":sQuery(id+"F8.wireOp",EDGE,"E763")}),1.0]])]});
            var Q5;
            Q5=makeQuery(id+"F8.imprint","IMPRINT",FACE,{"disambiguationData":[TD([[makeQuery(id+"F8.imprint","IMPRINT",EDGE,{"derivedFrom":sQuery(id+"F8.wireOp",EDGE,"E762")}),1.0]])]});
            var Q6;
            Q6=makeQuery(id+"F8.imprint","IMPRINT",FACE,{"disambiguationData":[TD([[makeQuery(id+"F8.imprint","IMPRINT",EDGE,{"derivedFrom":sQuery(id+"F8.wireOp",EDGE,"E767")}),1.0]])]});
            var Q7;
            Q7=makeQuery(id+"F8.imprint","IMPRINT",FACE,{"disambiguationData":[TD([[makeQuery(id+"F8.imprint","IMPRINT",EDGE,{"derivedFrom":sQuery(id+"F8.wireOp",EDGE,"E760")}),1.0]])]});
            extrude(context, id + "F9", {"entities" : qUnion([Q0, Q1, Q2, Q3, Q4, Q5, Q6, Q7]), "operationType" : NewBodyOperationType.REMOVE, "endBound" : BoundingType.THROUGH_ALL, "oppositeDirection" : true, "depth" : 25.4 * mm});
        }
    });
